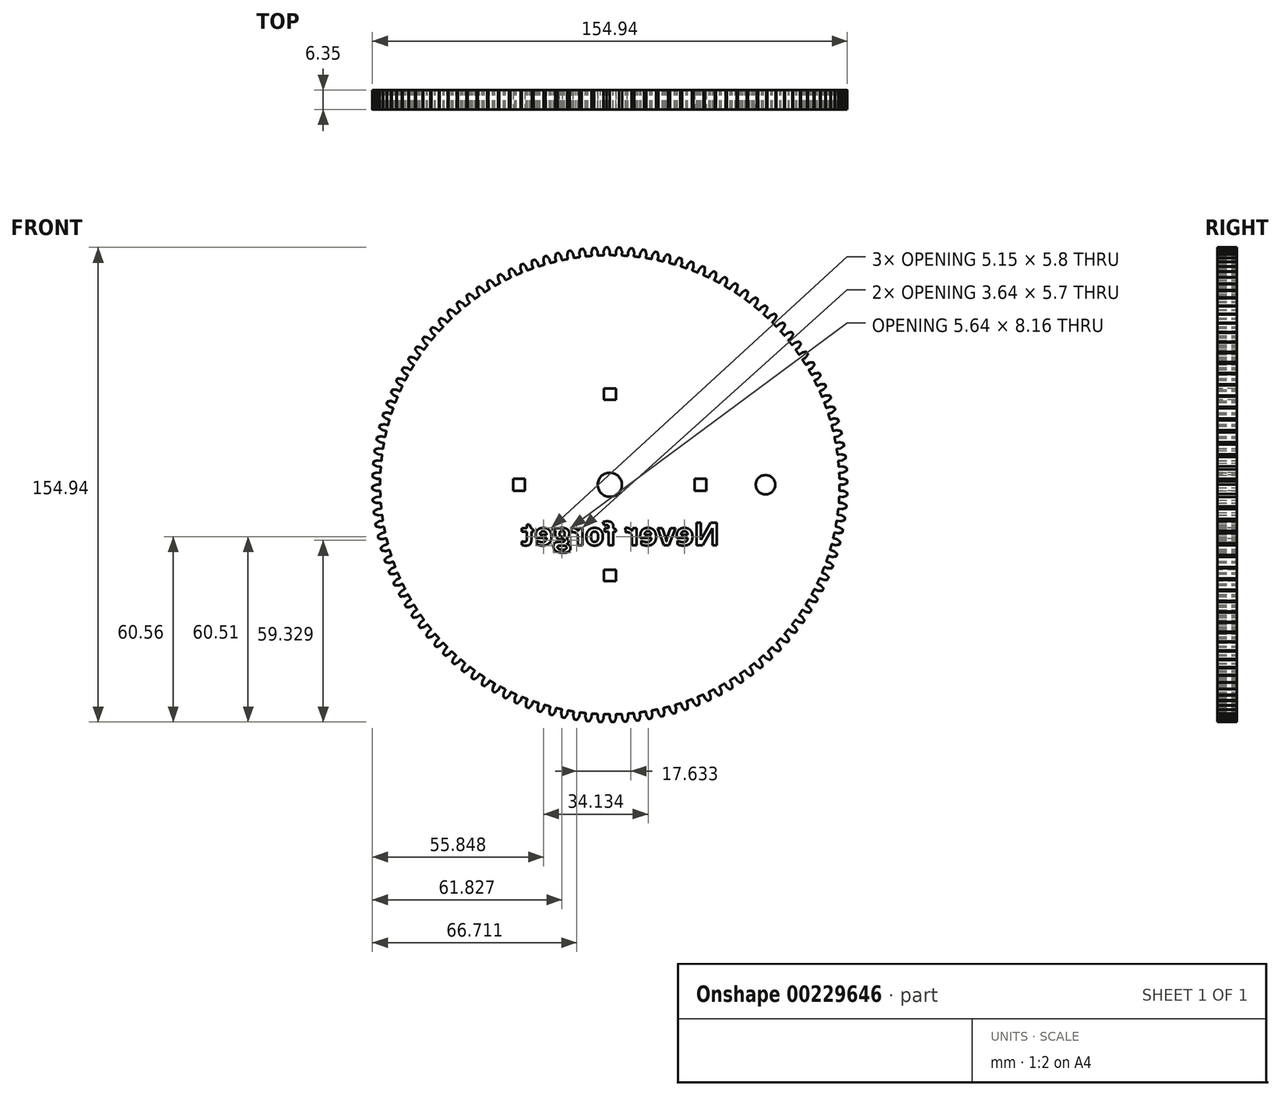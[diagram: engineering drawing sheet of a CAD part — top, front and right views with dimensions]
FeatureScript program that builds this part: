
annotation { "Feature Type Name" : "Feature", "Feature Type Description" : "" }
export const myFeature = defineFeature(function(context is Context, id is Id, definition is map)
    precondition{}
    {
        {
            var Q0;
            Q0=qCreatedBy(makeId("Front.planeOp"),FACE);
            var sketch = newSketch(context, id + "F0", { "sketchPlane" : qUnion([Q0])});
            skArc(sketch, "E0", {"start": v(-2.11, 74.9) * mm, "mid": v(-2.94, 74.87) * mm, "end": v(-3.77, 74.84) * mm});
            skArc(sketch, "E1.trimOffspring", {"start": v(-0.01, 76.23) * mm, "mid": v(-0.25, 76.8) * mm, "end": v(-0.5, 77.38) * mm});
            skLineSegment(sketch, "E2", {"start": v(-0.64, 77.47) * mm, "end": v(-1.01, 77.46) * mm});
            skLineSegment(sketch, "E3", {"start": v(0, 76.17) * mm, "end": v(0, 75.08) * mm});
            skLineSegment(sketch, "E4.MirrorCS", {"start": v(-1.39, 77.46) * mm, "end": v(-1.01, 77.46) * mm});
            skArc(sketch, "E5.MirrorCS", {"start": v(-1.99, 76.2) * mm, "mid": v(-1.77, 76.79) * mm, "end": v(-1.53, 77.37) * mm});
            skLineSegment(sketch, "E6.MirrorCS", {"start": v(-2, 76.15) * mm, "end": v(-1.97, 75.06) * mm});
            skPoint(sketch, "E7.visualSharp", {"position": v(-1.96, 74.9) * mm});
            skArc(sketch, "E8.filletArc", {"start": v(-2.11, 74.9) * mm, "mid": v(-2, 74.95) * mm, "end": v(-1.97, 75.06) * mm});
            skPoint(sketch, "E9.visualSharp", {"position": v(0, 74.93) * mm});
            skArc(sketch, "E9.filletArc", {"start": v(0, 75.08) * mm, "mid": v(0.04, 74.97) * mm, "end": v(0.15, 74.93) * mm});
            skPoint(sketch, "E10.visualSharp", {"position": v(0, 76.2) * mm});
            skArc(sketch, "E10.filletArc", {"start": v(0, 76.17) * mm, "mid": v(0, 76.2) * mm, "end": v(-0.01, 76.23) * mm});
            skPoint(sketch, "E11.visualSharp", {"position": v(-2, 76.17) * mm});
            skArc(sketch, "E11.filletArc", {"start": v(-1.99, 76.2) * mm, "mid": v(-2, 76.17) * mm, "end": v(-2, 76.15) * mm});
            skPoint(sketch, "E12.visualSharp", {"position": v(-1.49, 77.46) * mm});
            skArc(sketch, "E12.filletArc", {"start": v(-1.39, 77.46) * mm, "mid": v(-1.47, 77.43) * mm, "end": v(-1.53, 77.37) * mm});
            skPoint(sketch, "E13.visualSharp", {"position": v(-0.54, 77.47) * mm});
            skArc(sketch, "E13.filletArc", {"start": v(-0.5, 77.38) * mm, "mid": v(-0.56, 77.44) * mm, "end": v(-0.64, 77.47) * mm});
            skArc(sketch, "E14.1.0", {"start": v(-6.03, 74.69) * mm, "mid": v(-5.93, 74.74) * mm, "end": v(-5.9, 74.85) * mm});
            skLineSegment(sketch, "E14.1.1", {"start": v(-5.98, 75.94) * mm, "end": v(-5.9, 74.85) * mm});
            skArc(sketch, "E14.1.2", {"start": v(-5.97, 76) * mm, "mid": v(-5.78, 76.59) * mm, "end": v(-5.57, 77.18) * mm});
            skArc(sketch, "E14.1.3", {"start": v(-5.44, 77.28) * mm, "mid": v(-5.52, 77.25) * mm, "end": v(-5.57, 77.18) * mm});
            skLineSegment(sketch, "E14.1.4", {"start": v(-5.44, 77.28) * mm, "end": v(-5.07, 77.3) * mm});
            skLineSegment(sketch, "E14.1.5", {"start": v(-4.7, 77.33) * mm, "end": v(-5.07, 77.3) * mm});
            skArc(sketch, "E14.1.6", {"start": v(-4.55, 77.25) * mm, "mid": v(-4.6, 77.3) * mm, "end": v(-4.7, 77.33) * mm});
            skArc(sketch, "E14.1.7", {"start": v(-4, 76.12) * mm, "mid": v(-4.26, 76.69) * mm, "end": v(-4.55, 77.25) * mm});
            skLineSegment(sketch, "E14.1.8", {"start": v(-3.99, 76.07) * mm, "end": v(-3.93, 74.98) * mm});
            skArc(sketch, "E14.1.9", {"start": v(-3.93, 74.98) * mm, "mid": v(-3.88, 74.87) * mm, "end": v(-3.77, 74.84) * mm});
            skArc(sketch, "E14.2.0", {"start": v(-9.93, 74.27) * mm, "mid": v(-9.83, 74.33) * mm, "end": v(-9.8, 74.44) * mm});
            skLineSegment(sketch, "E14.2.1", {"start": v(-9.94, 75.52) * mm, "end": v(-9.8, 74.44) * mm});
            skArc(sketch, "E14.2.2", {"start": v(-9.94, 75.58) * mm, "mid": v(-9.78, 76.18) * mm, "end": v(-9.6, 76.78) * mm});
            skArc(sketch, "E14.2.3", {"start": v(-9.48, 76.89) * mm, "mid": v(-9.56, 76.85) * mm, "end": v(-9.6, 76.78) * mm});
            skLineSegment(sketch, "E14.2.4", {"start": v(-9.48, 76.89) * mm, "end": v(-9.1, 76.93) * mm});
            skLineSegment(sketch, "E14.2.5", {"start": v(-8.73, 76.98) * mm, "end": v(-9.1, 76.93) * mm});
            skArc(sketch, "E14.2.6", {"start": v(-8.59, 76.9) * mm, "mid": v(-8.65, 76.96) * mm, "end": v(-8.73, 76.98) * mm});
            skArc(sketch, "E14.2.7", {"start": v(-7.98, 75.8) * mm, "mid": v(-8.27, 76.36) * mm, "end": v(-8.59, 76.9) * mm});
            skLineSegment(sketch, "E14.2.8", {"start": v(-7.96, 75.75) * mm, "end": v(-7.85, 74.67) * mm});
            skArc(sketch, "E14.2.9", {"start": v(-7.85, 74.67) * mm, "mid": v(-7.8, 74.57) * mm, "end": v(-7.68, 74.54) * mm});
            skArc(sketch, "E14.3.0", {"start": v(-13.8, 73.65) * mm, "mid": v(-13.7, 73.71) * mm, "end": v(-13.68, 73.82) * mm});
            skLineSegment(sketch, "E14.3.1", {"start": v(-13.88, 74.9) * mm, "end": v(-13.68, 73.82) * mm});
            skArc(sketch, "E14.3.2", {"start": v(-13.88, 74.95) * mm, "mid": v(-13.76, 75.57) * mm, "end": v(-13.6, 76.17) * mm});
            skArc(sketch, "E14.3.3", {"start": v(-13.49, 76.29) * mm, "mid": v(-13.57, 76.25) * mm, "end": v(-13.6, 76.17) * mm});
            skLineSegment(sketch, "E14.3.4", {"start": v(-13.49, 76.29) * mm, "end": v(-13.12, 76.35) * mm});
            skLineSegment(sketch, "E14.3.5", {"start": v(-12.75, 76.41) * mm, "end": v(-13.12, 76.35) * mm});
            skArc(sketch, "E14.3.6", {"start": v(-12.6, 76.35) * mm, "mid": v(-12.66, 76.4) * mm, "end": v(-12.75, 76.41) * mm});
            skArc(sketch, "E14.3.7", {"start": v(-11.93, 75.29) * mm, "mid": v(-12.26, 75.82) * mm, "end": v(-12.6, 76.35) * mm});
            skLineSegment(sketch, "E14.3.8", {"start": v(-11.92, 75.23) * mm, "end": v(-11.75, 74.16) * mm});
            skArc(sketch, "E14.3.9", {"start": v(-11.75, 74.16) * mm, "mid": v(-11.68, 74.06) * mm, "end": v(-11.57, 74.03) * mm});
            skArc(sketch, "E14.4.0", {"start": v(-17.64, 72.82) * mm, "mid": v(-17.55, 72.9) * mm, "end": v(-17.53, 73) * mm});
            skLineSegment(sketch, "E14.4.1", {"start": v(-17.78, 74.07) * mm, "end": v(-17.53, 73) * mm});
            skArc(sketch, "E14.4.2", {"start": v(-17.78, 74.12) * mm, "mid": v(-17.7, 74.74) * mm, "end": v(-17.58, 75.36) * mm});
            skArc(sketch, "E14.4.3", {"start": v(-17.46, 75.48) * mm, "mid": v(-17.54, 75.43) * mm, "end": v(-17.58, 75.36) * mm});
            skLineSegment(sketch, "E14.4.4", {"start": v(-17.46, 75.48) * mm, "end": v(-17.1, 75.56) * mm});
            skLineSegment(sketch, "E14.4.5", {"start": v(-16.73, 75.64) * mm, "end": v(-17.1, 75.56) * mm});
            skArc(sketch, "E14.4.6", {"start": v(-16.58, 75.58) * mm, "mid": v(-16.65, 75.64) * mm, "end": v(-16.73, 75.64) * mm});
            skArc(sketch, "E14.4.7", {"start": v(-15.86, 74.56) * mm, "mid": v(-16.2, 75.08) * mm, "end": v(-16.58, 75.58) * mm});
            skLineSegment(sketch, "E14.4.8", {"start": v(-15.84, 74.5) * mm, "end": v(-15.61, 73.44) * mm});
            skArc(sketch, "E14.4.9", {"start": v(-15.61, 73.44) * mm, "mid": v(-15.54, 73.35) * mm, "end": v(-15.43, 73.32) * mm});
            skArc(sketch, "E14.5.0", {"start": v(-21.43, 71.8) * mm, "mid": v(-21.34, 71.87) * mm, "end": v(-21.32, 72) * mm});
            skLineSegment(sketch, "E14.5.1", {"start": v(-21.63, 73.03) * mm, "end": v(-21.32, 72) * mm});
            skArc(sketch, "E14.5.2", {"start": v(-21.64, 73.1) * mm, "mid": v(-21.58, 73.71) * mm, "end": v(-21.5, 74.33) * mm});
            skArc(sketch, "E14.5.3", {"start": v(-21.39, 74.46) * mm, "mid": v(-21.46, 74.41) * mm, "end": v(-21.5, 74.33) * mm});
            skLineSegment(sketch, "E14.5.4", {"start": v(-21.39, 74.46) * mm, "end": v(-21.03, 74.56) * mm});
            skLineSegment(sketch, "E14.5.5", {"start": v(-20.67, 74.66) * mm, "end": v(-21.03, 74.56) * mm});
            skArc(sketch, "E14.5.6", {"start": v(-20.5, 74.61) * mm, "mid": v(-20.58, 74.66) * mm, "end": v(-20.67, 74.66) * mm});
            skArc(sketch, "E14.5.7", {"start": v(-19.74, 73.63) * mm, "mid": v(-20.12, 74.13) * mm, "end": v(-20.5, 74.61) * mm});
            skLineSegment(sketch, "E14.5.8", {"start": v(-19.71, 73.58) * mm, "end": v(-19.43, 72.52) * mm});
            skArc(sketch, "E14.5.9", {"start": v(-19.43, 72.52) * mm, "mid": v(-19.36, 72.43) * mm, "end": v(-19.25, 72.42) * mm});
            skArc(sketch, "E14.6.0", {"start": v(-25.16, 70.58) * mm, "mid": v(-25.07, 70.66) * mm, "end": v(-25.06, 70.78) * mm});
            skLineSegment(sketch, "E14.6.1", {"start": v(-25.43, 71.8) * mm, "end": v(-25.06, 70.78) * mm});
            skArc(sketch, "E14.6.2", {"start": v(-25.44, 71.86) * mm, "mid": v(-25.4, 72.48) * mm, "end": v(-25.36, 73.1) * mm});
            skArc(sketch, "E14.6.3", {"start": v(-25.26, 73.24) * mm, "mid": v(-25.33, 73.19) * mm, "end": v(-25.36, 73.1) * mm});
            skLineSegment(sketch, "E14.6.4", {"start": v(-25.26, 73.24) * mm, "end": v(-24.9, 73.36) * mm});
            skLineSegment(sketch, "E14.6.5", {"start": v(-24.55, 73.48) * mm, "end": v(-24.9, 73.36) * mm});
            skArc(sketch, "E14.6.6", {"start": v(-24.39, 73.44) * mm, "mid": v(-24.46, 73.48) * mm, "end": v(-24.55, 73.48) * mm});
            skArc(sketch, "E14.6.7", {"start": v(-23.57, 72.5) * mm, "mid": v(-23.97, 72.97) * mm, "end": v(-24.39, 73.44) * mm});
            skLineSegment(sketch, "E14.6.8", {"start": v(-23.54, 72.44) * mm, "end": v(-23.2, 71.4) * mm});
            skArc(sketch, "E14.6.9", {"start": v(-23.2, 71.4) * mm, "mid": v(-23.13, 71.32) * mm, "end": v(-23, 71.3) * mm});
            skArc(sketch, "E14.7.0", {"start": v(-28.81, 69.17) * mm, "mid": v(-28.73, 69.25) * mm, "end": v(-28.73, 69.37) * mm});
            skLineSegment(sketch, "E14.7.1", {"start": v(-29.15, 70.37) * mm, "end": v(-28.73, 69.37) * mm});
            skArc(sketch, "E14.7.2", {"start": v(-29.16, 70.43) * mm, "mid": v(-29.17, 71.05) * mm, "end": v(-29.15, 71.68) * mm});
            skArc(sketch, "E14.7.3", {"start": v(-29.06, 71.82) * mm, "mid": v(-29.12, 71.76) * mm, "end": v(-29.15, 71.68) * mm});
            skLineSegment(sketch, "E14.7.4", {"start": v(-29.06, 71.82) * mm, "end": v(-28.7, 71.96) * mm});
            skLineSegment(sketch, "E14.7.5", {"start": v(-28.36, 72.1) * mm, "end": v(-28.7, 71.96) * mm});
            skArc(sketch, "E14.7.6", {"start": v(-28.2, 72.06) * mm, "mid": v(-28.27, 72.1) * mm, "end": v(-28.36, 72.1) * mm});
            skArc(sketch, "E14.7.7", {"start": v(-27.33, 71.16) * mm, "mid": v(-27.75, 71.62) * mm, "end": v(-28.2, 72.06) * mm});
            skLineSegment(sketch, "E14.7.8", {"start": v(-27.3, 71.11) * mm, "end": v(-26.9, 70.1) * mm});
            skArc(sketch, "E14.7.9", {"start": v(-26.9, 70.1) * mm, "mid": v(-26.83, 70.01) * mm, "end": v(-26.71, 70) * mm});
            skArc(sketch, "E14.8.0", {"start": v(-32.4, 67.57) * mm, "mid": v(-32.32, 67.65) * mm, "end": v(-32.32, 67.77) * mm});
            skLineSegment(sketch, "E14.8.1", {"start": v(-32.8, 68.75) * mm, "end": v(-32.32, 67.77) * mm});
            skArc(sketch, "E14.8.2", {"start": v(-32.8, 68.8) * mm, "mid": v(-32.84, 69.43) * mm, "end": v(-32.86, 70.06) * mm});
            skArc(sketch, "E14.8.3", {"start": v(-32.77, 70.2) * mm, "mid": v(-32.84, 70.14) * mm, "end": v(-32.86, 70.06) * mm});
            skLineSegment(sketch, "E14.8.4", {"start": v(-32.77, 70.2) * mm, "end": v(-32.43, 70.36) * mm});
            skLineSegment(sketch, "E14.8.5", {"start": v(-32.1, 70.51) * mm, "end": v(-32.43, 70.36) * mm});
            skArc(sketch, "E14.8.6", {"start": v(-31.93, 70.49) * mm, "mid": v(-32, 70.52) * mm, "end": v(-32.1, 70.51) * mm});
            skArc(sketch, "E14.8.7", {"start": v(-31.01, 69.63) * mm, "mid": v(-31.46, 70.07) * mm, "end": v(-31.93, 70.49) * mm});
            skLineSegment(sketch, "E14.8.8", {"start": v(-30.98, 69.59) * mm, "end": v(-30.54, 68.6) * mm});
            skArc(sketch, "E14.8.9", {"start": v(-30.54, 68.6) * mm, "mid": v(-30.45, 68.51) * mm, "end": v(-30.34, 68.51) * mm});
            skArc(sketch, "E14.9.0", {"start": v(-35.89, 65.78) * mm, "mid": v(-35.81, 65.87) * mm, "end": v(-35.83, 65.98) * mm});
            skLineSegment(sketch, "E14.9.1", {"start": v(-36.35, 66.94) * mm, "end": v(-35.83, 65.98) * mm});
            skArc(sketch, "E14.9.2", {"start": v(-36.36, 67) * mm, "mid": v(-36.43, 67.62) * mm, "end": v(-36.48, 68.24) * mm});
            skArc(sketch, "E14.9.3", {"start": v(-36.4, 68.38) * mm, "mid": v(-36.46, 68.32) * mm, "end": v(-36.48, 68.24) * mm});
            skLineSegment(sketch, "E14.9.4", {"start": v(-36.4, 68.38) * mm, "end": v(-36.07, 68.56) * mm});
            skLineSegment(sketch, "E14.9.5", {"start": v(-35.74, 68.73) * mm, "end": v(-36.07, 68.56) * mm});
            skArc(sketch, "E14.9.6", {"start": v(-35.57, 68.72) * mm, "mid": v(-35.65, 68.75) * mm, "end": v(-35.74, 68.73) * mm});
            skArc(sketch, "E14.9.7", {"start": v(-34.62, 67.91) * mm, "mid": v(-35.09, 68.32) * mm, "end": v(-35.57, 68.72) * mm});
            skLineSegment(sketch, "E14.9.8", {"start": v(-34.58, 67.87) * mm, "end": v(-34.09, 66.9) * mm});
            skArc(sketch, "E14.9.9", {"start": v(-34.09, 66.9) * mm, "mid": v(-34, 66.82) * mm, "end": v(-33.88, 66.83) * mm});
            skArc(sketch, "E14.10.0", {"start": v(-39.28, 63.8) * mm, "mid": v(-39.21, 63.9) * mm, "end": v(-39.23, 64.02) * mm});
            skLineSegment(sketch, "E14.10.1", {"start": v(-39.8, 64.95) * mm, "end": v(-39.23, 64.02) * mm});
            skArc(sketch, "E14.10.2", {"start": v(-39.82, 65) * mm, "mid": v(-39.92, 65.62) * mm, "end": v(-40, 66.24) * mm});
            skArc(sketch, "E14.10.3", {"start": v(-39.93, 66.39) * mm, "mid": v(-39.99, 66.32) * mm, "end": v(-40, 66.24) * mm});
            skLineSegment(sketch, "E14.10.4", {"start": v(-39.93, 66.39) * mm, "end": v(-39.61, 66.58) * mm});
            skLineSegment(sketch, "E14.10.5", {"start": v(-39.29, 66.77) * mm, "end": v(-39.61, 66.58) * mm});
            skArc(sketch, "E14.10.6", {"start": v(-39.12, 66.76) * mm, "mid": v(-39.2, 66.8) * mm, "end": v(-39.29, 66.77) * mm});
            skArc(sketch, "E14.10.7", {"start": v(-38.12, 66) * mm, "mid": v(-38.62, 66.4) * mm, "end": v(-39.12, 66.76) * mm});
            skLineSegment(sketch, "E14.10.8", {"start": v(-38.09, 65.97) * mm, "end": v(-37.54, 65.02) * mm});
            skArc(sketch, "E14.10.9", {"start": v(-37.54, 65.02) * mm, "mid": v(-37.45, 64.95) * mm, "end": v(-37.33, 64.97) * mm});
            skArc(sketch, "E14.11.0", {"start": v(-42.57, 61.67) * mm, "mid": v(-42.5, 61.76) * mm, "end": v(-42.53, 61.88) * mm});
            skLineSegment(sketch, "E14.11.1", {"start": v(-43.14, 62.78) * mm, "end": v(-42.53, 61.88) * mm});
            skArc(sketch, "E14.11.2", {"start": v(-43.17, 62.83) * mm, "mid": v(-43.3, 63.44) * mm, "end": v(-43.42, 64.05) * mm});
            skArc(sketch, "E14.11.3", {"start": v(-43.35, 64.2) * mm, "mid": v(-43.4, 64.14) * mm, "end": v(-43.42, 64.05) * mm});
            skLineSegment(sketch, "E14.11.4", {"start": v(-43.35, 64.2) * mm, "end": v(-43.04, 64.42) * mm});
            skLineSegment(sketch, "E14.11.5", {"start": v(-42.73, 64.62) * mm, "end": v(-43.04, 64.42) * mm});
            skArc(sketch, "E14.11.6", {"start": v(-42.56, 64.62) * mm, "mid": v(-42.65, 64.65) * mm, "end": v(-42.73, 64.62) * mm});
            skArc(sketch, "E14.11.7", {"start": v(-41.52, 63.92) * mm, "mid": v(-42.04, 64.28) * mm, "end": v(-42.56, 64.62) * mm});
            skLineSegment(sketch, "E14.11.8", {"start": v(-41.49, 63.88) * mm, "end": v(-40.9, 62.97) * mm});
            skArc(sketch, "E14.11.9", {"start": v(-40.9, 62.97) * mm, "mid": v(-40.8, 62.9) * mm, "end": v(-40.68, 62.92) * mm});
            skArc(sketch, "E14.12.0", {"start": v(-45.74, 59.35) * mm, "mid": v(-45.68, 59.45) * mm, "end": v(-45.7, 59.57) * mm});
            skLineSegment(sketch, "E14.12.1", {"start": v(-46.37, 60.43) * mm, "end": v(-45.7, 59.57) * mm});
            skArc(sketch, "E14.12.2", {"start": v(-46.4, 60.48) * mm, "mid": v(-46.56, 61.08) * mm, "end": v(-46.7, 61.7) * mm});
            skArc(sketch, "E14.12.3", {"start": v(-46.65, 61.85) * mm, "mid": v(-46.7, 61.78) * mm, "end": v(-46.7, 61.7) * mm});
            skLineSegment(sketch, "E14.12.4", {"start": v(-46.65, 61.85) * mm, "end": v(-46.35, 62.07) * mm});
            skLineSegment(sketch, "E14.12.5", {"start": v(-46.05, 62.3) * mm, "end": v(-46.35, 62.07) * mm});
            skArc(sketch, "E14.12.6", {"start": v(-45.89, 62.3) * mm, "mid": v(-45.97, 62.33) * mm, "end": v(-46.05, 62.3) * mm});
            skArc(sketch, "E14.12.7", {"start": v(-44.81, 61.66) * mm, "mid": v(-45.34, 62) * mm, "end": v(-45.89, 62.3) * mm});
            skLineSegment(sketch, "E14.12.8", {"start": v(-44.77, 61.62) * mm, "end": v(-44.13, 60.74) * mm});
            skArc(sketch, "E14.12.9", {"start": v(-44.13, 60.74) * mm, "mid": v(-44.03, 60.68) * mm, "end": v(-43.92, 60.7) * mm});
            skArc(sketch, "E14.13.0", {"start": v(-48.78, 56.88) * mm, "mid": v(-48.73, 56.98) * mm, "end": v(-48.76, 57.1) * mm});
            skLineSegment(sketch, "E14.13.1", {"start": v(-49.47, 57.92) * mm, "end": v(-48.76, 57.1) * mm});
            skArc(sketch, "E14.13.2", {"start": v(-49.5, 57.97) * mm, "mid": v(-49.7, 58.56) * mm, "end": v(-49.87, 59.16) * mm});
            skArc(sketch, "E14.13.3", {"start": v(-49.83, 59.32) * mm, "mid": v(-49.87, 59.25) * mm, "end": v(-49.87, 59.16) * mm});
            skLineSegment(sketch, "E14.13.4", {"start": v(-49.83, 59.32) * mm, "end": v(-49.54, 59.56) * mm});
            skLineSegment(sketch, "E14.13.5", {"start": v(-49.25, 59.8) * mm, "end": v(-49.54, 59.56) * mm});
            skArc(sketch, "E14.13.6", {"start": v(-49.08, 59.82) * mm, "mid": v(-49.17, 59.84) * mm, "end": v(-49.25, 59.8) * mm});
            skArc(sketch, "E14.13.7", {"start": v(-47.98, 59.23) * mm, "mid": v(-48.53, 59.54) * mm, "end": v(-49.08, 59.82) * mm});
            skLineSegment(sketch, "E14.13.8", {"start": v(-47.94, 59.2) * mm, "end": v(-47.25, 58.35) * mm});
            skArc(sketch, "E14.13.9", {"start": v(-47.25, 58.35) * mm, "mid": v(-47.15, 58.3) * mm, "end": v(-47.04, 58.33) * mm});
            skArc(sketch, "E14.14.0", {"start": v(-51.69, 54.25) * mm, "mid": v(-51.64, 54.35) * mm, "end": v(-51.68, 54.46) * mm});
            skLineSegment(sketch, "E14.14.1", {"start": v(-52.43, 55.25) * mm, "end": v(-51.68, 54.46) * mm});
            skArc(sketch, "E14.14.2", {"start": v(-52.46, 55.3) * mm, "mid": v(-52.7, 55.88) * mm, "end": v(-52.9, 56.47) * mm});
            skArc(sketch, "E14.14.3", {"start": v(-52.86, 56.63) * mm, "mid": v(-52.9, 56.56) * mm, "end": v(-52.9, 56.47) * mm});
            skLineSegment(sketch, "E14.14.4", {"start": v(-52.86, 56.63) * mm, "end": v(-52.59, 56.89) * mm});
            skLineSegment(sketch, "E14.14.5", {"start": v(-52.31, 57.14) * mm, "end": v(-52.59, 56.89) * mm});
            skArc(sketch, "E14.14.6", {"start": v(-52.15, 57.17) * mm, "mid": v(-52.23, 57.18) * mm, "end": v(-52.31, 57.14) * mm});
            skArc(sketch, "E14.14.7", {"start": v(-51.01, 56.64) * mm, "mid": v(-51.58, 56.91) * mm, "end": v(-52.15, 57.17) * mm});
            skLineSegment(sketch, "E14.14.8", {"start": v(-50.97, 56.6) * mm, "end": v(-50.24, 55.8) * mm});
            skArc(sketch, "E14.14.9", {"start": v(-50.24, 55.8) * mm, "mid": v(-50.13, 55.75) * mm, "end": v(-50.02, 55.79) * mm});
            skArc(sketch, "E14.15.0", {"start": v(-54.46, 51.47) * mm, "mid": v(-54.42, 51.58) * mm, "end": v(-54.46, 51.68) * mm});
            skLineSegment(sketch, "E14.15.1", {"start": v(-55.25, 52.43) * mm, "end": v(-54.46, 51.68) * mm});
            skArc(sketch, "E14.15.2", {"start": v(-55.29, 52.48) * mm, "mid": v(-55.54, 53.05) * mm, "end": v(-55.78, 53.63) * mm});
            skArc(sketch, "E14.15.3", {"start": v(-55.75, 53.79) * mm, "mid": v(-55.8, 53.71) * mm, "end": v(-55.78, 53.63) * mm});
            skLineSegment(sketch, "E14.15.4", {"start": v(-55.75, 53.79) * mm, "end": v(-55.5, 54.06) * mm});
            skLineSegment(sketch, "E14.15.5", {"start": v(-55.23, 54.33) * mm, "end": v(-55.5, 54.06) * mm});
            skArc(sketch, "E14.15.6", {"start": v(-55.07, 54.36) * mm, "mid": v(-55.15, 54.37) * mm, "end": v(-55.23, 54.33) * mm});
            skArc(sketch, "E14.15.7", {"start": v(-53.9, 53.9) * mm, "mid": v(-54.48, 54.14) * mm, "end": v(-55.07, 54.36) * mm});
            skLineSegment(sketch, "E14.15.8", {"start": v(-53.86, 53.86) * mm, "end": v(-53.1, 53.1) * mm});
            skArc(sketch, "E14.15.9", {"start": v(-53.1, 53.1) * mm, "mid": v(-52.98, 53.05) * mm, "end": v(-52.88, 53.1) * mm});
            skArc(sketch, "E14.16.0", {"start": v(-57.08, 48.55) * mm, "mid": v(-57.04, 48.66) * mm, "end": v(-57.1, 48.76) * mm});
            skLineSegment(sketch, "E14.16.1", {"start": v(-57.92, 49.47) * mm, "end": v(-57.1, 48.76) * mm});
            skArc(sketch, "E14.16.2", {"start": v(-57.96, 49.51) * mm, "mid": v(-58.25, 50.07) * mm, "end": v(-58.52, 50.63) * mm});
            skArc(sketch, "E14.16.3", {"start": v(-58.5, 50.8) * mm, "mid": v(-58.53, 50.72) * mm, "end": v(-58.52, 50.63) * mm});
            skLineSegment(sketch, "E14.16.4", {"start": v(-58.5, 50.8) * mm, "end": v(-58.25, 51.08) * mm});
            skLineSegment(sketch, "E14.16.5", {"start": v(-58, 51.36) * mm, "end": v(-58.25, 51.08) * mm});
            skArc(sketch, "E14.16.6", {"start": v(-57.84, 51.4) * mm, "mid": v(-57.92, 51.4) * mm, "end": v(-58, 51.36) * mm});
            skArc(sketch, "E14.16.7", {"start": v(-56.65, 51) * mm, "mid": v(-57.24, 51.21) * mm, "end": v(-57.84, 51.4) * mm});
            skLineSegment(sketch, "E14.16.8", {"start": v(-56.6, 50.97) * mm, "end": v(-55.8, 50.24) * mm});
            skArc(sketch, "E14.16.9", {"start": v(-55.8, 50.24) * mm, "mid": v(-55.69, 50.2) * mm, "end": v(-55.58, 50.25) * mm});
            skArc(sketch, "E14.17.0", {"start": v(-59.54, 45.5) * mm, "mid": v(-59.5, 45.6) * mm, "end": v(-59.57, 45.7) * mm});
            skLineSegment(sketch, "E14.17.1", {"start": v(-60.43, 46.37) * mm, "end": v(-59.57, 45.7) * mm});
            skArc(sketch, "E14.17.2", {"start": v(-60.47, 46.41) * mm, "mid": v(-60.79, 46.95) * mm, "end": v(-61.08, 47.5) * mm});
            skArc(sketch, "E14.17.3", {"start": v(-61.07, 47.67) * mm, "mid": v(-61.1, 47.59) * mm, "end": v(-61.08, 47.5) * mm});
            skLineSegment(sketch, "E14.17.4", {"start": v(-61.07, 47.67) * mm, "end": v(-60.84, 47.96) * mm});
            skLineSegment(sketch, "E14.17.5", {"start": v(-60.6, 48.26) * mm, "end": v(-60.84, 47.96) * mm});
            skArc(sketch, "E14.17.6", {"start": v(-60.45, 48.3) * mm, "mid": v(-60.54, 48.3) * mm, "end": v(-60.6, 48.26) * mm});
            skArc(sketch, "E14.17.7", {"start": v(-59.25, 47.96) * mm, "mid": v(-59.84, 48.15) * mm, "end": v(-60.45, 48.3) * mm});
            skLineSegment(sketch, "E14.17.8", {"start": v(-59.2, 47.94) * mm, "end": v(-58.35, 47.25) * mm});
            skArc(sketch, "E14.17.9", {"start": v(-58.35, 47.25) * mm, "mid": v(-58.24, 47.22) * mm, "end": v(-58.14, 47.27) * mm});
            skArc(sketch, "E14.18.0", {"start": v(-61.84, 42.32) * mm, "mid": v(-61.81, 42.43) * mm, "end": v(-61.88, 42.53) * mm});
            skLineSegment(sketch, "E14.18.1", {"start": v(-62.78, 43.14) * mm, "end": v(-61.88, 42.53) * mm});
            skArc(sketch, "E14.18.2", {"start": v(-62.81, 43.18) * mm, "mid": v(-63.16, 43.7) * mm, "end": v(-63.49, 44.24) * mm});
            skArc(sketch, "E14.18.3", {"start": v(-63.48, 44.4) * mm, "mid": v(-63.5, 44.32) * mm, "end": v(-63.49, 44.24) * mm});
            skLineSegment(sketch, "E14.18.4", {"start": v(-63.48, 44.4) * mm, "end": v(-63.27, 44.71) * mm});
            skLineSegment(sketch, "E14.18.5", {"start": v(-63.05, 45.02) * mm, "end": v(-63.27, 44.71) * mm});
            skArc(sketch, "E14.18.6", {"start": v(-62.9, 45.08) * mm, "mid": v(-62.98, 45.07) * mm, "end": v(-63.05, 45.02) * mm});
            skArc(sketch, "E14.18.7", {"start": v(-61.67, 44.8) * mm, "mid": v(-62.28, 44.95) * mm, "end": v(-62.9, 45.08) * mm});
            skLineSegment(sketch, "E14.18.8", {"start": v(-61.62, 44.77) * mm, "end": v(-60.74, 44.13) * mm});
            skArc(sketch, "E14.18.9", {"start": v(-60.74, 44.13) * mm, "mid": v(-60.63, 44.1) * mm, "end": v(-60.53, 44.17) * mm});
            skArc(sketch, "E14.19.0", {"start": v(-63.97, 39.02) * mm, "mid": v(-63.95, 39.14) * mm, "end": v(-64.02, 39.23) * mm});
            skLineSegment(sketch, "E14.19.1", {"start": v(-64.95, 39.8) * mm, "end": v(-64.02, 39.23) * mm});
            skArc(sketch, "E14.19.2", {"start": v(-64.99, 39.84) * mm, "mid": v(-65.36, 40.34) * mm, "end": v(-65.72, 40.86) * mm});
            skArc(sketch, "E14.19.3", {"start": v(-65.72, 41.02) * mm, "mid": v(-65.74, 40.94) * mm, "end": v(-65.72, 40.86) * mm});
            skLineSegment(sketch, "E14.19.4", {"start": v(-65.72, 41.02) * mm, "end": v(-65.52, 41.34) * mm});
            skLineSegment(sketch, "E14.19.5", {"start": v(-65.32, 41.66) * mm, "end": v(-65.52, 41.34) * mm});
            skArc(sketch, "E14.19.6", {"start": v(-65.17, 41.72) * mm, "mid": v(-65.25, 41.71) * mm, "end": v(-65.32, 41.66) * mm});
            skArc(sketch, "E14.19.7", {"start": v(-63.93, 41.5) * mm, "mid": v(-64.55, 41.63) * mm, "end": v(-65.17, 41.72) * mm});
            skLineSegment(sketch, "E14.19.8", {"start": v(-63.88, 41.49) * mm, "end": v(-62.97, 40.9) * mm});
            skArc(sketch, "E14.19.9", {"start": v(-62.97, 40.9) * mm, "mid": v(-62.85, 40.87) * mm, "end": v(-62.76, 40.94) * mm});
            skArc(sketch, "E14.20.0", {"start": v(-65.92, 35.62) * mm, "mid": v(-65.91, 35.74) * mm, "end": v(-65.98, 35.83) * mm});
            skLineSegment(sketch, "E14.20.1", {"start": v(-66.94, 36.35) * mm, "end": v(-65.98, 35.83) * mm});
            skArc(sketch, "E14.20.2", {"start": v(-66.98, 36.38) * mm, "mid": v(-67.38, 36.86) * mm, "end": v(-67.76, 37.36) * mm});
            skArc(sketch, "E14.20.3", {"start": v(-67.77, 37.53) * mm, "mid": v(-67.8, 37.44) * mm, "end": v(-67.76, 37.36) * mm});
            skLineSegment(sketch, "E14.20.4", {"start": v(-67.77, 37.53) * mm, "end": v(-67.6, 37.85) * mm});
            skLineSegment(sketch, "E14.20.5", {"start": v(-67.4, 38.18) * mm, "end": v(-67.6, 37.85) * mm});
            skArc(sketch, "E14.20.6", {"start": v(-67.26, 38.26) * mm, "mid": v(-67.35, 38.24) * mm, "end": v(-67.4, 38.18) * mm});
            skArc(sketch, "E14.20.7", {"start": v(-66.02, 38.1) * mm, "mid": v(-66.64, 38.2) * mm, "end": v(-67.26, 38.26) * mm});
            skLineSegment(sketch, "E14.20.8", {"start": v(-65.97, 38.09) * mm, "end": v(-65.02, 37.54) * mm});
            skArc(sketch, "E14.20.9", {"start": v(-65.02, 37.54) * mm, "mid": v(-64.9, 37.53) * mm, "end": v(-64.82, 37.6) * mm});
            skArc(sketch, "E14.21.0", {"start": v(-67.7, 32.12) * mm, "mid": v(-67.7, 32.24) * mm, "end": v(-67.77, 32.32) * mm});
            skLineSegment(sketch, "E14.21.1", {"start": v(-68.75, 32.8) * mm, "end": v(-67.77, 32.32) * mm});
            skArc(sketch, "E14.21.2", {"start": v(-68.8, 32.83) * mm, "mid": v(-69.22, 33.29) * mm, "end": v(-69.63, 33.76) * mm});
            skArc(sketch, "E14.21.3", {"start": v(-69.65, 33.93) * mm, "mid": v(-69.66, 33.84) * mm, "end": v(-69.63, 33.76) * mm});
            skLineSegment(sketch, "E14.21.4", {"start": v(-69.65, 33.93) * mm, "end": v(-69.48, 34.26) * mm});
            skLineSegment(sketch, "E14.21.5", {"start": v(-69.31, 34.6) * mm, "end": v(-69.48, 34.26) * mm});
            skArc(sketch, "E14.21.6", {"start": v(-69.17, 34.68) * mm, "mid": v(-69.26, 34.66) * mm, "end": v(-69.31, 34.6) * mm});
            skArc(sketch, "E14.21.7", {"start": v(-67.92, 34.6) * mm, "mid": v(-68.55, 34.65) * mm, "end": v(-69.17, 34.68) * mm});
            skLineSegment(sketch, "E14.21.8", {"start": v(-67.87, 34.58) * mm, "end": v(-66.9, 34.09) * mm});
            skArc(sketch, "E14.21.9", {"start": v(-66.9, 34.09) * mm, "mid": v(-66.78, 34.08) * mm, "end": v(-66.7, 34.15) * mm});
            skArc(sketch, "E14.22.0", {"start": v(-69.28, 28.53) * mm, "mid": v(-69.28, 28.65) * mm, "end": v(-69.37, 28.73) * mm});
            skLineSegment(sketch, "E14.22.1", {"start": v(-70.37, 29.15) * mm, "end": v(-69.37, 28.73) * mm});
            skArc(sketch, "E14.22.2", {"start": v(-70.42, 29.18) * mm, "mid": v(-70.87, 29.62) * mm, "end": v(-71.3, 30.07) * mm});
            skArc(sketch, "E14.22.3", {"start": v(-71.33, 30.24) * mm, "mid": v(-71.34, 30.15) * mm, "end": v(-71.3, 30.07) * mm});
            skLineSegment(sketch, "E14.22.4", {"start": v(-71.33, 30.24) * mm, "end": v(-71.18, 30.58) * mm});
            skLineSegment(sketch, "E14.22.5", {"start": v(-71.03, 30.93) * mm, "end": v(-71.18, 30.58) * mm});
            skArc(sketch, "E14.22.6", {"start": v(-70.9, 31.02) * mm, "mid": v(-70.97, 31) * mm, "end": v(-71.03, 30.93) * mm});
            skArc(sketch, "E14.22.7", {"start": v(-69.64, 31) * mm, "mid": v(-70.27, 31.02) * mm, "end": v(-70.9, 31.02) * mm});
            skLineSegment(sketch, "E14.22.8", {"start": v(-69.59, 30.98) * mm, "end": v(-68.6, 30.54) * mm});
            skArc(sketch, "E14.22.9", {"start": v(-68.6, 30.54) * mm, "mid": v(-68.47, 30.54) * mm, "end": v(-68.39, 30.62) * mm});
            skArc(sketch, "E14.23.0", {"start": v(-70.68, 24.87) * mm, "mid": v(-70.69, 24.99) * mm, "end": v(-70.78, 25.06) * mm});
            skLineSegment(sketch, "E14.23.1", {"start": v(-71.8, 25.43) * mm, "end": v(-70.78, 25.06) * mm});
            skArc(sketch, "E14.23.2", {"start": v(-71.85, 25.45) * mm, "mid": v(-72.32, 25.87) * mm, "end": v(-72.77, 26.3) * mm});
            skArc(sketch, "E14.23.3", {"start": v(-72.81, 26.46) * mm, "mid": v(-72.82, 26.38) * mm, "end": v(-72.77, 26.3) * mm});
            skLineSegment(sketch, "E14.23.4", {"start": v(-72.81, 26.46) * mm, "end": v(-72.68, 26.81) * mm});
            skLineSegment(sketch, "E14.23.5", {"start": v(-72.55, 27.17) * mm, "end": v(-72.68, 26.81) * mm});
            skArc(sketch, "E14.23.6", {"start": v(-72.42, 27.26) * mm, "mid": v(-72.5, 27.23) * mm, "end": v(-72.55, 27.17) * mm});
            skArc(sketch, "E14.23.7", {"start": v(-71.17, 27.3) * mm, "mid": v(-71.8, 27.3) * mm, "end": v(-72.42, 27.26) * mm});
            skLineSegment(sketch, "E14.23.8", {"start": v(-71.11, 27.3) * mm, "end": v(-70.1, 26.9) * mm});
            skArc(sketch, "E14.23.9", {"start": v(-70.1, 26.9) * mm, "mid": v(-69.98, 26.91) * mm, "end": v(-69.9, 27) * mm});
            skArc(sketch, "E14.24.0", {"start": v(-71.89, 21.14) * mm, "mid": v(-71.9, 21.25) * mm, "end": v(-72, 21.32) * mm});
            skLineSegment(sketch, "E14.24.1", {"start": v(-73.03, 21.63) * mm, "end": v(-72, 21.32) * mm});
            skArc(sketch, "E14.24.2", {"start": v(-73.08, 21.66) * mm, "mid": v(-73.57, 22.05) * mm, "end": v(-74.05, 22.46) * mm});
            skArc(sketch, "E14.24.3", {"start": v(-74.1, 22.61) * mm, "mid": v(-74.1, 22.53) * mm, "end": v(-74.05, 22.46) * mm});
            skLineSegment(sketch, "E14.24.4", {"start": v(-74.1, 22.61) * mm, "end": v(-73.99, 22.97) * mm});
            skLineSegment(sketch, "E14.24.5", {"start": v(-73.87, 23.33) * mm, "end": v(-73.99, 22.97) * mm});
            skArc(sketch, "E14.24.6", {"start": v(-73.75, 23.44) * mm, "mid": v(-73.83, 23.4) * mm, "end": v(-73.87, 23.33) * mm});
            skArc(sketch, "E14.24.7", {"start": v(-72.5, 23.55) * mm, "mid": v(-73.12, 23.5) * mm, "end": v(-73.75, 23.44) * mm});
            skLineSegment(sketch, "E14.24.8", {"start": v(-72.44, 23.54) * mm, "end": v(-71.4, 23.2) * mm});
            skArc(sketch, "E14.24.9", {"start": v(-71.4, 23.2) * mm, "mid": v(-71.3, 23.21) * mm, "end": v(-71.22, 23.3) * mm});
            skArc(sketch, "E14.25.0", {"start": v(-72.9, 17.34) * mm, "mid": v(-72.91, 17.46) * mm, "end": v(-73, 17.53) * mm});
            skLineSegment(sketch, "E14.25.1", {"start": v(-74.07, 17.78) * mm, "end": v(-73, 17.53) * mm});
            skArc(sketch, "E14.25.2", {"start": v(-74.12, 17.8) * mm, "mid": v(-74.63, 18.17) * mm, "end": v(-75.12, 18.55) * mm});
            skArc(sketch, "E14.25.3", {"start": v(-75.18, 18.7) * mm, "mid": v(-75.17, 18.62) * mm, "end": v(-75.12, 18.55) * mm});
            skLineSegment(sketch, "E14.25.4", {"start": v(-75.18, 18.7) * mm, "end": v(-75.09, 19.07) * mm});
            skLineSegment(sketch, "E14.25.5", {"start": v(-75, 19.43) * mm, "end": v(-75.09, 19.07) * mm});
            skArc(sketch, "E14.25.6", {"start": v(-74.87, 19.54) * mm, "mid": v(-74.95, 19.5) * mm, "end": v(-75, 19.43) * mm});
            skArc(sketch, "E14.25.7", {"start": v(-73.63, 19.72) * mm, "mid": v(-74.25, 19.64) * mm, "end": v(-74.87, 19.54) * mm});
            skLineSegment(sketch, "E14.25.8", {"start": v(-73.58, 19.71) * mm, "end": v(-72.52, 19.43) * mm});
            skArc(sketch, "E14.25.9", {"start": v(-72.52, 19.43) * mm, "mid": v(-72.4, 19.45) * mm, "end": v(-72.34, 19.54) * mm});
            skArc(sketch, "E14.26.0", {"start": v(-73.7, 13.5) * mm, "mid": v(-73.73, 13.62) * mm, "end": v(-73.82, 13.68) * mm});
            skLineSegment(sketch, "E14.26.1", {"start": v(-74.9, 13.88) * mm, "end": v(-73.82, 13.68) * mm});
            skArc(sketch, "E14.26.2", {"start": v(-74.95, 13.9) * mm, "mid": v(-75.48, 14.24) * mm, "end": v(-76, 14.6) * mm});
            skArc(sketch, "E14.26.3", {"start": v(-76.05, 14.75) * mm, "mid": v(-76.05, 14.66) * mm, "end": v(-76, 14.6) * mm});
            skLineSegment(sketch, "E14.26.4", {"start": v(-76.05, 14.75) * mm, "end": v(-75.98, 15.11) * mm});
            skLineSegment(sketch, "E14.26.5", {"start": v(-75.9, 15.48) * mm, "end": v(-75.98, 15.11) * mm});
            skArc(sketch, "E14.26.6", {"start": v(-75.8, 15.6) * mm, "mid": v(-75.87, 15.56) * mm, "end": v(-75.9, 15.48) * mm});
            skArc(sketch, "E14.26.7", {"start": v(-74.56, 15.84) * mm, "mid": v(-75.18, 15.73) * mm, "end": v(-75.8, 15.6) * mm});
            skLineSegment(sketch, "E14.26.8", {"start": v(-74.5, 15.84) * mm, "end": v(-73.44, 15.61) * mm});
            skArc(sketch, "E14.26.9", {"start": v(-73.44, 15.61) * mm, "mid": v(-73.33, 15.63) * mm, "end": v(-73.26, 15.73) * mm});
            skArc(sketch, "E14.27.0", {"start": v(-74.3, 9.63) * mm, "mid": v(-74.34, 9.74) * mm, "end": v(-74.44, 9.8) * mm});
            skLineSegment(sketch, "E14.27.1", {"start": v(-75.52, 9.94) * mm, "end": v(-74.44, 9.8) * mm});
            skArc(sketch, "E14.27.2", {"start": v(-75.57, 9.96) * mm, "mid": v(-76.12, 10.27) * mm, "end": v(-76.65, 10.6) * mm});
            skArc(sketch, "E14.27.3", {"start": v(-76.72, 10.74) * mm, "mid": v(-76.7, 10.66) * mm, "end": v(-76.65, 10.6) * mm});
            skLineSegment(sketch, "E14.27.4", {"start": v(-76.72, 10.74) * mm, "end": v(-76.67, 11.12) * mm});
            skLineSegment(sketch, "E14.27.5", {"start": v(-76.61, 11.49) * mm, "end": v(-76.67, 11.12) * mm});
            skArc(sketch, "E14.27.6", {"start": v(-76.5, 11.61) * mm, "mid": v(-76.58, 11.57) * mm, "end": v(-76.61, 11.49) * mm});
            skArc(sketch, "E14.27.7", {"start": v(-75.29, 11.91) * mm, "mid": v(-75.9, 11.77) * mm, "end": v(-76.5, 11.61) * mm});
            skLineSegment(sketch, "E14.27.8", {"start": v(-75.23, 11.92) * mm, "end": v(-74.16, 11.75) * mm});
            skArc(sketch, "E14.27.9", {"start": v(-74.16, 11.75) * mm, "mid": v(-74.04, 11.77) * mm, "end": v(-73.98, 11.87) * mm});
            skArc(sketch, "E14.28.0", {"start": v(-74.71, 5.73) * mm, "mid": v(-74.75, 5.84) * mm, "end": v(-74.85, 5.9) * mm});
            skLineSegment(sketch, "E14.28.1", {"start": v(-75.94, 5.98) * mm, "end": v(-74.85, 5.9) * mm});
            skArc(sketch, "E14.28.2", {"start": v(-76, 6) * mm, "mid": v(-76.55, 6.27) * mm, "end": v(-77.1, 6.57) * mm});
            skArc(sketch, "E14.28.3", {"start": v(-77.18, 6.71) * mm, "mid": v(-77.16, 6.63) * mm, "end": v(-77.1, 6.57) * mm});
            skLineSegment(sketch, "E14.28.4", {"start": v(-77.18, 6.71) * mm, "end": v(-77.15, 7.09) * mm});
            skLineSegment(sketch, "E14.28.5", {"start": v(-77.1, 7.46) * mm, "end": v(-77.15, 7.09) * mm});
            skArc(sketch, "E14.28.6", {"start": v(-77, 7.6) * mm, "mid": v(-77.08, 7.54) * mm, "end": v(-77.1, 7.46) * mm});
            skArc(sketch, "E14.28.7", {"start": v(-75.81, 7.96) * mm, "mid": v(-76.41, 7.78) * mm, "end": v(-77, 7.6) * mm});
            skLineSegment(sketch, "E14.28.8", {"start": v(-75.75, 7.96) * mm, "end": v(-74.67, 7.85) * mm});
            skArc(sketch, "E14.28.9", {"start": v(-74.67, 7.85) * mm, "mid": v(-74.56, 7.88) * mm, "end": v(-74.5, 7.98) * mm});
            skArc(sketch, "E14.29.0", {"start": v(-74.9, 1.8) * mm, "mid": v(-74.95, 1.92) * mm, "end": v(-75.06, 1.97) * mm});
            skLineSegment(sketch, "E14.29.1", {"start": v(-76.15, 2) * mm, "end": v(-75.06, 1.97) * mm});
            skArc(sketch, "E14.29.2", {"start": v(-76.2, 2) * mm, "mid": v(-76.77, 2.26) * mm, "end": v(-77.34, 2.52) * mm});
            skArc(sketch, "E14.29.3", {"start": v(-77.42, 2.67) * mm, "mid": v(-77.4, 2.58) * mm, "end": v(-77.34, 2.52) * mm});
            skLineSegment(sketch, "E14.29.4", {"start": v(-77.42, 2.67) * mm, "end": v(-77.41, 3.04) * mm});
            skLineSegment(sketch, "E14.29.5", {"start": v(-77.4, 3.42) * mm, "end": v(-77.41, 3.04) * mm});
            skArc(sketch, "E14.29.6", {"start": v(-77.3, 3.55) * mm, "mid": v(-77.37, 3.5) * mm, "end": v(-77.4, 3.42) * mm});
            skArc(sketch, "E14.29.7", {"start": v(-76.12, 3.98) * mm, "mid": v(-76.71, 3.77) * mm, "end": v(-77.3, 3.55) * mm});
            skLineSegment(sketch, "E14.29.8", {"start": v(-76.07, 3.99) * mm, "end": v(-74.98, 3.93) * mm});
            skArc(sketch, "E14.29.9", {"start": v(-74.98, 3.93) * mm, "mid": v(-74.87, 3.97) * mm, "end": v(-74.82, 4.07) * mm});
            skArc(sketch, "E14.30.0", {"start": v(-74.9, -2.11) * mm, "mid": v(-74.95, -2) * mm, "end": v(-75.06, -1.97) * mm});
            skLineSegment(sketch, "E14.30.1", {"start": v(-76.15, -2) * mm, "end": v(-75.06, -1.97) * mm});
            skArc(sketch, "E14.30.2", {"start": v(-76.2, -1.99) * mm, "mid": v(-76.79, -1.77) * mm, "end": v(-77.37, -1.53) * mm});
            skArc(sketch, "E14.30.3", {"start": v(-77.46, -1.39) * mm, "mid": v(-77.43, -1.47) * mm, "end": v(-77.37, -1.53) * mm});
            skLineSegment(sketch, "E14.30.4", {"start": v(-77.46, -1.39) * mm, "end": v(-77.46, -1.01) * mm});
            skLineSegment(sketch, "E14.30.5", {"start": v(-77.47, -0.64) * mm, "end": v(-77.46, -1.01) * mm});
            skArc(sketch, "E14.30.6", {"start": v(-77.38, -0.5) * mm, "mid": v(-77.44, -0.56) * mm, "end": v(-77.47, -0.64) * mm});
            skArc(sketch, "E14.30.7", {"start": v(-76.23, -0.01) * mm, "mid": v(-76.8, -0.25) * mm, "end": v(-77.38, -0.5) * mm});
            skLineSegment(sketch, "E14.30.8", {"start": v(-76.17, 0) * mm, "end": v(-75.08, 0) * mm});
            skArc(sketch, "E14.30.9", {"start": v(-75.08, 0) * mm, "mid": v(-74.97, 0.04) * mm, "end": v(-74.93, 0.15) * mm});
            skArc(sketch, "E14.31.0", {"start": v(-74.69, -6.03) * mm, "mid": v(-74.74, -5.93) * mm, "end": v(-74.85, -5.9) * mm});
            skLineSegment(sketch, "E14.31.1", {"start": v(-75.94, -5.98) * mm, "end": v(-74.85, -5.9) * mm});
            skArc(sketch, "E14.31.2", {"start": v(-76, -5.97) * mm, "mid": v(-76.59, -5.78) * mm, "end": v(-77.18, -5.57) * mm});
            skArc(sketch, "E14.31.3", {"start": v(-77.28, -5.44) * mm, "mid": v(-77.25, -5.52) * mm, "end": v(-77.18, -5.57) * mm});
            skLineSegment(sketch, "E14.31.4", {"start": v(-77.28, -5.44) * mm, "end": v(-77.3, -5.07) * mm});
            skLineSegment(sketch, "E14.31.5", {"start": v(-77.33, -4.7) * mm, "end": v(-77.3, -5.07) * mm});
            skArc(sketch, "E14.31.6", {"start": v(-77.25, -4.55) * mm, "mid": v(-77.3, -4.6) * mm, "end": v(-77.33, -4.7) * mm});
            skArc(sketch, "E14.31.7", {"start": v(-76.12, -4) * mm, "mid": v(-76.69, -4.26) * mm, "end": v(-77.25, -4.55) * mm});
            skLineSegment(sketch, "E14.31.8", {"start": v(-76.07, -3.99) * mm, "end": v(-74.98, -3.93) * mm});
            skArc(sketch, "E14.31.9", {"start": v(-74.98, -3.93) * mm, "mid": v(-74.87, -3.88) * mm, "end": v(-74.84, -3.77) * mm});
            skArc(sketch, "E14.32.0", {"start": v(-74.27, -9.93) * mm, "mid": v(-74.33, -9.83) * mm, "end": v(-74.44, -9.8) * mm});
            skLineSegment(sketch, "E14.32.1", {"start": v(-75.52, -9.94) * mm, "end": v(-74.44, -9.8) * mm});
            skArc(sketch, "E14.32.2", {"start": v(-75.58, -9.94) * mm, "mid": v(-76.18, -9.78) * mm, "end": v(-76.78, -9.6) * mm});
            skArc(sketch, "E14.32.3", {"start": v(-76.89, -9.48) * mm, "mid": v(-76.85, -9.56) * mm, "end": v(-76.78, -9.6) * mm});
            skLineSegment(sketch, "E14.32.4", {"start": v(-76.89, -9.48) * mm, "end": v(-76.93, -9.1) * mm});
            skLineSegment(sketch, "E14.32.5", {"start": v(-76.98, -8.73) * mm, "end": v(-76.93, -9.1) * mm});
            skArc(sketch, "E14.32.6", {"start": v(-76.9, -8.59) * mm, "mid": v(-76.96, -8.65) * mm, "end": v(-76.98, -8.73) * mm});
            skArc(sketch, "E14.32.7", {"start": v(-75.8, -7.98) * mm, "mid": v(-76.36, -8.27) * mm, "end": v(-76.9, -8.59) * mm});
            skLineSegment(sketch, "E14.32.8", {"start": v(-75.75, -7.96) * mm, "end": v(-74.67, -7.85) * mm});
            skArc(sketch, "E14.32.9", {"start": v(-74.67, -7.85) * mm, "mid": v(-74.57, -7.8) * mm, "end": v(-74.54, -7.68) * mm});
            skArc(sketch, "E14.33.0", {"start": v(-73.65, -13.8) * mm, "mid": v(-73.71, -13.7) * mm, "end": v(-73.82, -13.68) * mm});
            skLineSegment(sketch, "E14.33.1", {"start": v(-74.9, -13.88) * mm, "end": v(-73.82, -13.68) * mm});
            skArc(sketch, "E14.33.2", {"start": v(-74.95, -13.88) * mm, "mid": v(-75.57, -13.76) * mm, "end": v(-76.17, -13.6) * mm});
            skArc(sketch, "E14.33.3", {"start": v(-76.29, -13.49) * mm, "mid": v(-76.25, -13.57) * mm, "end": v(-76.17, -13.6) * mm});
            skLineSegment(sketch, "E14.33.4", {"start": v(-76.29, -13.49) * mm, "end": v(-76.35, -13.12) * mm});
            skLineSegment(sketch, "E14.33.5", {"start": v(-76.41, -12.75) * mm, "end": v(-76.35, -13.12) * mm});
            skArc(sketch, "E14.33.6", {"start": v(-76.35, -12.6) * mm, "mid": v(-76.4, -12.66) * mm, "end": v(-76.41, -12.75) * mm});
            skArc(sketch, "E14.33.7", {"start": v(-75.29, -11.93) * mm, "mid": v(-75.82, -12.26) * mm, "end": v(-76.35, -12.6) * mm});
            skLineSegment(sketch, "E14.33.8", {"start": v(-75.23, -11.92) * mm, "end": v(-74.16, -11.75) * mm});
            skArc(sketch, "E14.33.9", {"start": v(-74.16, -11.75) * mm, "mid": v(-74.06, -11.68) * mm, "end": v(-74.03, -11.57) * mm});
            skArc(sketch, "E14.34.0", {"start": v(-72.82, -17.64) * mm, "mid": v(-72.9, -17.55) * mm, "end": v(-73, -17.53) * mm});
            skLineSegment(sketch, "E14.34.1", {"start": v(-74.07, -17.78) * mm, "end": v(-73, -17.53) * mm});
            skArc(sketch, "E14.34.2", {"start": v(-74.12, -17.78) * mm, "mid": v(-74.74, -17.7) * mm, "end": v(-75.36, -17.58) * mm});
            skArc(sketch, "E14.34.3", {"start": v(-75.48, -17.46) * mm, "mid": v(-75.43, -17.54) * mm, "end": v(-75.36, -17.58) * mm});
            skLineSegment(sketch, "E14.34.4", {"start": v(-75.48, -17.46) * mm, "end": v(-75.56, -17.1) * mm});
            skLineSegment(sketch, "E14.34.5", {"start": v(-75.64, -16.73) * mm, "end": v(-75.56, -17.1) * mm});
            skArc(sketch, "E14.34.6", {"start": v(-75.58, -16.58) * mm, "mid": v(-75.64, -16.65) * mm, "end": v(-75.64, -16.73) * mm});
            skArc(sketch, "E14.34.7", {"start": v(-74.56, -15.86) * mm, "mid": v(-75.08, -16.2) * mm, "end": v(-75.58, -16.58) * mm});
            skLineSegment(sketch, "E14.34.8", {"start": v(-74.5, -15.84) * mm, "end": v(-73.44, -15.61) * mm});
            skArc(sketch, "E14.34.9", {"start": v(-73.44, -15.61) * mm, "mid": v(-73.35, -15.54) * mm, "end": v(-73.32, -15.43) * mm});
            skArc(sketch, "E14.35.0", {"start": v(-71.8, -21.43) * mm, "mid": v(-71.87, -21.34) * mm, "end": v(-72, -21.32) * mm});
            skLineSegment(sketch, "E14.35.1", {"start": v(-73.03, -21.63) * mm, "end": v(-72, -21.32) * mm});
            skArc(sketch, "E14.35.2", {"start": v(-73.1, -21.64) * mm, "mid": v(-73.71, -21.58) * mm, "end": v(-74.33, -21.5) * mm});
            skArc(sketch, "E14.35.3", {"start": v(-74.46, -21.39) * mm, "mid": v(-74.41, -21.46) * mm, "end": v(-74.33, -21.5) * mm});
            skLineSegment(sketch, "E14.35.4", {"start": v(-74.46, -21.39) * mm, "end": v(-74.56, -21.03) * mm});
            skLineSegment(sketch, "E14.35.5", {"start": v(-74.66, -20.67) * mm, "end": v(-74.56, -21.03) * mm});
            skArc(sketch, "E14.35.6", {"start": v(-74.61, -20.5) * mm, "mid": v(-74.66, -20.58) * mm, "end": v(-74.66, -20.67) * mm});
            skArc(sketch, "E14.35.7", {"start": v(-73.63, -19.74) * mm, "mid": v(-74.13, -20.12) * mm, "end": v(-74.61, -20.5) * mm});
            skLineSegment(sketch, "E14.35.8", {"start": v(-73.58, -19.71) * mm, "end": v(-72.52, -19.43) * mm});
            skArc(sketch, "E14.35.9", {"start": v(-72.52, -19.43) * mm, "mid": v(-72.43, -19.36) * mm, "end": v(-72.42, -19.25) * mm});
            skArc(sketch, "E14.36.0", {"start": v(-70.58, -25.16) * mm, "mid": v(-70.66, -25.07) * mm, "end": v(-70.78, -25.06) * mm});
            skLineSegment(sketch, "E14.36.1", {"start": v(-71.8, -25.43) * mm, "end": v(-70.78, -25.06) * mm});
            skArc(sketch, "E14.36.2", {"start": v(-71.86, -25.44) * mm, "mid": v(-72.48, -25.4) * mm, "end": v(-73.1, -25.36) * mm});
            skArc(sketch, "E14.36.3", {"start": v(-73.24, -25.26) * mm, "mid": v(-73.19, -25.33) * mm, "end": v(-73.1, -25.36) * mm});
            skLineSegment(sketch, "E14.36.4", {"start": v(-73.24, -25.26) * mm, "end": v(-73.36, -24.9) * mm});
            skLineSegment(sketch, "E14.36.5", {"start": v(-73.48, -24.55) * mm, "end": v(-73.36, -24.9) * mm});
            skArc(sketch, "E14.36.6", {"start": v(-73.44, -24.39) * mm, "mid": v(-73.48, -24.46) * mm, "end": v(-73.48, -24.55) * mm});
            skArc(sketch, "E14.36.7", {"start": v(-72.5, -23.57) * mm, "mid": v(-72.97, -23.97) * mm, "end": v(-73.44, -24.39) * mm});
            skLineSegment(sketch, "E14.36.8", {"start": v(-72.44, -23.54) * mm, "end": v(-71.4, -23.2) * mm});
            skArc(sketch, "E14.36.9", {"start": v(-71.4, -23.2) * mm, "mid": v(-71.32, -23.13) * mm, "end": v(-71.3, -23) * mm});
            skArc(sketch, "E14.37.0", {"start": v(-69.17, -28.81) * mm, "mid": v(-69.25, -28.73) * mm, "end": v(-69.37, -28.73) * mm});
            skLineSegment(sketch, "E14.37.1", {"start": v(-70.37, -29.15) * mm, "end": v(-69.37, -28.73) * mm});
            skArc(sketch, "E14.37.2", {"start": v(-70.43, -29.16) * mm, "mid": v(-71.05, -29.17) * mm, "end": v(-71.68, -29.15) * mm});
            skArc(sketch, "E14.37.3", {"start": v(-71.82, -29.06) * mm, "mid": v(-71.76, -29.12) * mm, "end": v(-71.68, -29.15) * mm});
            skLineSegment(sketch, "E14.37.4", {"start": v(-71.82, -29.06) * mm, "end": v(-71.96, -28.7) * mm});
            skLineSegment(sketch, "E14.37.5", {"start": v(-72.1, -28.36) * mm, "end": v(-71.96, -28.7) * mm});
            skArc(sketch, "E14.37.6", {"start": v(-72.06, -28.2) * mm, "mid": v(-72.1, -28.27) * mm, "end": v(-72.1, -28.36) * mm});
            skArc(sketch, "E14.37.7", {"start": v(-71.16, -27.33) * mm, "mid": v(-71.62, -27.75) * mm, "end": v(-72.06, -28.2) * mm});
            skLineSegment(sketch, "E14.37.8", {"start": v(-71.11, -27.3) * mm, "end": v(-70.1, -26.9) * mm});
            skArc(sketch, "E14.37.9", {"start": v(-70.1, -26.9) * mm, "mid": v(-70.01, -26.83) * mm, "end": v(-70, -26.71) * mm});
            skArc(sketch, "E14.38.0", {"start": v(-67.57, -32.4) * mm, "mid": v(-67.65, -32.32) * mm, "end": v(-67.77, -32.32) * mm});
            skLineSegment(sketch, "E14.38.1", {"start": v(-68.75, -32.8) * mm, "end": v(-67.77, -32.32) * mm});
            skArc(sketch, "E14.38.2", {"start": v(-68.8, -32.8) * mm, "mid": v(-69.43, -32.84) * mm, "end": v(-70.06, -32.86) * mm});
            skArc(sketch, "E14.38.3", {"start": v(-70.2, -32.77) * mm, "mid": v(-70.14, -32.84) * mm, "end": v(-70.06, -32.86) * mm});
            skLineSegment(sketch, "E14.38.4", {"start": v(-70.2, -32.77) * mm, "end": v(-70.36, -32.43) * mm});
            skLineSegment(sketch, "E14.38.5", {"start": v(-70.51, -32.1) * mm, "end": v(-70.36, -32.43) * mm});
            skArc(sketch, "E14.38.6", {"start": v(-70.49, -31.93) * mm, "mid": v(-70.52, -32) * mm, "end": v(-70.51, -32.1) * mm});
            skArc(sketch, "E14.38.7", {"start": v(-69.63, -31.01) * mm, "mid": v(-70.07, -31.46) * mm, "end": v(-70.49, -31.93) * mm});
            skLineSegment(sketch, "E14.38.8", {"start": v(-69.59, -30.98) * mm, "end": v(-68.6, -30.54) * mm});
            skArc(sketch, "E14.38.9", {"start": v(-68.6, -30.54) * mm, "mid": v(-68.51, -30.45) * mm, "end": v(-68.51, -30.34) * mm});
            skArc(sketch, "E14.39.0", {"start": v(-65.78, -35.89) * mm, "mid": v(-65.87, -35.81) * mm, "end": v(-65.98, -35.83) * mm});
            skLineSegment(sketch, "E14.39.1", {"start": v(-66.94, -36.35) * mm, "end": v(-65.98, -35.83) * mm});
            skArc(sketch, "E14.39.2", {"start": v(-67, -36.36) * mm, "mid": v(-67.62, -36.43) * mm, "end": v(-68.24, -36.48) * mm});
            skArc(sketch, "E14.39.3", {"start": v(-68.38, -36.4) * mm, "mid": v(-68.32, -36.46) * mm, "end": v(-68.24, -36.48) * mm});
            skLineSegment(sketch, "E14.39.4", {"start": v(-68.38, -36.4) * mm, "end": v(-68.56, -36.07) * mm});
            skLineSegment(sketch, "E14.39.5", {"start": v(-68.73, -35.74) * mm, "end": v(-68.56, -36.07) * mm});
            skArc(sketch, "E14.39.6", {"start": v(-68.72, -35.57) * mm, "mid": v(-68.75, -35.65) * mm, "end": v(-68.73, -35.74) * mm});
            skArc(sketch, "E14.39.7", {"start": v(-67.91, -34.62) * mm, "mid": v(-68.32, -35.09) * mm, "end": v(-68.72, -35.57) * mm});
            skLineSegment(sketch, "E14.39.8", {"start": v(-67.87, -34.58) * mm, "end": v(-66.9, -34.09) * mm});
            skArc(sketch, "E14.39.9", {"start": v(-66.9, -34.09) * mm, "mid": v(-66.82, -34) * mm, "end": v(-66.83, -33.88) * mm});
            skArc(sketch, "E14.40.0", {"start": v(-63.8, -39.28) * mm, "mid": v(-63.9, -39.21) * mm, "end": v(-64.02, -39.23) * mm});
            skLineSegment(sketch, "E14.40.1", {"start": v(-64.95, -39.8) * mm, "end": v(-64.02, -39.23) * mm});
            skArc(sketch, "E14.40.2", {"start": v(-65, -39.82) * mm, "mid": v(-65.62, -39.92) * mm, "end": v(-66.24, -40) * mm});
            skArc(sketch, "E14.40.3", {"start": v(-66.39, -39.93) * mm, "mid": v(-66.32, -39.99) * mm, "end": v(-66.24, -40) * mm});
            skLineSegment(sketch, "E14.40.4", {"start": v(-66.39, -39.93) * mm, "end": v(-66.58, -39.61) * mm});
            skLineSegment(sketch, "E14.40.5", {"start": v(-66.77, -39.29) * mm, "end": v(-66.58, -39.61) * mm});
            skArc(sketch, "E14.40.6", {"start": v(-66.76, -39.12) * mm, "mid": v(-66.8, -39.2) * mm, "end": v(-66.77, -39.29) * mm});
            skArc(sketch, "E14.40.7", {"start": v(-66, -38.12) * mm, "mid": v(-66.4, -38.62) * mm, "end": v(-66.76, -39.12) * mm});
            skLineSegment(sketch, "E14.40.8", {"start": v(-65.97, -38.09) * mm, "end": v(-65.02, -37.54) * mm});
            skArc(sketch, "E14.40.9", {"start": v(-65.02, -37.54) * mm, "mid": v(-64.95, -37.45) * mm, "end": v(-64.97, -37.33) * mm});
            skArc(sketch, "E14.41.0", {"start": v(-61.67, -42.57) * mm, "mid": v(-61.76, -42.5) * mm, "end": v(-61.88, -42.53) * mm});
            skLineSegment(sketch, "E14.41.1", {"start": v(-62.78, -43.14) * mm, "end": v(-61.88, -42.53) * mm});
            skArc(sketch, "E14.41.2", {"start": v(-62.83, -43.17) * mm, "mid": v(-63.44, -43.3) * mm, "end": v(-64.05, -43.42) * mm});
            skArc(sketch, "E14.41.3", {"start": v(-64.2, -43.35) * mm, "mid": v(-64.14, -43.4) * mm, "end": v(-64.05, -43.42) * mm});
            skLineSegment(sketch, "E14.41.4", {"start": v(-64.2, -43.35) * mm, "end": v(-64.42, -43.04) * mm});
            skLineSegment(sketch, "E14.41.5", {"start": v(-64.62, -42.73) * mm, "end": v(-64.42, -43.04) * mm});
            skArc(sketch, "E14.41.6", {"start": v(-64.62, -42.56) * mm, "mid": v(-64.65, -42.65) * mm, "end": v(-64.62, -42.73) * mm});
            skArc(sketch, "E14.41.7", {"start": v(-63.92, -41.52) * mm, "mid": v(-64.28, -42.04) * mm, "end": v(-64.62, -42.56) * mm});
            skLineSegment(sketch, "E14.41.8", {"start": v(-63.88, -41.49) * mm, "end": v(-62.97, -40.9) * mm});
            skArc(sketch, "E14.41.9", {"start": v(-62.97, -40.9) * mm, "mid": v(-62.9, -40.8) * mm, "end": v(-62.92, -40.68) * mm});
            skArc(sketch, "E14.42.0", {"start": v(-59.35, -45.74) * mm, "mid": v(-59.45, -45.68) * mm, "end": v(-59.57, -45.7) * mm});
            skLineSegment(sketch, "E14.42.1", {"start": v(-60.43, -46.37) * mm, "end": v(-59.57, -45.7) * mm});
            skArc(sketch, "E14.42.2", {"start": v(-60.48, -46.4) * mm, "mid": v(-61.08, -46.56) * mm, "end": v(-61.7, -46.7) * mm});
            skArc(sketch, "E14.42.3", {"start": v(-61.85, -46.65) * mm, "mid": v(-61.78, -46.7) * mm, "end": v(-61.7, -46.7) * mm});
            skLineSegment(sketch, "E14.42.4", {"start": v(-61.85, -46.65) * mm, "end": v(-62.07, -46.35) * mm});
            skLineSegment(sketch, "E14.42.5", {"start": v(-62.3, -46.05) * mm, "end": v(-62.07, -46.35) * mm});
            skArc(sketch, "E14.42.6", {"start": v(-62.3, -45.89) * mm, "mid": v(-62.33, -45.97) * mm, "end": v(-62.3, -46.05) * mm});
            skArc(sketch, "E14.42.7", {"start": v(-61.66, -44.81) * mm, "mid": v(-62, -45.34) * mm, "end": v(-62.3, -45.89) * mm});
            skLineSegment(sketch, "E14.42.8", {"start": v(-61.62, -44.77) * mm, "end": v(-60.74, -44.13) * mm});
            skArc(sketch, "E14.42.9", {"start": v(-60.74, -44.13) * mm, "mid": v(-60.68, -44.03) * mm, "end": v(-60.7, -43.92) * mm});
            skArc(sketch, "E14.43.0", {"start": v(-56.88, -48.78) * mm, "mid": v(-56.98, -48.73) * mm, "end": v(-57.1, -48.76) * mm});
            skLineSegment(sketch, "E14.43.1", {"start": v(-57.92, -49.47) * mm, "end": v(-57.1, -48.76) * mm});
            skArc(sketch, "E14.43.2", {"start": v(-57.97, -49.5) * mm, "mid": v(-58.56, -49.7) * mm, "end": v(-59.16, -49.87) * mm});
            skArc(sketch, "E14.43.3", {"start": v(-59.32, -49.83) * mm, "mid": v(-59.25, -49.87) * mm, "end": v(-59.16, -49.87) * mm});
            skLineSegment(sketch, "E14.43.4", {"start": v(-59.32, -49.83) * mm, "end": v(-59.56, -49.54) * mm});
            skLineSegment(sketch, "E14.43.5", {"start": v(-59.8, -49.25) * mm, "end": v(-59.56, -49.54) * mm});
            skArc(sketch, "E14.43.6", {"start": v(-59.82, -49.08) * mm, "mid": v(-59.84, -49.17) * mm, "end": v(-59.8, -49.25) * mm});
            skArc(sketch, "E14.43.7", {"start": v(-59.23, -47.98) * mm, "mid": v(-59.54, -48.53) * mm, "end": v(-59.82, -49.08) * mm});
            skLineSegment(sketch, "E14.43.8", {"start": v(-59.2, -47.94) * mm, "end": v(-58.35, -47.25) * mm});
            skArc(sketch, "E14.43.9", {"start": v(-58.35, -47.25) * mm, "mid": v(-58.3, -47.15) * mm, "end": v(-58.33, -47.04) * mm});
            skArc(sketch, "E14.44.0", {"start": v(-54.25, -51.69) * mm, "mid": v(-54.35, -51.64) * mm, "end": v(-54.46, -51.68) * mm});
            skLineSegment(sketch, "E14.44.1", {"start": v(-55.25, -52.43) * mm, "end": v(-54.46, -51.68) * mm});
            skArc(sketch, "E14.44.2", {"start": v(-55.3, -52.46) * mm, "mid": v(-55.88, -52.7) * mm, "end": v(-56.47, -52.9) * mm});
            skArc(sketch, "E14.44.3", {"start": v(-56.63, -52.86) * mm, "mid": v(-56.56, -52.9) * mm, "end": v(-56.47, -52.9) * mm});
            skLineSegment(sketch, "E14.44.4", {"start": v(-56.63, -52.86) * mm, "end": v(-56.89, -52.59) * mm});
            skLineSegment(sketch, "E14.44.5", {"start": v(-57.14, -52.31) * mm, "end": v(-56.89, -52.59) * mm});
            skArc(sketch, "E14.44.6", {"start": v(-57.17, -52.15) * mm, "mid": v(-57.18, -52.23) * mm, "end": v(-57.14, -52.31) * mm});
            skArc(sketch, "E14.44.7", {"start": v(-56.64, -51.01) * mm, "mid": v(-56.91, -51.58) * mm, "end": v(-57.17, -52.15) * mm});
            skLineSegment(sketch, "E14.44.8", {"start": v(-56.6, -50.97) * mm, "end": v(-55.8, -50.24) * mm});
            skArc(sketch, "E14.44.9", {"start": v(-55.8, -50.24) * mm, "mid": v(-55.75, -50.13) * mm, "end": v(-55.79, -50.02) * mm});
            skArc(sketch, "E14.45.0", {"start": v(-51.47, -54.46) * mm, "mid": v(-51.58, -54.42) * mm, "end": v(-51.68, -54.46) * mm});
            skLineSegment(sketch, "E14.45.1", {"start": v(-52.43, -55.25) * mm, "end": v(-51.68, -54.46) * mm});
            skArc(sketch, "E14.45.2", {"start": v(-52.48, -55.29) * mm, "mid": v(-53.05, -55.54) * mm, "end": v(-53.63, -55.78) * mm});
            skArc(sketch, "E14.45.3", {"start": v(-53.79, -55.75) * mm, "mid": v(-53.71, -55.8) * mm, "end": v(-53.63, -55.78) * mm});
            skLineSegment(sketch, "E14.45.4", {"start": v(-53.79, -55.75) * mm, "end": v(-54.06, -55.5) * mm});
            skLineSegment(sketch, "E14.45.5", {"start": v(-54.33, -55.23) * mm, "end": v(-54.06, -55.5) * mm});
            skArc(sketch, "E14.45.6", {"start": v(-54.36, -55.07) * mm, "mid": v(-54.37, -55.15) * mm, "end": v(-54.33, -55.23) * mm});
            skArc(sketch, "E14.45.7", {"start": v(-53.9, -53.9) * mm, "mid": v(-54.14, -54.48) * mm, "end": v(-54.36, -55.07) * mm});
            skLineSegment(sketch, "E14.45.8", {"start": v(-53.86, -53.86) * mm, "end": v(-53.1, -53.1) * mm});
            skArc(sketch, "E14.45.9", {"start": v(-53.1, -53.1) * mm, "mid": v(-53.05, -52.98) * mm, "end": v(-53.1, -52.88) * mm});
            skArc(sketch, "E14.46.0", {"start": v(-48.55, -57.08) * mm, "mid": v(-48.66, -57.04) * mm, "end": v(-48.76, -57.1) * mm});
            skLineSegment(sketch, "E14.46.1", {"start": v(-49.47, -57.92) * mm, "end": v(-48.76, -57.1) * mm});
            skArc(sketch, "E14.46.2", {"start": v(-49.51, -57.96) * mm, "mid": v(-50.07, -58.25) * mm, "end": v(-50.63, -58.52) * mm});
            skArc(sketch, "E14.46.3", {"start": v(-50.8, -58.5) * mm, "mid": v(-50.72, -58.53) * mm, "end": v(-50.63, -58.52) * mm});
            skLineSegment(sketch, "E14.46.4", {"start": v(-50.8, -58.5) * mm, "end": v(-51.08, -58.25) * mm});
            skLineSegment(sketch, "E14.46.5", {"start": v(-51.36, -58) * mm, "end": v(-51.08, -58.25) * mm});
            skArc(sketch, "E14.46.6", {"start": v(-51.4, -57.84) * mm, "mid": v(-51.4, -57.92) * mm, "end": v(-51.36, -58) * mm});
            skArc(sketch, "E14.46.7", {"start": v(-51, -56.65) * mm, "mid": v(-51.21, -57.24) * mm, "end": v(-51.4, -57.84) * mm});
            skLineSegment(sketch, "E14.46.8", {"start": v(-50.97, -56.6) * mm, "end": v(-50.24, -55.8) * mm});
            skArc(sketch, "E14.46.9", {"start": v(-50.24, -55.8) * mm, "mid": v(-50.2, -55.69) * mm, "end": v(-50.25, -55.58) * mm});
            skArc(sketch, "E14.47.0", {"start": v(-45.5, -59.54) * mm, "mid": v(-45.6, -59.5) * mm, "end": v(-45.7, -59.57) * mm});
            skLineSegment(sketch, "E14.47.1", {"start": v(-46.37, -60.43) * mm, "end": v(-45.7, -59.57) * mm});
            skArc(sketch, "E14.47.2", {"start": v(-46.41, -60.47) * mm, "mid": v(-46.95, -60.79) * mm, "end": v(-47.5, -61.08) * mm});
            skArc(sketch, "E14.47.3", {"start": v(-47.67, -61.07) * mm, "mid": v(-47.59, -61.1) * mm, "end": v(-47.5, -61.08) * mm});
            skLineSegment(sketch, "E14.47.4", {"start": v(-47.67, -61.07) * mm, "end": v(-47.96, -60.84) * mm});
            skLineSegment(sketch, "E14.47.5", {"start": v(-48.26, -60.6) * mm, "end": v(-47.96, -60.84) * mm});
            skArc(sketch, "E14.47.6", {"start": v(-48.3, -60.45) * mm, "mid": v(-48.3, -60.54) * mm, "end": v(-48.26, -60.6) * mm});
            skArc(sketch, "E14.47.7", {"start": v(-47.96, -59.25) * mm, "mid": v(-48.15, -59.84) * mm, "end": v(-48.3, -60.45) * mm});
            skLineSegment(sketch, "E14.47.8", {"start": v(-47.94, -59.2) * mm, "end": v(-47.25, -58.35) * mm});
            skArc(sketch, "E14.47.9", {"start": v(-47.25, -58.35) * mm, "mid": v(-47.22, -58.24) * mm, "end": v(-47.27, -58.14) * mm});
            skArc(sketch, "E14.48.0", {"start": v(-42.32, -61.84) * mm, "mid": v(-42.43, -61.81) * mm, "end": v(-42.53, -61.88) * mm});
            skLineSegment(sketch, "E14.48.1", {"start": v(-43.14, -62.78) * mm, "end": v(-42.53, -61.88) * mm});
            skArc(sketch, "E14.48.2", {"start": v(-43.18, -62.81) * mm, "mid": v(-43.7, -63.16) * mm, "end": v(-44.24, -63.49) * mm});
            skArc(sketch, "E14.48.3", {"start": v(-44.4, -63.48) * mm, "mid": v(-44.32, -63.5) * mm, "end": v(-44.24, -63.49) * mm});
            skLineSegment(sketch, "E14.48.4", {"start": v(-44.4, -63.48) * mm, "end": v(-44.71, -63.27) * mm});
            skLineSegment(sketch, "E14.48.5", {"start": v(-45.02, -63.05) * mm, "end": v(-44.71, -63.27) * mm});
            skArc(sketch, "E14.48.6", {"start": v(-45.08, -62.9) * mm, "mid": v(-45.07, -62.98) * mm, "end": v(-45.02, -63.05) * mm});
            skArc(sketch, "E14.48.7", {"start": v(-44.8, -61.67) * mm, "mid": v(-44.95, -62.28) * mm, "end": v(-45.08, -62.9) * mm});
            skLineSegment(sketch, "E14.48.8", {"start": v(-44.77, -61.62) * mm, "end": v(-44.13, -60.74) * mm});
            skArc(sketch, "E14.48.9", {"start": v(-44.13, -60.74) * mm, "mid": v(-44.1, -60.63) * mm, "end": v(-44.17, -60.53) * mm});
            skArc(sketch, "E14.49.0", {"start": v(-39.02, -63.97) * mm, "mid": v(-39.14, -63.95) * mm, "end": v(-39.23, -64.02) * mm});
            skLineSegment(sketch, "E14.49.1", {"start": v(-39.8, -64.95) * mm, "end": v(-39.23, -64.02) * mm});
            skArc(sketch, "E14.49.2", {"start": v(-39.84, -64.99) * mm, "mid": v(-40.34, -65.36) * mm, "end": v(-40.86, -65.72) * mm});
            skArc(sketch, "E14.49.3", {"start": v(-41.02, -65.72) * mm, "mid": v(-40.94, -65.74) * mm, "end": v(-40.86, -65.72) * mm});
            skLineSegment(sketch, "E14.49.4", {"start": v(-41.02, -65.72) * mm, "end": v(-41.34, -65.52) * mm});
            skLineSegment(sketch, "E14.49.5", {"start": v(-41.66, -65.32) * mm, "end": v(-41.34, -65.52) * mm});
            skArc(sketch, "E14.49.6", {"start": v(-41.72, -65.17) * mm, "mid": v(-41.71, -65.25) * mm, "end": v(-41.66, -65.32) * mm});
            skArc(sketch, "E14.49.7", {"start": v(-41.5, -63.93) * mm, "mid": v(-41.63, -64.55) * mm, "end": v(-41.72, -65.17) * mm});
            skLineSegment(sketch, "E14.49.8", {"start": v(-41.49, -63.88) * mm, "end": v(-40.9, -62.97) * mm});
            skArc(sketch, "E14.49.9", {"start": v(-40.9, -62.97) * mm, "mid": v(-40.87, -62.85) * mm, "end": v(-40.94, -62.76) * mm});
            skArc(sketch, "E14.50.0", {"start": v(-35.62, -65.92) * mm, "mid": v(-35.74, -65.91) * mm, "end": v(-35.83, -65.98) * mm});
            skLineSegment(sketch, "E14.50.1", {"start": v(-36.35, -66.94) * mm, "end": v(-35.83, -65.98) * mm});
            skArc(sketch, "E14.50.2", {"start": v(-36.38, -66.98) * mm, "mid": v(-36.86, -67.38) * mm, "end": v(-37.36, -67.76) * mm});
            skArc(sketch, "E14.50.3", {"start": v(-37.53, -67.77) * mm, "mid": v(-37.44, -67.8) * mm, "end": v(-37.36, -67.76) * mm});
            skLineSegment(sketch, "E14.50.4", {"start": v(-37.53, -67.77) * mm, "end": v(-37.85, -67.6) * mm});
            skLineSegment(sketch, "E14.50.5", {"start": v(-38.18, -67.4) * mm, "end": v(-37.85, -67.6) * mm});
            skArc(sketch, "E14.50.6", {"start": v(-38.26, -67.26) * mm, "mid": v(-38.24, -67.35) * mm, "end": v(-38.18, -67.4) * mm});
            skArc(sketch, "E14.50.7", {"start": v(-38.1, -66.02) * mm, "mid": v(-38.2, -66.64) * mm, "end": v(-38.26, -67.26) * mm});
            skLineSegment(sketch, "E14.50.8", {"start": v(-38.09, -65.97) * mm, "end": v(-37.54, -65.02) * mm});
            skArc(sketch, "E14.50.9", {"start": v(-37.54, -65.02) * mm, "mid": v(-37.53, -64.9) * mm, "end": v(-37.6, -64.82) * mm});
            skArc(sketch, "E14.51.0", {"start": v(-32.12, -67.7) * mm, "mid": v(-32.24, -67.7) * mm, "end": v(-32.32, -67.77) * mm});
            skLineSegment(sketch, "E14.51.1", {"start": v(-32.8, -68.75) * mm, "end": v(-32.32, -67.77) * mm});
            skArc(sketch, "E14.51.2", {"start": v(-32.83, -68.8) * mm, "mid": v(-33.29, -69.22) * mm, "end": v(-33.76, -69.63) * mm});
            skArc(sketch, "E14.51.3", {"start": v(-33.93, -69.65) * mm, "mid": v(-33.84, -69.66) * mm, "end": v(-33.76, -69.63) * mm});
            skLineSegment(sketch, "E14.51.4", {"start": v(-33.93, -69.65) * mm, "end": v(-34.26, -69.48) * mm});
            skLineSegment(sketch, "E14.51.5", {"start": v(-34.6, -69.31) * mm, "end": v(-34.26, -69.48) * mm});
            skArc(sketch, "E14.51.6", {"start": v(-34.68, -69.17) * mm, "mid": v(-34.66, -69.26) * mm, "end": v(-34.6, -69.31) * mm});
            skArc(sketch, "E14.51.7", {"start": v(-34.6, -67.92) * mm, "mid": v(-34.65, -68.55) * mm, "end": v(-34.68, -69.17) * mm});
            skLineSegment(sketch, "E14.51.8", {"start": v(-34.58, -67.87) * mm, "end": v(-34.09, -66.9) * mm});
            skArc(sketch, "E14.51.9", {"start": v(-34.09, -66.9) * mm, "mid": v(-34.08, -66.78) * mm, "end": v(-34.15, -66.7) * mm});
            skArc(sketch, "E14.52.0", {"start": v(-28.53, -69.28) * mm, "mid": v(-28.65, -69.28) * mm, "end": v(-28.73, -69.37) * mm});
            skLineSegment(sketch, "E14.52.1", {"start": v(-29.15, -70.37) * mm, "end": v(-28.73, -69.37) * mm});
            skArc(sketch, "E14.52.2", {"start": v(-29.18, -70.42) * mm, "mid": v(-29.62, -70.87) * mm, "end": v(-30.07, -71.3) * mm});
            skArc(sketch, "E14.52.3", {"start": v(-30.24, -71.33) * mm, "mid": v(-30.15, -71.34) * mm, "end": v(-30.07, -71.3) * mm});
            skLineSegment(sketch, "E14.52.4", {"start": v(-30.24, -71.33) * mm, "end": v(-30.58, -71.18) * mm});
            skLineSegment(sketch, "E14.52.5", {"start": v(-30.93, -71.03) * mm, "end": v(-30.58, -71.18) * mm});
            skArc(sketch, "E14.52.6", {"start": v(-31.02, -70.9) * mm, "mid": v(-31, -70.97) * mm, "end": v(-30.93, -71.03) * mm});
            skArc(sketch, "E14.52.7", {"start": v(-31, -69.64) * mm, "mid": v(-31.02, -70.27) * mm, "end": v(-31.02, -70.9) * mm});
            skLineSegment(sketch, "E14.52.8", {"start": v(-30.98, -69.59) * mm, "end": v(-30.54, -68.6) * mm});
            skArc(sketch, "E14.52.9", {"start": v(-30.54, -68.6) * mm, "mid": v(-30.54, -68.47) * mm, "end": v(-30.62, -68.39) * mm});
            skArc(sketch, "E14.53.0", {"start": v(-24.87, -70.68) * mm, "mid": v(-24.99, -70.69) * mm, "end": v(-25.06, -70.78) * mm});
            skLineSegment(sketch, "E14.53.1", {"start": v(-25.43, -71.8) * mm, "end": v(-25.06, -70.78) * mm});
            skArc(sketch, "E14.53.2", {"start": v(-25.45, -71.85) * mm, "mid": v(-25.87, -72.32) * mm, "end": v(-26.3, -72.77) * mm});
            skArc(sketch, "E14.53.3", {"start": v(-26.46, -72.81) * mm, "mid": v(-26.38, -72.82) * mm, "end": v(-26.3, -72.77) * mm});
            skLineSegment(sketch, "E14.53.4", {"start": v(-26.46, -72.81) * mm, "end": v(-26.81, -72.68) * mm});
            skLineSegment(sketch, "E14.53.5", {"start": v(-27.17, -72.55) * mm, "end": v(-26.81, -72.68) * mm});
            skArc(sketch, "E14.53.6", {"start": v(-27.26, -72.42) * mm, "mid": v(-27.23, -72.5) * mm, "end": v(-27.17, -72.55) * mm});
            skArc(sketch, "E14.53.7", {"start": v(-27.3, -71.17) * mm, "mid": v(-27.3, -71.8) * mm, "end": v(-27.26, -72.42) * mm});
            skLineSegment(sketch, "E14.53.8", {"start": v(-27.3, -71.11) * mm, "end": v(-26.9, -70.1) * mm});
            skArc(sketch, "E14.53.9", {"start": v(-26.9, -70.1) * mm, "mid": v(-26.91, -69.98) * mm, "end": v(-27, -69.9) * mm});
            skArc(sketch, "E14.54.0", {"start": v(-21.14, -71.89) * mm, "mid": v(-21.25, -71.9) * mm, "end": v(-21.32, -72) * mm});
            skLineSegment(sketch, "E14.54.1", {"start": v(-21.63, -73.03) * mm, "end": v(-21.32, -72) * mm});
            skArc(sketch, "E14.54.2", {"start": v(-21.66, -73.08) * mm, "mid": v(-22.05, -73.57) * mm, "end": v(-22.46, -74.05) * mm});
            skArc(sketch, "E14.54.3", {"start": v(-22.61, -74.1) * mm, "mid": v(-22.53, -74.1) * mm, "end": v(-22.46, -74.05) * mm});
            skLineSegment(sketch, "E14.54.4", {"start": v(-22.61, -74.1) * mm, "end": v(-22.97, -73.99) * mm});
            skLineSegment(sketch, "E14.54.5", {"start": v(-23.33, -73.87) * mm, "end": v(-22.97, -73.99) * mm});
            skArc(sketch, "E14.54.6", {"start": v(-23.44, -73.75) * mm, "mid": v(-23.4, -73.83) * mm, "end": v(-23.33, -73.87) * mm});
            skArc(sketch, "E14.54.7", {"start": v(-23.55, -72.5) * mm, "mid": v(-23.5, -73.12) * mm, "end": v(-23.44, -73.75) * mm});
            skLineSegment(sketch, "E14.54.8", {"start": v(-23.54, -72.44) * mm, "end": v(-23.2, -71.4) * mm});
            skArc(sketch, "E14.54.9", {"start": v(-23.2, -71.4) * mm, "mid": v(-23.21, -71.3) * mm, "end": v(-23.3, -71.22) * mm});
            skArc(sketch, "E14.55.0", {"start": v(-17.34, -72.9) * mm, "mid": v(-17.46, -72.91) * mm, "end": v(-17.53, -73) * mm});
            skLineSegment(sketch, "E14.55.1", {"start": v(-17.78, -74.07) * mm, "end": v(-17.53, -73) * mm});
            skArc(sketch, "E14.55.2", {"start": v(-17.8, -74.12) * mm, "mid": v(-18.17, -74.63) * mm, "end": v(-18.55, -75.12) * mm});
            skArc(sketch, "E14.55.3", {"start": v(-18.7, -75.18) * mm, "mid": v(-18.62, -75.17) * mm, "end": v(-18.55, -75.12) * mm});
            skLineSegment(sketch, "E14.55.4", {"start": v(-18.7, -75.18) * mm, "end": v(-19.07, -75.09) * mm});
            skLineSegment(sketch, "E14.55.5", {"start": v(-19.43, -75) * mm, "end": v(-19.07, -75.09) * mm});
            skArc(sketch, "E14.55.6", {"start": v(-19.54, -74.87) * mm, "mid": v(-19.5, -74.95) * mm, "end": v(-19.43, -75) * mm});
            skArc(sketch, "E14.55.7", {"start": v(-19.72, -73.63) * mm, "mid": v(-19.64, -74.25) * mm, "end": v(-19.54, -74.87) * mm});
            skLineSegment(sketch, "E14.55.8", {"start": v(-19.71, -73.58) * mm, "end": v(-19.43, -72.52) * mm});
            skArc(sketch, "E14.55.9", {"start": v(-19.43, -72.52) * mm, "mid": v(-19.45, -72.4) * mm, "end": v(-19.54, -72.34) * mm});
            skArc(sketch, "E14.56.0", {"start": v(-13.5, -73.7) * mm, "mid": v(-13.62, -73.73) * mm, "end": v(-13.68, -73.82) * mm});
            skLineSegment(sketch, "E14.56.1", {"start": v(-13.88, -74.9) * mm, "end": v(-13.68, -73.82) * mm});
            skArc(sketch, "E14.56.2", {"start": v(-13.9, -74.95) * mm, "mid": v(-14.24, -75.48) * mm, "end": v(-14.6, -76) * mm});
            skArc(sketch, "E14.56.3", {"start": v(-14.75, -76.05) * mm, "mid": v(-14.66, -76.05) * mm, "end": v(-14.6, -76) * mm});
            skLineSegment(sketch, "E14.56.4", {"start": v(-14.75, -76.05) * mm, "end": v(-15.11, -75.98) * mm});
            skLineSegment(sketch, "E14.56.5", {"start": v(-15.48, -75.9) * mm, "end": v(-15.11, -75.98) * mm});
            skArc(sketch, "E14.56.6", {"start": v(-15.6, -75.8) * mm, "mid": v(-15.56, -75.87) * mm, "end": v(-15.48, -75.9) * mm});
            skArc(sketch, "E14.56.7", {"start": v(-15.84, -74.56) * mm, "mid": v(-15.73, -75.18) * mm, "end": v(-15.6, -75.8) * mm});
            skLineSegment(sketch, "E14.56.8", {"start": v(-15.84, -74.5) * mm, "end": v(-15.61, -73.44) * mm});
            skArc(sketch, "E14.56.9", {"start": v(-15.61, -73.44) * mm, "mid": v(-15.63, -73.33) * mm, "end": v(-15.73, -73.26) * mm});
            skArc(sketch, "E14.57.0", {"start": v(-9.63, -74.3) * mm, "mid": v(-9.74, -74.34) * mm, "end": v(-9.8, -74.44) * mm});
            skLineSegment(sketch, "E14.57.1", {"start": v(-9.94, -75.52) * mm, "end": v(-9.8, -74.44) * mm});
            skArc(sketch, "E14.57.2", {"start": v(-9.96, -75.57) * mm, "mid": v(-10.27, -76.12) * mm, "end": v(-10.6, -76.65) * mm});
            skArc(sketch, "E14.57.3", {"start": v(-10.74, -76.72) * mm, "mid": v(-10.66, -76.7) * mm, "end": v(-10.6, -76.65) * mm});
            skLineSegment(sketch, "E14.57.4", {"start": v(-10.74, -76.72) * mm, "end": v(-11.12, -76.67) * mm});
            skLineSegment(sketch, "E14.57.5", {"start": v(-11.49, -76.61) * mm, "end": v(-11.12, -76.67) * mm});
            skArc(sketch, "E14.57.6", {"start": v(-11.61, -76.5) * mm, "mid": v(-11.57, -76.58) * mm, "end": v(-11.49, -76.61) * mm});
            skArc(sketch, "E14.57.7", {"start": v(-11.91, -75.29) * mm, "mid": v(-11.77, -75.9) * mm, "end": v(-11.61, -76.5) * mm});
            skLineSegment(sketch, "E14.57.8", {"start": v(-11.92, -75.23) * mm, "end": v(-11.75, -74.16) * mm});
            skArc(sketch, "E14.57.9", {"start": v(-11.75, -74.16) * mm, "mid": v(-11.77, -74.04) * mm, "end": v(-11.87, -73.98) * mm});
            skArc(sketch, "E14.58.0", {"start": v(-5.73, -74.71) * mm, "mid": v(-5.84, -74.75) * mm, "end": v(-5.9, -74.85) * mm});
            skLineSegment(sketch, "E14.58.1", {"start": v(-5.98, -75.94) * mm, "end": v(-5.9, -74.85) * mm});
            skArc(sketch, "E14.58.2", {"start": v(-6, -76) * mm, "mid": v(-6.27, -76.55) * mm, "end": v(-6.57, -77.1) * mm});
            skArc(sketch, "E14.58.3", {"start": v(-6.71, -77.18) * mm, "mid": v(-6.63, -77.16) * mm, "end": v(-6.57, -77.1) * mm});
            skLineSegment(sketch, "E14.58.4", {"start": v(-6.71, -77.18) * mm, "end": v(-7.09, -77.15) * mm});
            skLineSegment(sketch, "E14.58.5", {"start": v(-7.46, -77.1) * mm, "end": v(-7.09, -77.15) * mm});
            skArc(sketch, "E14.58.6", {"start": v(-7.6, -77) * mm, "mid": v(-7.54, -77.08) * mm, "end": v(-7.46, -77.1) * mm});
            skArc(sketch, "E14.58.7", {"start": v(-7.96, -75.81) * mm, "mid": v(-7.78, -76.41) * mm, "end": v(-7.6, -77) * mm});
            skLineSegment(sketch, "E14.58.8", {"start": v(-7.96, -75.75) * mm, "end": v(-7.85, -74.67) * mm});
            skArc(sketch, "E14.58.9", {"start": v(-7.85, -74.67) * mm, "mid": v(-7.88, -74.56) * mm, "end": v(-7.98, -74.5) * mm});
            skArc(sketch, "E14.59.0", {"start": v(-1.8, -74.9) * mm, "mid": v(-1.92, -74.95) * mm, "end": v(-1.97, -75.06) * mm});
            skLineSegment(sketch, "E14.59.1", {"start": v(-2, -76.15) * mm, "end": v(-1.97, -75.06) * mm});
            skArc(sketch, "E14.59.2", {"start": v(-2, -76.2) * mm, "mid": v(-2.26, -76.77) * mm, "end": v(-2.52, -77.34) * mm});
            skArc(sketch, "E14.59.3", {"start": v(-2.67, -77.42) * mm, "mid": v(-2.58, -77.4) * mm, "end": v(-2.52, -77.34) * mm});
            skLineSegment(sketch, "E14.59.4", {"start": v(-2.67, -77.42) * mm, "end": v(-3.04, -77.41) * mm});
            skLineSegment(sketch, "E14.59.5", {"start": v(-3.42, -77.4) * mm, "end": v(-3.04, -77.41) * mm});
            skArc(sketch, "E14.59.6", {"start": v(-3.55, -77.3) * mm, "mid": v(-3.5, -77.37) * mm, "end": v(-3.42, -77.4) * mm});
            skArc(sketch, "E14.59.7", {"start": v(-3.98, -76.12) * mm, "mid": v(-3.77, -76.71) * mm, "end": v(-3.55, -77.3) * mm});
            skLineSegment(sketch, "E14.59.8", {"start": v(-3.99, -76.07) * mm, "end": v(-3.93, -74.98) * mm});
            skArc(sketch, "E14.59.9", {"start": v(-3.93, -74.98) * mm, "mid": v(-3.97, -74.87) * mm, "end": v(-4.07, -74.82) * mm});
            skArc(sketch, "E14.60.0", {"start": v(2.11, -74.9) * mm, "mid": v(2, -74.95) * mm, "end": v(1.97, -75.06) * mm});
            skLineSegment(sketch, "E14.60.1", {"start": v(2, -76.15) * mm, "end": v(1.97, -75.06) * mm});
            skArc(sketch, "E14.60.2", {"start": v(1.99, -76.2) * mm, "mid": v(1.77, -76.79) * mm, "end": v(1.53, -77.37) * mm});
            skArc(sketch, "E14.60.3", {"start": v(1.39, -77.46) * mm, "mid": v(1.47, -77.43) * mm, "end": v(1.53, -77.37) * mm});
            skLineSegment(sketch, "E14.60.4", {"start": v(1.39, -77.46) * mm, "end": v(1.01, -77.46) * mm});
            skLineSegment(sketch, "E14.60.5", {"start": v(0.64, -77.47) * mm, "end": v(1.01, -77.46) * mm});
            skArc(sketch, "E14.60.6", {"start": v(0.5, -77.38) * mm, "mid": v(0.56, -77.44) * mm, "end": v(0.64, -77.47) * mm});
            skArc(sketch, "E14.60.7", {"start": v(0.01, -76.23) * mm, "mid": v(0.25, -76.8) * mm, "end": v(0.5, -77.38) * mm});
            skLineSegment(sketch, "E14.60.8", {"start": v(0, -76.17) * mm, "end": v(0, -75.08) * mm});
            skArc(sketch, "E14.60.9", {"start": v(0, -75.08) * mm, "mid": v(-0.04, -74.97) * mm, "end": v(-0.15, -74.93) * mm});
            skArc(sketch, "E14.61.0", {"start": v(6.03, -74.69) * mm, "mid": v(5.93, -74.74) * mm, "end": v(5.9, -74.85) * mm});
            skLineSegment(sketch, "E14.61.1", {"start": v(5.98, -75.94) * mm, "end": v(5.9, -74.85) * mm});
            skArc(sketch, "E14.61.2", {"start": v(5.97, -76) * mm, "mid": v(5.78, -76.59) * mm, "end": v(5.57, -77.18) * mm});
            skArc(sketch, "E14.61.3", {"start": v(5.44, -77.28) * mm, "mid": v(5.52, -77.25) * mm, "end": v(5.57, -77.18) * mm});
            skLineSegment(sketch, "E14.61.4", {"start": v(5.44, -77.28) * mm, "end": v(5.07, -77.3) * mm});
            skLineSegment(sketch, "E14.61.5", {"start": v(4.7, -77.33) * mm, "end": v(5.07, -77.3) * mm});
            skArc(sketch, "E14.61.6", {"start": v(4.55, -77.25) * mm, "mid": v(4.6, -77.3) * mm, "end": v(4.7, -77.33) * mm});
            skArc(sketch, "E14.61.7", {"start": v(4, -76.12) * mm, "mid": v(4.26, -76.69) * mm, "end": v(4.55, -77.25) * mm});
            skLineSegment(sketch, "E14.61.8", {"start": v(3.99, -76.07) * mm, "end": v(3.93, -74.98) * mm});
            skArc(sketch, "E14.61.9", {"start": v(3.93, -74.98) * mm, "mid": v(3.88, -74.87) * mm, "end": v(3.77, -74.84) * mm});
            skArc(sketch, "E14.62.0", {"start": v(9.93, -74.27) * mm, "mid": v(9.83, -74.33) * mm, "end": v(9.8, -74.44) * mm});
            skLineSegment(sketch, "E14.62.1", {"start": v(9.94, -75.52) * mm, "end": v(9.8, -74.44) * mm});
            skArc(sketch, "E14.62.2", {"start": v(9.94, -75.58) * mm, "mid": v(9.78, -76.18) * mm, "end": v(9.6, -76.78) * mm});
            skArc(sketch, "E14.62.3", {"start": v(9.48, -76.89) * mm, "mid": v(9.56, -76.85) * mm, "end": v(9.6, -76.78) * mm});
            skLineSegment(sketch, "E14.62.4", {"start": v(9.48, -76.89) * mm, "end": v(9.1, -76.93) * mm});
            skLineSegment(sketch, "E14.62.5", {"start": v(8.73, -76.98) * mm, "end": v(9.1, -76.93) * mm});
            skArc(sketch, "E14.62.6", {"start": v(8.59, -76.9) * mm, "mid": v(8.65, -76.96) * mm, "end": v(8.73, -76.98) * mm});
            skArc(sketch, "E14.62.7", {"start": v(7.98, -75.8) * mm, "mid": v(8.27, -76.36) * mm, "end": v(8.59, -76.9) * mm});
            skLineSegment(sketch, "E14.62.8", {"start": v(7.96, -75.75) * mm, "end": v(7.85, -74.67) * mm});
            skArc(sketch, "E14.62.9", {"start": v(7.85, -74.67) * mm, "mid": v(7.8, -74.57) * mm, "end": v(7.68, -74.54) * mm});
            skArc(sketch, "E14.63.0", {"start": v(13.8, -73.65) * mm, "mid": v(13.7, -73.71) * mm, "end": v(13.68, -73.82) * mm});
            skLineSegment(sketch, "E14.63.1", {"start": v(13.88, -74.9) * mm, "end": v(13.68, -73.82) * mm});
            skArc(sketch, "E14.63.2", {"start": v(13.88, -74.95) * mm, "mid": v(13.76, -75.57) * mm, "end": v(13.6, -76.17) * mm});
            skArc(sketch, "E14.63.3", {"start": v(13.49, -76.29) * mm, "mid": v(13.57, -76.25) * mm, "end": v(13.6, -76.17) * mm});
            skLineSegment(sketch, "E14.63.4", {"start": v(13.49, -76.29) * mm, "end": v(13.12, -76.35) * mm});
            skLineSegment(sketch, "E14.63.5", {"start": v(12.75, -76.41) * mm, "end": v(13.12, -76.35) * mm});
            skArc(sketch, "E14.63.6", {"start": v(12.6, -76.35) * mm, "mid": v(12.66, -76.4) * mm, "end": v(12.75, -76.41) * mm});
            skArc(sketch, "E14.63.7", {"start": v(11.93, -75.29) * mm, "mid": v(12.26, -75.82) * mm, "end": v(12.6, -76.35) * mm});
            skLineSegment(sketch, "E14.63.8", {"start": v(11.92, -75.23) * mm, "end": v(11.75, -74.16) * mm});
            skArc(sketch, "E14.63.9", {"start": v(11.75, -74.16) * mm, "mid": v(11.68, -74.06) * mm, "end": v(11.57, -74.03) * mm});
            skArc(sketch, "E14.64.0", {"start": v(17.64, -72.82) * mm, "mid": v(17.55, -72.9) * mm, "end": v(17.53, -73) * mm});
            skLineSegment(sketch, "E14.64.1", {"start": v(17.78, -74.07) * mm, "end": v(17.53, -73) * mm});
            skArc(sketch, "E14.64.2", {"start": v(17.78, -74.12) * mm, "mid": v(17.7, -74.74) * mm, "end": v(17.58, -75.36) * mm});
            skArc(sketch, "E14.64.3", {"start": v(17.46, -75.48) * mm, "mid": v(17.54, -75.43) * mm, "end": v(17.58, -75.36) * mm});
            skLineSegment(sketch, "E14.64.4", {"start": v(17.46, -75.48) * mm, "end": v(17.1, -75.56) * mm});
            skLineSegment(sketch, "E14.64.5", {"start": v(16.73, -75.64) * mm, "end": v(17.1, -75.56) * mm});
            skArc(sketch, "E14.64.6", {"start": v(16.58, -75.58) * mm, "mid": v(16.65, -75.64) * mm, "end": v(16.73, -75.64) * mm});
            skArc(sketch, "E14.64.7", {"start": v(15.86, -74.56) * mm, "mid": v(16.2, -75.08) * mm, "end": v(16.58, -75.58) * mm});
            skLineSegment(sketch, "E14.64.8", {"start": v(15.84, -74.5) * mm, "end": v(15.61, -73.44) * mm});
            skArc(sketch, "E14.64.9", {"start": v(15.61, -73.44) * mm, "mid": v(15.54, -73.35) * mm, "end": v(15.43, -73.32) * mm});
            skArc(sketch, "E14.65.0", {"start": v(21.43, -71.8) * mm, "mid": v(21.34, -71.87) * mm, "end": v(21.32, -72) * mm});
            skLineSegment(sketch, "E14.65.1", {"start": v(21.63, -73.03) * mm, "end": v(21.32, -72) * mm});
            skArc(sketch, "E14.65.2", {"start": v(21.64, -73.1) * mm, "mid": v(21.58, -73.71) * mm, "end": v(21.5, -74.33) * mm});
            skArc(sketch, "E14.65.3", {"start": v(21.39, -74.46) * mm, "mid": v(21.46, -74.41) * mm, "end": v(21.5, -74.33) * mm});
            skLineSegment(sketch, "E14.65.4", {"start": v(21.39, -74.46) * mm, "end": v(21.03, -74.56) * mm});
            skLineSegment(sketch, "E14.65.5", {"start": v(20.67, -74.66) * mm, "end": v(21.03, -74.56) * mm});
            skArc(sketch, "E14.65.6", {"start": v(20.5, -74.61) * mm, "mid": v(20.58, -74.66) * mm, "end": v(20.67, -74.66) * mm});
            skArc(sketch, "E14.65.7", {"start": v(19.74, -73.63) * mm, "mid": v(20.12, -74.13) * mm, "end": v(20.5, -74.61) * mm});
            skLineSegment(sketch, "E14.65.8", {"start": v(19.71, -73.58) * mm, "end": v(19.43, -72.52) * mm});
            skArc(sketch, "E14.65.9", {"start": v(19.43, -72.52) * mm, "mid": v(19.36, -72.43) * mm, "end": v(19.25, -72.42) * mm});
            skArc(sketch, "E14.66.0", {"start": v(25.16, -70.58) * mm, "mid": v(25.07, -70.66) * mm, "end": v(25.06, -70.78) * mm});
            skLineSegment(sketch, "E14.66.1", {"start": v(25.43, -71.8) * mm, "end": v(25.06, -70.78) * mm});
            skArc(sketch, "E14.66.2", {"start": v(25.44, -71.86) * mm, "mid": v(25.4, -72.48) * mm, "end": v(25.36, -73.1) * mm});
            skArc(sketch, "E14.66.3", {"start": v(25.26, -73.24) * mm, "mid": v(25.33, -73.19) * mm, "end": v(25.36, -73.1) * mm});
            skLineSegment(sketch, "E14.66.4", {"start": v(25.26, -73.24) * mm, "end": v(24.9, -73.36) * mm});
            skLineSegment(sketch, "E14.66.5", {"start": v(24.55, -73.48) * mm, "end": v(24.9, -73.36) * mm});
            skArc(sketch, "E14.66.6", {"start": v(24.39, -73.44) * mm, "mid": v(24.46, -73.48) * mm, "end": v(24.55, -73.48) * mm});
            skArc(sketch, "E14.66.7", {"start": v(23.57, -72.5) * mm, "mid": v(23.97, -72.97) * mm, "end": v(24.39, -73.44) * mm});
            skLineSegment(sketch, "E14.66.8", {"start": v(23.54, -72.44) * mm, "end": v(23.2, -71.4) * mm});
            skArc(sketch, "E14.66.9", {"start": v(23.2, -71.4) * mm, "mid": v(23.13, -71.32) * mm, "end": v(23, -71.3) * mm});
            skArc(sketch, "E14.67.0", {"start": v(28.81, -69.17) * mm, "mid": v(28.73, -69.25) * mm, "end": v(28.73, -69.37) * mm});
            skLineSegment(sketch, "E14.67.1", {"start": v(29.15, -70.37) * mm, "end": v(28.73, -69.37) * mm});
            skArc(sketch, "E14.67.2", {"start": v(29.16, -70.43) * mm, "mid": v(29.17, -71.05) * mm, "end": v(29.15, -71.68) * mm});
            skArc(sketch, "E14.67.3", {"start": v(29.06, -71.82) * mm, "mid": v(29.12, -71.76) * mm, "end": v(29.15, -71.68) * mm});
            skLineSegment(sketch, "E14.67.4", {"start": v(29.06, -71.82) * mm, "end": v(28.7, -71.96) * mm});
            skLineSegment(sketch, "E14.67.5", {"start": v(28.36, -72.1) * mm, "end": v(28.7, -71.96) * mm});
            skArc(sketch, "E14.67.6", {"start": v(28.2, -72.06) * mm, "mid": v(28.27, -72.1) * mm, "end": v(28.36, -72.1) * mm});
            skArc(sketch, "E14.67.7", {"start": v(27.33, -71.16) * mm, "mid": v(27.75, -71.62) * mm, "end": v(28.2, -72.06) * mm});
            skLineSegment(sketch, "E14.67.8", {"start": v(27.3, -71.11) * mm, "end": v(26.9, -70.1) * mm});
            skArc(sketch, "E14.67.9", {"start": v(26.9, -70.1) * mm, "mid": v(26.83, -70.01) * mm, "end": v(26.71, -70) * mm});
            skArc(sketch, "E14.68.0", {"start": v(32.4, -67.57) * mm, "mid": v(32.32, -67.65) * mm, "end": v(32.32, -67.77) * mm});
            skLineSegment(sketch, "E14.68.1", {"start": v(32.8, -68.75) * mm, "end": v(32.32, -67.77) * mm});
            skArc(sketch, "E14.68.2", {"start": v(32.8, -68.8) * mm, "mid": v(32.84, -69.43) * mm, "end": v(32.86, -70.06) * mm});
            skArc(sketch, "E14.68.3", {"start": v(32.77, -70.2) * mm, "mid": v(32.84, -70.14) * mm, "end": v(32.86, -70.06) * mm});
            skLineSegment(sketch, "E14.68.4", {"start": v(32.77, -70.2) * mm, "end": v(32.43, -70.36) * mm});
            skLineSegment(sketch, "E14.68.5", {"start": v(32.1, -70.51) * mm, "end": v(32.43, -70.36) * mm});
            skArc(sketch, "E14.68.6", {"start": v(31.93, -70.49) * mm, "mid": v(32, -70.52) * mm, "end": v(32.1, -70.51) * mm});
            skArc(sketch, "E14.68.7", {"start": v(31.01, -69.63) * mm, "mid": v(31.46, -70.07) * mm, "end": v(31.93, -70.49) * mm});
            skLineSegment(sketch, "E14.68.8", {"start": v(30.98, -69.59) * mm, "end": v(30.54, -68.6) * mm});
            skArc(sketch, "E14.68.9", {"start": v(30.54, -68.6) * mm, "mid": v(30.45, -68.51) * mm, "end": v(30.34, -68.51) * mm});
            skArc(sketch, "E14.69.0", {"start": v(35.89, -65.78) * mm, "mid": v(35.81, -65.87) * mm, "end": v(35.83, -65.98) * mm});
            skLineSegment(sketch, "E14.69.1", {"start": v(36.35, -66.94) * mm, "end": v(35.83, -65.98) * mm});
            skArc(sketch, "E14.69.2", {"start": v(36.36, -67) * mm, "mid": v(36.43, -67.62) * mm, "end": v(36.48, -68.24) * mm});
            skArc(sketch, "E14.69.3", {"start": v(36.4, -68.38) * mm, "mid": v(36.46, -68.32) * mm, "end": v(36.48, -68.24) * mm});
            skLineSegment(sketch, "E14.69.4", {"start": v(36.4, -68.38) * mm, "end": v(36.07, -68.56) * mm});
            skLineSegment(sketch, "E14.69.5", {"start": v(35.74, -68.73) * mm, "end": v(36.07, -68.56) * mm});
            skArc(sketch, "E14.69.6", {"start": v(35.57, -68.72) * mm, "mid": v(35.65, -68.75) * mm, "end": v(35.74, -68.73) * mm});
            skArc(sketch, "E14.69.7", {"start": v(34.62, -67.91) * mm, "mid": v(35.09, -68.32) * mm, "end": v(35.57, -68.72) * mm});
            skLineSegment(sketch, "E14.69.8", {"start": v(34.58, -67.87) * mm, "end": v(34.09, -66.9) * mm});
            skArc(sketch, "E14.69.9", {"start": v(34.09, -66.9) * mm, "mid": v(34, -66.82) * mm, "end": v(33.88, -66.83) * mm});
            skArc(sketch, "E14.70.0", {"start": v(39.28, -63.8) * mm, "mid": v(39.21, -63.9) * mm, "end": v(39.23, -64.02) * mm});
            skLineSegment(sketch, "E14.70.1", {"start": v(39.8, -64.95) * mm, "end": v(39.23, -64.02) * mm});
            skArc(sketch, "E14.70.2", {"start": v(39.82, -65) * mm, "mid": v(39.92, -65.62) * mm, "end": v(40, -66.24) * mm});
            skArc(sketch, "E14.70.3", {"start": v(39.93, -66.39) * mm, "mid": v(39.99, -66.32) * mm, "end": v(40, -66.24) * mm});
            skLineSegment(sketch, "E14.70.4", {"start": v(39.93, -66.39) * mm, "end": v(39.61, -66.58) * mm});
            skLineSegment(sketch, "E14.70.5", {"start": v(39.29, -66.77) * mm, "end": v(39.61, -66.58) * mm});
            skArc(sketch, "E14.70.6", {"start": v(39.12, -66.76) * mm, "mid": v(39.2, -66.8) * mm, "end": v(39.29, -66.77) * mm});
            skArc(sketch, "E14.70.7", {"start": v(38.12, -66) * mm, "mid": v(38.62, -66.4) * mm, "end": v(39.12, -66.76) * mm});
            skLineSegment(sketch, "E14.70.8", {"start": v(38.09, -65.97) * mm, "end": v(37.54, -65.02) * mm});
            skArc(sketch, "E14.70.9", {"start": v(37.54, -65.02) * mm, "mid": v(37.45, -64.95) * mm, "end": v(37.33, -64.97) * mm});
            skArc(sketch, "E14.71.0", {"start": v(42.57, -61.67) * mm, "mid": v(42.5, -61.76) * mm, "end": v(42.53, -61.88) * mm});
            skLineSegment(sketch, "E14.71.1", {"start": v(43.14, -62.78) * mm, "end": v(42.53, -61.88) * mm});
            skArc(sketch, "E14.71.2", {"start": v(43.17, -62.83) * mm, "mid": v(43.3, -63.44) * mm, "end": v(43.42, -64.05) * mm});
            skArc(sketch, "E14.71.3", {"start": v(43.35, -64.2) * mm, "mid": v(43.4, -64.14) * mm, "end": v(43.42, -64.05) * mm});
            skLineSegment(sketch, "E14.71.4", {"start": v(43.35, -64.2) * mm, "end": v(43.04, -64.42) * mm});
            skLineSegment(sketch, "E14.71.5", {"start": v(42.73, -64.62) * mm, "end": v(43.04, -64.42) * mm});
            skArc(sketch, "E14.71.6", {"start": v(42.56, -64.62) * mm, "mid": v(42.65, -64.65) * mm, "end": v(42.73, -64.62) * mm});
            skArc(sketch, "E14.71.7", {"start": v(41.52, -63.92) * mm, "mid": v(42.04, -64.28) * mm, "end": v(42.56, -64.62) * mm});
            skLineSegment(sketch, "E14.71.8", {"start": v(41.49, -63.88) * mm, "end": v(40.9, -62.97) * mm});
            skArc(sketch, "E14.71.9", {"start": v(40.9, -62.97) * mm, "mid": v(40.8, -62.9) * mm, "end": v(40.68, -62.92) * mm});
            skArc(sketch, "E14.72.0", {"start": v(45.74, -59.35) * mm, "mid": v(45.68, -59.45) * mm, "end": v(45.7, -59.57) * mm});
            skLineSegment(sketch, "E14.72.1", {"start": v(46.37, -60.43) * mm, "end": v(45.7, -59.57) * mm});
            skArc(sketch, "E14.72.2", {"start": v(46.4, -60.48) * mm, "mid": v(46.56, -61.08) * mm, "end": v(46.7, -61.7) * mm});
            skArc(sketch, "E14.72.3", {"start": v(46.65, -61.85) * mm, "mid": v(46.7, -61.78) * mm, "end": v(46.7, -61.7) * mm});
            skLineSegment(sketch, "E14.72.4", {"start": v(46.65, -61.85) * mm, "end": v(46.35, -62.07) * mm});
            skLineSegment(sketch, "E14.72.5", {"start": v(46.05, -62.3) * mm, "end": v(46.35, -62.07) * mm});
            skArc(sketch, "E14.72.6", {"start": v(45.89, -62.3) * mm, "mid": v(45.97, -62.33) * mm, "end": v(46.05, -62.3) * mm});
            skArc(sketch, "E14.72.7", {"start": v(44.81, -61.66) * mm, "mid": v(45.34, -62) * mm, "end": v(45.89, -62.3) * mm});
            skLineSegment(sketch, "E14.72.8", {"start": v(44.77, -61.62) * mm, "end": v(44.13, -60.74) * mm});
            skArc(sketch, "E14.72.9", {"start": v(44.13, -60.74) * mm, "mid": v(44.03, -60.68) * mm, "end": v(43.92, -60.7) * mm});
            skArc(sketch, "E14.73.0", {"start": v(48.78, -56.88) * mm, "mid": v(48.73, -56.98) * mm, "end": v(48.76, -57.1) * mm});
            skLineSegment(sketch, "E14.73.1", {"start": v(49.47, -57.92) * mm, "end": v(48.76, -57.1) * mm});
            skArc(sketch, "E14.73.2", {"start": v(49.5, -57.97) * mm, "mid": v(49.7, -58.56) * mm, "end": v(49.87, -59.16) * mm});
            skArc(sketch, "E14.73.3", {"start": v(49.83, -59.32) * mm, "mid": v(49.87, -59.25) * mm, "end": v(49.87, -59.16) * mm});
            skLineSegment(sketch, "E14.73.4", {"start": v(49.83, -59.32) * mm, "end": v(49.54, -59.56) * mm});
            skLineSegment(sketch, "E14.73.5", {"start": v(49.25, -59.8) * mm, "end": v(49.54, -59.56) * mm});
            skArc(sketch, "E14.73.6", {"start": v(49.08, -59.82) * mm, "mid": v(49.17, -59.84) * mm, "end": v(49.25, -59.8) * mm});
            skArc(sketch, "E14.73.7", {"start": v(47.98, -59.23) * mm, "mid": v(48.53, -59.54) * mm, "end": v(49.08, -59.82) * mm});
            skLineSegment(sketch, "E14.73.8", {"start": v(47.94, -59.2) * mm, "end": v(47.25, -58.35) * mm});
            skArc(sketch, "E14.73.9", {"start": v(47.25, -58.35) * mm, "mid": v(47.15, -58.3) * mm, "end": v(47.04, -58.33) * mm});
            skArc(sketch, "E14.74.0", {"start": v(51.69, -54.25) * mm, "mid": v(51.64, -54.35) * mm, "end": v(51.68, -54.46) * mm});
            skLineSegment(sketch, "E14.74.1", {"start": v(52.43, -55.25) * mm, "end": v(51.68, -54.46) * mm});
            skArc(sketch, "E14.74.2", {"start": v(52.46, -55.3) * mm, "mid": v(52.7, -55.88) * mm, "end": v(52.9, -56.47) * mm});
            skArc(sketch, "E14.74.3", {"start": v(52.86, -56.63) * mm, "mid": v(52.9, -56.56) * mm, "end": v(52.9, -56.47) * mm});
            skLineSegment(sketch, "E14.74.4", {"start": v(52.86, -56.63) * mm, "end": v(52.59, -56.89) * mm});
            skLineSegment(sketch, "E14.74.5", {"start": v(52.31, -57.14) * mm, "end": v(52.59, -56.89) * mm});
            skArc(sketch, "E14.74.6", {"start": v(52.15, -57.17) * mm, "mid": v(52.23, -57.18) * mm, "end": v(52.31, -57.14) * mm});
            skArc(sketch, "E14.74.7", {"start": v(51.01, -56.64) * mm, "mid": v(51.58, -56.91) * mm, "end": v(52.15, -57.17) * mm});
            skLineSegment(sketch, "E14.74.8", {"start": v(50.97, -56.6) * mm, "end": v(50.24, -55.8) * mm});
            skArc(sketch, "E14.74.9", {"start": v(50.24, -55.8) * mm, "mid": v(50.13, -55.75) * mm, "end": v(50.02, -55.79) * mm});
            skArc(sketch, "E14.75.0", {"start": v(54.46, -51.47) * mm, "mid": v(54.42, -51.58) * mm, "end": v(54.46, -51.68) * mm});
            skLineSegment(sketch, "E14.75.1", {"start": v(55.25, -52.43) * mm, "end": v(54.46, -51.68) * mm});
            skArc(sketch, "E14.75.2", {"start": v(55.29, -52.48) * mm, "mid": v(55.54, -53.05) * mm, "end": v(55.78, -53.63) * mm});
            skArc(sketch, "E14.75.3", {"start": v(55.75, -53.79) * mm, "mid": v(55.8, -53.71) * mm, "end": v(55.78, -53.63) * mm});
            skLineSegment(sketch, "E14.75.4", {"start": v(55.75, -53.79) * mm, "end": v(55.5, -54.06) * mm});
            skLineSegment(sketch, "E14.75.5", {"start": v(55.23, -54.33) * mm, "end": v(55.5, -54.06) * mm});
            skArc(sketch, "E14.75.6", {"start": v(55.07, -54.36) * mm, "mid": v(55.15, -54.37) * mm, "end": v(55.23, -54.33) * mm});
            skArc(sketch, "E14.75.7", {"start": v(53.9, -53.9) * mm, "mid": v(54.48, -54.14) * mm, "end": v(55.07, -54.36) * mm});
            skLineSegment(sketch, "E14.75.8", {"start": v(53.86, -53.86) * mm, "end": v(53.1, -53.1) * mm});
            skArc(sketch, "E14.75.9", {"start": v(53.1, -53.1) * mm, "mid": v(52.98, -53.05) * mm, "end": v(52.88, -53.1) * mm});
            skArc(sketch, "E14.76.0", {"start": v(57.08, -48.55) * mm, "mid": v(57.04, -48.66) * mm, "end": v(57.1, -48.76) * mm});
            skLineSegment(sketch, "E14.76.1", {"start": v(57.92, -49.47) * mm, "end": v(57.1, -48.76) * mm});
            skArc(sketch, "E14.76.2", {"start": v(57.96, -49.51) * mm, "mid": v(58.25, -50.07) * mm, "end": v(58.52, -50.63) * mm});
            skArc(sketch, "E14.76.3", {"start": v(58.5, -50.8) * mm, "mid": v(58.53, -50.72) * mm, "end": v(58.52, -50.63) * mm});
            skLineSegment(sketch, "E14.76.4", {"start": v(58.5, -50.8) * mm, "end": v(58.25, -51.08) * mm});
            skLineSegment(sketch, "E14.76.5", {"start": v(58, -51.36) * mm, "end": v(58.25, -51.08) * mm});
            skArc(sketch, "E14.76.6", {"start": v(57.84, -51.4) * mm, "mid": v(57.92, -51.4) * mm, "end": v(58, -51.36) * mm});
            skArc(sketch, "E14.76.7", {"start": v(56.65, -51) * mm, "mid": v(57.24, -51.21) * mm, "end": v(57.84, -51.4) * mm});
            skLineSegment(sketch, "E14.76.8", {"start": v(56.6, -50.97) * mm, "end": v(55.8, -50.24) * mm});
            skArc(sketch, "E14.76.9", {"start": v(55.8, -50.24) * mm, "mid": v(55.69, -50.2) * mm, "end": v(55.58, -50.25) * mm});
            skArc(sketch, "E14.77.0", {"start": v(59.54, -45.5) * mm, "mid": v(59.5, -45.6) * mm, "end": v(59.57, -45.7) * mm});
            skLineSegment(sketch, "E14.77.1", {"start": v(60.43, -46.37) * mm, "end": v(59.57, -45.7) * mm});
            skArc(sketch, "E14.77.2", {"start": v(60.47, -46.41) * mm, "mid": v(60.79, -46.95) * mm, "end": v(61.08, -47.5) * mm});
            skArc(sketch, "E14.77.3", {"start": v(61.07, -47.67) * mm, "mid": v(61.1, -47.59) * mm, "end": v(61.08, -47.5) * mm});
            skLineSegment(sketch, "E14.77.4", {"start": v(61.07, -47.67) * mm, "end": v(60.84, -47.96) * mm});
            skLineSegment(sketch, "E14.77.5", {"start": v(60.6, -48.26) * mm, "end": v(60.84, -47.96) * mm});
            skArc(sketch, "E14.77.6", {"start": v(60.45, -48.3) * mm, "mid": v(60.54, -48.3) * mm, "end": v(60.6, -48.26) * mm});
            skArc(sketch, "E14.77.7", {"start": v(59.25, -47.96) * mm, "mid": v(59.84, -48.15) * mm, "end": v(60.45, -48.3) * mm});
            skLineSegment(sketch, "E14.77.8", {"start": v(59.2, -47.94) * mm, "end": v(58.35, -47.25) * mm});
            skArc(sketch, "E14.77.9", {"start": v(58.35, -47.25) * mm, "mid": v(58.24, -47.22) * mm, "end": v(58.14, -47.27) * mm});
            skArc(sketch, "E14.78.0", {"start": v(61.84, -42.32) * mm, "mid": v(61.81, -42.43) * mm, "end": v(61.88, -42.53) * mm});
            skLineSegment(sketch, "E14.78.1", {"start": v(62.78, -43.14) * mm, "end": v(61.88, -42.53) * mm});
            skArc(sketch, "E14.78.2", {"start": v(62.81, -43.18) * mm, "mid": v(63.16, -43.7) * mm, "end": v(63.49, -44.24) * mm});
            skArc(sketch, "E14.78.3", {"start": v(63.48, -44.4) * mm, "mid": v(63.5, -44.32) * mm, "end": v(63.49, -44.24) * mm});
            skLineSegment(sketch, "E14.78.4", {"start": v(63.48, -44.4) * mm, "end": v(63.27, -44.71) * mm});
            skLineSegment(sketch, "E14.78.5", {"start": v(63.05, -45.02) * mm, "end": v(63.27, -44.71) * mm});
            skArc(sketch, "E14.78.6", {"start": v(62.9, -45.08) * mm, "mid": v(62.98, -45.07) * mm, "end": v(63.05, -45.02) * mm});
            skArc(sketch, "E14.78.7", {"start": v(61.67, -44.8) * mm, "mid": v(62.28, -44.95) * mm, "end": v(62.9, -45.08) * mm});
            skLineSegment(sketch, "E14.78.8", {"start": v(61.62, -44.77) * mm, "end": v(60.74, -44.13) * mm});
            skArc(sketch, "E14.78.9", {"start": v(60.74, -44.13) * mm, "mid": v(60.63, -44.1) * mm, "end": v(60.53, -44.17) * mm});
            skArc(sketch, "E14.79.0", {"start": v(63.97, -39.02) * mm, "mid": v(63.95, -39.14) * mm, "end": v(64.02, -39.23) * mm});
            skLineSegment(sketch, "E14.79.1", {"start": v(64.95, -39.8) * mm, "end": v(64.02, -39.23) * mm});
            skArc(sketch, "E14.79.2", {"start": v(64.99, -39.84) * mm, "mid": v(65.36, -40.34) * mm, "end": v(65.72, -40.86) * mm});
            skArc(sketch, "E14.79.3", {"start": v(65.72, -41.02) * mm, "mid": v(65.74, -40.94) * mm, "end": v(65.72, -40.86) * mm});
            skLineSegment(sketch, "E14.79.4", {"start": v(65.72, -41.02) * mm, "end": v(65.52, -41.34) * mm});
            skLineSegment(sketch, "E14.79.5", {"start": v(65.32, -41.66) * mm, "end": v(65.52, -41.34) * mm});
            skArc(sketch, "E14.79.6", {"start": v(65.17, -41.72) * mm, "mid": v(65.25, -41.71) * mm, "end": v(65.32, -41.66) * mm});
            skArc(sketch, "E14.79.7", {"start": v(63.93, -41.5) * mm, "mid": v(64.55, -41.63) * mm, "end": v(65.17, -41.72) * mm});
            skLineSegment(sketch, "E14.79.8", {"start": v(63.88, -41.49) * mm, "end": v(62.97, -40.9) * mm});
            skArc(sketch, "E14.79.9", {"start": v(62.97, -40.9) * mm, "mid": v(62.85, -40.87) * mm, "end": v(62.76, -40.94) * mm});
            skArc(sketch, "E14.80.0", {"start": v(65.92, -35.62) * mm, "mid": v(65.91, -35.74) * mm, "end": v(65.98, -35.83) * mm});
            skLineSegment(sketch, "E14.80.1", {"start": v(66.94, -36.35) * mm, "end": v(65.98, -35.83) * mm});
            skArc(sketch, "E14.80.2", {"start": v(66.98, -36.38) * mm, "mid": v(67.38, -36.86) * mm, "end": v(67.76, -37.36) * mm});
            skArc(sketch, "E14.80.3", {"start": v(67.77, -37.53) * mm, "mid": v(67.8, -37.44) * mm, "end": v(67.76, -37.36) * mm});
            skLineSegment(sketch, "E14.80.4", {"start": v(67.77, -37.53) * mm, "end": v(67.6, -37.85) * mm});
            skLineSegment(sketch, "E14.80.5", {"start": v(67.4, -38.18) * mm, "end": v(67.6, -37.85) * mm});
            skArc(sketch, "E14.80.6", {"start": v(67.26, -38.26) * mm, "mid": v(67.35, -38.24) * mm, "end": v(67.4, -38.18) * mm});
            skArc(sketch, "E14.80.7", {"start": v(66.02, -38.1) * mm, "mid": v(66.64, -38.2) * mm, "end": v(67.26, -38.26) * mm});
            skLineSegment(sketch, "E14.80.8", {"start": v(65.97, -38.09) * mm, "end": v(65.02, -37.54) * mm});
            skArc(sketch, "E14.80.9", {"start": v(65.02, -37.54) * mm, "mid": v(64.9, -37.53) * mm, "end": v(64.82, -37.6) * mm});
            skArc(sketch, "E14.81.0", {"start": v(67.7, -32.12) * mm, "mid": v(67.7, -32.24) * mm, "end": v(67.77, -32.32) * mm});
            skLineSegment(sketch, "E14.81.1", {"start": v(68.75, -32.8) * mm, "end": v(67.77, -32.32) * mm});
            skArc(sketch, "E14.81.2", {"start": v(68.8, -32.83) * mm, "mid": v(69.22, -33.29) * mm, "end": v(69.63, -33.76) * mm});
            skArc(sketch, "E14.81.3", {"start": v(69.65, -33.93) * mm, "mid": v(69.66, -33.84) * mm, "end": v(69.63, -33.76) * mm});
            skLineSegment(sketch, "E14.81.4", {"start": v(69.65, -33.93) * mm, "end": v(69.48, -34.26) * mm});
            skLineSegment(sketch, "E14.81.5", {"start": v(69.31, -34.6) * mm, "end": v(69.48, -34.26) * mm});
            skArc(sketch, "E14.81.6", {"start": v(69.17, -34.68) * mm, "mid": v(69.26, -34.66) * mm, "end": v(69.31, -34.6) * mm});
            skArc(sketch, "E14.81.7", {"start": v(67.92, -34.6) * mm, "mid": v(68.55, -34.65) * mm, "end": v(69.17, -34.68) * mm});
            skLineSegment(sketch, "E14.81.8", {"start": v(67.87, -34.58) * mm, "end": v(66.9, -34.09) * mm});
            skArc(sketch, "E14.81.9", {"start": v(66.9, -34.09) * mm, "mid": v(66.78, -34.08) * mm, "end": v(66.7, -34.15) * mm});
            skArc(sketch, "E14.82.0", {"start": v(69.28, -28.53) * mm, "mid": v(69.28, -28.65) * mm, "end": v(69.37, -28.73) * mm});
            skLineSegment(sketch, "E14.82.1", {"start": v(70.37, -29.15) * mm, "end": v(69.37, -28.73) * mm});
            skArc(sketch, "E14.82.2", {"start": v(70.42, -29.18) * mm, "mid": v(70.87, -29.62) * mm, "end": v(71.3, -30.07) * mm});
            skArc(sketch, "E14.82.3", {"start": v(71.33, -30.24) * mm, "mid": v(71.34, -30.15) * mm, "end": v(71.3, -30.07) * mm});
            skLineSegment(sketch, "E14.82.4", {"start": v(71.33, -30.24) * mm, "end": v(71.18, -30.58) * mm});
            skLineSegment(sketch, "E14.82.5", {"start": v(71.03, -30.93) * mm, "end": v(71.18, -30.58) * mm});
            skArc(sketch, "E14.82.6", {"start": v(70.9, -31.02) * mm, "mid": v(70.97, -31) * mm, "end": v(71.03, -30.93) * mm});
            skArc(sketch, "E14.82.7", {"start": v(69.64, -31) * mm, "mid": v(70.27, -31.02) * mm, "end": v(70.9, -31.02) * mm});
            skLineSegment(sketch, "E14.82.8", {"start": v(69.59, -30.98) * mm, "end": v(68.6, -30.54) * mm});
            skArc(sketch, "E14.82.9", {"start": v(68.6, -30.54) * mm, "mid": v(68.47, -30.54) * mm, "end": v(68.39, -30.62) * mm});
            skArc(sketch, "E14.83.0", {"start": v(70.68, -24.87) * mm, "mid": v(70.69, -24.99) * mm, "end": v(70.78, -25.06) * mm});
            skLineSegment(sketch, "E14.83.1", {"start": v(71.8, -25.43) * mm, "end": v(70.78, -25.06) * mm});
            skArc(sketch, "E14.83.2", {"start": v(71.85, -25.45) * mm, "mid": v(72.32, -25.87) * mm, "end": v(72.77, -26.3) * mm});
            skArc(sketch, "E14.83.3", {"start": v(72.81, -26.46) * mm, "mid": v(72.82, -26.38) * mm, "end": v(72.77, -26.3) * mm});
            skLineSegment(sketch, "E14.83.4", {"start": v(72.81, -26.46) * mm, "end": v(72.68, -26.81) * mm});
            skLineSegment(sketch, "E14.83.5", {"start": v(72.55, -27.17) * mm, "end": v(72.68, -26.81) * mm});
            skArc(sketch, "E14.83.6", {"start": v(72.42, -27.26) * mm, "mid": v(72.5, -27.23) * mm, "end": v(72.55, -27.17) * mm});
            skArc(sketch, "E14.83.7", {"start": v(71.17, -27.3) * mm, "mid": v(71.8, -27.3) * mm, "end": v(72.42, -27.26) * mm});
            skLineSegment(sketch, "E14.83.8", {"start": v(71.11, -27.3) * mm, "end": v(70.1, -26.9) * mm});
            skArc(sketch, "E14.83.9", {"start": v(70.1, -26.9) * mm, "mid": v(69.98, -26.91) * mm, "end": v(69.9, -27) * mm});
            skArc(sketch, "E14.84.0", {"start": v(71.89, -21.14) * mm, "mid": v(71.9, -21.25) * mm, "end": v(72, -21.32) * mm});
            skLineSegment(sketch, "E14.84.1", {"start": v(73.03, -21.63) * mm, "end": v(72, -21.32) * mm});
            skArc(sketch, "E14.84.2", {"start": v(73.08, -21.66) * mm, "mid": v(73.57, -22.05) * mm, "end": v(74.05, -22.46) * mm});
            skArc(sketch, "E14.84.3", {"start": v(74.1, -22.61) * mm, "mid": v(74.1, -22.53) * mm, "end": v(74.05, -22.46) * mm});
            skLineSegment(sketch, "E14.84.4", {"start": v(74.1, -22.61) * mm, "end": v(73.99, -22.97) * mm});
            skLineSegment(sketch, "E14.84.5", {"start": v(73.87, -23.33) * mm, "end": v(73.99, -22.97) * mm});
            skArc(sketch, "E14.84.6", {"start": v(73.75, -23.44) * mm, "mid": v(73.83, -23.4) * mm, "end": v(73.87, -23.33) * mm});
            skArc(sketch, "E14.84.7", {"start": v(72.5, -23.55) * mm, "mid": v(73.12, -23.5) * mm, "end": v(73.75, -23.44) * mm});
            skLineSegment(sketch, "E14.84.8", {"start": v(72.44, -23.54) * mm, "end": v(71.4, -23.2) * mm});
            skArc(sketch, "E14.84.9", {"start": v(71.4, -23.2) * mm, "mid": v(71.3, -23.21) * mm, "end": v(71.22, -23.3) * mm});
            skArc(sketch, "E14.85.0", {"start": v(72.9, -17.34) * mm, "mid": v(72.91, -17.46) * mm, "end": v(73, -17.53) * mm});
            skLineSegment(sketch, "E14.85.1", {"start": v(74.07, -17.78) * mm, "end": v(73, -17.53) * mm});
            skArc(sketch, "E14.85.2", {"start": v(74.12, -17.8) * mm, "mid": v(74.63, -18.17) * mm, "end": v(75.12, -18.55) * mm});
            skArc(sketch, "E14.85.3", {"start": v(75.18, -18.7) * mm, "mid": v(75.17, -18.62) * mm, "end": v(75.12, -18.55) * mm});
            skLineSegment(sketch, "E14.85.4", {"start": v(75.18, -18.7) * mm, "end": v(75.09, -19.07) * mm});
            skLineSegment(sketch, "E14.85.5", {"start": v(75, -19.43) * mm, "end": v(75.09, -19.07) * mm});
            skArc(sketch, "E14.85.6", {"start": v(74.87, -19.54) * mm, "mid": v(74.95, -19.5) * mm, "end": v(75, -19.43) * mm});
            skArc(sketch, "E14.85.7", {"start": v(73.63, -19.72) * mm, "mid": v(74.25, -19.64) * mm, "end": v(74.87, -19.54) * mm});
            skLineSegment(sketch, "E14.85.8", {"start": v(73.58, -19.71) * mm, "end": v(72.52, -19.43) * mm});
            skArc(sketch, "E14.85.9", {"start": v(72.52, -19.43) * mm, "mid": v(72.4, -19.45) * mm, "end": v(72.34, -19.54) * mm});
            skArc(sketch, "E14.86.0", {"start": v(73.7, -13.5) * mm, "mid": v(73.73, -13.62) * mm, "end": v(73.82, -13.68) * mm});
            skLineSegment(sketch, "E14.86.1", {"start": v(74.9, -13.88) * mm, "end": v(73.82, -13.68) * mm});
            skArc(sketch, "E14.86.2", {"start": v(74.95, -13.9) * mm, "mid": v(75.48, -14.24) * mm, "end": v(76, -14.6) * mm});
            skArc(sketch, "E14.86.3", {"start": v(76.05, -14.75) * mm, "mid": v(76.05, -14.66) * mm, "end": v(76, -14.6) * mm});
            skLineSegment(sketch, "E14.86.4", {"start": v(76.05, -14.75) * mm, "end": v(75.98, -15.11) * mm});
            skLineSegment(sketch, "E14.86.5", {"start": v(75.9, -15.48) * mm, "end": v(75.98, -15.11) * mm});
            skArc(sketch, "E14.86.6", {"start": v(75.8, -15.6) * mm, "mid": v(75.87, -15.56) * mm, "end": v(75.9, -15.48) * mm});
            skArc(sketch, "E14.86.7", {"start": v(74.56, -15.84) * mm, "mid": v(75.18, -15.73) * mm, "end": v(75.8, -15.6) * mm});
            skLineSegment(sketch, "E14.86.8", {"start": v(74.5, -15.84) * mm, "end": v(73.44, -15.61) * mm});
            skArc(sketch, "E14.86.9", {"start": v(73.44, -15.61) * mm, "mid": v(73.33, -15.63) * mm, "end": v(73.26, -15.73) * mm});
            skArc(sketch, "E14.87.0", {"start": v(74.3, -9.63) * mm, "mid": v(74.34, -9.74) * mm, "end": v(74.44, -9.8) * mm});
            skLineSegment(sketch, "E14.87.1", {"start": v(75.52, -9.94) * mm, "end": v(74.44, -9.8) * mm});
            skArc(sketch, "E14.87.2", {"start": v(75.57, -9.96) * mm, "mid": v(76.12, -10.27) * mm, "end": v(76.65, -10.6) * mm});
            skArc(sketch, "E14.87.3", {"start": v(76.72, -10.74) * mm, "mid": v(76.7, -10.66) * mm, "end": v(76.65, -10.6) * mm});
            skLineSegment(sketch, "E14.87.4", {"start": v(76.72, -10.74) * mm, "end": v(76.67, -11.12) * mm});
            skLineSegment(sketch, "E14.87.5", {"start": v(76.61, -11.49) * mm, "end": v(76.67, -11.12) * mm});
            skArc(sketch, "E14.87.6", {"start": v(76.5, -11.61) * mm, "mid": v(76.58, -11.57) * mm, "end": v(76.61, -11.49) * mm});
            skArc(sketch, "E14.87.7", {"start": v(75.29, -11.91) * mm, "mid": v(75.9, -11.77) * mm, "end": v(76.5, -11.61) * mm});
            skLineSegment(sketch, "E14.87.8", {"start": v(75.23, -11.92) * mm, "end": v(74.16, -11.75) * mm});
            skArc(sketch, "E14.87.9", {"start": v(74.16, -11.75) * mm, "mid": v(74.04, -11.77) * mm, "end": v(73.98, -11.87) * mm});
            skArc(sketch, "E14.88.0", {"start": v(74.71, -5.73) * mm, "mid": v(74.75, -5.84) * mm, "end": v(74.85, -5.9) * mm});
            skLineSegment(sketch, "E14.88.1", {"start": v(75.94, -5.98) * mm, "end": v(74.85, -5.9) * mm});
            skArc(sketch, "E14.88.2", {"start": v(76, -6) * mm, "mid": v(76.55, -6.27) * mm, "end": v(77.1, -6.57) * mm});
            skArc(sketch, "E14.88.3", {"start": v(77.18, -6.71) * mm, "mid": v(77.16, -6.63) * mm, "end": v(77.1, -6.57) * mm});
            skLineSegment(sketch, "E14.88.4", {"start": v(77.18, -6.71) * mm, "end": v(77.15, -7.09) * mm});
            skLineSegment(sketch, "E14.88.5", {"start": v(77.1, -7.46) * mm, "end": v(77.15, -7.09) * mm});
            skArc(sketch, "E14.88.6", {"start": v(77, -7.6) * mm, "mid": v(77.08, -7.54) * mm, "end": v(77.1, -7.46) * mm});
            skArc(sketch, "E14.88.7", {"start": v(75.81, -7.96) * mm, "mid": v(76.41, -7.78) * mm, "end": v(77, -7.6) * mm});
            skLineSegment(sketch, "E14.88.8", {"start": v(75.75, -7.96) * mm, "end": v(74.67, -7.85) * mm});
            skArc(sketch, "E14.88.9", {"start": v(74.67, -7.85) * mm, "mid": v(74.56, -7.88) * mm, "end": v(74.5, -7.98) * mm});
            skArc(sketch, "E14.89.0", {"start": v(74.9, -1.8) * mm, "mid": v(74.95, -1.92) * mm, "end": v(75.06, -1.97) * mm});
            skLineSegment(sketch, "E14.89.1", {"start": v(76.15, -2) * mm, "end": v(75.06, -1.97) * mm});
            skArc(sketch, "E14.89.2", {"start": v(76.2, -2) * mm, "mid": v(76.77, -2.26) * mm, "end": v(77.34, -2.52) * mm});
            skArc(sketch, "E14.89.3", {"start": v(77.42, -2.67) * mm, "mid": v(77.4, -2.58) * mm, "end": v(77.34, -2.52) * mm});
            skLineSegment(sketch, "E14.89.4", {"start": v(77.42, -2.67) * mm, "end": v(77.41, -3.04) * mm});
            skLineSegment(sketch, "E14.89.5", {"start": v(77.4, -3.42) * mm, "end": v(77.41, -3.04) * mm});
            skArc(sketch, "E14.89.6", {"start": v(77.3, -3.55) * mm, "mid": v(77.37, -3.5) * mm, "end": v(77.4, -3.42) * mm});
            skArc(sketch, "E14.89.7", {"start": v(76.12, -3.98) * mm, "mid": v(76.71, -3.77) * mm, "end": v(77.3, -3.55) * mm});
            skLineSegment(sketch, "E14.89.8", {"start": v(76.07, -3.99) * mm, "end": v(74.98, -3.93) * mm});
            skArc(sketch, "E14.89.9", {"start": v(74.98, -3.93) * mm, "mid": v(74.87, -3.97) * mm, "end": v(74.82, -4.07) * mm});
            skArc(sketch, "E14.90.0", {"start": v(74.9, 2.11) * mm, "mid": v(74.95, 2) * mm, "end": v(75.06, 1.97) * mm});
            skLineSegment(sketch, "E14.90.1", {"start": v(76.15, 2) * mm, "end": v(75.06, 1.97) * mm});
            skArc(sketch, "E14.90.2", {"start": v(76.2, 1.99) * mm, "mid": v(76.79, 1.77) * mm, "end": v(77.37, 1.53) * mm});
            skArc(sketch, "E14.90.3", {"start": v(77.46, 1.39) * mm, "mid": v(77.43, 1.47) * mm, "end": v(77.37, 1.53) * mm});
            skLineSegment(sketch, "E14.90.4", {"start": v(77.46, 1.39) * mm, "end": v(77.46, 1.01) * mm});
            skLineSegment(sketch, "E14.90.5", {"start": v(77.47, 0.64) * mm, "end": v(77.46, 1.01) * mm});
            skArc(sketch, "E14.90.6", {"start": v(77.38, 0.5) * mm, "mid": v(77.44, 0.56) * mm, "end": v(77.47, 0.64) * mm});
            skArc(sketch, "E14.90.7", {"start": v(76.23, 0.01) * mm, "mid": v(76.8, 0.25) * mm, "end": v(77.38, 0.5) * mm});
            skLineSegment(sketch, "E14.90.8", {"start": v(76.17, 0) * mm, "end": v(75.08, 0) * mm});
            skArc(sketch, "E14.90.9", {"start": v(75.08, 0) * mm, "mid": v(74.97, -0.04) * mm, "end": v(74.93, -0.15) * mm});
            skArc(sketch, "E14.91.0", {"start": v(74.69, 6.03) * mm, "mid": v(74.74, 5.93) * mm, "end": v(74.85, 5.9) * mm});
            skLineSegment(sketch, "E14.91.1", {"start": v(75.94, 5.98) * mm, "end": v(74.85, 5.9) * mm});
            skArc(sketch, "E14.91.2", {"start": v(76, 5.97) * mm, "mid": v(76.59, 5.78) * mm, "end": v(77.18, 5.57) * mm});
            skArc(sketch, "E14.91.3", {"start": v(77.28, 5.44) * mm, "mid": v(77.25, 5.52) * mm, "end": v(77.18, 5.57) * mm});
            skLineSegment(sketch, "E14.91.4", {"start": v(77.28, 5.44) * mm, "end": v(77.3, 5.07) * mm});
            skLineSegment(sketch, "E14.91.5", {"start": v(77.33, 4.7) * mm, "end": v(77.3, 5.07) * mm});
            skArc(sketch, "E14.91.6", {"start": v(77.25, 4.55) * mm, "mid": v(77.3, 4.6) * mm, "end": v(77.33, 4.7) * mm});
            skArc(sketch, "E14.91.7", {"start": v(76.12, 4) * mm, "mid": v(76.69, 4.26) * mm, "end": v(77.25, 4.55) * mm});
            skLineSegment(sketch, "E14.91.8", {"start": v(76.07, 3.99) * mm, "end": v(74.98, 3.93) * mm});
            skArc(sketch, "E14.91.9", {"start": v(74.98, 3.93) * mm, "mid": v(74.87, 3.88) * mm, "end": v(74.84, 3.77) * mm});
            skArc(sketch, "E14.92.0", {"start": v(74.27, 9.93) * mm, "mid": v(74.33, 9.83) * mm, "end": v(74.44, 9.8) * mm});
            skLineSegment(sketch, "E14.92.1", {"start": v(75.52, 9.94) * mm, "end": v(74.44, 9.8) * mm});
            skArc(sketch, "E14.92.2", {"start": v(75.58, 9.94) * mm, "mid": v(76.18, 9.78) * mm, "end": v(76.78, 9.6) * mm});
            skArc(sketch, "E14.92.3", {"start": v(76.89, 9.48) * mm, "mid": v(76.85, 9.56) * mm, "end": v(76.78, 9.6) * mm});
            skLineSegment(sketch, "E14.92.4", {"start": v(76.89, 9.48) * mm, "end": v(76.93, 9.1) * mm});
            skLineSegment(sketch, "E14.92.5", {"start": v(76.98, 8.73) * mm, "end": v(76.93, 9.1) * mm});
            skArc(sketch, "E14.92.6", {"start": v(76.9, 8.59) * mm, "mid": v(76.96, 8.65) * mm, "end": v(76.98, 8.73) * mm});
            skArc(sketch, "E14.92.7", {"start": v(75.8, 7.98) * mm, "mid": v(76.36, 8.27) * mm, "end": v(76.9, 8.59) * mm});
            skLineSegment(sketch, "E14.92.8", {"start": v(75.75, 7.96) * mm, "end": v(74.67, 7.85) * mm});
            skArc(sketch, "E14.92.9", {"start": v(74.67, 7.85) * mm, "mid": v(74.57, 7.8) * mm, "end": v(74.54, 7.68) * mm});
            skArc(sketch, "E14.93.0", {"start": v(73.65, 13.8) * mm, "mid": v(73.71, 13.7) * mm, "end": v(73.82, 13.68) * mm});
            skLineSegment(sketch, "E14.93.1", {"start": v(74.9, 13.88) * mm, "end": v(73.82, 13.68) * mm});
            skArc(sketch, "E14.93.2", {"start": v(74.95, 13.88) * mm, "mid": v(75.57, 13.76) * mm, "end": v(76.17, 13.6) * mm});
            skArc(sketch, "E14.93.3", {"start": v(76.29, 13.49) * mm, "mid": v(76.25, 13.57) * mm, "end": v(76.17, 13.6) * mm});
            skLineSegment(sketch, "E14.93.4", {"start": v(76.29, 13.49) * mm, "end": v(76.35, 13.12) * mm});
            skLineSegment(sketch, "E14.93.5", {"start": v(76.41, 12.75) * mm, "end": v(76.35, 13.12) * mm});
            skArc(sketch, "E14.93.6", {"start": v(76.35, 12.6) * mm, "mid": v(76.4, 12.66) * mm, "end": v(76.41, 12.75) * mm});
            skArc(sketch, "E14.93.7", {"start": v(75.29, 11.93) * mm, "mid": v(75.82, 12.26) * mm, "end": v(76.35, 12.6) * mm});
            skLineSegment(sketch, "E14.93.8", {"start": v(75.23, 11.92) * mm, "end": v(74.16, 11.75) * mm});
            skArc(sketch, "E14.93.9", {"start": v(74.16, 11.75) * mm, "mid": v(74.06, 11.68) * mm, "end": v(74.03, 11.57) * mm});
            skArc(sketch, "E14.94.0", {"start": v(72.82, 17.64) * mm, "mid": v(72.9, 17.55) * mm, "end": v(73, 17.53) * mm});
            skLineSegment(sketch, "E14.94.1", {"start": v(74.07, 17.78) * mm, "end": v(73, 17.53) * mm});
            skArc(sketch, "E14.94.2", {"start": v(74.12, 17.78) * mm, "mid": v(74.74, 17.7) * mm, "end": v(75.36, 17.58) * mm});
            skArc(sketch, "E14.94.3", {"start": v(75.48, 17.46) * mm, "mid": v(75.43, 17.54) * mm, "end": v(75.36, 17.58) * mm});
            skLineSegment(sketch, "E14.94.4", {"start": v(75.48, 17.46) * mm, "end": v(75.56, 17.1) * mm});
            skLineSegment(sketch, "E14.94.5", {"start": v(75.64, 16.73) * mm, "end": v(75.56, 17.1) * mm});
            skArc(sketch, "E14.94.6", {"start": v(75.58, 16.58) * mm, "mid": v(75.64, 16.65) * mm, "end": v(75.64, 16.73) * mm});
            skArc(sketch, "E14.94.7", {"start": v(74.56, 15.86) * mm, "mid": v(75.08, 16.2) * mm, "end": v(75.58, 16.58) * mm});
            skLineSegment(sketch, "E14.94.8", {"start": v(74.5, 15.84) * mm, "end": v(73.44, 15.61) * mm});
            skArc(sketch, "E14.94.9", {"start": v(73.44, 15.61) * mm, "mid": v(73.35, 15.54) * mm, "end": v(73.32, 15.43) * mm});
            skArc(sketch, "E14.95.0", {"start": v(71.8, 21.43) * mm, "mid": v(71.87, 21.34) * mm, "end": v(72, 21.32) * mm});
            skLineSegment(sketch, "E14.95.1", {"start": v(73.03, 21.63) * mm, "end": v(72, 21.32) * mm});
            skArc(sketch, "E14.95.2", {"start": v(73.1, 21.64) * mm, "mid": v(73.71, 21.58) * mm, "end": v(74.33, 21.5) * mm});
            skArc(sketch, "E14.95.3", {"start": v(74.46, 21.39) * mm, "mid": v(74.41, 21.46) * mm, "end": v(74.33, 21.5) * mm});
            skLineSegment(sketch, "E14.95.4", {"start": v(74.46, 21.39) * mm, "end": v(74.56, 21.03) * mm});
            skLineSegment(sketch, "E14.95.5", {"start": v(74.66, 20.67) * mm, "end": v(74.56, 21.03) * mm});
            skArc(sketch, "E14.95.6", {"start": v(74.61, 20.5) * mm, "mid": v(74.66, 20.58) * mm, "end": v(74.66, 20.67) * mm});
            skArc(sketch, "E14.95.7", {"start": v(73.63, 19.74) * mm, "mid": v(74.13, 20.12) * mm, "end": v(74.61, 20.5) * mm});
            skLineSegment(sketch, "E14.95.8", {"start": v(73.58, 19.71) * mm, "end": v(72.52, 19.43) * mm});
            skArc(sketch, "E14.95.9", {"start": v(72.52, 19.43) * mm, "mid": v(72.43, 19.36) * mm, "end": v(72.42, 19.25) * mm});
            skArc(sketch, "E14.96.0", {"start": v(70.58, 25.16) * mm, "mid": v(70.66, 25.07) * mm, "end": v(70.78, 25.06) * mm});
            skLineSegment(sketch, "E14.96.1", {"start": v(71.8, 25.43) * mm, "end": v(70.78, 25.06) * mm});
            skArc(sketch, "E14.96.2", {"start": v(71.86, 25.44) * mm, "mid": v(72.48, 25.4) * mm, "end": v(73.1, 25.36) * mm});
            skArc(sketch, "E14.96.3", {"start": v(73.24, 25.26) * mm, "mid": v(73.19, 25.33) * mm, "end": v(73.1, 25.36) * mm});
            skLineSegment(sketch, "E14.96.4", {"start": v(73.24, 25.26) * mm, "end": v(73.36, 24.9) * mm});
            skLineSegment(sketch, "E14.96.5", {"start": v(73.48, 24.55) * mm, "end": v(73.36, 24.9) * mm});
            skArc(sketch, "E14.96.6", {"start": v(73.44, 24.39) * mm, "mid": v(73.48, 24.46) * mm, "end": v(73.48, 24.55) * mm});
            skArc(sketch, "E14.96.7", {"start": v(72.5, 23.57) * mm, "mid": v(72.97, 23.97) * mm, "end": v(73.44, 24.39) * mm});
            skLineSegment(sketch, "E14.96.8", {"start": v(72.44, 23.54) * mm, "end": v(71.4, 23.2) * mm});
            skArc(sketch, "E14.96.9", {"start": v(71.4, 23.2) * mm, "mid": v(71.32, 23.13) * mm, "end": v(71.3, 23) * mm});
            skArc(sketch, "E14.97.0", {"start": v(69.17, 28.81) * mm, "mid": v(69.25, 28.73) * mm, "end": v(69.37, 28.73) * mm});
            skLineSegment(sketch, "E14.97.1", {"start": v(70.37, 29.15) * mm, "end": v(69.37, 28.73) * mm});
            skArc(sketch, "E14.97.2", {"start": v(70.43, 29.16) * mm, "mid": v(71.05, 29.17) * mm, "end": v(71.68, 29.15) * mm});
            skArc(sketch, "E14.97.3", {"start": v(71.82, 29.06) * mm, "mid": v(71.76, 29.12) * mm, "end": v(71.68, 29.15) * mm});
            skLineSegment(sketch, "E14.97.4", {"start": v(71.82, 29.06) * mm, "end": v(71.96, 28.7) * mm});
            skLineSegment(sketch, "E14.97.5", {"start": v(72.1, 28.36) * mm, "end": v(71.96, 28.7) * mm});
            skArc(sketch, "E14.97.6", {"start": v(72.06, 28.2) * mm, "mid": v(72.1, 28.27) * mm, "end": v(72.1, 28.36) * mm});
            skArc(sketch, "E14.97.7", {"start": v(71.16, 27.33) * mm, "mid": v(71.62, 27.75) * mm, "end": v(72.06, 28.2) * mm});
            skLineSegment(sketch, "E14.97.8", {"start": v(71.11, 27.3) * mm, "end": v(70.1, 26.9) * mm});
            skArc(sketch, "E14.97.9", {"start": v(70.1, 26.9) * mm, "mid": v(70.01, 26.83) * mm, "end": v(70, 26.71) * mm});
            skArc(sketch, "E14.98.0", {"start": v(67.57, 32.4) * mm, "mid": v(67.65, 32.32) * mm, "end": v(67.77, 32.32) * mm});
            skLineSegment(sketch, "E14.98.1", {"start": v(68.75, 32.8) * mm, "end": v(67.77, 32.32) * mm});
            skArc(sketch, "E14.98.2", {"start": v(68.8, 32.8) * mm, "mid": v(69.43, 32.84) * mm, "end": v(70.06, 32.86) * mm});
            skArc(sketch, "E14.98.3", {"start": v(70.2, 32.77) * mm, "mid": v(70.14, 32.84) * mm, "end": v(70.06, 32.86) * mm});
            skLineSegment(sketch, "E14.98.4", {"start": v(70.2, 32.77) * mm, "end": v(70.36, 32.43) * mm});
            skLineSegment(sketch, "E14.98.5", {"start": v(70.51, 32.1) * mm, "end": v(70.36, 32.43) * mm});
            skArc(sketch, "E14.98.6", {"start": v(70.49, 31.93) * mm, "mid": v(70.52, 32) * mm, "end": v(70.51, 32.1) * mm});
            skArc(sketch, "E14.98.7", {"start": v(69.63, 31.01) * mm, "mid": v(70.07, 31.46) * mm, "end": v(70.49, 31.93) * mm});
            skLineSegment(sketch, "E14.98.8", {"start": v(69.59, 30.98) * mm, "end": v(68.6, 30.54) * mm});
            skArc(sketch, "E14.98.9", {"start": v(68.6, 30.54) * mm, "mid": v(68.51, 30.45) * mm, "end": v(68.51, 30.34) * mm});
            skArc(sketch, "E14.99.0", {"start": v(65.78, 35.89) * mm, "mid": v(65.87, 35.81) * mm, "end": v(65.98, 35.83) * mm});
            skLineSegment(sketch, "E14.99.1", {"start": v(66.94, 36.35) * mm, "end": v(65.98, 35.83) * mm});
            skArc(sketch, "E14.99.2", {"start": v(67, 36.36) * mm, "mid": v(67.62, 36.43) * mm, "end": v(68.24, 36.48) * mm});
            skArc(sketch, "E14.99.3", {"start": v(68.38, 36.4) * mm, "mid": v(68.32, 36.46) * mm, "end": v(68.24, 36.48) * mm});
            skLineSegment(sketch, "E14.99.4", {"start": v(68.38, 36.4) * mm, "end": v(68.56, 36.07) * mm});
            skLineSegment(sketch, "E14.99.5", {"start": v(68.73, 35.74) * mm, "end": v(68.56, 36.07) * mm});
            skArc(sketch, "E14.99.6", {"start": v(68.72, 35.57) * mm, "mid": v(68.75, 35.65) * mm, "end": v(68.73, 35.74) * mm});
            skArc(sketch, "E14.99.7", {"start": v(67.91, 34.62) * mm, "mid": v(68.32, 35.09) * mm, "end": v(68.72, 35.57) * mm});
            skLineSegment(sketch, "E14.99.8", {"start": v(67.87, 34.58) * mm, "end": v(66.9, 34.09) * mm});
            skArc(sketch, "E14.99.9", {"start": v(66.9, 34.09) * mm, "mid": v(66.82, 34) * mm, "end": v(66.83, 33.88) * mm});
            skArc(sketch, "E14.100.0", {"start": v(63.8, 39.28) * mm, "mid": v(63.9, 39.21) * mm, "end": v(64.02, 39.23) * mm});
            skLineSegment(sketch, "E14.100.1", {"start": v(64.95, 39.8) * mm, "end": v(64.02, 39.23) * mm});
            skArc(sketch, "E14.100.2", {"start": v(65, 39.82) * mm, "mid": v(65.62, 39.92) * mm, "end": v(66.24, 40) * mm});
            skArc(sketch, "E14.100.3", {"start": v(66.39, 39.93) * mm, "mid": v(66.32, 39.99) * mm, "end": v(66.24, 40) * mm});
            skLineSegment(sketch, "E14.100.4", {"start": v(66.39, 39.93) * mm, "end": v(66.58, 39.61) * mm});
            skLineSegment(sketch, "E14.100.5", {"start": v(66.77, 39.29) * mm, "end": v(66.58, 39.61) * mm});
            skArc(sketch, "E14.100.6", {"start": v(66.76, 39.12) * mm, "mid": v(66.8, 39.2) * mm, "end": v(66.77, 39.29) * mm});
            skArc(sketch, "E14.100.7", {"start": v(66, 38.12) * mm, "mid": v(66.4, 38.62) * mm, "end": v(66.76, 39.12) * mm});
            skLineSegment(sketch, "E14.100.8", {"start": v(65.97, 38.09) * mm, "end": v(65.02, 37.54) * mm});
            skArc(sketch, "E14.100.9", {"start": v(65.02, 37.54) * mm, "mid": v(64.95, 37.45) * mm, "end": v(64.97, 37.33) * mm});
            skArc(sketch, "E14.101.0", {"start": v(61.67, 42.57) * mm, "mid": v(61.76, 42.5) * mm, "end": v(61.88, 42.53) * mm});
            skLineSegment(sketch, "E14.101.1", {"start": v(62.78, 43.14) * mm, "end": v(61.88, 42.53) * mm});
            skArc(sketch, "E14.101.2", {"start": v(62.83, 43.17) * mm, "mid": v(63.44, 43.3) * mm, "end": v(64.05, 43.42) * mm});
            skArc(sketch, "E14.101.3", {"start": v(64.2, 43.35) * mm, "mid": v(64.14, 43.4) * mm, "end": v(64.05, 43.42) * mm});
            skLineSegment(sketch, "E14.101.4", {"start": v(64.2, 43.35) * mm, "end": v(64.42, 43.04) * mm});
            skLineSegment(sketch, "E14.101.5", {"start": v(64.62, 42.73) * mm, "end": v(64.42, 43.04) * mm});
            skArc(sketch, "E14.101.6", {"start": v(64.62, 42.56) * mm, "mid": v(64.65, 42.65) * mm, "end": v(64.62, 42.73) * mm});
            skArc(sketch, "E14.101.7", {"start": v(63.92, 41.52) * mm, "mid": v(64.28, 42.04) * mm, "end": v(64.62, 42.56) * mm});
            skLineSegment(sketch, "E14.101.8", {"start": v(63.88, 41.49) * mm, "end": v(62.97, 40.9) * mm});
            skArc(sketch, "E14.101.9", {"start": v(62.97, 40.9) * mm, "mid": v(62.9, 40.8) * mm, "end": v(62.92, 40.68) * mm});
            skArc(sketch, "E14.102.0", {"start": v(59.35, 45.74) * mm, "mid": v(59.45, 45.68) * mm, "end": v(59.57, 45.7) * mm});
            skLineSegment(sketch, "E14.102.1", {"start": v(60.43, 46.37) * mm, "end": v(59.57, 45.7) * mm});
            skArc(sketch, "E14.102.2", {"start": v(60.48, 46.4) * mm, "mid": v(61.08, 46.56) * mm, "end": v(61.7, 46.7) * mm});
            skArc(sketch, "E14.102.3", {"start": v(61.85, 46.65) * mm, "mid": v(61.78, 46.7) * mm, "end": v(61.7, 46.7) * mm});
            skLineSegment(sketch, "E14.102.4", {"start": v(61.85, 46.65) * mm, "end": v(62.07, 46.35) * mm});
            skLineSegment(sketch, "E14.102.5", {"start": v(62.3, 46.05) * mm, "end": v(62.07, 46.35) * mm});
            skArc(sketch, "E14.102.6", {"start": v(62.3, 45.89) * mm, "mid": v(62.33, 45.97) * mm, "end": v(62.3, 46.05) * mm});
            skArc(sketch, "E14.102.7", {"start": v(61.66, 44.81) * mm, "mid": v(62, 45.34) * mm, "end": v(62.3, 45.89) * mm});
            skLineSegment(sketch, "E14.102.8", {"start": v(61.62, 44.77) * mm, "end": v(60.74, 44.13) * mm});
            skArc(sketch, "E14.102.9", {"start": v(60.74, 44.13) * mm, "mid": v(60.68, 44.03) * mm, "end": v(60.7, 43.92) * mm});
            skArc(sketch, "E14.103.0", {"start": v(56.88, 48.78) * mm, "mid": v(56.98, 48.73) * mm, "end": v(57.1, 48.76) * mm});
            skLineSegment(sketch, "E14.103.1", {"start": v(57.92, 49.47) * mm, "end": v(57.1, 48.76) * mm});
            skArc(sketch, "E14.103.2", {"start": v(57.97, 49.5) * mm, "mid": v(58.56, 49.7) * mm, "end": v(59.16, 49.87) * mm});
            skArc(sketch, "E14.103.3", {"start": v(59.32, 49.83) * mm, "mid": v(59.25, 49.87) * mm, "end": v(59.16, 49.87) * mm});
            skLineSegment(sketch, "E14.103.4", {"start": v(59.32, 49.83) * mm, "end": v(59.56, 49.54) * mm});
            skLineSegment(sketch, "E14.103.5", {"start": v(59.8, 49.25) * mm, "end": v(59.56, 49.54) * mm});
            skArc(sketch, "E14.103.6", {"start": v(59.82, 49.08) * mm, "mid": v(59.84, 49.17) * mm, "end": v(59.8, 49.25) * mm});
            skArc(sketch, "E14.103.7", {"start": v(59.23, 47.98) * mm, "mid": v(59.54, 48.53) * mm, "end": v(59.82, 49.08) * mm});
            skLineSegment(sketch, "E14.103.8", {"start": v(59.2, 47.94) * mm, "end": v(58.35, 47.25) * mm});
            skArc(sketch, "E14.103.9", {"start": v(58.35, 47.25) * mm, "mid": v(58.3, 47.15) * mm, "end": v(58.33, 47.04) * mm});
            skArc(sketch, "E14.104.0", {"start": v(54.25, 51.69) * mm, "mid": v(54.35, 51.64) * mm, "end": v(54.46, 51.68) * mm});
            skLineSegment(sketch, "E14.104.1", {"start": v(55.25, 52.43) * mm, "end": v(54.46, 51.68) * mm});
            skArc(sketch, "E14.104.2", {"start": v(55.3, 52.46) * mm, "mid": v(55.88, 52.7) * mm, "end": v(56.47, 52.9) * mm});
            skArc(sketch, "E14.104.3", {"start": v(56.63, 52.86) * mm, "mid": v(56.56, 52.9) * mm, "end": v(56.47, 52.9) * mm});
            skLineSegment(sketch, "E14.104.4", {"start": v(56.63, 52.86) * mm, "end": v(56.89, 52.59) * mm});
            skLineSegment(sketch, "E14.104.5", {"start": v(57.14, 52.31) * mm, "end": v(56.89, 52.59) * mm});
            skArc(sketch, "E14.104.6", {"start": v(57.17, 52.15) * mm, "mid": v(57.18, 52.23) * mm, "end": v(57.14, 52.31) * mm});
            skArc(sketch, "E14.104.7", {"start": v(56.64, 51.01) * mm, "mid": v(56.91, 51.58) * mm, "end": v(57.17, 52.15) * mm});
            skLineSegment(sketch, "E14.104.8", {"start": v(56.6, 50.97) * mm, "end": v(55.8, 50.24) * mm});
            skArc(sketch, "E14.104.9", {"start": v(55.8, 50.24) * mm, "mid": v(55.75, 50.13) * mm, "end": v(55.79, 50.02) * mm});
            skArc(sketch, "E14.105.0", {"start": v(51.47, 54.46) * mm, "mid": v(51.58, 54.42) * mm, "end": v(51.68, 54.46) * mm});
            skLineSegment(sketch, "E14.105.1", {"start": v(52.43, 55.25) * mm, "end": v(51.68, 54.46) * mm});
            skArc(sketch, "E14.105.2", {"start": v(52.48, 55.29) * mm, "mid": v(53.05, 55.54) * mm, "end": v(53.63, 55.78) * mm});
            skArc(sketch, "E14.105.3", {"start": v(53.79, 55.75) * mm, "mid": v(53.71, 55.8) * mm, "end": v(53.63, 55.78) * mm});
            skLineSegment(sketch, "E14.105.4", {"start": v(53.79, 55.75) * mm, "end": v(54.06, 55.5) * mm});
            skLineSegment(sketch, "E14.105.5", {"start": v(54.33, 55.23) * mm, "end": v(54.06, 55.5) * mm});
            skArc(sketch, "E14.105.6", {"start": v(54.36, 55.07) * mm, "mid": v(54.37, 55.15) * mm, "end": v(54.33, 55.23) * mm});
            skArc(sketch, "E14.105.7", {"start": v(53.9, 53.9) * mm, "mid": v(54.14, 54.48) * mm, "end": v(54.36, 55.07) * mm});
            skLineSegment(sketch, "E14.105.8", {"start": v(53.86, 53.86) * mm, "end": v(53.1, 53.1) * mm});
            skArc(sketch, "E14.105.9", {"start": v(53.1, 53.1) * mm, "mid": v(53.05, 52.98) * mm, "end": v(53.1, 52.88) * mm});
            skArc(sketch, "E14.106.0", {"start": v(48.55, 57.08) * mm, "mid": v(48.66, 57.04) * mm, "end": v(48.76, 57.1) * mm});
            skLineSegment(sketch, "E14.106.1", {"start": v(49.47, 57.92) * mm, "end": v(48.76, 57.1) * mm});
            skArc(sketch, "E14.106.2", {"start": v(49.51, 57.96) * mm, "mid": v(50.07, 58.25) * mm, "end": v(50.63, 58.52) * mm});
            skArc(sketch, "E14.106.3", {"start": v(50.8, 58.5) * mm, "mid": v(50.72, 58.53) * mm, "end": v(50.63, 58.52) * mm});
            skLineSegment(sketch, "E14.106.4", {"start": v(50.8, 58.5) * mm, "end": v(51.08, 58.25) * mm});
            skLineSegment(sketch, "E14.106.5", {"start": v(51.36, 58) * mm, "end": v(51.08, 58.25) * mm});
            skArc(sketch, "E14.106.6", {"start": v(51.4, 57.84) * mm, "mid": v(51.4, 57.92) * mm, "end": v(51.36, 58) * mm});
            skArc(sketch, "E14.106.7", {"start": v(51, 56.65) * mm, "mid": v(51.21, 57.24) * mm, "end": v(51.4, 57.84) * mm});
            skLineSegment(sketch, "E14.106.8", {"start": v(50.97, 56.6) * mm, "end": v(50.24, 55.8) * mm});
            skArc(sketch, "E14.106.9", {"start": v(50.24, 55.8) * mm, "mid": v(50.2, 55.69) * mm, "end": v(50.25, 55.58) * mm});
            skArc(sketch, "E14.107.0", {"start": v(45.5, 59.54) * mm, "mid": v(45.6, 59.5) * mm, "end": v(45.7, 59.57) * mm});
            skLineSegment(sketch, "E14.107.1", {"start": v(46.37, 60.43) * mm, "end": v(45.7, 59.57) * mm});
            skArc(sketch, "E14.107.2", {"start": v(46.41, 60.47) * mm, "mid": v(46.95, 60.79) * mm, "end": v(47.5, 61.08) * mm});
            skArc(sketch, "E14.107.3", {"start": v(47.67, 61.07) * mm, "mid": v(47.59, 61.1) * mm, "end": v(47.5, 61.08) * mm});
            skLineSegment(sketch, "E14.107.4", {"start": v(47.67, 61.07) * mm, "end": v(47.96, 60.84) * mm});
            skLineSegment(sketch, "E14.107.5", {"start": v(48.26, 60.6) * mm, "end": v(47.96, 60.84) * mm});
            skArc(sketch, "E14.107.6", {"start": v(48.3, 60.45) * mm, "mid": v(48.3, 60.54) * mm, "end": v(48.26, 60.6) * mm});
            skArc(sketch, "E14.107.7", {"start": v(47.96, 59.25) * mm, "mid": v(48.15, 59.84) * mm, "end": v(48.3, 60.45) * mm});
            skLineSegment(sketch, "E14.107.8", {"start": v(47.94, 59.2) * mm, "end": v(47.25, 58.35) * mm});
            skArc(sketch, "E14.107.9", {"start": v(47.25, 58.35) * mm, "mid": v(47.22, 58.24) * mm, "end": v(47.27, 58.14) * mm});
            skArc(sketch, "E14.108.0", {"start": v(42.32, 61.84) * mm, "mid": v(42.43, 61.81) * mm, "end": v(42.53, 61.88) * mm});
            skLineSegment(sketch, "E14.108.1", {"start": v(43.14, 62.78) * mm, "end": v(42.53, 61.88) * mm});
            skArc(sketch, "E14.108.2", {"start": v(43.18, 62.81) * mm, "mid": v(43.7, 63.16) * mm, "end": v(44.24, 63.49) * mm});
            skArc(sketch, "E14.108.3", {"start": v(44.4, 63.48) * mm, "mid": v(44.32, 63.5) * mm, "end": v(44.24, 63.49) * mm});
            skLineSegment(sketch, "E14.108.4", {"start": v(44.4, 63.48) * mm, "end": v(44.71, 63.27) * mm});
            skLineSegment(sketch, "E14.108.5", {"start": v(45.02, 63.05) * mm, "end": v(44.71, 63.27) * mm});
            skArc(sketch, "E14.108.6", {"start": v(45.08, 62.9) * mm, "mid": v(45.07, 62.98) * mm, "end": v(45.02, 63.05) * mm});
            skArc(sketch, "E14.108.7", {"start": v(44.8, 61.67) * mm, "mid": v(44.95, 62.28) * mm, "end": v(45.08, 62.9) * mm});
            skLineSegment(sketch, "E14.108.8", {"start": v(44.77, 61.62) * mm, "end": v(44.13, 60.74) * mm});
            skArc(sketch, "E14.108.9", {"start": v(44.13, 60.74) * mm, "mid": v(44.1, 60.63) * mm, "end": v(44.17, 60.53) * mm});
            skArc(sketch, "E14.109.0", {"start": v(39.02, 63.97) * mm, "mid": v(39.14, 63.95) * mm, "end": v(39.23, 64.02) * mm});
            skLineSegment(sketch, "E14.109.1", {"start": v(39.8, 64.95) * mm, "end": v(39.23, 64.02) * mm});
            skArc(sketch, "E14.109.2", {"start": v(39.84, 64.99) * mm, "mid": v(40.34, 65.36) * mm, "end": v(40.86, 65.72) * mm});
            skArc(sketch, "E14.109.3", {"start": v(41.02, 65.72) * mm, "mid": v(40.94, 65.74) * mm, "end": v(40.86, 65.72) * mm});
            skLineSegment(sketch, "E14.109.4", {"start": v(41.02, 65.72) * mm, "end": v(41.34, 65.52) * mm});
            skLineSegment(sketch, "E14.109.5", {"start": v(41.66, 65.32) * mm, "end": v(41.34, 65.52) * mm});
            skArc(sketch, "E14.109.6", {"start": v(41.72, 65.17) * mm, "mid": v(41.71, 65.25) * mm, "end": v(41.66, 65.32) * mm});
            skArc(sketch, "E14.109.7", {"start": v(41.5, 63.93) * mm, "mid": v(41.63, 64.55) * mm, "end": v(41.72, 65.17) * mm});
            skLineSegment(sketch, "E14.109.8", {"start": v(41.49, 63.88) * mm, "end": v(40.9, 62.97) * mm});
            skArc(sketch, "E14.109.9", {"start": v(40.9, 62.97) * mm, "mid": v(40.87, 62.85) * mm, "end": v(40.94, 62.76) * mm});
            skArc(sketch, "E14.110.0", {"start": v(35.62, 65.92) * mm, "mid": v(35.74, 65.91) * mm, "end": v(35.83, 65.98) * mm});
            skLineSegment(sketch, "E14.110.1", {"start": v(36.35, 66.94) * mm, "end": v(35.83, 65.98) * mm});
            skArc(sketch, "E14.110.2", {"start": v(36.38, 66.98) * mm, "mid": v(36.86, 67.38) * mm, "end": v(37.36, 67.76) * mm});
            skArc(sketch, "E14.110.3", {"start": v(37.53, 67.77) * mm, "mid": v(37.44, 67.8) * mm, "end": v(37.36, 67.76) * mm});
            skLineSegment(sketch, "E14.110.4", {"start": v(37.53, 67.77) * mm, "end": v(37.85, 67.6) * mm});
            skLineSegment(sketch, "E14.110.5", {"start": v(38.18, 67.4) * mm, "end": v(37.85, 67.6) * mm});
            skArc(sketch, "E14.110.6", {"start": v(38.26, 67.26) * mm, "mid": v(38.24, 67.35) * mm, "end": v(38.18, 67.4) * mm});
            skArc(sketch, "E14.110.7", {"start": v(38.1, 66.02) * mm, "mid": v(38.2, 66.64) * mm, "end": v(38.26, 67.26) * mm});
            skLineSegment(sketch, "E14.110.8", {"start": v(38.09, 65.97) * mm, "end": v(37.54, 65.02) * mm});
            skArc(sketch, "E14.110.9", {"start": v(37.54, 65.02) * mm, "mid": v(37.53, 64.9) * mm, "end": v(37.6, 64.82) * mm});
            skArc(sketch, "E14.111.0", {"start": v(32.12, 67.7) * mm, "mid": v(32.24, 67.7) * mm, "end": v(32.32, 67.77) * mm});
            skLineSegment(sketch, "E14.111.1", {"start": v(32.8, 68.75) * mm, "end": v(32.32, 67.77) * mm});
            skArc(sketch, "E14.111.2", {"start": v(32.83, 68.8) * mm, "mid": v(33.29, 69.22) * mm, "end": v(33.76, 69.63) * mm});
            skArc(sketch, "E14.111.3", {"start": v(33.93, 69.65) * mm, "mid": v(33.84, 69.66) * mm, "end": v(33.76, 69.63) * mm});
            skLineSegment(sketch, "E14.111.4", {"start": v(33.93, 69.65) * mm, "end": v(34.26, 69.48) * mm});
            skLineSegment(sketch, "E14.111.5", {"start": v(34.6, 69.31) * mm, "end": v(34.26, 69.48) * mm});
            skArc(sketch, "E14.111.6", {"start": v(34.68, 69.17) * mm, "mid": v(34.66, 69.26) * mm, "end": v(34.6, 69.31) * mm});
            skArc(sketch, "E14.111.7", {"start": v(34.6, 67.92) * mm, "mid": v(34.65, 68.55) * mm, "end": v(34.68, 69.17) * mm});
            skLineSegment(sketch, "E14.111.8", {"start": v(34.58, 67.87) * mm, "end": v(34.09, 66.9) * mm});
            skArc(sketch, "E14.111.9", {"start": v(34.09, 66.9) * mm, "mid": v(34.08, 66.78) * mm, "end": v(34.15, 66.7) * mm});
            skArc(sketch, "E14.112.0", {"start": v(28.53, 69.28) * mm, "mid": v(28.65, 69.28) * mm, "end": v(28.73, 69.37) * mm});
            skLineSegment(sketch, "E14.112.1", {"start": v(29.15, 70.37) * mm, "end": v(28.73, 69.37) * mm});
            skArc(sketch, "E14.112.2", {"start": v(29.18, 70.42) * mm, "mid": v(29.62, 70.87) * mm, "end": v(30.07, 71.3) * mm});
            skArc(sketch, "E14.112.3", {"start": v(30.24, 71.33) * mm, "mid": v(30.15, 71.34) * mm, "end": v(30.07, 71.3) * mm});
            skLineSegment(sketch, "E14.112.4", {"start": v(30.24, 71.33) * mm, "end": v(30.58, 71.18) * mm});
            skLineSegment(sketch, "E14.112.5", {"start": v(30.93, 71.03) * mm, "end": v(30.58, 71.18) * mm});
            skArc(sketch, "E14.112.6", {"start": v(31.02, 70.9) * mm, "mid": v(31, 70.97) * mm, "end": v(30.93, 71.03) * mm});
            skArc(sketch, "E14.112.7", {"start": v(31, 69.64) * mm, "mid": v(31.02, 70.27) * mm, "end": v(31.02, 70.9) * mm});
            skLineSegment(sketch, "E14.112.8", {"start": v(30.98, 69.59) * mm, "end": v(30.54, 68.6) * mm});
            skArc(sketch, "E14.112.9", {"start": v(30.54, 68.6) * mm, "mid": v(30.54, 68.47) * mm, "end": v(30.62, 68.39) * mm});
            skArc(sketch, "E14.113.0", {"start": v(24.87, 70.68) * mm, "mid": v(24.99, 70.69) * mm, "end": v(25.06, 70.78) * mm});
            skLineSegment(sketch, "E14.113.1", {"start": v(25.43, 71.8) * mm, "end": v(25.06, 70.78) * mm});
            skArc(sketch, "E14.113.2", {"start": v(25.45, 71.85) * mm, "mid": v(25.87, 72.32) * mm, "end": v(26.3, 72.77) * mm});
            skArc(sketch, "E14.113.3", {"start": v(26.46, 72.81) * mm, "mid": v(26.38, 72.82) * mm, "end": v(26.3, 72.77) * mm});
            skLineSegment(sketch, "E14.113.4", {"start": v(26.46, 72.81) * mm, "end": v(26.81, 72.68) * mm});
            skLineSegment(sketch, "E14.113.5", {"start": v(27.17, 72.55) * mm, "end": v(26.81, 72.68) * mm});
            skArc(sketch, "E14.113.6", {"start": v(27.26, 72.42) * mm, "mid": v(27.23, 72.5) * mm, "end": v(27.17, 72.55) * mm});
            skArc(sketch, "E14.113.7", {"start": v(27.3, 71.17) * mm, "mid": v(27.3, 71.8) * mm, "end": v(27.26, 72.42) * mm});
            skLineSegment(sketch, "E14.113.8", {"start": v(27.3, 71.11) * mm, "end": v(26.9, 70.1) * mm});
            skArc(sketch, "E14.113.9", {"start": v(26.9, 70.1) * mm, "mid": v(26.91, 69.98) * mm, "end": v(27, 69.9) * mm});
            skArc(sketch, "E14.114.0", {"start": v(21.14, 71.89) * mm, "mid": v(21.25, 71.9) * mm, "end": v(21.32, 72) * mm});
            skLineSegment(sketch, "E14.114.1", {"start": v(21.63, 73.03) * mm, "end": v(21.32, 72) * mm});
            skArc(sketch, "E14.114.2", {"start": v(21.66, 73.08) * mm, "mid": v(22.05, 73.57) * mm, "end": v(22.46, 74.05) * mm});
            skArc(sketch, "E14.114.3", {"start": v(22.61, 74.1) * mm, "mid": v(22.53, 74.1) * mm, "end": v(22.46, 74.05) * mm});
            skLineSegment(sketch, "E14.114.4", {"start": v(22.61, 74.1) * mm, "end": v(22.97, 73.99) * mm});
            skLineSegment(sketch, "E14.114.5", {"start": v(23.33, 73.87) * mm, "end": v(22.97, 73.99) * mm});
            skArc(sketch, "E14.114.6", {"start": v(23.44, 73.75) * mm, "mid": v(23.4, 73.83) * mm, "end": v(23.33, 73.87) * mm});
            skArc(sketch, "E14.114.7", {"start": v(23.55, 72.5) * mm, "mid": v(23.5, 73.12) * mm, "end": v(23.44, 73.75) * mm});
            skLineSegment(sketch, "E14.114.8", {"start": v(23.54, 72.44) * mm, "end": v(23.2, 71.4) * mm});
            skArc(sketch, "E14.114.9", {"start": v(23.2, 71.4) * mm, "mid": v(23.21, 71.3) * mm, "end": v(23.3, 71.22) * mm});
            skArc(sketch, "E14.115.0", {"start": v(17.34, 72.9) * mm, "mid": v(17.46, 72.91) * mm, "end": v(17.53, 73) * mm});
            skLineSegment(sketch, "E14.115.1", {"start": v(17.78, 74.07) * mm, "end": v(17.53, 73) * mm});
            skArc(sketch, "E14.115.2", {"start": v(17.8, 74.12) * mm, "mid": v(18.17, 74.63) * mm, "end": v(18.55, 75.12) * mm});
            skArc(sketch, "E14.115.3", {"start": v(18.7, 75.18) * mm, "mid": v(18.62, 75.17) * mm, "end": v(18.55, 75.12) * mm});
            skLineSegment(sketch, "E14.115.4", {"start": v(18.7, 75.18) * mm, "end": v(19.07, 75.09) * mm});
            skLineSegment(sketch, "E14.115.5", {"start": v(19.43, 75) * mm, "end": v(19.07, 75.09) * mm});
            skArc(sketch, "E14.115.6", {"start": v(19.54, 74.87) * mm, "mid": v(19.5, 74.95) * mm, "end": v(19.43, 75) * mm});
            skArc(sketch, "E14.115.7", {"start": v(19.72, 73.63) * mm, "mid": v(19.64, 74.25) * mm, "end": v(19.54, 74.87) * mm});
            skLineSegment(sketch, "E14.115.8", {"start": v(19.71, 73.58) * mm, "end": v(19.43, 72.52) * mm});
            skArc(sketch, "E14.115.9", {"start": v(19.43, 72.52) * mm, "mid": v(19.45, 72.4) * mm, "end": v(19.54, 72.34) * mm});
            skArc(sketch, "E14.116.0", {"start": v(13.5, 73.7) * mm, "mid": v(13.62, 73.73) * mm, "end": v(13.68, 73.82) * mm});
            skLineSegment(sketch, "E14.116.1", {"start": v(13.88, 74.9) * mm, "end": v(13.68, 73.82) * mm});
            skArc(sketch, "E14.116.2", {"start": v(13.9, 74.95) * mm, "mid": v(14.24, 75.48) * mm, "end": v(14.6, 76) * mm});
            skArc(sketch, "E14.116.3", {"start": v(14.75, 76.05) * mm, "mid": v(14.66, 76.05) * mm, "end": v(14.6, 76) * mm});
            skLineSegment(sketch, "E14.116.4", {"start": v(14.75, 76.05) * mm, "end": v(15.11, 75.98) * mm});
            skLineSegment(sketch, "E14.116.5", {"start": v(15.48, 75.9) * mm, "end": v(15.11, 75.98) * mm});
            skArc(sketch, "E14.116.6", {"start": v(15.6, 75.8) * mm, "mid": v(15.56, 75.87) * mm, "end": v(15.48, 75.9) * mm});
            skArc(sketch, "E14.116.7", {"start": v(15.84, 74.56) * mm, "mid": v(15.73, 75.18) * mm, "end": v(15.6, 75.8) * mm});
            skLineSegment(sketch, "E14.116.8", {"start": v(15.84, 74.5) * mm, "end": v(15.61, 73.44) * mm});
            skArc(sketch, "E14.116.9", {"start": v(15.61, 73.44) * mm, "mid": v(15.63, 73.33) * mm, "end": v(15.73, 73.26) * mm});
            skArc(sketch, "E14.117.0", {"start": v(9.63, 74.3) * mm, "mid": v(9.74, 74.34) * mm, "end": v(9.8, 74.44) * mm});
            skLineSegment(sketch, "E14.117.1", {"start": v(9.94, 75.52) * mm, "end": v(9.8, 74.44) * mm});
            skArc(sketch, "E14.117.2", {"start": v(9.96, 75.57) * mm, "mid": v(10.27, 76.12) * mm, "end": v(10.6, 76.65) * mm});
            skArc(sketch, "E14.117.3", {"start": v(10.74, 76.72) * mm, "mid": v(10.66, 76.7) * mm, "end": v(10.6, 76.65) * mm});
            skLineSegment(sketch, "E14.117.4", {"start": v(10.74, 76.72) * mm, "end": v(11.12, 76.67) * mm});
            skLineSegment(sketch, "E14.117.5", {"start": v(11.49, 76.61) * mm, "end": v(11.12, 76.67) * mm});
            skArc(sketch, "E14.117.6", {"start": v(11.61, 76.5) * mm, "mid": v(11.57, 76.58) * mm, "end": v(11.49, 76.61) * mm});
            skArc(sketch, "E14.117.7", {"start": v(11.91, 75.29) * mm, "mid": v(11.77, 75.9) * mm, "end": v(11.61, 76.5) * mm});
            skLineSegment(sketch, "E14.117.8", {"start": v(11.92, 75.23) * mm, "end": v(11.75, 74.16) * mm});
            skArc(sketch, "E14.117.9", {"start": v(11.75, 74.16) * mm, "mid": v(11.77, 74.04) * mm, "end": v(11.87, 73.98) * mm});
            skArc(sketch, "E14.118.0", {"start": v(5.73, 74.71) * mm, "mid": v(5.84, 74.75) * mm, "end": v(5.9, 74.85) * mm});
            skLineSegment(sketch, "E14.118.1", {"start": v(5.98, 75.94) * mm, "end": v(5.9, 74.85) * mm});
            skArc(sketch, "E14.118.2", {"start": v(6, 76) * mm, "mid": v(6.27, 76.55) * mm, "end": v(6.57, 77.1) * mm});
            skArc(sketch, "E14.118.3", {"start": v(6.71, 77.18) * mm, "mid": v(6.63, 77.16) * mm, "end": v(6.57, 77.1) * mm});
            skLineSegment(sketch, "E14.118.4", {"start": v(6.71, 77.18) * mm, "end": v(7.09, 77.15) * mm});
            skLineSegment(sketch, "E14.118.5", {"start": v(7.46, 77.1) * mm, "end": v(7.09, 77.15) * mm});
            skArc(sketch, "E14.118.6", {"start": v(7.6, 77) * mm, "mid": v(7.54, 77.08) * mm, "end": v(7.46, 77.1) * mm});
            skArc(sketch, "E14.118.7", {"start": v(7.96, 75.81) * mm, "mid": v(7.78, 76.41) * mm, "end": v(7.6, 77) * mm});
            skLineSegment(sketch, "E14.118.8", {"start": v(7.96, 75.75) * mm, "end": v(7.85, 74.67) * mm});
            skArc(sketch, "E14.118.9", {"start": v(7.85, 74.67) * mm, "mid": v(7.88, 74.56) * mm, "end": v(7.98, 74.5) * mm});
            skArc(sketch, "E14.119.0", {"start": v(1.8, 74.9) * mm, "mid": v(1.92, 74.95) * mm, "end": v(1.97, 75.06) * mm});
            skLineSegment(sketch, "E14.119.1", {"start": v(2, 76.15) * mm, "end": v(1.97, 75.06) * mm});
            skArc(sketch, "E14.119.2", {"start": v(2, 76.2) * mm, "mid": v(2.26, 76.77) * mm, "end": v(2.52, 77.34) * mm});
            skArc(sketch, "E14.119.3", {"start": v(2.67, 77.42) * mm, "mid": v(2.58, 77.4) * mm, "end": v(2.52, 77.34) * mm});
            skLineSegment(sketch, "E14.119.4", {"start": v(2.67, 77.42) * mm, "end": v(3.04, 77.41) * mm});
            skLineSegment(sketch, "E14.119.5", {"start": v(3.42, 77.4) * mm, "end": v(3.04, 77.41) * mm});
            skArc(sketch, "E14.119.6", {"start": v(3.55, 77.3) * mm, "mid": v(3.5, 77.37) * mm, "end": v(3.42, 77.4) * mm});
            skArc(sketch, "E14.119.7", {"start": v(3.98, 76.12) * mm, "mid": v(3.77, 76.71) * mm, "end": v(3.55, 77.3) * mm});
            skLineSegment(sketch, "E14.119.8", {"start": v(3.99, 76.07) * mm, "end": v(3.93, 74.98) * mm});
            skArc(sketch, "E14.119.9", {"start": v(3.93, 74.98) * mm, "mid": v(3.97, 74.87) * mm, "end": v(4.07, 74.82) * mm});
            skArc(sketch, "E15.trimOffspring", {"start": v(-6.03, 74.69) * mm, "mid": v(-6.86, 74.62) * mm, "end": v(-7.68, 74.54) * mm});
            skArc(sketch, "E16.trimOffspring", {"start": v(-9.93, 74.27) * mm, "mid": v(-10.75, 74.15) * mm, "end": v(-11.57, 74.03) * mm});
            skArc(sketch, "E17.trimOffspring", {"start": v(-13.8, 73.65) * mm, "mid": v(-14.62, 73.5) * mm, "end": v(-15.43, 73.32) * mm});
            skArc(sketch, "E18.trimOffspring", {"start": v(-17.64, 72.82) * mm, "mid": v(-18.44, 72.62) * mm, "end": v(-19.25, 72.42) * mm});
            skArc(sketch, "E19.trimOffspring", {"start": v(-21.43, 71.8) * mm, "mid": v(-22.22, 71.56) * mm, "end": v(-23, 71.3) * mm});
            skArc(sketch, "E20.trimOffspring", {"start": v(-25.16, 70.58) * mm, "mid": v(-25.93, 70.3) * mm, "end": v(-26.71, 70) * mm});
            skArc(sketch, "E21.trimOffspring", {"start": v(-28.81, 69.17) * mm, "mid": v(-29.58, 68.85) * mm, "end": v(-30.34, 68.51) * mm});
            skArc(sketch, "E22.trimOffspring", {"start": v(-32.4, 67.57) * mm, "mid": v(-33.14, 67.2) * mm, "end": v(-33.88, 66.83) * mm});
            skArc(sketch, "E23.trimOffspring", {"start": v(-35.89, 65.78) * mm, "mid": v(-36.61, 65.38) * mm, "end": v(-37.33, 64.97) * mm});
            skArc(sketch, "E24.trimOffspring", {"start": v(-39.28, 63.8) * mm, "mid": v(-39.98, 63.37) * mm, "end": v(-40.68, 62.92) * mm});
            skArc(sketch, "E25.trimOffspring", {"start": v(-42.57, 61.67) * mm, "mid": v(-43.25, 61.2) * mm, "end": v(-43.92, 60.7) * mm});
            skArc(sketch, "E26.trimOffspring", {"start": v(-45.74, 59.35) * mm, "mid": v(-46.39, 58.84) * mm, "end": v(-47.04, 58.33) * mm});
            skArc(sketch, "E27.trimOffspring", {"start": v(-48.78, 56.88) * mm, "mid": v(-49.4, 56.34) * mm, "end": v(-50.02, 55.79) * mm});
            skArc(sketch, "E28.trimOffspring", {"start": v(-51.69, 54.25) * mm, "mid": v(-52.29, 53.67) * mm, "end": v(-52.88, 53.1) * mm});
            skArc(sketch, "E29.trimOffspring", {"start": v(-54.46, 51.47) * mm, "mid": v(-55.02, 50.86) * mm, "end": v(-55.58, 50.25) * mm});
            skArc(sketch, "E30.trimOffspring", {"start": v(-57.08, 48.55) * mm, "mid": v(-57.6, 47.91) * mm, "end": v(-58.14, 47.27) * mm});
            skArc(sketch, "E31.trimOffspring", {"start": v(-59.54, 45.5) * mm, "mid": v(-60.04, 44.83) * mm, "end": v(-60.53, 44.17) * mm});
            skArc(sketch, "E32.trimOffspring", {"start": v(-61.84, 42.32) * mm, "mid": v(-62.3, 41.63) * mm, "end": v(-62.76, 40.94) * mm});
            skArc(sketch, "E33.trimOffspring", {"start": v(-63.97, 39.02) * mm, "mid": v(-64.4, 38.31) * mm, "end": v(-64.82, 37.6) * mm});
            skArc(sketch, "E34.trimOffspring", {"start": v(-65.92, 35.62) * mm, "mid": v(-66.31, 34.89) * mm, "end": v(-66.7, 34.15) * mm});
            skArc(sketch, "E35.trimOffspring", {"start": v(-67.7, 32.12) * mm, "mid": v(-68.05, 31.37) * mm, "end": v(-68.39, 30.62) * mm});
            skArc(sketch, "E36.trimOffspring", {"start": v(-69.28, 28.53) * mm, "mid": v(-69.6, 27.77) * mm, "end": v(-69.9, 27) * mm});
            skArc(sketch, "E37.trimOffspring", {"start": v(-70.68, 24.87) * mm, "mid": v(-70.95, 24.09) * mm, "end": v(-71.22, 23.3) * mm});
            skArc(sketch, "E38.trimOffspring", {"start": v(-71.89, 21.14) * mm, "mid": v(-72.12, 20.34) * mm, "end": v(-72.34, 19.54) * mm});
            skArc(sketch, "E39.trimOffspring", {"start": v(-72.9, 17.34) * mm, "mid": v(-73.08, 16.54) * mm, "end": v(-73.26, 15.73) * mm});
            skArc(sketch, "E40.trimOffspring", {"start": v(-73.7, 13.5) * mm, "mid": v(-73.85, 12.69) * mm, "end": v(-73.98, 11.87) * mm});
            skArc(sketch, "E41.trimOffspring", {"start": v(-74.3, 9.63) * mm, "mid": v(-74.41, 8.8) * mm, "end": v(-74.5, 7.98) * mm});
            skArc(sketch, "E42.trimOffspring", {"start": v(-74.71, 5.73) * mm, "mid": v(-74.77, 4.9) * mm, "end": v(-74.82, 4.07) * mm});
            skArc(sketch, "E43.trimOffspring", {"start": v(-74.9, 1.8) * mm, "mid": v(-74.92, 0.98) * mm, "end": v(-74.93, 0.15) * mm});
            skArc(sketch, "E44.trimOffspring", {"start": v(-74.9, -2.11) * mm, "mid": v(-74.87, -2.94) * mm, "end": v(-74.84, -3.77) * mm});
            skArc(sketch, "E45.trimOffspring", {"start": v(-74.69, -6.03) * mm, "mid": v(-74.62, -6.86) * mm, "end": v(-74.54, -7.68) * mm});
            skArc(sketch, "E46.trimOffspring", {"start": v(-74.27, -9.93) * mm, "mid": v(-74.15, -10.75) * mm, "end": v(-74.03, -11.57) * mm});
            skArc(sketch, "E47.trimOffspring", {"start": v(-73.65, -13.8) * mm, "mid": v(-73.5, -14.62) * mm, "end": v(-73.32, -15.43) * mm});
            skArc(sketch, "E48.trimOffspring", {"start": v(-72.82, -17.64) * mm, "mid": v(-72.62, -18.44) * mm, "end": v(-72.42, -19.25) * mm});
            skArc(sketch, "E49.trimOffspring", {"start": v(-61.67, -42.57) * mm, "mid": v(-61.2, -43.25) * mm, "end": v(-60.7, -43.92) * mm});
            skLineSegment(sketch, "E50", {"start": v(-5.98, 75.94) * mm, "end": v(-5.97, 76) * mm});
            skLineSegment(sketch, "E51", {"start": v(-3.99, 76.07) * mm, "end": v(-4, 76.12) * mm});
            skLineSegment(sketch, "E52", {"start": v(-7.96, 75.75) * mm, "end": v(-7.98, 75.8) * mm});
            skLineSegment(sketch, "E53", {"start": v(-9.94, 75.52) * mm, "end": v(-9.94, 75.58) * mm});
            skLineSegment(sketch, "E54", {"start": v(-11.92, 75.23) * mm, "end": v(-11.93, 75.29) * mm});
            skLineSegment(sketch, "E55", {"start": v(-13.88, 74.9) * mm, "end": v(-13.88, 74.95) * mm});
            skLineSegment(sketch, "E56", {"start": v(-15.84, 74.5) * mm, "end": v(-15.86, 74.56) * mm});
            skLineSegment(sketch, "E57", {"start": v(-17.78, 74.07) * mm, "end": v(-17.78, 74.12) * mm});
            skLineSegment(sketch, "E58", {"start": v(-19.74, 73.63) * mm, "end": v(-19.71, 73.58) * mm});
            skLineSegment(sketch, "E59", {"start": v(-21.63, 73.03) * mm, "end": v(-21.64, 73.1) * mm});
            skLineSegment(sketch, "E60", {"start": v(-23.57, 72.5) * mm, "end": v(-23.54, 72.44) * mm});
            skLineSegment(sketch, "E61", {"start": v(-25.44, 71.86) * mm, "end": v(-25.43, 71.8) * mm});
            skLineSegment(sketch, "E62", {"start": v(-27.33, 71.16) * mm, "end": v(-27.3, 71.11) * mm});
            skLineSegment(sketch, "E63", {"start": v(-29.16, 70.43) * mm, "end": v(-29.15, 70.37) * mm});
            skLineSegment(sketch, "E64", {"start": v(-31.01, 69.63) * mm, "end": v(-30.98, 69.59) * mm});
            skLineSegment(sketch, "E65", {"start": v(-32.8, 68.75) * mm, "end": v(-32.8, 68.8) * mm});
            skLineSegment(sketch, "E66", {"start": v(-34.62, 67.91) * mm, "end": v(-34.58, 67.87) * mm});
            skLineSegment(sketch, "E67", {"start": v(-36.36, 67) * mm, "end": v(-36.35, 66.94) * mm});
            skLineSegment(sketch, "E68", {"start": v(-39.8, 64.95) * mm, "end": v(-39.82, 65) * mm});
            skLineSegment(sketch, "E69", {"start": v(-38.12, 66) * mm, "end": v(-38.09, 65.97) * mm});
            skLineSegment(sketch, "E70", {"start": v(-41.52, 63.92) * mm, "end": v(-41.49, 63.88) * mm});
            skLineSegment(sketch, "E71", {"start": v(-43.17, 62.83) * mm, "end": v(-43.14, 62.78) * mm});
            skLineSegment(sketch, "E72", {"start": v(-44.81, 61.66) * mm, "end": v(-44.77, 61.62) * mm});
            skArc(sketch, "E73.1.0", {"start": v(-5.97, 76) * mm, "mid": v(-5.98, 75.96) * mm, "end": v(-5.98, 75.94) * mm});
            skArc(sketch, "E73.1.1", {"start": v(-3.99, 76.07) * mm, "mid": v(-4, 76.1) * mm, "end": v(-4, 76.12) * mm});
            skArc(sketch, "E73.2.0", {"start": v(-9.94, 75.58) * mm, "mid": v(-9.94, 75.55) * mm, "end": v(-9.94, 75.52) * mm});
            skArc(sketch, "E73.2.1", {"start": v(-7.96, 75.75) * mm, "mid": v(-7.97, 75.78) * mm, "end": v(-7.98, 75.8) * mm});
            skArc(sketch, "E74.3.3.0", {"start": v(-13.88, 74.95) * mm, "mid": v(-13.88, 74.92) * mm, "end": v(-13.88, 74.9) * mm});
            skArc(sketch, "E74.4.3.0", {"start": v(-11.92, 75.23) * mm, "mid": v(-11.92, 75.26) * mm, "end": v(-11.93, 75.29) * mm});
            skArc(sketch, "E74.3.4.0", {"start": v(-17.78, 74.12) * mm, "mid": v(-17.79, 74.1) * mm, "end": v(-17.78, 74.07) * mm});
            skArc(sketch, "E74.4.4.0", {"start": v(-15.84, 74.5) * mm, "mid": v(-15.85, 74.53) * mm, "end": v(-15.86, 74.56) * mm});
            skArc(sketch, "E74.3.5.0", {"start": v(-21.64, 73.1) * mm, "mid": v(-21.64, 73.06) * mm, "end": v(-21.63, 73.03) * mm});
            skArc(sketch, "E74.4.5.0", {"start": v(-19.71, 73.58) * mm, "mid": v(-19.72, 73.6) * mm, "end": v(-19.74, 73.63) * mm});
            skArc(sketch, "E74.3.6.0", {"start": v(-25.44, 71.86) * mm, "mid": v(-25.43, 71.83) * mm, "end": v(-25.43, 71.8) * mm});
            skArc(sketch, "E74.4.6.0", {"start": v(-23.54, 72.44) * mm, "mid": v(-23.55, 72.47) * mm, "end": v(-23.57, 72.5) * mm});
            skArc(sketch, "E74.3.7.0", {"start": v(-29.16, 70.43) * mm, "mid": v(-29.16, 70.4) * mm, "end": v(-29.15, 70.37) * mm});
            skArc(sketch, "E74.4.7.0", {"start": v(-27.3, 71.11) * mm, "mid": v(-27.3, 71.14) * mm, "end": v(-27.33, 71.16) * mm});
            skArc(sketch, "E74.3.8.0", {"start": v(-32.8, 68.8) * mm, "mid": v(-32.8, 68.78) * mm, "end": v(-32.8, 68.75) * mm});
            skArc(sketch, "E74.4.8.0", {"start": v(-30.98, 69.59) * mm, "mid": v(-31, 69.61) * mm, "end": v(-31.01, 69.63) * mm});
            skArc(sketch, "E74.3.9.0", {"start": v(-36.36, 67) * mm, "mid": v(-36.36, 66.97) * mm, "end": v(-36.35, 66.94) * mm});
            skArc(sketch, "E74.4.9.0", {"start": v(-34.58, 67.87) * mm, "mid": v(-34.6, 67.9) * mm, "end": v(-34.62, 67.91) * mm});
            skArc(sketch, "E74.3.10.0", {"start": v(-39.82, 65) * mm, "mid": v(-39.81, 64.97) * mm, "end": v(-39.8, 64.95) * mm});
            skArc(sketch, "E74.4.10.0", {"start": v(-38.09, 65.97) * mm, "mid": v(-38.1, 65.99) * mm, "end": v(-38.12, 66) * mm});
            skArc(sketch, "E74.3.11.0", {"start": v(-43.17, 62.83) * mm, "mid": v(-43.16, 62.8) * mm, "end": v(-43.14, 62.78) * mm});
            skArc(sketch, "E74.4.11.0", {"start": v(-41.49, 63.88) * mm, "mid": v(-41.5, 63.9) * mm, "end": v(-41.52, 63.92) * mm});
            skArc(sketch, "E74.3.12.0", {"start": v(-46.4, 60.48) * mm, "mid": v(-46.39, 60.45) * mm, "end": v(-46.37, 60.43) * mm});
            skArc(sketch, "E74.4.12.0", {"start": v(-44.77, 61.62) * mm, "mid": v(-44.8, 61.65) * mm, "end": v(-44.81, 61.66) * mm});
            skArc(sketch, "E74.3.13.0", {"start": v(-49.5, 57.97) * mm, "mid": v(-49.49, 57.94) * mm, "end": v(-49.47, 57.92) * mm});
            skArc(sketch, "E74.4.13.0", {"start": v(-47.94, 59.2) * mm, "mid": v(-47.96, 59.22) * mm, "end": v(-47.98, 59.23) * mm});
            skArc(sketch, "E74.3.14.0", {"start": v(-52.46, 55.3) * mm, "mid": v(-52.45, 55.27) * mm, "end": v(-52.43, 55.25) * mm});
            skArc(sketch, "E74.4.14.0", {"start": v(-50.97, 56.6) * mm, "mid": v(-50.99, 56.63) * mm, "end": v(-51.01, 56.64) * mm});
            skArc(sketch, "E74.3.15.0", {"start": v(-55.29, 52.48) * mm, "mid": v(-55.27, 52.45) * mm, "end": v(-55.25, 52.43) * mm});
            skArc(sketch, "E74.4.15.0", {"start": v(-53.86, 53.86) * mm, "mid": v(-53.88, 53.88) * mm, "end": v(-53.9, 53.9) * mm});
            skArc(sketch, "E74.3.16.0", {"start": v(-57.96, 49.51) * mm, "mid": v(-57.94, 49.49) * mm, "end": v(-57.92, 49.47) * mm});
            skArc(sketch, "E74.4.16.0", {"start": v(-56.6, 50.97) * mm, "mid": v(-56.63, 50.99) * mm, "end": v(-56.65, 51) * mm});
            skArc(sketch, "E74.3.17.0", {"start": v(-60.47, 46.41) * mm, "mid": v(-60.45, 46.39) * mm, "end": v(-60.43, 46.37) * mm});
            skArc(sketch, "E74.4.17.0", {"start": v(-59.2, 47.94) * mm, "mid": v(-59.22, 47.95) * mm, "end": v(-59.25, 47.96) * mm});
            skArc(sketch, "E74.3.18.0", {"start": v(-62.81, 43.18) * mm, "mid": v(-62.8, 43.16) * mm, "end": v(-62.78, 43.14) * mm});
            skArc(sketch, "E74.4.18.0", {"start": v(-61.62, 44.77) * mm, "mid": v(-61.65, 44.79) * mm, "end": v(-61.67, 44.8) * mm});
            skArc(sketch, "E74.3.19.0", {"start": v(-64.99, 39.84) * mm, "mid": v(-64.97, 39.82) * mm, "end": v(-64.95, 39.8) * mm});
            skArc(sketch, "E74.4.19.0", {"start": v(-63.88, 41.49) * mm, "mid": v(-63.9, 41.5) * mm, "end": v(-63.93, 41.5) * mm});
            skArc(sketch, "E74.3.20.0", {"start": v(-66.98, 36.38) * mm, "mid": v(-66.96, 36.36) * mm, "end": v(-66.94, 36.35) * mm});
            skArc(sketch, "E74.4.20.0", {"start": v(-65.97, 38.09) * mm, "mid": v(-66, 38.1) * mm, "end": v(-66.02, 38.1) * mm});
            skArc(sketch, "E74.3.21.0", {"start": v(-68.8, 32.83) * mm, "mid": v(-68.78, 32.8) * mm, "end": v(-68.75, 32.8) * mm});
            skArc(sketch, "E74.4.21.0", {"start": v(-67.87, 34.58) * mm, "mid": v(-67.9, 34.6) * mm, "end": v(-67.92, 34.6) * mm});
            skArc(sketch, "E74.3.22.0", {"start": v(-70.42, 29.18) * mm, "mid": v(-70.4, 29.16) * mm, "end": v(-70.37, 29.15) * mm});
            skArc(sketch, "E74.4.22.0", {"start": v(-69.59, 30.98) * mm, "mid": v(-69.61, 31) * mm, "end": v(-69.64, 31) * mm});
            skArc(sketch, "E74.3.23.0", {"start": v(-71.85, 25.45) * mm, "mid": v(-71.83, 25.44) * mm, "end": v(-71.8, 25.43) * mm});
            skArc(sketch, "E74.4.23.0", {"start": v(-71.11, 27.3) * mm, "mid": v(-71.14, 27.3) * mm, "end": v(-71.17, 27.3) * mm});
            skArc(sketch, "E74.3.24.0", {"start": v(-73.08, 21.66) * mm, "mid": v(-73.06, 21.64) * mm, "end": v(-73.03, 21.63) * mm});
            skArc(sketch, "E74.4.24.0", {"start": v(-72.44, 23.54) * mm, "mid": v(-72.47, 23.54) * mm, "end": v(-72.5, 23.55) * mm});
            skArc(sketch, "E74.3.25.0", {"start": v(-74.12, 17.8) * mm, "mid": v(-74.1, 17.8) * mm, "end": v(-74.07, 17.78) * mm});
            skArc(sketch, "E74.4.25.0", {"start": v(-73.58, 19.71) * mm, "mid": v(-73.6, 19.72) * mm, "end": v(-73.63, 19.72) * mm});
            skArc(sketch, "E74.3.26.0", {"start": v(-74.95, 13.9) * mm, "mid": v(-74.92, 13.89) * mm, "end": v(-74.9, 13.88) * mm});
            skArc(sketch, "E74.4.26.0", {"start": v(-74.5, 15.84) * mm, "mid": v(-74.53, 15.84) * mm, "end": v(-74.56, 15.84) * mm});
            skArc(sketch, "E74.3.27.0", {"start": v(-75.57, 9.96) * mm, "mid": v(-75.55, 9.95) * mm, "end": v(-75.52, 9.94) * mm});
            skArc(sketch, "E74.4.27.0", {"start": v(-75.23, 11.92) * mm, "mid": v(-75.26, 11.92) * mm, "end": v(-75.29, 11.91) * mm});
            skArc(sketch, "E74.3.28.0", {"start": v(-76, 6) * mm, "mid": v(-75.96, 5.98) * mm, "end": v(-75.94, 5.98) * mm});
            skArc(sketch, "E74.4.28.0", {"start": v(-75.75, 7.96) * mm, "mid": v(-75.78, 7.96) * mm, "end": v(-75.81, 7.96) * mm});
            skArc(sketch, "E74.3.29.0", {"start": v(-76.2, 2) * mm, "mid": v(-76.17, 2) * mm, "end": v(-76.15, 2) * mm});
            skArc(sketch, "E74.4.29.0", {"start": v(-76.07, 3.99) * mm, "mid": v(-76.1, 3.99) * mm, "end": v(-76.12, 3.98) * mm});
            skArc(sketch, "E74.3.30.0", {"start": v(-76.2, -1.99) * mm, "mid": v(-76.17, -2) * mm, "end": v(-76.15, -2) * mm});
            skArc(sketch, "E74.4.30.0", {"start": v(-76.17, 0) * mm, "mid": v(-76.2, 0) * mm, "end": v(-76.23, -0.01) * mm});
            skArc(sketch, "E74.3.31.0", {"start": v(-76, -5.97) * mm, "mid": v(-75.96, -5.98) * mm, "end": v(-75.94, -5.98) * mm});
            skArc(sketch, "E74.4.31.0", {"start": v(-76.07, -3.99) * mm, "mid": v(-76.1, -4) * mm, "end": v(-76.12, -4) * mm});
            skArc(sketch, "E74.3.32.0", {"start": v(-75.58, -9.94) * mm, "mid": v(-75.55, -9.94) * mm, "end": v(-75.52, -9.94) * mm});
            skArc(sketch, "E74.4.32.0", {"start": v(-75.75, -7.96) * mm, "mid": v(-75.78, -7.97) * mm, "end": v(-75.8, -7.98) * mm});
            skArc(sketch, "E74.3.33.0", {"start": v(-74.95, -13.88) * mm, "mid": v(-74.92, -13.88) * mm, "end": v(-74.9, -13.88) * mm});
            skArc(sketch, "E74.4.33.0", {"start": v(-75.23, -11.92) * mm, "mid": v(-75.26, -11.92) * mm, "end": v(-75.29, -11.93) * mm});
            skArc(sketch, "E74.3.34.0", {"start": v(-74.12, -17.78) * mm, "mid": v(-74.1, -17.79) * mm, "end": v(-74.07, -17.78) * mm});
            skArc(sketch, "E74.4.34.0", {"start": v(-74.5, -15.84) * mm, "mid": v(-74.53, -15.85) * mm, "end": v(-74.56, -15.86) * mm});
            skArc(sketch, "E74.3.35.0", {"start": v(-73.1, -21.64) * mm, "mid": v(-73.06, -21.64) * mm, "end": v(-73.03, -21.63) * mm});
            skArc(sketch, "E74.4.35.0", {"start": v(-73.58, -19.71) * mm, "mid": v(-73.6, -19.72) * mm, "end": v(-73.63, -19.74) * mm});
            skArc(sketch, "E74.3.36.0", {"start": v(-71.86, -25.44) * mm, "mid": v(-71.83, -25.43) * mm, "end": v(-71.8, -25.43) * mm});
            skArc(sketch, "E74.4.36.0", {"start": v(-72.44, -23.54) * mm, "mid": v(-72.47, -23.55) * mm, "end": v(-72.5, -23.57) * mm});
            skArc(sketch, "E74.3.37.0", {"start": v(-70.43, -29.16) * mm, "mid": v(-70.4, -29.16) * mm, "end": v(-70.37, -29.15) * mm});
            skArc(sketch, "E74.4.37.0", {"start": v(-71.11, -27.3) * mm, "mid": v(-71.14, -27.3) * mm, "end": v(-71.16, -27.33) * mm});
            skArc(sketch, "E74.3.38.0", {"start": v(-68.8, -32.8) * mm, "mid": v(-68.78, -32.8) * mm, "end": v(-68.75, -32.8) * mm});
            skArc(sketch, "E74.4.38.0", {"start": v(-69.59, -30.98) * mm, "mid": v(-69.61, -31) * mm, "end": v(-69.63, -31.01) * mm});
            skArc(sketch, "E74.3.39.0", {"start": v(-67, -36.36) * mm, "mid": v(-66.97, -36.36) * mm, "end": v(-66.94, -36.35) * mm});
            skArc(sketch, "E74.4.39.0", {"start": v(-67.87, -34.58) * mm, "mid": v(-67.9, -34.6) * mm, "end": v(-67.91, -34.62) * mm});
            skArc(sketch, "E74.3.40.0", {"start": v(-65, -39.82) * mm, "mid": v(-64.97, -39.81) * mm, "end": v(-64.95, -39.8) * mm});
            skArc(sketch, "E74.4.40.0", {"start": v(-65.97, -38.09) * mm, "mid": v(-65.99, -38.1) * mm, "end": v(-66, -38.12) * mm});
            skArc(sketch, "E74.3.41.0", {"start": v(-62.83, -43.17) * mm, "mid": v(-62.8, -43.16) * mm, "end": v(-62.78, -43.14) * mm});
            skArc(sketch, "E74.4.41.0", {"start": v(-63.88, -41.49) * mm, "mid": v(-63.9, -41.5) * mm, "end": v(-63.92, -41.52) * mm});
            skArc(sketch, "E74.3.42.0", {"start": v(-60.48, -46.4) * mm, "mid": v(-60.45, -46.39) * mm, "end": v(-60.43, -46.37) * mm});
            skArc(sketch, "E74.4.42.0", {"start": v(-61.62, -44.77) * mm, "mid": v(-61.65, -44.8) * mm, "end": v(-61.66, -44.81) * mm});
            skArc(sketch, "E74.3.43.0", {"start": v(-57.97, -49.5) * mm, "mid": v(-57.94, -49.49) * mm, "end": v(-57.92, -49.47) * mm});
            skArc(sketch, "E74.4.43.0", {"start": v(-59.2, -47.94) * mm, "mid": v(-59.22, -47.96) * mm, "end": v(-59.23, -47.98) * mm});
            skArc(sketch, "E74.3.44.0", {"start": v(-55.3, -52.46) * mm, "mid": v(-55.27, -52.45) * mm, "end": v(-55.25, -52.43) * mm});
            skArc(sketch, "E74.4.44.0", {"start": v(-56.6, -50.97) * mm, "mid": v(-56.63, -50.99) * mm, "end": v(-56.64, -51.01) * mm});
            skArc(sketch, "E74.3.45.0", {"start": v(-52.48, -55.29) * mm, "mid": v(-52.45, -55.27) * mm, "end": v(-52.43, -55.25) * mm});
            skArc(sketch, "E74.4.45.0", {"start": v(-53.86, -53.86) * mm, "mid": v(-53.88, -53.88) * mm, "end": v(-53.9, -53.9) * mm});
            skArc(sketch, "E74.3.46.0", {"start": v(-49.51, -57.96) * mm, "mid": v(-49.49, -57.94) * mm, "end": v(-49.47, -57.92) * mm});
            skArc(sketch, "E74.4.46.0", {"start": v(-50.97, -56.6) * mm, "mid": v(-50.99, -56.63) * mm, "end": v(-51, -56.65) * mm});
            skArc(sketch, "E74.3.47.0", {"start": v(-46.41, -60.47) * mm, "mid": v(-46.39, -60.45) * mm, "end": v(-46.37, -60.43) * mm});
            skArc(sketch, "E74.4.47.0", {"start": v(-47.94, -59.2) * mm, "mid": v(-47.95, -59.22) * mm, "end": v(-47.96, -59.25) * mm});
            skArc(sketch, "E74.3.48.0", {"start": v(-43.18, -62.81) * mm, "mid": v(-43.16, -62.8) * mm, "end": v(-43.14, -62.78) * mm});
            skArc(sketch, "E74.4.48.0", {"start": v(-44.77, -61.62) * mm, "mid": v(-44.79, -61.65) * mm, "end": v(-44.8, -61.67) * mm});
            skArc(sketch, "E74.3.49.0", {"start": v(-39.84, -64.99) * mm, "mid": v(-39.82, -64.97) * mm, "end": v(-39.8, -64.95) * mm});
            skArc(sketch, "E74.4.49.0", {"start": v(-41.49, -63.88) * mm, "mid": v(-41.5, -63.9) * mm, "end": v(-41.5, -63.93) * mm});
            skArc(sketch, "E74.3.50.0", {"start": v(-36.38, -66.98) * mm, "mid": v(-36.36, -66.96) * mm, "end": v(-36.35, -66.94) * mm});
            skArc(sketch, "E74.4.50.0", {"start": v(-38.09, -65.97) * mm, "mid": v(-38.1, -66) * mm, "end": v(-38.1, -66.02) * mm});
            skArc(sketch, "E74.3.51.0", {"start": v(-32.83, -68.8) * mm, "mid": v(-32.8, -68.78) * mm, "end": v(-32.8, -68.75) * mm});
            skArc(sketch, "E74.4.51.0", {"start": v(-34.58, -67.87) * mm, "mid": v(-34.6, -67.9) * mm, "end": v(-34.6, -67.92) * mm});
            skArc(sketch, "E74.3.52.0", {"start": v(-29.18, -70.42) * mm, "mid": v(-29.16, -70.4) * mm, "end": v(-29.15, -70.37) * mm});
            skArc(sketch, "E74.4.52.0", {"start": v(-30.98, -69.59) * mm, "mid": v(-31, -69.61) * mm, "end": v(-31, -69.64) * mm});
            skArc(sketch, "E74.3.53.0", {"start": v(-25.45, -71.85) * mm, "mid": v(-25.44, -71.83) * mm, "end": v(-25.43, -71.8) * mm});
            skArc(sketch, "E74.4.53.0", {"start": v(-27.3, -71.11) * mm, "mid": v(-27.3, -71.14) * mm, "end": v(-27.3, -71.17) * mm});
            skArc(sketch, "E74.3.54.0", {"start": v(-21.66, -73.08) * mm, "mid": v(-21.64, -73.06) * mm, "end": v(-21.63, -73.03) * mm});
            skArc(sketch, "E74.4.54.0", {"start": v(-23.54, -72.44) * mm, "mid": v(-23.54, -72.47) * mm, "end": v(-23.55, -72.5) * mm});
            skArc(sketch, "E74.3.55.0", {"start": v(-17.8, -74.12) * mm, "mid": v(-17.8, -74.1) * mm, "end": v(-17.78, -74.07) * mm});
            skArc(sketch, "E74.4.55.0", {"start": v(-19.71, -73.58) * mm, "mid": v(-19.72, -73.6) * mm, "end": v(-19.72, -73.63) * mm});
            skArc(sketch, "E74.3.56.0", {"start": v(-13.9, -74.95) * mm, "mid": v(-13.89, -74.92) * mm, "end": v(-13.88, -74.9) * mm});
            skArc(sketch, "E74.4.56.0", {"start": v(-15.84, -74.5) * mm, "mid": v(-15.84, -74.53) * mm, "end": v(-15.84, -74.56) * mm});
            skArc(sketch, "E74.3.57.0", {"start": v(-9.96, -75.57) * mm, "mid": v(-9.95, -75.55) * mm, "end": v(-9.94, -75.52) * mm});
            skArc(sketch, "E74.4.57.0", {"start": v(-11.92, -75.23) * mm, "mid": v(-11.92, -75.26) * mm, "end": v(-11.91, -75.29) * mm});
            skArc(sketch, "E74.3.58.0", {"start": v(-6, -76) * mm, "mid": v(-5.98, -75.96) * mm, "end": v(-5.98, -75.94) * mm});
            skArc(sketch, "E74.4.58.0", {"start": v(-7.96, -75.75) * mm, "mid": v(-7.96, -75.78) * mm, "end": v(-7.96, -75.81) * mm});
            skArc(sketch, "E74.3.59.0", {"start": v(-2, -76.2) * mm, "mid": v(-2, -76.17) * mm, "end": v(-2, -76.15) * mm});
            skArc(sketch, "E74.4.59.0", {"start": v(-3.99, -76.07) * mm, "mid": v(-3.99, -76.1) * mm, "end": v(-3.98, -76.12) * mm});
            skArc(sketch, "E74.3.60.0", {"start": v(1.99, -76.2) * mm, "mid": v(2, -76.17) * mm, "end": v(2, -76.15) * mm});
            skArc(sketch, "E74.4.60.0", {"start": v(0, -76.17) * mm, "mid": v(0, -76.2) * mm, "end": v(0.01, -76.23) * mm});
            skArc(sketch, "E74.3.61.0", {"start": v(5.97, -76) * mm, "mid": v(5.98, -75.96) * mm, "end": v(5.98, -75.94) * mm});
            skArc(sketch, "E74.4.61.0", {"start": v(3.99, -76.07) * mm, "mid": v(4, -76.1) * mm, "end": v(4, -76.12) * mm});
            skArc(sketch, "E74.3.62.0", {"start": v(9.94, -75.58) * mm, "mid": v(9.94, -75.55) * mm, "end": v(9.94, -75.52) * mm});
            skArc(sketch, "E74.4.62.0", {"start": v(7.96, -75.75) * mm, "mid": v(7.97, -75.78) * mm, "end": v(7.98, -75.8) * mm});
            skArc(sketch, "E74.3.63.0", {"start": v(13.88, -74.95) * mm, "mid": v(13.88, -74.92) * mm, "end": v(13.88, -74.9) * mm});
            skArc(sketch, "E74.4.63.0", {"start": v(11.92, -75.23) * mm, "mid": v(11.92, -75.26) * mm, "end": v(11.93, -75.29) * mm});
            skArc(sketch, "E74.3.64.0", {"start": v(17.78, -74.12) * mm, "mid": v(17.79, -74.1) * mm, "end": v(17.78, -74.07) * mm});
            skArc(sketch, "E74.4.64.0", {"start": v(15.84, -74.5) * mm, "mid": v(15.85, -74.53) * mm, "end": v(15.86, -74.56) * mm});
            skArc(sketch, "E74.3.65.0", {"start": v(21.64, -73.1) * mm, "mid": v(21.64, -73.06) * mm, "end": v(21.63, -73.03) * mm});
            skArc(sketch, "E74.4.65.0", {"start": v(19.71, -73.58) * mm, "mid": v(19.72, -73.6) * mm, "end": v(19.74, -73.63) * mm});
            skArc(sketch, "E74.3.66.0", {"start": v(25.44, -71.86) * mm, "mid": v(25.43, -71.83) * mm, "end": v(25.43, -71.8) * mm});
            skArc(sketch, "E74.4.66.0", {"start": v(23.54, -72.44) * mm, "mid": v(23.55, -72.47) * mm, "end": v(23.57, -72.5) * mm});
            skArc(sketch, "E74.3.67.0", {"start": v(29.16, -70.43) * mm, "mid": v(29.16, -70.4) * mm, "end": v(29.15, -70.37) * mm});
            skArc(sketch, "E74.4.67.0", {"start": v(27.3, -71.11) * mm, "mid": v(27.3, -71.14) * mm, "end": v(27.33, -71.16) * mm});
            skArc(sketch, "E74.3.68.0", {"start": v(32.8, -68.8) * mm, "mid": v(32.8, -68.78) * mm, "end": v(32.8, -68.75) * mm});
            skArc(sketch, "E74.4.68.0", {"start": v(30.98, -69.59) * mm, "mid": v(31, -69.61) * mm, "end": v(31.01, -69.63) * mm});
            skArc(sketch, "E74.3.69.0", {"start": v(36.36, -67) * mm, "mid": v(36.36, -66.97) * mm, "end": v(36.35, -66.94) * mm});
            skArc(sketch, "E74.4.69.0", {"start": v(34.58, -67.87) * mm, "mid": v(34.6, -67.9) * mm, "end": v(34.62, -67.91) * mm});
            skArc(sketch, "E74.3.70.0", {"start": v(39.82, -65) * mm, "mid": v(39.81, -64.97) * mm, "end": v(39.8, -64.95) * mm});
            skArc(sketch, "E74.4.70.0", {"start": v(38.09, -65.97) * mm, "mid": v(38.1, -65.99) * mm, "end": v(38.12, -66) * mm});
            skArc(sketch, "E74.3.71.0", {"start": v(43.17, -62.83) * mm, "mid": v(43.16, -62.8) * mm, "end": v(43.14, -62.78) * mm});
            skArc(sketch, "E74.4.71.0", {"start": v(41.49, -63.88) * mm, "mid": v(41.5, -63.9) * mm, "end": v(41.52, -63.92) * mm});
            skArc(sketch, "E74.3.72.0", {"start": v(46.4, -60.48) * mm, "mid": v(46.39, -60.45) * mm, "end": v(46.37, -60.43) * mm});
            skArc(sketch, "E74.4.72.0", {"start": v(44.77, -61.62) * mm, "mid": v(44.8, -61.65) * mm, "end": v(44.81, -61.66) * mm});
            skArc(sketch, "E74.3.73.0", {"start": v(49.5, -57.97) * mm, "mid": v(49.49, -57.94) * mm, "end": v(49.47, -57.92) * mm});
            skArc(sketch, "E74.4.73.0", {"start": v(47.94, -59.2) * mm, "mid": v(47.96, -59.22) * mm, "end": v(47.98, -59.23) * mm});
            skArc(sketch, "E74.3.74.0", {"start": v(52.46, -55.3) * mm, "mid": v(52.45, -55.27) * mm, "end": v(52.43, -55.25) * mm});
            skArc(sketch, "E74.4.74.0", {"start": v(50.97, -56.6) * mm, "mid": v(50.99, -56.63) * mm, "end": v(51.01, -56.64) * mm});
            skArc(sketch, "E74.3.75.0", {"start": v(55.29, -52.48) * mm, "mid": v(55.27, -52.45) * mm, "end": v(55.25, -52.43) * mm});
            skArc(sketch, "E74.4.75.0", {"start": v(53.86, -53.86) * mm, "mid": v(53.88, -53.88) * mm, "end": v(53.9, -53.9) * mm});
            skArc(sketch, "E74.3.76.0", {"start": v(57.96, -49.51) * mm, "mid": v(57.94, -49.49) * mm, "end": v(57.92, -49.47) * mm});
            skArc(sketch, "E74.4.76.0", {"start": v(56.6, -50.97) * mm, "mid": v(56.63, -50.99) * mm, "end": v(56.65, -51) * mm});
            skArc(sketch, "E74.3.77.0", {"start": v(60.47, -46.41) * mm, "mid": v(60.45, -46.39) * mm, "end": v(60.43, -46.37) * mm});
            skArc(sketch, "E74.4.77.0", {"start": v(59.2, -47.94) * mm, "mid": v(59.22, -47.95) * mm, "end": v(59.25, -47.96) * mm});
            skArc(sketch, "E74.3.78.0", {"start": v(62.81, -43.18) * mm, "mid": v(62.8, -43.16) * mm, "end": v(62.78, -43.14) * mm});
            skArc(sketch, "E74.4.78.0", {"start": v(61.62, -44.77) * mm, "mid": v(61.65, -44.79) * mm, "end": v(61.67, -44.8) * mm});
            skArc(sketch, "E74.3.79.0", {"start": v(64.99, -39.84) * mm, "mid": v(64.97, -39.82) * mm, "end": v(64.95, -39.8) * mm});
            skArc(sketch, "E74.4.79.0", {"start": v(63.88, -41.49) * mm, "mid": v(63.9, -41.5) * mm, "end": v(63.93, -41.5) * mm});
            skArc(sketch, "E74.3.80.0", {"start": v(66.98, -36.38) * mm, "mid": v(66.96, -36.36) * mm, "end": v(66.94, -36.35) * mm});
            skArc(sketch, "E74.4.80.0", {"start": v(65.97, -38.09) * mm, "mid": v(66, -38.1) * mm, "end": v(66.02, -38.1) * mm});
            skArc(sketch, "E74.3.81.0", {"start": v(68.8, -32.83) * mm, "mid": v(68.78, -32.8) * mm, "end": v(68.75, -32.8) * mm});
            skArc(sketch, "E74.4.81.0", {"start": v(67.87, -34.58) * mm, "mid": v(67.9, -34.6) * mm, "end": v(67.92, -34.6) * mm});
            skArc(sketch, "E74.3.82.0", {"start": v(70.42, -29.18) * mm, "mid": v(70.4, -29.16) * mm, "end": v(70.37, -29.15) * mm});
            skArc(sketch, "E74.4.82.0", {"start": v(69.59, -30.98) * mm, "mid": v(69.61, -31) * mm, "end": v(69.64, -31) * mm});
            skArc(sketch, "E74.3.83.0", {"start": v(71.85, -25.45) * mm, "mid": v(71.83, -25.44) * mm, "end": v(71.8, -25.43) * mm});
            skArc(sketch, "E74.4.83.0", {"start": v(71.11, -27.3) * mm, "mid": v(71.14, -27.3) * mm, "end": v(71.17, -27.3) * mm});
            skArc(sketch, "E74.3.84.0", {"start": v(73.08, -21.66) * mm, "mid": v(73.06, -21.64) * mm, "end": v(73.03, -21.63) * mm});
            skArc(sketch, "E74.4.84.0", {"start": v(72.44, -23.54) * mm, "mid": v(72.47, -23.54) * mm, "end": v(72.5, -23.55) * mm});
            skArc(sketch, "E74.3.85.0", {"start": v(74.12, -17.8) * mm, "mid": v(74.1, -17.8) * mm, "end": v(74.07, -17.78) * mm});
            skArc(sketch, "E74.4.85.0", {"start": v(73.58, -19.71) * mm, "mid": v(73.6, -19.72) * mm, "end": v(73.63, -19.72) * mm});
            skArc(sketch, "E74.3.86.0", {"start": v(74.95, -13.9) * mm, "mid": v(74.92, -13.89) * mm, "end": v(74.9, -13.88) * mm});
            skArc(sketch, "E74.4.86.0", {"start": v(74.5, -15.84) * mm, "mid": v(74.53, -15.84) * mm, "end": v(74.56, -15.84) * mm});
            skArc(sketch, "E74.3.87.0", {"start": v(75.57, -9.96) * mm, "mid": v(75.55, -9.95) * mm, "end": v(75.52, -9.94) * mm});
            skArc(sketch, "E74.4.87.0", {"start": v(75.23, -11.92) * mm, "mid": v(75.26, -11.92) * mm, "end": v(75.29, -11.91) * mm});
            skArc(sketch, "E74.3.88.0", {"start": v(76, -6) * mm, "mid": v(75.96, -5.98) * mm, "end": v(75.94, -5.98) * mm});
            skArc(sketch, "E74.4.88.0", {"start": v(75.75, -7.96) * mm, "mid": v(75.78, -7.96) * mm, "end": v(75.81, -7.96) * mm});
            skArc(sketch, "E74.3.89.0", {"start": v(76.2, -2) * mm, "mid": v(76.17, -2) * mm, "end": v(76.15, -2) * mm});
            skArc(sketch, "E74.4.89.0", {"start": v(76.07, -3.99) * mm, "mid": v(76.1, -3.99) * mm, "end": v(76.12, -3.98) * mm});
            skArc(sketch, "E74.3.90.0", {"start": v(76.2, 1.99) * mm, "mid": v(76.17, 2) * mm, "end": v(76.15, 2) * mm});
            skArc(sketch, "E74.4.90.0", {"start": v(76.17, 0) * mm, "mid": v(76.2, 0) * mm, "end": v(76.23, 0.01) * mm});
            skArc(sketch, "E74.3.91.0", {"start": v(76, 5.97) * mm, "mid": v(75.96, 5.98) * mm, "end": v(75.94, 5.98) * mm});
            skArc(sketch, "E74.4.91.0", {"start": v(76.07, 3.99) * mm, "mid": v(76.1, 4) * mm, "end": v(76.12, 4) * mm});
            skArc(sketch, "E74.3.92.0", {"start": v(75.58, 9.94) * mm, "mid": v(75.55, 9.94) * mm, "end": v(75.52, 9.94) * mm});
            skArc(sketch, "E74.4.92.0", {"start": v(75.75, 7.96) * mm, "mid": v(75.78, 7.97) * mm, "end": v(75.8, 7.98) * mm});
            skArc(sketch, "E74.3.93.0", {"start": v(74.95, 13.88) * mm, "mid": v(74.92, 13.88) * mm, "end": v(74.9, 13.88) * mm});
            skArc(sketch, "E74.4.93.0", {"start": v(75.23, 11.92) * mm, "mid": v(75.26, 11.92) * mm, "end": v(75.29, 11.93) * mm});
            skArc(sketch, "E74.3.94.0", {"start": v(74.12, 17.78) * mm, "mid": v(74.1, 17.79) * mm, "end": v(74.07, 17.78) * mm});
            skArc(sketch, "E74.4.94.0", {"start": v(74.5, 15.84) * mm, "mid": v(74.53, 15.85) * mm, "end": v(74.56, 15.86) * mm});
            skArc(sketch, "E74.3.95.0", {"start": v(73.1, 21.64) * mm, "mid": v(73.06, 21.64) * mm, "end": v(73.03, 21.63) * mm});
            skArc(sketch, "E74.4.95.0", {"start": v(73.58, 19.71) * mm, "mid": v(73.6, 19.72) * mm, "end": v(73.63, 19.74) * mm});
            skArc(sketch, "E74.3.96.0", {"start": v(71.86, 25.44) * mm, "mid": v(71.83, 25.43) * mm, "end": v(71.8, 25.43) * mm});
            skArc(sketch, "E74.4.96.0", {"start": v(72.44, 23.54) * mm, "mid": v(72.47, 23.55) * mm, "end": v(72.5, 23.57) * mm});
            skArc(sketch, "E74.3.97.0", {"start": v(70.43, 29.16) * mm, "mid": v(70.4, 29.16) * mm, "end": v(70.37, 29.15) * mm});
            skArc(sketch, "E74.4.97.0", {"start": v(71.11, 27.3) * mm, "mid": v(71.14, 27.3) * mm, "end": v(71.16, 27.33) * mm});
            skArc(sketch, "E74.3.98.0", {"start": v(68.8, 32.8) * mm, "mid": v(68.78, 32.8) * mm, "end": v(68.75, 32.8) * mm});
            skArc(sketch, "E74.4.98.0", {"start": v(69.59, 30.98) * mm, "mid": v(69.61, 31) * mm, "end": v(69.63, 31.01) * mm});
            skArc(sketch, "E74.3.99.0", {"start": v(67, 36.36) * mm, "mid": v(66.97, 36.36) * mm, "end": v(66.94, 36.35) * mm});
            skArc(sketch, "E74.4.99.0", {"start": v(67.87, 34.58) * mm, "mid": v(67.9, 34.6) * mm, "end": v(67.91, 34.62) * mm});
            skArc(sketch, "E74.3.100.0", {"start": v(65, 39.82) * mm, "mid": v(64.97, 39.81) * mm, "end": v(64.95, 39.8) * mm});
            skArc(sketch, "E74.4.100.0", {"start": v(65.97, 38.09) * mm, "mid": v(65.99, 38.1) * mm, "end": v(66, 38.12) * mm});
            skArc(sketch, "E74.3.101.0", {"start": v(62.83, 43.17) * mm, "mid": v(62.8, 43.16) * mm, "end": v(62.78, 43.14) * mm});
            skArc(sketch, "E74.4.101.0", {"start": v(63.88, 41.49) * mm, "mid": v(63.9, 41.5) * mm, "end": v(63.92, 41.52) * mm});
            skArc(sketch, "E74.3.102.0", {"start": v(60.48, 46.4) * mm, "mid": v(60.45, 46.39) * mm, "end": v(60.43, 46.37) * mm});
            skArc(sketch, "E74.4.102.0", {"start": v(61.62, 44.77) * mm, "mid": v(61.65, 44.8) * mm, "end": v(61.66, 44.81) * mm});
            skArc(sketch, "E74.3.103.0", {"start": v(57.97, 49.5) * mm, "mid": v(57.94, 49.49) * mm, "end": v(57.92, 49.47) * mm});
            skArc(sketch, "E74.4.103.0", {"start": v(59.2, 47.94) * mm, "mid": v(59.22, 47.96) * mm, "end": v(59.23, 47.98) * mm});
            skArc(sketch, "E74.3.104.0", {"start": v(55.3, 52.46) * mm, "mid": v(55.27, 52.45) * mm, "end": v(55.25, 52.43) * mm});
            skArc(sketch, "E74.4.104.0", {"start": v(56.6, 50.97) * mm, "mid": v(56.63, 50.99) * mm, "end": v(56.64, 51.01) * mm});
            skArc(sketch, "E74.3.105.0", {"start": v(52.48, 55.29) * mm, "mid": v(52.45, 55.27) * mm, "end": v(52.43, 55.25) * mm});
            skArc(sketch, "E74.4.105.0", {"start": v(53.86, 53.86) * mm, "mid": v(53.88, 53.88) * mm, "end": v(53.9, 53.9) * mm});
            skArc(sketch, "E74.3.106.0", {"start": v(49.51, 57.96) * mm, "mid": v(49.49, 57.94) * mm, "end": v(49.47, 57.92) * mm});
            skArc(sketch, "E74.4.106.0", {"start": v(50.97, 56.6) * mm, "mid": v(50.99, 56.63) * mm, "end": v(51, 56.65) * mm});
            skArc(sketch, "E74.3.107.0", {"start": v(46.41, 60.47) * mm, "mid": v(46.39, 60.45) * mm, "end": v(46.37, 60.43) * mm});
            skArc(sketch, "E74.4.107.0", {"start": v(47.94, 59.2) * mm, "mid": v(47.95, 59.22) * mm, "end": v(47.96, 59.25) * mm});
            skArc(sketch, "E74.3.108.0", {"start": v(43.18, 62.81) * mm, "mid": v(43.16, 62.8) * mm, "end": v(43.14, 62.78) * mm});
            skArc(sketch, "E74.4.108.0", {"start": v(44.77, 61.62) * mm, "mid": v(44.79, 61.65) * mm, "end": v(44.8, 61.67) * mm});
            skArc(sketch, "E74.3.109.0", {"start": v(39.84, 64.99) * mm, "mid": v(39.82, 64.97) * mm, "end": v(39.8, 64.95) * mm});
            skArc(sketch, "E74.4.109.0", {"start": v(41.49, 63.88) * mm, "mid": v(41.5, 63.9) * mm, "end": v(41.5, 63.93) * mm});
            skArc(sketch, "E74.3.110.0", {"start": v(36.38, 66.98) * mm, "mid": v(36.36, 66.96) * mm, "end": v(36.35, 66.94) * mm});
            skArc(sketch, "E74.4.110.0", {"start": v(38.09, 65.97) * mm, "mid": v(38.1, 66) * mm, "end": v(38.1, 66.02) * mm});
            skArc(sketch, "E74.3.111.0", {"start": v(32.83, 68.8) * mm, "mid": v(32.8, 68.78) * mm, "end": v(32.8, 68.75) * mm});
            skArc(sketch, "E74.4.111.0", {"start": v(34.58, 67.87) * mm, "mid": v(34.6, 67.9) * mm, "end": v(34.6, 67.92) * mm});
            skArc(sketch, "E74.3.112.0", {"start": v(29.18, 70.42) * mm, "mid": v(29.16, 70.4) * mm, "end": v(29.15, 70.37) * mm});
            skArc(sketch, "E74.4.112.0", {"start": v(30.98, 69.59) * mm, "mid": v(31, 69.61) * mm, "end": v(31, 69.64) * mm});
            skArc(sketch, "E74.3.113.0", {"start": v(25.45, 71.85) * mm, "mid": v(25.44, 71.83) * mm, "end": v(25.43, 71.8) * mm});
            skArc(sketch, "E74.4.113.0", {"start": v(27.3, 71.11) * mm, "mid": v(27.3, 71.14) * mm, "end": v(27.3, 71.17) * mm});
            skArc(sketch, "E74.3.114.0", {"start": v(21.66, 73.08) * mm, "mid": v(21.64, 73.06) * mm, "end": v(21.63, 73.03) * mm});
            skArc(sketch, "E74.4.114.0", {"start": v(23.54, 72.44) * mm, "mid": v(23.54, 72.47) * mm, "end": v(23.55, 72.5) * mm});
            skArc(sketch, "E74.3.115.0", {"start": v(17.8, 74.12) * mm, "mid": v(17.8, 74.1) * mm, "end": v(17.78, 74.07) * mm});
            skArc(sketch, "E74.4.115.0", {"start": v(19.71, 73.58) * mm, "mid": v(19.72, 73.6) * mm, "end": v(19.72, 73.63) * mm});
            skArc(sketch, "E74.3.116.0", {"start": v(13.9, 74.95) * mm, "mid": v(13.89, 74.92) * mm, "end": v(13.88, 74.9) * mm});
            skArc(sketch, "E74.4.116.0", {"start": v(15.84, 74.5) * mm, "mid": v(15.84, 74.53) * mm, "end": v(15.84, 74.56) * mm});
            skArc(sketch, "E74.3.117.0", {"start": v(9.96, 75.57) * mm, "mid": v(9.95, 75.55) * mm, "end": v(9.94, 75.52) * mm});
            skArc(sketch, "E74.4.117.0", {"start": v(11.92, 75.23) * mm, "mid": v(11.92, 75.26) * mm, "end": v(11.91, 75.29) * mm});
            skArc(sketch, "E74.3.118.0", {"start": v(6, 76) * mm, "mid": v(5.98, 75.96) * mm, "end": v(5.98, 75.94) * mm});
            skArc(sketch, "E74.4.118.0", {"start": v(7.96, 75.75) * mm, "mid": v(7.96, 75.78) * mm, "end": v(7.96, 75.81) * mm});
            skArc(sketch, "E74.3.119.0", {"start": v(2, 76.2) * mm, "mid": v(2, 76.17) * mm, "end": v(2, 76.15) * mm});
            skArc(sketch, "E74.4.119.0", {"start": v(3.99, 76.07) * mm, "mid": v(3.99, 76.1) * mm, "end": v(3.98, 76.12) * mm});
            skArc(sketch, "E75.trimOffspring", {"start": v(-65.78, -35.89) * mm, "mid": v(-65.38, -36.61) * mm, "end": v(-64.97, -37.33) * mm});
            skArc(sketch, "E76.trimOffspring", {"start": v(-67.57, -32.4) * mm, "mid": v(-67.2, -33.14) * mm, "end": v(-66.83, -33.88) * mm});
            skArc(sketch, "E77.trimOffspring", {"start": v(-69.17, -28.81) * mm, "mid": v(-68.85, -29.58) * mm, "end": v(-68.51, -30.34) * mm});
            skArc(sketch, "E78.trimOffspring", {"start": v(-63.8, -39.28) * mm, "mid": v(-63.37, -39.98) * mm, "end": v(-62.92, -40.68) * mm});
            skArc(sketch, "E79.trimOffspring", {"start": v(-59.35, -45.74) * mm, "mid": v(-58.84, -46.39) * mm, "end": v(-58.33, -47.04) * mm});
            skArc(sketch, "E80.trimOffspring", {"start": v(-56.88, -48.78) * mm, "mid": v(-56.34, -49.4) * mm, "end": v(-55.79, -50.02) * mm});
            skArc(sketch, "E81.trimOffspring", {"start": v(-54.25, -51.69) * mm, "mid": v(-53.67, -52.29) * mm, "end": v(-53.1, -52.88) * mm});
            skArc(sketch, "E82.trimOffspring", {"start": v(-71.8, -21.43) * mm, "mid": v(-70.95, -24.09) * mm, "end": v(-70, -26.71) * mm});
            skArc(sketch, "E83.trimOffspring", {"start": v(-51.47, -54.46) * mm, "mid": v(-50.86, -55.02) * mm, "end": v(-50.25, -55.58) * mm});
            skArc(sketch, "E84.trimOffspring", {"start": v(-48.55, -57.08) * mm, "mid": v(-47.91, -57.6) * mm, "end": v(-47.27, -58.14) * mm});
            skArc(sketch, "E85.trimOffspring", {"start": v(-45.5, -59.54) * mm, "mid": v(-44.83, -60.04) * mm, "end": v(-44.17, -60.53) * mm});
            skArc(sketch, "E86.trimOffspring", {"start": v(-42.32, -61.84) * mm, "mid": v(-41.63, -62.3) * mm, "end": v(-40.94, -62.76) * mm});
            skArc(sketch, "E87.trimOffspring", {"start": v(-39.02, -63.97) * mm, "mid": v(-38.31, -64.4) * mm, "end": v(-37.6, -64.82) * mm});
            skArc(sketch, "E88.trimOffspring", {"start": v(-35.62, -65.92) * mm, "mid": v(-34.89, -66.31) * mm, "end": v(-34.15, -66.7) * mm});
            skArc(sketch, "E89.trimOffspring", {"start": v(-32.12, -67.7) * mm, "mid": v(-31.37, -68.05) * mm, "end": v(-30.62, -68.39) * mm});
            skArc(sketch, "E90.trimOffspring", {"start": v(-28.53, -69.28) * mm, "mid": v(-27.77, -69.6) * mm, "end": v(-27, -69.9) * mm});
            skArc(sketch, "E91.trimOffspring", {"start": v(-24.87, -70.68) * mm, "mid": v(-24.09, -70.95) * mm, "end": v(-23.3, -71.22) * mm});
            skArc(sketch, "E92.trimOffspring", {"start": v(-21.14, -71.89) * mm, "mid": v(-20.34, -72.12) * mm, "end": v(-19.54, -72.34) * mm});
            skArc(sketch, "E93.trimOffspring", {"start": v(-17.34, -72.9) * mm, "mid": v(-16.54, -73.08) * mm, "end": v(-15.73, -73.26) * mm});
            skArc(sketch, "E94.trimOffspring", {"start": v(-13.5, -73.7) * mm, "mid": v(-12.69, -73.85) * mm, "end": v(-11.87, -73.98) * mm});
            skArc(sketch, "E95.trimOffspring", {"start": v(-9.63, -74.3) * mm, "mid": v(-8.8, -74.41) * mm, "end": v(-7.98, -74.5) * mm});
            skArc(sketch, "E96.trimOffspring", {"start": v(-5.73, -74.71) * mm, "mid": v(-4.9, -74.77) * mm, "end": v(-4.07, -74.82) * mm});
            skArc(sketch, "E97.trimOffspring", {"start": v(-1.8, -74.9) * mm, "mid": v(-0.98, -74.92) * mm, "end": v(-0.15, -74.93) * mm});
            skArc(sketch, "E98.trimOffspring", {"start": v(2.11, -74.9) * mm, "mid": v(2.94, -74.87) * mm, "end": v(3.77, -74.84) * mm});
            skArc(sketch, "E99.trimOffspring", {"start": v(6.03, -74.69) * mm, "mid": v(6.86, -74.62) * mm, "end": v(7.68, -74.54) * mm});
            skArc(sketch, "E100.trimOffspring", {"start": v(9.93, -74.27) * mm, "mid": v(10.75, -74.15) * mm, "end": v(11.57, -74.03) * mm});
            skArc(sketch, "E101.trimOffspring", {"start": v(13.8, -73.65) * mm, "mid": v(14.62, -73.5) * mm, "end": v(15.43, -73.32) * mm});
            skArc(sketch, "E102.trimOffspring", {"start": v(17.64, -72.82) * mm, "mid": v(18.44, -72.62) * mm, "end": v(19.25, -72.42) * mm});
            skArc(sketch, "E103.trimOffspring", {"start": v(21.43, -71.8) * mm, "mid": v(22.22, -71.56) * mm, "end": v(23, -71.3) * mm});
            skArc(sketch, "E104.trimOffspring", {"start": v(25.16, -70.58) * mm, "mid": v(25.93, -70.3) * mm, "end": v(26.71, -70) * mm});
            skArc(sketch, "E105.trimOffspring", {"start": v(28.81, -69.17) * mm, "mid": v(29.58, -68.85) * mm, "end": v(30.34, -68.51) * mm});
            skArc(sketch, "E106.trimOffspring", {"start": v(32.4, -67.57) * mm, "mid": v(33.14, -67.2) * mm, "end": v(33.88, -66.83) * mm});
            skArc(sketch, "E107.trimOffspring", {"start": v(35.89, -65.78) * mm, "mid": v(36.61, -65.38) * mm, "end": v(37.33, -64.97) * mm});
            skArc(sketch, "E108.trimOffspring", {"start": v(39.28, -63.8) * mm, "mid": v(39.98, -63.37) * mm, "end": v(40.68, -62.92) * mm});
            skArc(sketch, "E109.trimOffspring", {"start": v(42.57, -61.67) * mm, "mid": v(43.25, -61.2) * mm, "end": v(43.92, -60.7) * mm});
            skArc(sketch, "E110.trimOffspring", {"start": v(45.74, -59.35) * mm, "mid": v(46.39, -58.84) * mm, "end": v(47.04, -58.33) * mm});
            skArc(sketch, "E111.trimOffspring", {"start": v(48.78, -56.88) * mm, "mid": v(49.4, -56.34) * mm, "end": v(50.02, -55.79) * mm});
            skArc(sketch, "E112.trimOffspring", {"start": v(51.69, -54.25) * mm, "mid": v(52.29, -53.67) * mm, "end": v(52.88, -53.1) * mm});
            skArc(sketch, "E113.trimOffspring", {"start": v(54.46, -51.47) * mm, "mid": v(55.02, -50.86) * mm, "end": v(55.58, -50.25) * mm});
            skArc(sketch, "E114.trimOffspring", {"start": v(57.08, -48.55) * mm, "mid": v(57.6, -47.91) * mm, "end": v(58.14, -47.27) * mm});
            skArc(sketch, "E115.trimOffspring", {"start": v(59.54, -45.5) * mm, "mid": v(60.04, -44.83) * mm, "end": v(60.53, -44.17) * mm});
            skArc(sketch, "E116.trimOffspring", {"start": v(61.84, -42.32) * mm, "mid": v(62.3, -41.63) * mm, "end": v(62.76, -40.94) * mm});
            skArc(sketch, "E117.trimOffspring", {"start": v(63.97, -39.02) * mm, "mid": v(64.4, -38.31) * mm, "end": v(64.82, -37.6) * mm});
            skArc(sketch, "E118.trimOffspring", {"start": v(65.92, -35.62) * mm, "mid": v(66.31, -34.89) * mm, "end": v(66.7, -34.15) * mm});
            skArc(sketch, "E119.trimOffspring", {"start": v(67.7, -32.12) * mm, "mid": v(68.05, -31.37) * mm, "end": v(68.39, -30.62) * mm});
            skArc(sketch, "E120.trimOffspring", {"start": v(69.28, -28.53) * mm, "mid": v(69.6, -27.77) * mm, "end": v(69.9, -27) * mm});
            skArc(sketch, "E121.trimOffspring", {"start": v(70.68, -24.87) * mm, "mid": v(70.95, -24.09) * mm, "end": v(71.22, -23.3) * mm});
            skArc(sketch, "E122.trimOffspring", {"start": v(71.89, -21.14) * mm, "mid": v(72.12, -20.34) * mm, "end": v(72.34, -19.54) * mm});
            skArc(sketch, "E123.trimOffspring", {"start": v(72.9, -17.34) * mm, "mid": v(73.08, -16.54) * mm, "end": v(73.26, -15.73) * mm});
            skArc(sketch, "E124.trimOffspring", {"start": v(73.7, -13.5) * mm, "mid": v(73.85, -12.69) * mm, "end": v(73.98, -11.87) * mm});
            skArc(sketch, "E125.trimOffspring", {"start": v(74.3, -9.63) * mm, "mid": v(74.41, -8.8) * mm, "end": v(74.5, -7.98) * mm});
            skArc(sketch, "E126.trimOffspring", {"start": v(74.71, -5.73) * mm, "mid": v(74.77, -4.9) * mm, "end": v(74.82, -4.07) * mm});
            skArc(sketch, "E127.trimOffspring", {"start": v(74.9, -1.8) * mm, "mid": v(74.92, -0.98) * mm, "end": v(74.93, -0.15) * mm});
            skArc(sketch, "E128.trimOffspring", {"start": v(74.9, 2.11) * mm, "mid": v(74.87, 2.94) * mm, "end": v(74.84, 3.77) * mm});
            skArc(sketch, "E129.trimOffspring", {"start": v(74.69, 6.03) * mm, "mid": v(74.62, 6.86) * mm, "end": v(74.54, 7.68) * mm});
            skArc(sketch, "E130.trimOffspring", {"start": v(74.27, 9.93) * mm, "mid": v(74.15, 10.75) * mm, "end": v(74.03, 11.57) * mm});
            skArc(sketch, "E131.trimOffspring", {"start": v(73.65, 13.8) * mm, "mid": v(73.5, 14.62) * mm, "end": v(73.32, 15.43) * mm});
            skArc(sketch, "E132.trimOffspring", {"start": v(72.82, 17.64) * mm, "mid": v(72.62, 18.44) * mm, "end": v(72.42, 19.25) * mm});
            skArc(sketch, "E133.trimOffspring", {"start": v(71.8, 21.43) * mm, "mid": v(71.56, 22.22) * mm, "end": v(71.3, 23) * mm});
            skArc(sketch, "E134.trimOffspring", {"start": v(70.58, 25.16) * mm, "mid": v(70.3, 25.93) * mm, "end": v(70, 26.71) * mm});
            skArc(sketch, "E135.trimOffspring", {"start": v(69.17, 28.81) * mm, "mid": v(68.85, 29.58) * mm, "end": v(68.51, 30.34) * mm});
            skArc(sketch, "E136.trimOffspring", {"start": v(67.57, 32.4) * mm, "mid": v(67.2, 33.14) * mm, "end": v(66.83, 33.88) * mm});
            skArc(sketch, "E137.trimOffspring", {"start": v(65.78, 35.89) * mm, "mid": v(65.38, 36.61) * mm, "end": v(64.97, 37.33) * mm});
            skArc(sketch, "E138.trimOffspring", {"start": v(63.8, 39.28) * mm, "mid": v(63.37, 39.98) * mm, "end": v(62.92, 40.68) * mm});
            skArc(sketch, "E139.trimOffspring", {"start": v(61.67, 42.57) * mm, "mid": v(61.2, 43.25) * mm, "end": v(60.7, 43.92) * mm});
            skArc(sketch, "E140.trimOffspring", {"start": v(59.35, 45.74) * mm, "mid": v(58.84, 46.39) * mm, "end": v(58.33, 47.04) * mm});
            skArc(sketch, "E141.trimOffspring", {"start": v(56.88, 48.78) * mm, "mid": v(56.34, 49.4) * mm, "end": v(55.79, 50.02) * mm});
            skArc(sketch, "E142.trimOffspring", {"start": v(54.25, 51.69) * mm, "mid": v(53.67, 52.29) * mm, "end": v(53.1, 52.88) * mm});
            skArc(sketch, "E143.trimOffspring", {"start": v(51.47, 54.46) * mm, "mid": v(50.86, 55.02) * mm, "end": v(50.25, 55.58) * mm});
            skArc(sketch, "E144.trimOffspring", {"start": v(48.55, 57.08) * mm, "mid": v(47.91, 57.6) * mm, "end": v(47.27, 58.14) * mm});
            skArc(sketch, "E145.trimOffspring", {"start": v(45.5, 59.54) * mm, "mid": v(44.83, 60.04) * mm, "end": v(44.17, 60.53) * mm});
            skArc(sketch, "E146.trimOffspring", {"start": v(42.32, 61.84) * mm, "mid": v(41.63, 62.3) * mm, "end": v(40.94, 62.76) * mm});
            skArc(sketch, "E147.trimOffspring", {"start": v(39.02, 63.97) * mm, "mid": v(38.31, 64.4) * mm, "end": v(37.6, 64.82) * mm});
            skArc(sketch, "E148.trimOffspring", {"start": v(35.62, 65.92) * mm, "mid": v(34.89, 66.31) * mm, "end": v(34.15, 66.7) * mm});
            skArc(sketch, "E149.trimOffspring", {"start": v(32.12, 67.7) * mm, "mid": v(31.37, 68.05) * mm, "end": v(30.62, 68.39) * mm});
            skArc(sketch, "E150.trimOffspring", {"start": v(28.53, 69.28) * mm, "mid": v(27.77, 69.6) * mm, "end": v(27, 69.9) * mm});
            skArc(sketch, "E151.trimOffspring", {"start": v(24.87, 70.68) * mm, "mid": v(24.09, 70.95) * mm, "end": v(23.3, 71.22) * mm});
            skArc(sketch, "E152.trimOffspring", {"start": v(21.14, 71.89) * mm, "mid": v(20.34, 72.12) * mm, "end": v(19.54, 72.34) * mm});
            skArc(sketch, "E153.trimOffspring", {"start": v(17.34, 72.9) * mm, "mid": v(16.54, 73.08) * mm, "end": v(15.73, 73.26) * mm});
            skArc(sketch, "E154.trimOffspring", {"start": v(13.5, 73.7) * mm, "mid": v(12.69, 73.85) * mm, "end": v(11.87, 73.98) * mm});
            skArc(sketch, "E155.trimOffspring", {"start": v(9.63, 74.3) * mm, "mid": v(8.8, 74.41) * mm, "end": v(7.98, 74.5) * mm});
            skArc(sketch, "E156.trimOffspring", {"start": v(1.8, 74.9) * mm, "mid": v(0.98, 74.92) * mm, "end": v(0.15, 74.93) * mm});
            skArc(sketch, "E157.trimOffspring", {"start": v(5.73, 74.71) * mm, "mid": v(4.9, 74.77) * mm, "end": v(4.07, 74.82) * mm});
            skSolve(sketch);
        }
        {
            var Q0;
            Q0 = qSketchRegion(id + "F0", true);
            extrude(context, id + "F1", {"entities" : qUnion([Q0]), "depth" : 6.35 * mm});
        }
        {
            var Q0;
            Q0=makeQuery(id+"F1.opExtrude","CAP_FACE",FACE,{"disambiguationData":[OSD([sQuery(id+"F0.wireOp",EDGE,"E0"),sQuery(id+"F0.wireOp",EDGE,"E1.trimOffspring"),sQuery(id+"F0.wireOp",EDGE,"E2"),sQuery(id+"F0.wireOp",EDGE,"E3"),sQuery(id+"F0.wireOp",EDGE,"E4.MirrorCS"),sQuery(id+"F0.wireOp",EDGE,"E5.MirrorCS"),sQuery(id+"F0.wireOp",EDGE,"E6.MirrorCS"),sQuery(id+"F0.wireOp",EDGE,"E8.filletArc"),sQuery(id+"F0.wireOp",EDGE,"E9.filletArc"),sQuery(id+"F0.wireOp",EDGE,"E10.filletArc"),sQuery(id+"F0.wireOp",EDGE,"E11.filletArc"),sQuery(id+"F0.wireOp",EDGE,"E12.filletArc"),sQuery(id+"F0.wireOp",EDGE,"E13.filletArc"),sQuery(id+"F0.wireOp",EDGE,"E14.1.0"),sQuery(id+"F0.wireOp",EDGE,"E14.1.1"),sQuery(id+"F0.wireOp",EDGE,"E14.1.2"),sQuery(id+"F0.wireOp",EDGE,"E14.1.3"),sQuery(id+"F0.wireOp",EDGE,"E14.1.4"),sQuery(id+"F0.wireOp",EDGE,"E14.1.5"),sQuery(id+"F0.wireOp",EDGE,"E14.1.6"),sQuery(id+"F0.wireOp",EDGE,"E14.1.7"),sQuery(id+"F0.wireOp",EDGE,"E14.1.8"),sQuery(id+"F0.wireOp",EDGE,"E14.1.9"),sQuery(id+"F0.wireOp",EDGE,"E14.2.0"),sQuery(id+"F0.wireOp",EDGE,"E14.2.1"),sQuery(id+"F0.wireOp",EDGE,"E14.2.2"),sQuery(id+"F0.wireOp",EDGE,"E14.2.3"),sQuery(id+"F0.wireOp",EDGE,"E14.2.4"),sQuery(id+"F0.wireOp",EDGE,"E14.2.5"),sQuery(id+"F0.wireOp",EDGE,"E14.2.6"),sQuery(id+"F0.wireOp",EDGE,"E14.2.7"),sQuery(id+"F0.wireOp",EDGE,"E14.2.8"),sQuery(id+"F0.wireOp",EDGE,"E14.2.9"),sQuery(id+"F0.wireOp",EDGE,"E14.3.0"),sQuery(id+"F0.wireOp",EDGE,"E14.3.1"),sQuery(id+"F0.wireOp",EDGE,"E14.3.2"),sQuery(id+"F0.wireOp",EDGE,"E14.3.3"),sQuery(id+"F0.wireOp",EDGE,"E14.3.4"),sQuery(id+"F0.wireOp",EDGE,"E14.3.5"),sQuery(id+"F0.wireOp",EDGE,"E14.3.6"),sQuery(id+"F0.wireOp",EDGE,"E14.3.7"),sQuery(id+"F0.wireOp",EDGE,"E14.3.8"),sQuery(id+"F0.wireOp",EDGE,"E14.3.9"),sQuery(id+"F0.wireOp",EDGE,"E14.4.0"),sQuery(id+"F0.wireOp",EDGE,"E14.4.1"),sQuery(id+"F0.wireOp",EDGE,"E14.4.2"),sQuery(id+"F0.wireOp",EDGE,"E14.4.3"),sQuery(id+"F0.wireOp",EDGE,"E14.4.4"),sQuery(id+"F0.wireOp",EDGE,"E14.4.5"),sQuery(id+"F0.wireOp",EDGE,"E14.4.6"),sQuery(id+"F0.wireOp",EDGE,"E14.4.7"),sQuery(id+"F0.wireOp",EDGE,"E14.4.8"),sQuery(id+"F0.wireOp",EDGE,"E14.4.9"),sQuery(id+"F0.wireOp",EDGE,"E14.5.0"),sQuery(id+"F0.wireOp",EDGE,"E14.5.1"),sQuery(id+"F0.wireOp",EDGE,"E14.5.2"),sQuery(id+"F0.wireOp",EDGE,"E14.5.3"),sQuery(id+"F0.wireOp",EDGE,"E14.5.4"),sQuery(id+"F0.wireOp",EDGE,"E14.5.5"),sQuery(id+"F0.wireOp",EDGE,"E14.5.6"),sQuery(id+"F0.wireOp",EDGE,"E14.5.7"),sQuery(id+"F0.wireOp",EDGE,"E14.5.8"),sQuery(id+"F0.wireOp",EDGE,"E14.5.9"),sQuery(id+"F0.wireOp",EDGE,"E14.6.0"),sQuery(id+"F0.wireOp",EDGE,"E14.6.1"),sQuery(id+"F0.wireOp",EDGE,"E14.6.2"),sQuery(id+"F0.wireOp",EDGE,"E14.6.3"),sQuery(id+"F0.wireOp",EDGE,"E14.6.4"),sQuery(id+"F0.wireOp",EDGE,"E14.6.5"),sQuery(id+"F0.wireOp",EDGE,"E14.6.6"),sQuery(id+"F0.wireOp",EDGE,"E14.6.7"),sQuery(id+"F0.wireOp",EDGE,"E14.6.8"),sQuery(id+"F0.wireOp",EDGE,"E14.6.9"),sQuery(id+"F0.wireOp",EDGE,"E14.7.0"),sQuery(id+"F0.wireOp",EDGE,"E14.7.1"),sQuery(id+"F0.wireOp",EDGE,"E14.7.2"),sQuery(id+"F0.wireOp",EDGE,"E14.7.3"),sQuery(id+"F0.wireOp",EDGE,"E14.7.4"),sQuery(id+"F0.wireOp",EDGE,"E14.7.5"),sQuery(id+"F0.wireOp",EDGE,"E14.7.6"),sQuery(id+"F0.wireOp",EDGE,"E14.7.7"),sQuery(id+"F0.wireOp",EDGE,"E14.7.8"),sQuery(id+"F0.wireOp",EDGE,"E14.7.9"),sQuery(id+"F0.wireOp",EDGE,"E14.8.0"),sQuery(id+"F0.wireOp",EDGE,"E14.8.1"),sQuery(id+"F0.wireOp",EDGE,"E14.8.2"),sQuery(id+"F0.wireOp",EDGE,"E14.8.3"),sQuery(id+"F0.wireOp",EDGE,"E14.8.4"),sQuery(id+"F0.wireOp",EDGE,"E14.8.5"),sQuery(id+"F0.wireOp",EDGE,"E14.8.6"),sQuery(id+"F0.wireOp",EDGE,"E14.8.7"),sQuery(id+"F0.wireOp",EDGE,"E14.8.8"),sQuery(id+"F0.wireOp",EDGE,"E14.8.9"),sQuery(id+"F0.wireOp",EDGE,"E14.9.0"),sQuery(id+"F0.wireOp",EDGE,"E14.9.1"),sQuery(id+"F0.wireOp",EDGE,"E14.9.2"),sQuery(id+"F0.wireOp",EDGE,"E14.9.3"),sQuery(id+"F0.wireOp",EDGE,"E14.9.4"),sQuery(id+"F0.wireOp",EDGE,"E14.9.5"),sQuery(id+"F0.wireOp",EDGE,"E14.9.6"),sQuery(id+"F0.wireOp",EDGE,"E14.9.7"),sQuery(id+"F0.wireOp",EDGE,"E14.9.8"),sQuery(id+"F0.wireOp",EDGE,"E14.9.9"),sQuery(id+"F0.wireOp",EDGE,"E14.10.0"),sQuery(id+"F0.wireOp",EDGE,"E14.10.1"),sQuery(id+"F0.wireOp",EDGE,"E14.10.2"),sQuery(id+"F0.wireOp",EDGE,"E14.10.3"),sQuery(id+"F0.wireOp",EDGE,"E14.10.4"),sQuery(id+"F0.wireOp",EDGE,"E14.10.5"),sQuery(id+"F0.wireOp",EDGE,"E14.10.6"),sQuery(id+"F0.wireOp",EDGE,"E14.10.7"),sQuery(id+"F0.wireOp",EDGE,"E14.10.8"),sQuery(id+"F0.wireOp",EDGE,"E14.10.9"),sQuery(id+"F0.wireOp",EDGE,"E14.11.0"),sQuery(id+"F0.wireOp",EDGE,"E14.11.1"),sQuery(id+"F0.wireOp",EDGE,"E14.11.2"),sQuery(id+"F0.wireOp",EDGE,"E14.11.3"),sQuery(id+"F0.wireOp",EDGE,"E14.11.4"),sQuery(id+"F0.wireOp",EDGE,"E14.11.5"),sQuery(id+"F0.wireOp",EDGE,"E14.11.6"),sQuery(id+"F0.wireOp",EDGE,"E14.11.7"),sQuery(id+"F0.wireOp",EDGE,"E14.11.8"),sQuery(id+"F0.wireOp",EDGE,"E14.11.9"),sQuery(id+"F0.wireOp",EDGE,"E14.12.0"),sQuery(id+"F0.wireOp",EDGE,"E14.12.1"),sQuery(id+"F0.wireOp",EDGE,"E14.12.2"),sQuery(id+"F0.wireOp",EDGE,"E14.12.3"),sQuery(id+"F0.wireOp",EDGE,"E14.12.4"),sQuery(id+"F0.wireOp",EDGE,"E14.12.5"),sQuery(id+"F0.wireOp",EDGE,"E14.12.6"),sQuery(id+"F0.wireOp",EDGE,"E14.12.7"),sQuery(id+"F0.wireOp",EDGE,"E14.12.8"),sQuery(id+"F0.wireOp",EDGE,"E14.12.9"),sQuery(id+"F0.wireOp",EDGE,"E14.13.0"),sQuery(id+"F0.wireOp",EDGE,"E14.13.1"),sQuery(id+"F0.wireOp",EDGE,"E14.13.2"),sQuery(id+"F0.wireOp",EDGE,"E14.13.3"),sQuery(id+"F0.wireOp",EDGE,"E14.13.4"),sQuery(id+"F0.wireOp",EDGE,"E14.13.5"),sQuery(id+"F0.wireOp",EDGE,"E14.13.6"),sQuery(id+"F0.wireOp",EDGE,"E14.13.7"),sQuery(id+"F0.wireOp",EDGE,"E14.13.8"),sQuery(id+"F0.wireOp",EDGE,"E14.13.9"),sQuery(id+"F0.wireOp",EDGE,"E14.14.0"),sQuery(id+"F0.wireOp",EDGE,"E14.14.1"),sQuery(id+"F0.wireOp",EDGE,"E14.14.2"),sQuery(id+"F0.wireOp",EDGE,"E14.14.3"),sQuery(id+"F0.wireOp",EDGE,"E14.14.4"),sQuery(id+"F0.wireOp",EDGE,"E14.14.5"),sQuery(id+"F0.wireOp",EDGE,"E14.14.6"),sQuery(id+"F0.wireOp",EDGE,"E14.14.7"),sQuery(id+"F0.wireOp",EDGE,"E14.14.8"),sQuery(id+"F0.wireOp",EDGE,"E14.14.9"),sQuery(id+"F0.wireOp",EDGE,"E14.15.0"),sQuery(id+"F0.wireOp",EDGE,"E14.15.1"),sQuery(id+"F0.wireOp",EDGE,"E14.15.2"),sQuery(id+"F0.wireOp",EDGE,"E14.15.3"),sQuery(id+"F0.wireOp",EDGE,"E14.15.4"),sQuery(id+"F0.wireOp",EDGE,"E14.15.5"),sQuery(id+"F0.wireOp",EDGE,"E14.15.6"),sQuery(id+"F0.wireOp",EDGE,"E14.15.7"),sQuery(id+"F0.wireOp",EDGE,"E14.15.8"),sQuery(id+"F0.wireOp",EDGE,"E14.15.9"),sQuery(id+"F0.wireOp",EDGE,"E14.16.0"),sQuery(id+"F0.wireOp",EDGE,"E14.16.1"),sQuery(id+"F0.wireOp",EDGE,"E14.16.2"),sQuery(id+"F0.wireOp",EDGE,"E14.16.3"),sQuery(id+"F0.wireOp",EDGE,"E14.16.4"),sQuery(id+"F0.wireOp",EDGE,"E14.16.5"),sQuery(id+"F0.wireOp",EDGE,"E14.16.6"),sQuery(id+"F0.wireOp",EDGE,"E14.16.7"),sQuery(id+"F0.wireOp",EDGE,"E14.16.8"),sQuery(id+"F0.wireOp",EDGE,"E14.16.9"),sQuery(id+"F0.wireOp",EDGE,"E14.17.0"),sQuery(id+"F0.wireOp",EDGE,"E14.17.1"),sQuery(id+"F0.wireOp",EDGE,"E14.17.2"),sQuery(id+"F0.wireOp",EDGE,"E14.17.3"),sQuery(id+"F0.wireOp",EDGE,"E14.17.4"),sQuery(id+"F0.wireOp",EDGE,"E14.17.5"),sQuery(id+"F0.wireOp",EDGE,"E14.17.6"),sQuery(id+"F0.wireOp",EDGE,"E14.17.7"),sQuery(id+"F0.wireOp",EDGE,"E14.17.8"),sQuery(id+"F0.wireOp",EDGE,"E14.17.9"),sQuery(id+"F0.wireOp",EDGE,"E14.18.0"),sQuery(id+"F0.wireOp",EDGE,"E14.18.1"),sQuery(id+"F0.wireOp",EDGE,"E14.18.2"),sQuery(id+"F0.wireOp",EDGE,"E14.18.3"),sQuery(id+"F0.wireOp",EDGE,"E14.18.4"),sQuery(id+"F0.wireOp",EDGE,"E14.18.5"),sQuery(id+"F0.wireOp",EDGE,"E14.18.6"),sQuery(id+"F0.wireOp",EDGE,"E14.18.7"),sQuery(id+"F0.wireOp",EDGE,"E14.18.8"),sQuery(id+"F0.wireOp",EDGE,"E14.18.9"),sQuery(id+"F0.wireOp",EDGE,"E14.19.0"),sQuery(id+"F0.wireOp",EDGE,"E14.19.1"),sQuery(id+"F0.wireOp",EDGE,"E14.19.2"),sQuery(id+"F0.wireOp",EDGE,"E14.19.3"),sQuery(id+"F0.wireOp",EDGE,"E14.19.4"),sQuery(id+"F0.wireOp",EDGE,"E14.19.5"),sQuery(id+"F0.wireOp",EDGE,"E14.19.6"),sQuery(id+"F0.wireOp",EDGE,"E14.19.7"),sQuery(id+"F0.wireOp",EDGE,"E14.19.8"),sQuery(id+"F0.wireOp",EDGE,"E14.19.9"),sQuery(id+"F0.wireOp",EDGE,"E14.20.0"),sQuery(id+"F0.wireOp",EDGE,"E14.20.1"),sQuery(id+"F0.wireOp",EDGE,"E14.20.2"),sQuery(id+"F0.wireOp",EDGE,"E14.20.3"),sQuery(id+"F0.wireOp",EDGE,"E14.20.4"),sQuery(id+"F0.wireOp",EDGE,"E14.20.5"),sQuery(id+"F0.wireOp",EDGE,"E14.20.6"),sQuery(id+"F0.wireOp",EDGE,"E14.20.7"),sQuery(id+"F0.wireOp",EDGE,"E14.20.8"),sQuery(id+"F0.wireOp",EDGE,"E14.20.9"),sQuery(id+"F0.wireOp",EDGE,"E14.21.0"),sQuery(id+"F0.wireOp",EDGE,"E14.21.1"),sQuery(id+"F0.wireOp",EDGE,"E14.21.2"),sQuery(id+"F0.wireOp",EDGE,"E14.21.3"),sQuery(id+"F0.wireOp",EDGE,"E14.21.4"),sQuery(id+"F0.wireOp",EDGE,"E14.21.5"),sQuery(id+"F0.wireOp",EDGE,"E14.21.6"),sQuery(id+"F0.wireOp",EDGE,"E14.21.7"),sQuery(id+"F0.wireOp",EDGE,"E14.21.8"),sQuery(id+"F0.wireOp",EDGE,"E14.21.9"),sQuery(id+"F0.wireOp",EDGE,"E14.22.0"),sQuery(id+"F0.wireOp",EDGE,"E14.22.1"),sQuery(id+"F0.wireOp",EDGE,"E14.22.2"),sQuery(id+"F0.wireOp",EDGE,"E14.22.3"),sQuery(id+"F0.wireOp",EDGE,"E14.22.4"),sQuery(id+"F0.wireOp",EDGE,"E14.22.5"),sQuery(id+"F0.wireOp",EDGE,"E14.22.6"),sQuery(id+"F0.wireOp",EDGE,"E14.22.7"),sQuery(id+"F0.wireOp",EDGE,"E14.22.8"),sQuery(id+"F0.wireOp",EDGE,"E14.22.9"),sQuery(id+"F0.wireOp",EDGE,"E14.23.0"),sQuery(id+"F0.wireOp",EDGE,"E14.23.1"),sQuery(id+"F0.wireOp",EDGE,"E14.23.2"),sQuery(id+"F0.wireOp",EDGE,"E14.23.3"),sQuery(id+"F0.wireOp",EDGE,"E14.23.4"),sQuery(id+"F0.wireOp",EDGE,"E14.23.5"),sQuery(id+"F0.wireOp",EDGE,"E14.23.6"),sQuery(id+"F0.wireOp",EDGE,"E14.23.7"),sQuery(id+"F0.wireOp",EDGE,"E14.23.8"),sQuery(id+"F0.wireOp",EDGE,"E14.23.9"),sQuery(id+"F0.wireOp",EDGE,"E14.24.0"),sQuery(id+"F0.wireOp",EDGE,"E14.24.1"),sQuery(id+"F0.wireOp",EDGE,"E14.24.2"),sQuery(id+"F0.wireOp",EDGE,"E14.24.3"),sQuery(id+"F0.wireOp",EDGE,"E14.24.4"),sQuery(id+"F0.wireOp",EDGE,"E14.24.5"),sQuery(id+"F0.wireOp",EDGE,"E14.24.6"),sQuery(id+"F0.wireOp",EDGE,"E14.24.7"),sQuery(id+"F0.wireOp",EDGE,"E14.24.8"),sQuery(id+"F0.wireOp",EDGE,"E14.24.9"),sQuery(id+"F0.wireOp",EDGE,"E14.25.0"),sQuery(id+"F0.wireOp",EDGE,"E14.25.1"),sQuery(id+"F0.wireOp",EDGE,"E14.25.2"),sQuery(id+"F0.wireOp",EDGE,"E14.25.3"),sQuery(id+"F0.wireOp",EDGE,"E14.25.4"),sQuery(id+"F0.wireOp",EDGE,"E14.25.5"),sQuery(id+"F0.wireOp",EDGE,"E14.25.6"),sQuery(id+"F0.wireOp",EDGE,"E14.25.7"),sQuery(id+"F0.wireOp",EDGE,"E14.25.8"),sQuery(id+"F0.wireOp",EDGE,"E14.25.9"),sQuery(id+"F0.wireOp",EDGE,"E14.26.0"),sQuery(id+"F0.wireOp",EDGE,"E14.26.1"),sQuery(id+"F0.wireOp",EDGE,"E14.26.2"),sQuery(id+"F0.wireOp",EDGE,"E14.26.3"),sQuery(id+"F0.wireOp",EDGE,"E14.26.4"),sQuery(id+"F0.wireOp",EDGE,"E14.26.5"),sQuery(id+"F0.wireOp",EDGE,"E14.26.6"),sQuery(id+"F0.wireOp",EDGE,"E14.26.7"),sQuery(id+"F0.wireOp",EDGE,"E14.26.8"),sQuery(id+"F0.wireOp",EDGE,"E14.26.9"),sQuery(id+"F0.wireOp",EDGE,"E14.27.0"),sQuery(id+"F0.wireOp",EDGE,"E14.27.1"),sQuery(id+"F0.wireOp",EDGE,"E14.27.2"),sQuery(id+"F0.wireOp",EDGE,"E14.27.3"),sQuery(id+"F0.wireOp",EDGE,"E14.27.4"),sQuery(id+"F0.wireOp",EDGE,"E14.27.5"),sQuery(id+"F0.wireOp",EDGE,"E14.27.6"),sQuery(id+"F0.wireOp",EDGE,"E14.27.7"),sQuery(id+"F0.wireOp",EDGE,"E14.27.8"),sQuery(id+"F0.wireOp",EDGE,"E14.27.9"),sQuery(id+"F0.wireOp",EDGE,"E14.28.0"),sQuery(id+"F0.wireOp",EDGE,"E14.28.1"),sQuery(id+"F0.wireOp",EDGE,"E14.28.2"),sQuery(id+"F0.wireOp",EDGE,"E14.28.3"),sQuery(id+"F0.wireOp",EDGE,"E14.28.4"),sQuery(id+"F0.wireOp",EDGE,"E14.28.5"),sQuery(id+"F0.wireOp",EDGE,"E14.28.6"),sQuery(id+"F0.wireOp",EDGE,"E14.28.7"),sQuery(id+"F0.wireOp",EDGE,"E14.28.8"),sQuery(id+"F0.wireOp",EDGE,"E14.28.9"),sQuery(id+"F0.wireOp",EDGE,"E14.29.0"),sQuery(id+"F0.wireOp",EDGE,"E14.29.1"),sQuery(id+"F0.wireOp",EDGE,"E14.29.2"),sQuery(id+"F0.wireOp",EDGE,"E14.29.3"),sQuery(id+"F0.wireOp",EDGE,"E14.29.4"),sQuery(id+"F0.wireOp",EDGE,"E14.29.5"),sQuery(id+"F0.wireOp",EDGE,"E14.29.6"),sQuery(id+"F0.wireOp",EDGE,"E14.29.7"),sQuery(id+"F0.wireOp",EDGE,"E14.29.8"),sQuery(id+"F0.wireOp",EDGE,"E14.29.9"),sQuery(id+"F0.wireOp",EDGE,"E14.30.0"),sQuery(id+"F0.wireOp",EDGE,"E14.30.1"),sQuery(id+"F0.wireOp",EDGE,"E14.30.2"),sQuery(id+"F0.wireOp",EDGE,"E14.30.3"),sQuery(id+"F0.wireOp",EDGE,"E14.30.4"),sQuery(id+"F0.wireOp",EDGE,"E14.30.5"),sQuery(id+"F0.wireOp",EDGE,"E14.30.6"),sQuery(id+"F0.wireOp",EDGE,"E14.30.7"),sQuery(id+"F0.wireOp",EDGE,"E14.30.8"),sQuery(id+"F0.wireOp",EDGE,"E14.30.9"),sQuery(id+"F0.wireOp",EDGE,"E14.31.0"),sQuery(id+"F0.wireOp",EDGE,"E14.31.1"),sQuery(id+"F0.wireOp",EDGE,"E14.31.2"),sQuery(id+"F0.wireOp",EDGE,"E14.31.3"),sQuery(id+"F0.wireOp",EDGE,"E14.31.4"),sQuery(id+"F0.wireOp",EDGE,"E14.31.5"),sQuery(id+"F0.wireOp",EDGE,"E14.31.6"),sQuery(id+"F0.wireOp",EDGE,"E14.31.7"),sQuery(id+"F0.wireOp",EDGE,"E14.31.8"),sQuery(id+"F0.wireOp",EDGE,"E14.31.9"),sQuery(id+"F0.wireOp",EDGE,"E14.32.0"),sQuery(id+"F0.wireOp",EDGE,"E14.32.1"),sQuery(id+"F0.wireOp",EDGE,"E14.32.2"),sQuery(id+"F0.wireOp",EDGE,"E14.32.3"),sQuery(id+"F0.wireOp",EDGE,"E14.32.4"),sQuery(id+"F0.wireOp",EDGE,"E14.32.5"),sQuery(id+"F0.wireOp",EDGE,"E14.32.6"),sQuery(id+"F0.wireOp",EDGE,"E14.32.7"),sQuery(id+"F0.wireOp",EDGE,"E14.32.8"),sQuery(id+"F0.wireOp",EDGE,"E14.32.9"),sQuery(id+"F0.wireOp",EDGE,"E14.33.0"),sQuery(id+"F0.wireOp",EDGE,"E14.33.1"),sQuery(id+"F0.wireOp",EDGE,"E14.33.2"),sQuery(id+"F0.wireOp",EDGE,"E14.33.3"),sQuery(id+"F0.wireOp",EDGE,"E14.33.4"),sQuery(id+"F0.wireOp",EDGE,"E14.33.5"),sQuery(id+"F0.wireOp",EDGE,"E14.33.6"),sQuery(id+"F0.wireOp",EDGE,"E14.33.7"),sQuery(id+"F0.wireOp",EDGE,"E14.33.8"),sQuery(id+"F0.wireOp",EDGE,"E14.33.9"),sQuery(id+"F0.wireOp",EDGE,"E14.34.0"),sQuery(id+"F0.wireOp",EDGE,"E14.34.1"),sQuery(id+"F0.wireOp",EDGE,"E14.34.2"),sQuery(id+"F0.wireOp",EDGE,"E14.34.3"),sQuery(id+"F0.wireOp",EDGE,"E14.34.4"),sQuery(id+"F0.wireOp",EDGE,"E14.34.5"),sQuery(id+"F0.wireOp",EDGE,"E14.34.6"),sQuery(id+"F0.wireOp",EDGE,"E14.34.7"),sQuery(id+"F0.wireOp",EDGE,"E14.34.8"),sQuery(id+"F0.wireOp",EDGE,"E14.34.9"),sQuery(id+"F0.wireOp",EDGE,"E14.35.0"),sQuery(id+"F0.wireOp",EDGE,"E14.35.1"),sQuery(id+"F0.wireOp",EDGE,"E14.35.2"),sQuery(id+"F0.wireOp",EDGE,"E14.35.3"),sQuery(id+"F0.wireOp",EDGE,"E14.35.4"),sQuery(id+"F0.wireOp",EDGE,"E14.35.5"),sQuery(id+"F0.wireOp",EDGE,"E14.35.6"),sQuery(id+"F0.wireOp",EDGE,"E14.35.7"),sQuery(id+"F0.wireOp",EDGE,"E14.35.8"),sQuery(id+"F0.wireOp",EDGE,"E14.35.9"),sQuery(id+"F0.wireOp",EDGE,"E14.36.0"),sQuery(id+"F0.wireOp",EDGE,"E14.36.1"),sQuery(id+"F0.wireOp",EDGE,"E14.36.2"),sQuery(id+"F0.wireOp",EDGE,"E14.36.3"),sQuery(id+"F0.wireOp",EDGE,"E14.36.4"),sQuery(id+"F0.wireOp",EDGE,"E14.36.5"),sQuery(id+"F0.wireOp",EDGE,"E14.36.6"),sQuery(id+"F0.wireOp",EDGE,"E14.36.7"),sQuery(id+"F0.wireOp",EDGE,"E14.36.8"),sQuery(id+"F0.wireOp",EDGE,"E14.36.9"),sQuery(id+"F0.wireOp",EDGE,"E14.37.0"),sQuery(id+"F0.wireOp",EDGE,"E14.37.1"),sQuery(id+"F0.wireOp",EDGE,"E14.37.2"),sQuery(id+"F0.wireOp",EDGE,"E14.37.3"),sQuery(id+"F0.wireOp",EDGE,"E14.37.4"),sQuery(id+"F0.wireOp",EDGE,"E14.37.5"),sQuery(id+"F0.wireOp",EDGE,"E14.37.6"),sQuery(id+"F0.wireOp",EDGE,"E14.37.7"),sQuery(id+"F0.wireOp",EDGE,"E14.37.8"),sQuery(id+"F0.wireOp",EDGE,"E14.37.9"),sQuery(id+"F0.wireOp",EDGE,"E14.38.0"),sQuery(id+"F0.wireOp",EDGE,"E14.38.1"),sQuery(id+"F0.wireOp",EDGE,"E14.38.2"),sQuery(id+"F0.wireOp",EDGE,"E14.38.3"),sQuery(id+"F0.wireOp",EDGE,"E14.38.4"),sQuery(id+"F0.wireOp",EDGE,"E14.38.5"),sQuery(id+"F0.wireOp",EDGE,"E14.38.6"),sQuery(id+"F0.wireOp",EDGE,"E14.38.7"),sQuery(id+"F0.wireOp",EDGE,"E14.38.8"),sQuery(id+"F0.wireOp",EDGE,"E14.38.9"),sQuery(id+"F0.wireOp",EDGE,"E14.39.0"),sQuery(id+"F0.wireOp",EDGE,"E14.39.1"),sQuery(id+"F0.wireOp",EDGE,"E14.39.2"),sQuery(id+"F0.wireOp",EDGE,"E14.39.3"),sQuery(id+"F0.wireOp",EDGE,"E14.39.4"),sQuery(id+"F0.wireOp",EDGE,"E14.39.5"),sQuery(id+"F0.wireOp",EDGE,"E14.39.6"),sQuery(id+"F0.wireOp",EDGE,"E14.39.7"),sQuery(id+"F0.wireOp",EDGE,"E14.39.8"),sQuery(id+"F0.wireOp",EDGE,"E14.39.9"),sQuery(id+"F0.wireOp",EDGE,"E14.40.0"),sQuery(id+"F0.wireOp",EDGE,"E14.40.1"),sQuery(id+"F0.wireOp",EDGE,"E14.40.2"),sQuery(id+"F0.wireOp",EDGE,"E14.40.3"),sQuery(id+"F0.wireOp",EDGE,"E14.40.4"),sQuery(id+"F0.wireOp",EDGE,"E14.40.5"),sQuery(id+"F0.wireOp",EDGE,"E14.40.6"),sQuery(id+"F0.wireOp",EDGE,"E14.40.7"),sQuery(id+"F0.wireOp",EDGE,"E14.40.8"),sQuery(id+"F0.wireOp",EDGE,"E14.40.9"),sQuery(id+"F0.wireOp",EDGE,"E14.41.0"),sQuery(id+"F0.wireOp",EDGE,"E14.41.1"),sQuery(id+"F0.wireOp",EDGE,"E14.41.2"),sQuery(id+"F0.wireOp",EDGE,"E14.41.3"),sQuery(id+"F0.wireOp",EDGE,"E14.41.4"),sQuery(id+"F0.wireOp",EDGE,"E14.41.5"),sQuery(id+"F0.wireOp",EDGE,"E14.41.6"),sQuery(id+"F0.wireOp",EDGE,"E14.41.7"),sQuery(id+"F0.wireOp",EDGE,"E14.41.8"),sQuery(id+"F0.wireOp",EDGE,"E14.41.9"),sQuery(id+"F0.wireOp",EDGE,"E14.42.0"),sQuery(id+"F0.wireOp",EDGE,"E14.42.1"),sQuery(id+"F0.wireOp",EDGE,"E14.42.2"),sQuery(id+"F0.wireOp",EDGE,"E14.42.3"),sQuery(id+"F0.wireOp",EDGE,"E14.42.4"),sQuery(id+"F0.wireOp",EDGE,"E14.42.5"),sQuery(id+"F0.wireOp",EDGE,"E14.42.6"),sQuery(id+"F0.wireOp",EDGE,"E14.42.7"),sQuery(id+"F0.wireOp",EDGE,"E14.42.8"),sQuery(id+"F0.wireOp",EDGE,"E14.42.9"),sQuery(id+"F0.wireOp",EDGE,"E14.43.0"),sQuery(id+"F0.wireOp",EDGE,"E14.43.1"),sQuery(id+"F0.wireOp",EDGE,"E14.43.2"),sQuery(id+"F0.wireOp",EDGE,"E14.43.3"),sQuery(id+"F0.wireOp",EDGE,"E14.43.4"),sQuery(id+"F0.wireOp",EDGE,"E14.43.5"),sQuery(id+"F0.wireOp",EDGE,"E14.43.6"),sQuery(id+"F0.wireOp",EDGE,"E14.43.7"),sQuery(id+"F0.wireOp",EDGE,"E14.43.8"),sQuery(id+"F0.wireOp",EDGE,"E14.43.9"),sQuery(id+"F0.wireOp",EDGE,"E14.44.0"),sQuery(id+"F0.wireOp",EDGE,"E14.44.1"),sQuery(id+"F0.wireOp",EDGE,"E14.44.2"),sQuery(id+"F0.wireOp",EDGE,"E14.44.3"),sQuery(id+"F0.wireOp",EDGE,"E14.44.4"),sQuery(id+"F0.wireOp",EDGE,"E14.44.5"),sQuery(id+"F0.wireOp",EDGE,"E14.44.6"),sQuery(id+"F0.wireOp",EDGE,"E14.44.7"),sQuery(id+"F0.wireOp",EDGE,"E14.44.8"),sQuery(id+"F0.wireOp",EDGE,"E14.44.9"),sQuery(id+"F0.wireOp",EDGE,"E14.45.0"),sQuery(id+"F0.wireOp",EDGE,"E14.45.1"),sQuery(id+"F0.wireOp",EDGE,"E14.45.2"),sQuery(id+"F0.wireOp",EDGE,"E14.45.3"),sQuery(id+"F0.wireOp",EDGE,"E14.45.4"),sQuery(id+"F0.wireOp",EDGE,"E14.45.5"),sQuery(id+"F0.wireOp",EDGE,"E14.45.6"),sQuery(id+"F0.wireOp",EDGE,"E14.45.7"),sQuery(id+"F0.wireOp",EDGE,"E14.45.8"),sQuery(id+"F0.wireOp",EDGE,"E14.45.9"),sQuery(id+"F0.wireOp",EDGE,"E14.46.0"),sQuery(id+"F0.wireOp",EDGE,"E14.46.1"),sQuery(id+"F0.wireOp",EDGE,"E14.46.2"),sQuery(id+"F0.wireOp",EDGE,"E14.46.3"),sQuery(id+"F0.wireOp",EDGE,"E14.46.4"),sQuery(id+"F0.wireOp",EDGE,"E14.46.5"),sQuery(id+"F0.wireOp",EDGE,"E14.46.6"),sQuery(id+"F0.wireOp",EDGE,"E14.46.7"),sQuery(id+"F0.wireOp",EDGE,"E14.46.8"),sQuery(id+"F0.wireOp",EDGE,"E14.46.9"),sQuery(id+"F0.wireOp",EDGE,"E14.47.0"),sQuery(id+"F0.wireOp",EDGE,"E14.47.1"),sQuery(id+"F0.wireOp",EDGE,"E14.47.2"),sQuery(id+"F0.wireOp",EDGE,"E14.47.3"),sQuery(id+"F0.wireOp",EDGE,"E14.47.4"),sQuery(id+"F0.wireOp",EDGE,"E14.47.5"),sQuery(id+"F0.wireOp",EDGE,"E14.47.6"),sQuery(id+"F0.wireOp",EDGE,"E14.47.7"),sQuery(id+"F0.wireOp",EDGE,"E14.47.8"),sQuery(id+"F0.wireOp",EDGE,"E14.47.9"),sQuery(id+"F0.wireOp",EDGE,"E14.48.0"),sQuery(id+"F0.wireOp",EDGE,"E14.48.1"),sQuery(id+"F0.wireOp",EDGE,"E14.48.2"),sQuery(id+"F0.wireOp",EDGE,"E14.48.3"),sQuery(id+"F0.wireOp",EDGE,"E14.48.4"),sQuery(id+"F0.wireOp",EDGE,"E14.48.5"),sQuery(id+"F0.wireOp",EDGE,"E14.48.6"),sQuery(id+"F0.wireOp",EDGE,"E14.48.7"),sQuery(id+"F0.wireOp",EDGE,"E14.48.8"),sQuery(id+"F0.wireOp",EDGE,"E14.48.9"),sQuery(id+"F0.wireOp",EDGE,"E14.49.0"),sQuery(id+"F0.wireOp",EDGE,"E14.49.1"),sQuery(id+"F0.wireOp",EDGE,"E14.49.2"),sQuery(id+"F0.wireOp",EDGE,"E14.49.3"),sQuery(id+"F0.wireOp",EDGE,"E14.49.4"),sQuery(id+"F0.wireOp",EDGE,"E14.49.5"),sQuery(id+"F0.wireOp",EDGE,"E14.49.6"),sQuery(id+"F0.wireOp",EDGE,"E14.49.7"),sQuery(id+"F0.wireOp",EDGE,"E14.49.8"),sQuery(id+"F0.wireOp",EDGE,"E14.49.9"),sQuery(id+"F0.wireOp",EDGE,"E14.50.0"),sQuery(id+"F0.wireOp",EDGE,"E14.50.1"),sQuery(id+"F0.wireOp",EDGE,"E14.50.2"),sQuery(id+"F0.wireOp",EDGE,"E14.50.3"),sQuery(id+"F0.wireOp",EDGE,"E14.50.4"),sQuery(id+"F0.wireOp",EDGE,"E14.50.5"),sQuery(id+"F0.wireOp",EDGE,"E14.50.6"),sQuery(id+"F0.wireOp",EDGE,"E14.50.7"),sQuery(id+"F0.wireOp",EDGE,"E14.50.8"),sQuery(id+"F0.wireOp",EDGE,"E14.50.9"),sQuery(id+"F0.wireOp",EDGE,"E14.51.0"),sQuery(id+"F0.wireOp",EDGE,"E14.51.1"),sQuery(id+"F0.wireOp",EDGE,"E14.51.2"),sQuery(id+"F0.wireOp",EDGE,"E14.51.3"),sQuery(id+"F0.wireOp",EDGE,"E14.51.4"),sQuery(id+"F0.wireOp",EDGE,"E14.51.5"),sQuery(id+"F0.wireOp",EDGE,"E14.51.6"),sQuery(id+"F0.wireOp",EDGE,"E14.51.7"),sQuery(id+"F0.wireOp",EDGE,"E14.51.8"),sQuery(id+"F0.wireOp",EDGE,"E14.51.9"),sQuery(id+"F0.wireOp",EDGE,"E14.52.0"),sQuery(id+"F0.wireOp",EDGE,"E14.52.1"),sQuery(id+"F0.wireOp",EDGE,"E14.52.2"),sQuery(id+"F0.wireOp",EDGE,"E14.52.3"),sQuery(id+"F0.wireOp",EDGE,"E14.52.4"),sQuery(id+"F0.wireOp",EDGE,"E14.52.5"),sQuery(id+"F0.wireOp",EDGE,"E14.52.6"),sQuery(id+"F0.wireOp",EDGE,"E14.52.7"),sQuery(id+"F0.wireOp",EDGE,"E14.52.8"),sQuery(id+"F0.wireOp",EDGE,"E14.52.9"),sQuery(id+"F0.wireOp",EDGE,"E14.53.0"),sQuery(id+"F0.wireOp",EDGE,"E14.53.1"),sQuery(id+"F0.wireOp",EDGE,"E14.53.2"),sQuery(id+"F0.wireOp",EDGE,"E14.53.3"),sQuery(id+"F0.wireOp",EDGE,"E14.53.4"),sQuery(id+"F0.wireOp",EDGE,"E14.53.5"),sQuery(id+"F0.wireOp",EDGE,"E14.53.6"),sQuery(id+"F0.wireOp",EDGE,"E14.53.7"),sQuery(id+"F0.wireOp",EDGE,"E14.53.8"),sQuery(id+"F0.wireOp",EDGE,"E14.53.9"),sQuery(id+"F0.wireOp",EDGE,"E14.54.0"),sQuery(id+"F0.wireOp",EDGE,"E14.54.1"),sQuery(id+"F0.wireOp",EDGE,"E14.54.2"),sQuery(id+"F0.wireOp",EDGE,"E14.54.3"),sQuery(id+"F0.wireOp",EDGE,"E14.54.4"),sQuery(id+"F0.wireOp",EDGE,"E14.54.5"),sQuery(id+"F0.wireOp",EDGE,"E14.54.6"),sQuery(id+"F0.wireOp",EDGE,"E14.54.7"),sQuery(id+"F0.wireOp",EDGE,"E14.54.8"),sQuery(id+"F0.wireOp",EDGE,"E14.54.9"),sQuery(id+"F0.wireOp",EDGE,"E14.55.0"),sQuery(id+"F0.wireOp",EDGE,"E14.55.1"),sQuery(id+"F0.wireOp",EDGE,"E14.55.2"),sQuery(id+"F0.wireOp",EDGE,"E14.55.3"),sQuery(id+"F0.wireOp",EDGE,"E14.55.4"),sQuery(id+"F0.wireOp",EDGE,"E14.55.5"),sQuery(id+"F0.wireOp",EDGE,"E14.55.6"),sQuery(id+"F0.wireOp",EDGE,"E14.55.7"),sQuery(id+"F0.wireOp",EDGE,"E14.55.8"),sQuery(id+"F0.wireOp",EDGE,"E14.55.9"),sQuery(id+"F0.wireOp",EDGE,"E14.56.0"),sQuery(id+"F0.wireOp",EDGE,"E14.56.1"),sQuery(id+"F0.wireOp",EDGE,"E14.56.2"),sQuery(id+"F0.wireOp",EDGE,"E14.56.3"),sQuery(id+"F0.wireOp",EDGE,"E14.56.4"),sQuery(id+"F0.wireOp",EDGE,"E14.56.5"),sQuery(id+"F0.wireOp",EDGE,"E14.56.6"),sQuery(id+"F0.wireOp",EDGE,"E14.56.7"),sQuery(id+"F0.wireOp",EDGE,"E14.56.8"),sQuery(id+"F0.wireOp",EDGE,"E14.56.9"),sQuery(id+"F0.wireOp",EDGE,"E14.57.0"),sQuery(id+"F0.wireOp",EDGE,"E14.57.1"),sQuery(id+"F0.wireOp",EDGE,"E14.57.2"),sQuery(id+"F0.wireOp",EDGE,"E14.57.3"),sQuery(id+"F0.wireOp",EDGE,"E14.57.4"),sQuery(id+"F0.wireOp",EDGE,"E14.57.5"),sQuery(id+"F0.wireOp",EDGE,"E14.57.6"),sQuery(id+"F0.wireOp",EDGE,"E14.57.7"),sQuery(id+"F0.wireOp",EDGE,"E14.57.8"),sQuery(id+"F0.wireOp",EDGE,"E14.57.9"),sQuery(id+"F0.wireOp",EDGE,"E14.58.0"),sQuery(id+"F0.wireOp",EDGE,"E14.58.1"),sQuery(id+"F0.wireOp",EDGE,"E14.58.2"),sQuery(id+"F0.wireOp",EDGE,"E14.58.3"),sQuery(id+"F0.wireOp",EDGE,"E14.58.4"),sQuery(id+"F0.wireOp",EDGE,"E14.58.5"),sQuery(id+"F0.wireOp",EDGE,"E14.58.6"),sQuery(id+"F0.wireOp",EDGE,"E14.58.7"),sQuery(id+"F0.wireOp",EDGE,"E14.58.8"),sQuery(id+"F0.wireOp",EDGE,"E14.58.9"),sQuery(id+"F0.wireOp",EDGE,"E14.59.0"),sQuery(id+"F0.wireOp",EDGE,"E14.59.1"),sQuery(id+"F0.wireOp",EDGE,"E14.59.2"),sQuery(id+"F0.wireOp",EDGE,"E14.59.3"),sQuery(id+"F0.wireOp",EDGE,"E14.59.4"),sQuery(id+"F0.wireOp",EDGE,"E14.59.5"),sQuery(id+"F0.wireOp",EDGE,"E14.59.6"),sQuery(id+"F0.wireOp",EDGE,"E14.59.7"),sQuery(id+"F0.wireOp",EDGE,"E14.59.8"),sQuery(id+"F0.wireOp",EDGE,"E14.59.9"),sQuery(id+"F0.wireOp",EDGE,"E14.60.0"),sQuery(id+"F0.wireOp",EDGE,"E14.60.1"),sQuery(id+"F0.wireOp",EDGE,"E14.60.2"),sQuery(id+"F0.wireOp",EDGE,"E14.60.3"),sQuery(id+"F0.wireOp",EDGE,"E14.60.4"),sQuery(id+"F0.wireOp",EDGE,"E14.60.5"),sQuery(id+"F0.wireOp",EDGE,"E14.60.6"),sQuery(id+"F0.wireOp",EDGE,"E14.60.7"),sQuery(id+"F0.wireOp",EDGE,"E14.60.8"),sQuery(id+"F0.wireOp",EDGE,"E14.60.9"),sQuery(id+"F0.wireOp",EDGE,"E14.61.0"),sQuery(id+"F0.wireOp",EDGE,"E14.61.1"),sQuery(id+"F0.wireOp",EDGE,"E14.61.2"),sQuery(id+"F0.wireOp",EDGE,"E14.61.3"),sQuery(id+"F0.wireOp",EDGE,"E14.61.4"),sQuery(id+"F0.wireOp",EDGE,"E14.61.5"),sQuery(id+"F0.wireOp",EDGE,"E14.61.6"),sQuery(id+"F0.wireOp",EDGE,"E14.61.7"),sQuery(id+"F0.wireOp",EDGE,"E14.61.8"),sQuery(id+"F0.wireOp",EDGE,"E14.61.9"),sQuery(id+"F0.wireOp",EDGE,"E14.62.0"),sQuery(id+"F0.wireOp",EDGE,"E14.62.1"),sQuery(id+"F0.wireOp",EDGE,"E14.62.2"),sQuery(id+"F0.wireOp",EDGE,"E14.62.3"),sQuery(id+"F0.wireOp",EDGE,"E14.62.4"),sQuery(id+"F0.wireOp",EDGE,"E14.62.5"),sQuery(id+"F0.wireOp",EDGE,"E14.62.6"),sQuery(id+"F0.wireOp",EDGE,"E14.62.7"),sQuery(id+"F0.wireOp",EDGE,"E14.62.8"),sQuery(id+"F0.wireOp",EDGE,"E14.62.9"),sQuery(id+"F0.wireOp",EDGE,"E14.63.0"),sQuery(id+"F0.wireOp",EDGE,"E14.63.1"),sQuery(id+"F0.wireOp",EDGE,"E14.63.2"),sQuery(id+"F0.wireOp",EDGE,"E14.63.3"),sQuery(id+"F0.wireOp",EDGE,"E14.63.4"),sQuery(id+"F0.wireOp",EDGE,"E14.63.5"),sQuery(id+"F0.wireOp",EDGE,"E14.63.6"),sQuery(id+"F0.wireOp",EDGE,"E14.63.7"),sQuery(id+"F0.wireOp",EDGE,"E14.63.8"),sQuery(id+"F0.wireOp",EDGE,"E14.63.9"),sQuery(id+"F0.wireOp",EDGE,"E14.64.0"),sQuery(id+"F0.wireOp",EDGE,"E14.64.1"),sQuery(id+"F0.wireOp",EDGE,"E14.64.2"),sQuery(id+"F0.wireOp",EDGE,"E14.64.3"),sQuery(id+"F0.wireOp",EDGE,"E14.64.4"),sQuery(id+"F0.wireOp",EDGE,"E14.64.5"),sQuery(id+"F0.wireOp",EDGE,"E14.64.6"),sQuery(id+"F0.wireOp",EDGE,"E14.64.7"),sQuery(id+"F0.wireOp",EDGE,"E14.64.8"),sQuery(id+"F0.wireOp",EDGE,"E14.64.9"),sQuery(id+"F0.wireOp",EDGE,"E14.65.0"),sQuery(id+"F0.wireOp",EDGE,"E14.65.1"),sQuery(id+"F0.wireOp",EDGE,"E14.65.2"),sQuery(id+"F0.wireOp",EDGE,"E14.65.3"),sQuery(id+"F0.wireOp",EDGE,"E14.65.4"),sQuery(id+"F0.wireOp",EDGE,"E14.65.5"),sQuery(id+"F0.wireOp",EDGE,"E14.65.6"),sQuery(id+"F0.wireOp",EDGE,"E14.65.7"),sQuery(id+"F0.wireOp",EDGE,"E14.65.8"),sQuery(id+"F0.wireOp",EDGE,"E14.65.9"),sQuery(id+"F0.wireOp",EDGE,"E14.66.0"),sQuery(id+"F0.wireOp",EDGE,"E14.66.1"),sQuery(id+"F0.wireOp",EDGE,"E14.66.2"),sQuery(id+"F0.wireOp",EDGE,"E14.66.3"),sQuery(id+"F0.wireOp",EDGE,"E14.66.4"),sQuery(id+"F0.wireOp",EDGE,"E14.66.5"),sQuery(id+"F0.wireOp",EDGE,"E14.66.6"),sQuery(id+"F0.wireOp",EDGE,"E14.66.7"),sQuery(id+"F0.wireOp",EDGE,"E14.66.8"),sQuery(id+"F0.wireOp",EDGE,"E14.66.9"),sQuery(id+"F0.wireOp",EDGE,"E14.67.0"),sQuery(id+"F0.wireOp",EDGE,"E14.67.1"),sQuery(id+"F0.wireOp",EDGE,"E14.67.2"),sQuery(id+"F0.wireOp",EDGE,"E14.67.3"),sQuery(id+"F0.wireOp",EDGE,"E14.67.4"),sQuery(id+"F0.wireOp",EDGE,"E14.67.5"),sQuery(id+"F0.wireOp",EDGE,"E14.67.6"),sQuery(id+"F0.wireOp",EDGE,"E14.67.7"),sQuery(id+"F0.wireOp",EDGE,"E14.67.8"),sQuery(id+"F0.wireOp",EDGE,"E14.67.9"),sQuery(id+"F0.wireOp",EDGE,"E14.68.0"),sQuery(id+"F0.wireOp",EDGE,"E14.68.1"),sQuery(id+"F0.wireOp",EDGE,"E14.68.2"),sQuery(id+"F0.wireOp",EDGE,"E14.68.3"),sQuery(id+"F0.wireOp",EDGE,"E14.68.4"),sQuery(id+"F0.wireOp",EDGE,"E14.68.5"),sQuery(id+"F0.wireOp",EDGE,"E14.68.6"),sQuery(id+"F0.wireOp",EDGE,"E14.68.7"),sQuery(id+"F0.wireOp",EDGE,"E14.68.8"),sQuery(id+"F0.wireOp",EDGE,"E14.68.9"),sQuery(id+"F0.wireOp",EDGE,"E14.69.0"),sQuery(id+"F0.wireOp",EDGE,"E14.69.1"),sQuery(id+"F0.wireOp",EDGE,"E14.69.2"),sQuery(id+"F0.wireOp",EDGE,"E14.69.3"),sQuery(id+"F0.wireOp",EDGE,"E14.69.4"),sQuery(id+"F0.wireOp",EDGE,"E14.69.5"),sQuery(id+"F0.wireOp",EDGE,"E14.69.6"),sQuery(id+"F0.wireOp",EDGE,"E14.69.7"),sQuery(id+"F0.wireOp",EDGE,"E14.69.8"),sQuery(id+"F0.wireOp",EDGE,"E14.69.9"),sQuery(id+"F0.wireOp",EDGE,"E14.70.0"),sQuery(id+"F0.wireOp",EDGE,"E14.70.1"),sQuery(id+"F0.wireOp",EDGE,"E14.70.2"),sQuery(id+"F0.wireOp",EDGE,"E14.70.3"),sQuery(id+"F0.wireOp",EDGE,"E14.70.4"),sQuery(id+"F0.wireOp",EDGE,"E14.70.5"),sQuery(id+"F0.wireOp",EDGE,"E14.70.6"),sQuery(id+"F0.wireOp",EDGE,"E14.70.7"),sQuery(id+"F0.wireOp",EDGE,"E14.70.8"),sQuery(id+"F0.wireOp",EDGE,"E14.70.9"),sQuery(id+"F0.wireOp",EDGE,"E14.71.0"),sQuery(id+"F0.wireOp",EDGE,"E14.71.1"),sQuery(id+"F0.wireOp",EDGE,"E14.71.2"),sQuery(id+"F0.wireOp",EDGE,"E14.71.3"),sQuery(id+"F0.wireOp",EDGE,"E14.71.4"),sQuery(id+"F0.wireOp",EDGE,"E14.71.5"),sQuery(id+"F0.wireOp",EDGE,"E14.71.6"),sQuery(id+"F0.wireOp",EDGE,"E14.71.7"),sQuery(id+"F0.wireOp",EDGE,"E14.71.8"),sQuery(id+"F0.wireOp",EDGE,"E14.71.9"),sQuery(id+"F0.wireOp",EDGE,"E14.72.0"),sQuery(id+"F0.wireOp",EDGE,"E14.72.1"),sQuery(id+"F0.wireOp",EDGE,"E14.72.2"),sQuery(id+"F0.wireOp",EDGE,"E14.72.3"),sQuery(id+"F0.wireOp",EDGE,"E14.72.4"),sQuery(id+"F0.wireOp",EDGE,"E14.72.5"),sQuery(id+"F0.wireOp",EDGE,"E14.72.6"),sQuery(id+"F0.wireOp",EDGE,"E14.72.7"),sQuery(id+"F0.wireOp",EDGE,"E14.72.8"),sQuery(id+"F0.wireOp",EDGE,"E14.72.9"),sQuery(id+"F0.wireOp",EDGE,"E14.73.0"),sQuery(id+"F0.wireOp",EDGE,"E14.73.1"),sQuery(id+"F0.wireOp",EDGE,"E14.73.2"),sQuery(id+"F0.wireOp",EDGE,"E14.73.3"),sQuery(id+"F0.wireOp",EDGE,"E14.73.4"),sQuery(id+"F0.wireOp",EDGE,"E14.73.5"),sQuery(id+"F0.wireOp",EDGE,"E14.73.6"),sQuery(id+"F0.wireOp",EDGE,"E14.73.7"),sQuery(id+"F0.wireOp",EDGE,"E14.73.8"),sQuery(id+"F0.wireOp",EDGE,"E14.73.9"),sQuery(id+"F0.wireOp",EDGE,"E14.74.0"),sQuery(id+"F0.wireOp",EDGE,"E14.74.1"),sQuery(id+"F0.wireOp",EDGE,"E14.74.2"),sQuery(id+"F0.wireOp",EDGE,"E14.74.3"),sQuery(id+"F0.wireOp",EDGE,"E14.74.4"),sQuery(id+"F0.wireOp",EDGE,"E14.74.5"),sQuery(id+"F0.wireOp",EDGE,"E14.74.6"),sQuery(id+"F0.wireOp",EDGE,"E14.74.7"),sQuery(id+"F0.wireOp",EDGE,"E14.74.8"),sQuery(id+"F0.wireOp",EDGE,"E14.74.9"),sQuery(id+"F0.wireOp",EDGE,"E14.75.0"),sQuery(id+"F0.wireOp",EDGE,"E14.75.1"),sQuery(id+"F0.wireOp",EDGE,"E14.75.2"),sQuery(id+"F0.wireOp",EDGE,"E14.75.3"),sQuery(id+"F0.wireOp",EDGE,"E14.75.4"),sQuery(id+"F0.wireOp",EDGE,"E14.75.5"),sQuery(id+"F0.wireOp",EDGE,"E14.75.6"),sQuery(id+"F0.wireOp",EDGE,"E14.75.7"),sQuery(id+"F0.wireOp",EDGE,"E14.75.8"),sQuery(id+"F0.wireOp",EDGE,"E14.75.9"),sQuery(id+"F0.wireOp",EDGE,"E14.76.0"),sQuery(id+"F0.wireOp",EDGE,"E14.76.1"),sQuery(id+"F0.wireOp",EDGE,"E14.76.2"),sQuery(id+"F0.wireOp",EDGE,"E14.76.3"),sQuery(id+"F0.wireOp",EDGE,"E14.76.4"),sQuery(id+"F0.wireOp",EDGE,"E14.76.5"),sQuery(id+"F0.wireOp",EDGE,"E14.76.6"),sQuery(id+"F0.wireOp",EDGE,"E14.76.7"),sQuery(id+"F0.wireOp",EDGE,"E14.76.8"),sQuery(id+"F0.wireOp",EDGE,"E14.76.9"),sQuery(id+"F0.wireOp",EDGE,"E14.77.0"),sQuery(id+"F0.wireOp",EDGE,"E14.77.1"),sQuery(id+"F0.wireOp",EDGE,"E14.77.2"),sQuery(id+"F0.wireOp",EDGE,"E14.77.3"),sQuery(id+"F0.wireOp",EDGE,"E14.77.4"),sQuery(id+"F0.wireOp",EDGE,"E14.77.5"),sQuery(id+"F0.wireOp",EDGE,"E14.77.6"),sQuery(id+"F0.wireOp",EDGE,"E14.77.7"),sQuery(id+"F0.wireOp",EDGE,"E14.77.8"),sQuery(id+"F0.wireOp",EDGE,"E14.77.9"),sQuery(id+"F0.wireOp",EDGE,"E14.78.0"),sQuery(id+"F0.wireOp",EDGE,"E14.78.1"),sQuery(id+"F0.wireOp",EDGE,"E14.78.2"),sQuery(id+"F0.wireOp",EDGE,"E14.78.3"),sQuery(id+"F0.wireOp",EDGE,"E14.78.4"),sQuery(id+"F0.wireOp",EDGE,"E14.78.5"),sQuery(id+"F0.wireOp",EDGE,"E14.78.6"),sQuery(id+"F0.wireOp",EDGE,"E14.78.7"),sQuery(id+"F0.wireOp",EDGE,"E14.78.8"),sQuery(id+"F0.wireOp",EDGE,"E14.78.9"),sQuery(id+"F0.wireOp",EDGE,"E14.79.0"),sQuery(id+"F0.wireOp",EDGE,"E14.79.1"),sQuery(id+"F0.wireOp",EDGE,"E14.79.2"),sQuery(id+"F0.wireOp",EDGE,"E14.79.3"),sQuery(id+"F0.wireOp",EDGE,"E14.79.4"),sQuery(id+"F0.wireOp",EDGE,"E14.79.5"),sQuery(id+"F0.wireOp",EDGE,"E14.79.6"),sQuery(id+"F0.wireOp",EDGE,"E14.79.7"),sQuery(id+"F0.wireOp",EDGE,"E14.79.8"),sQuery(id+"F0.wireOp",EDGE,"E14.79.9"),sQuery(id+"F0.wireOp",EDGE,"E14.80.0"),sQuery(id+"F0.wireOp",EDGE,"E14.80.1"),sQuery(id+"F0.wireOp",EDGE,"E14.80.2"),sQuery(id+"F0.wireOp",EDGE,"E14.80.3"),sQuery(id+"F0.wireOp",EDGE,"E14.80.4"),sQuery(id+"F0.wireOp",EDGE,"E14.80.5"),sQuery(id+"F0.wireOp",EDGE,"E14.80.6"),sQuery(id+"F0.wireOp",EDGE,"E14.80.7"),sQuery(id+"F0.wireOp",EDGE,"E14.80.8"),sQuery(id+"F0.wireOp",EDGE,"E14.80.9"),sQuery(id+"F0.wireOp",EDGE,"E14.81.0"),sQuery(id+"F0.wireOp",EDGE,"E14.81.1"),sQuery(id+"F0.wireOp",EDGE,"E14.81.2"),sQuery(id+"F0.wireOp",EDGE,"E14.81.3"),sQuery(id+"F0.wireOp",EDGE,"E14.81.4"),sQuery(id+"F0.wireOp",EDGE,"E14.81.5"),sQuery(id+"F0.wireOp",EDGE,"E14.81.6"),sQuery(id+"F0.wireOp",EDGE,"E14.81.7"),sQuery(id+"F0.wireOp",EDGE,"E14.81.8"),sQuery(id+"F0.wireOp",EDGE,"E14.81.9"),sQuery(id+"F0.wireOp",EDGE,"E14.82.0"),sQuery(id+"F0.wireOp",EDGE,"E14.82.1"),sQuery(id+"F0.wireOp",EDGE,"E14.82.2"),sQuery(id+"F0.wireOp",EDGE,"E14.82.3"),sQuery(id+"F0.wireOp",EDGE,"E14.82.4"),sQuery(id+"F0.wireOp",EDGE,"E14.82.5"),sQuery(id+"F0.wireOp",EDGE,"E14.82.6"),sQuery(id+"F0.wireOp",EDGE,"E14.82.7"),sQuery(id+"F0.wireOp",EDGE,"E14.82.8"),sQuery(id+"F0.wireOp",EDGE,"E14.82.9"),sQuery(id+"F0.wireOp",EDGE,"E14.83.0"),sQuery(id+"F0.wireOp",EDGE,"E14.83.1"),sQuery(id+"F0.wireOp",EDGE,"E14.83.2"),sQuery(id+"F0.wireOp",EDGE,"E14.83.3"),sQuery(id+"F0.wireOp",EDGE,"E14.83.4"),sQuery(id+"F0.wireOp",EDGE,"E14.83.5"),sQuery(id+"F0.wireOp",EDGE,"E14.83.6"),sQuery(id+"F0.wireOp",EDGE,"E14.83.7"),sQuery(id+"F0.wireOp",EDGE,"E14.83.8"),sQuery(id+"F0.wireOp",EDGE,"E14.83.9"),sQuery(id+"F0.wireOp",EDGE,"E14.84.0"),sQuery(id+"F0.wireOp",EDGE,"E14.84.1"),sQuery(id+"F0.wireOp",EDGE,"E14.84.2"),sQuery(id+"F0.wireOp",EDGE,"E14.84.3"),sQuery(id+"F0.wireOp",EDGE,"E14.84.4"),sQuery(id+"F0.wireOp",EDGE,"E14.84.5"),sQuery(id+"F0.wireOp",EDGE,"E14.84.6"),sQuery(id+"F0.wireOp",EDGE,"E14.84.7"),sQuery(id+"F0.wireOp",EDGE,"E14.84.8"),sQuery(id+"F0.wireOp",EDGE,"E14.84.9"),sQuery(id+"F0.wireOp",EDGE,"E14.85.0"),sQuery(id+"F0.wireOp",EDGE,"E14.85.1"),sQuery(id+"F0.wireOp",EDGE,"E14.85.2"),sQuery(id+"F0.wireOp",EDGE,"E14.85.3"),sQuery(id+"F0.wireOp",EDGE,"E14.85.4"),sQuery(id+"F0.wireOp",EDGE,"E14.85.5"),sQuery(id+"F0.wireOp",EDGE,"E14.85.6"),sQuery(id+"F0.wireOp",EDGE,"E14.85.7"),sQuery(id+"F0.wireOp",EDGE,"E14.85.8"),sQuery(id+"F0.wireOp",EDGE,"E14.85.9"),sQuery(id+"F0.wireOp",EDGE,"E14.86.0"),sQuery(id+"F0.wireOp",EDGE,"E14.86.1"),sQuery(id+"F0.wireOp",EDGE,"E14.86.2"),sQuery(id+"F0.wireOp",EDGE,"E14.86.3"),sQuery(id+"F0.wireOp",EDGE,"E14.86.4"),sQuery(id+"F0.wireOp",EDGE,"E14.86.5"),sQuery(id+"F0.wireOp",EDGE,"E14.86.6"),sQuery(id+"F0.wireOp",EDGE,"E14.86.7"),sQuery(id+"F0.wireOp",EDGE,"E14.86.8"),sQuery(id+"F0.wireOp",EDGE,"E14.86.9"),sQuery(id+"F0.wireOp",EDGE,"E14.87.0"),sQuery(id+"F0.wireOp",EDGE,"E14.87.1"),sQuery(id+"F0.wireOp",EDGE,"E14.87.2"),sQuery(id+"F0.wireOp",EDGE,"E14.87.3"),sQuery(id+"F0.wireOp",EDGE,"E14.87.4"),sQuery(id+"F0.wireOp",EDGE,"E14.87.5"),sQuery(id+"F0.wireOp",EDGE,"E14.87.6"),sQuery(id+"F0.wireOp",EDGE,"E14.87.7"),sQuery(id+"F0.wireOp",EDGE,"E14.87.8"),sQuery(id+"F0.wireOp",EDGE,"E14.87.9"),sQuery(id+"F0.wireOp",EDGE,"E14.88.0"),sQuery(id+"F0.wireOp",EDGE,"E14.88.1"),sQuery(id+"F0.wireOp",EDGE,"E14.88.2"),sQuery(id+"F0.wireOp",EDGE,"E14.88.3"),sQuery(id+"F0.wireOp",EDGE,"E14.88.4"),sQuery(id+"F0.wireOp",EDGE,"E14.88.5"),sQuery(id+"F0.wireOp",EDGE,"E14.88.6"),sQuery(id+"F0.wireOp",EDGE,"E14.88.7"),sQuery(id+"F0.wireOp",EDGE,"E14.88.8"),sQuery(id+"F0.wireOp",EDGE,"E14.88.9"),sQuery(id+"F0.wireOp",EDGE,"E14.89.0"),sQuery(id+"F0.wireOp",EDGE,"E14.89.1"),sQuery(id+"F0.wireOp",EDGE,"E14.89.2"),sQuery(id+"F0.wireOp",EDGE,"E14.89.3"),sQuery(id+"F0.wireOp",EDGE,"E14.89.4"),sQuery(id+"F0.wireOp",EDGE,"E14.89.5"),sQuery(id+"F0.wireOp",EDGE,"E14.89.6"),sQuery(id+"F0.wireOp",EDGE,"E14.89.7"),sQuery(id+"F0.wireOp",EDGE,"E14.89.8"),sQuery(id+"F0.wireOp",EDGE,"E14.89.9"),sQuery(id+"F0.wireOp",EDGE,"E14.90.0"),sQuery(id+"F0.wireOp",EDGE,"E14.90.1"),sQuery(id+"F0.wireOp",EDGE,"E14.90.2"),sQuery(id+"F0.wireOp",EDGE,"E14.90.3"),sQuery(id+"F0.wireOp",EDGE,"E14.90.4"),sQuery(id+"F0.wireOp",EDGE,"E14.90.5"),sQuery(id+"F0.wireOp",EDGE,"E14.90.6"),sQuery(id+"F0.wireOp",EDGE,"E14.90.7"),sQuery(id+"F0.wireOp",EDGE,"E14.90.8"),sQuery(id+"F0.wireOp",EDGE,"E14.90.9"),sQuery(id+"F0.wireOp",EDGE,"E14.91.0"),sQuery(id+"F0.wireOp",EDGE,"E14.91.1"),sQuery(id+"F0.wireOp",EDGE,"E14.91.2"),sQuery(id+"F0.wireOp",EDGE,"E14.91.3"),sQuery(id+"F0.wireOp",EDGE,"E14.91.4"),sQuery(id+"F0.wireOp",EDGE,"E14.91.5"),sQuery(id+"F0.wireOp",EDGE,"E14.91.6"),sQuery(id+"F0.wireOp",EDGE,"E14.91.7"),sQuery(id+"F0.wireOp",EDGE,"E14.91.8"),sQuery(id+"F0.wireOp",EDGE,"E14.91.9"),sQuery(id+"F0.wireOp",EDGE,"E14.92.0"),sQuery(id+"F0.wireOp",EDGE,"E14.92.1"),sQuery(id+"F0.wireOp",EDGE,"E14.92.2"),sQuery(id+"F0.wireOp",EDGE,"E14.92.3"),sQuery(id+"F0.wireOp",EDGE,"E14.92.4"),sQuery(id+"F0.wireOp",EDGE,"E14.92.5"),sQuery(id+"F0.wireOp",EDGE,"E14.92.6"),sQuery(id+"F0.wireOp",EDGE,"E14.92.7"),sQuery(id+"F0.wireOp",EDGE,"E14.92.8"),sQuery(id+"F0.wireOp",EDGE,"E14.92.9"),sQuery(id+"F0.wireOp",EDGE,"E14.93.0"),sQuery(id+"F0.wireOp",EDGE,"E14.93.1"),sQuery(id+"F0.wireOp",EDGE,"E14.93.2"),sQuery(id+"F0.wireOp",EDGE,"E14.93.3"),sQuery(id+"F0.wireOp",EDGE,"E14.93.4"),sQuery(id+"F0.wireOp",EDGE,"E14.93.5"),sQuery(id+"F0.wireOp",EDGE,"E14.93.6"),sQuery(id+"F0.wireOp",EDGE,"E14.93.7"),sQuery(id+"F0.wireOp",EDGE,"E14.93.8"),sQuery(id+"F0.wireOp",EDGE,"E14.93.9"),sQuery(id+"F0.wireOp",EDGE,"E14.94.0"),sQuery(id+"F0.wireOp",EDGE,"E14.94.1"),sQuery(id+"F0.wireOp",EDGE,"E14.94.2"),sQuery(id+"F0.wireOp",EDGE,"E14.94.3"),sQuery(id+"F0.wireOp",EDGE,"E14.94.4"),sQuery(id+"F0.wireOp",EDGE,"E14.94.5"),sQuery(id+"F0.wireOp",EDGE,"E14.94.6"),sQuery(id+"F0.wireOp",EDGE,"E14.94.7"),sQuery(id+"F0.wireOp",EDGE,"E14.94.8"),sQuery(id+"F0.wireOp",EDGE,"E14.94.9"),sQuery(id+"F0.wireOp",EDGE,"E14.95.0"),sQuery(id+"F0.wireOp",EDGE,"E14.95.1"),sQuery(id+"F0.wireOp",EDGE,"E14.95.2"),sQuery(id+"F0.wireOp",EDGE,"E14.95.3"),sQuery(id+"F0.wireOp",EDGE,"E14.95.4"),sQuery(id+"F0.wireOp",EDGE,"E14.95.5"),sQuery(id+"F0.wireOp",EDGE,"E14.95.6"),sQuery(id+"F0.wireOp",EDGE,"E14.95.7"),sQuery(id+"F0.wireOp",EDGE,"E14.95.8"),sQuery(id+"F0.wireOp",EDGE,"E14.95.9"),sQuery(id+"F0.wireOp",EDGE,"E14.96.0"),sQuery(id+"F0.wireOp",EDGE,"E14.96.1"),sQuery(id+"F0.wireOp",EDGE,"E14.96.2"),sQuery(id+"F0.wireOp",EDGE,"E14.96.3"),sQuery(id+"F0.wireOp",EDGE,"E14.96.4"),sQuery(id+"F0.wireOp",EDGE,"E14.96.5"),sQuery(id+"F0.wireOp",EDGE,"E14.96.6"),sQuery(id+"F0.wireOp",EDGE,"E14.96.7"),sQuery(id+"F0.wireOp",EDGE,"E14.96.8"),sQuery(id+"F0.wireOp",EDGE,"E14.96.9"),sQuery(id+"F0.wireOp",EDGE,"E14.97.0"),sQuery(id+"F0.wireOp",EDGE,"E14.97.1"),sQuery(id+"F0.wireOp",EDGE,"E14.97.2"),sQuery(id+"F0.wireOp",EDGE,"E14.97.3"),sQuery(id+"F0.wireOp",EDGE,"E14.97.4"),sQuery(id+"F0.wireOp",EDGE,"E14.97.5"),sQuery(id+"F0.wireOp",EDGE,"E14.97.6"),sQuery(id+"F0.wireOp",EDGE,"E14.97.7"),sQuery(id+"F0.wireOp",EDGE,"E14.97.8"),sQuery(id+"F0.wireOp",EDGE,"E14.97.9"),sQuery(id+"F0.wireOp",EDGE,"E14.98.0"),sQuery(id+"F0.wireOp",EDGE,"E14.98.1"),sQuery(id+"F0.wireOp",EDGE,"E14.98.2"),sQuery(id+"F0.wireOp",EDGE,"E14.98.3"),sQuery(id+"F0.wireOp",EDGE,"E14.98.4"),sQuery(id+"F0.wireOp",EDGE,"E14.98.5"),sQuery(id+"F0.wireOp",EDGE,"E14.98.6"),sQuery(id+"F0.wireOp",EDGE,"E14.98.7"),sQuery(id+"F0.wireOp",EDGE,"E14.98.8"),sQuery(id+"F0.wireOp",EDGE,"E14.98.9"),sQuery(id+"F0.wireOp",EDGE,"E14.99.0"),sQuery(id+"F0.wireOp",EDGE,"E14.99.1"),sQuery(id+"F0.wireOp",EDGE,"E14.99.2"),sQuery(id+"F0.wireOp",EDGE,"E14.99.3"),sQuery(id+"F0.wireOp",EDGE,"E14.99.4"),sQuery(id+"F0.wireOp",EDGE,"E14.99.5"),sQuery(id+"F0.wireOp",EDGE,"E14.99.6"),sQuery(id+"F0.wireOp",EDGE,"E14.99.7"),sQuery(id+"F0.wireOp",EDGE,"E14.99.8"),sQuery(id+"F0.wireOp",EDGE,"E14.99.9"),sQuery(id+"F0.wireOp",EDGE,"E14.100.0"),sQuery(id+"F0.wireOp",EDGE,"E14.100.1"),sQuery(id+"F0.wireOp",EDGE,"E14.100.2"),sQuery(id+"F0.wireOp",EDGE,"E14.100.3"),sQuery(id+"F0.wireOp",EDGE,"E14.100.4"),sQuery(id+"F0.wireOp",EDGE,"E14.100.5"),sQuery(id+"F0.wireOp",EDGE,"E14.100.6"),sQuery(id+"F0.wireOp",EDGE,"E14.100.7"),sQuery(id+"F0.wireOp",EDGE,"E14.100.8"),sQuery(id+"F0.wireOp",EDGE,"E14.100.9"),sQuery(id+"F0.wireOp",EDGE,"E14.101.0"),sQuery(id+"F0.wireOp",EDGE,"E14.101.1"),sQuery(id+"F0.wireOp",EDGE,"E14.101.2"),sQuery(id+"F0.wireOp",EDGE,"E14.101.3"),sQuery(id+"F0.wireOp",EDGE,"E14.101.4"),sQuery(id+"F0.wireOp",EDGE,"E14.101.5"),sQuery(id+"F0.wireOp",EDGE,"E14.101.6"),sQuery(id+"F0.wireOp",EDGE,"E14.101.7"),sQuery(id+"F0.wireOp",EDGE,"E14.101.8"),sQuery(id+"F0.wireOp",EDGE,"E14.101.9"),sQuery(id+"F0.wireOp",EDGE,"E14.102.0"),sQuery(id+"F0.wireOp",EDGE,"E14.102.1"),sQuery(id+"F0.wireOp",EDGE,"E14.102.2"),sQuery(id+"F0.wireOp",EDGE,"E14.102.3"),sQuery(id+"F0.wireOp",EDGE,"E14.102.4"),sQuery(id+"F0.wireOp",EDGE,"E14.102.5"),sQuery(id+"F0.wireOp",EDGE,"E14.102.6"),sQuery(id+"F0.wireOp",EDGE,"E14.102.7"),sQuery(id+"F0.wireOp",EDGE,"E14.102.8"),sQuery(id+"F0.wireOp",EDGE,"E14.102.9"),sQuery(id+"F0.wireOp",EDGE,"E14.103.0"),sQuery(id+"F0.wireOp",EDGE,"E14.103.1"),sQuery(id+"F0.wireOp",EDGE,"E14.103.2"),sQuery(id+"F0.wireOp",EDGE,"E14.103.3"),sQuery(id+"F0.wireOp",EDGE,"E14.103.4"),sQuery(id+"F0.wireOp",EDGE,"E14.103.5"),sQuery(id+"F0.wireOp",EDGE,"E14.103.6"),sQuery(id+"F0.wireOp",EDGE,"E14.103.7"),sQuery(id+"F0.wireOp",EDGE,"E14.103.8"),sQuery(id+"F0.wireOp",EDGE,"E14.103.9"),sQuery(id+"F0.wireOp",EDGE,"E14.104.0"),sQuery(id+"F0.wireOp",EDGE,"E14.104.1"),sQuery(id+"F0.wireOp",EDGE,"E14.104.2"),sQuery(id+"F0.wireOp",EDGE,"E14.104.3"),sQuery(id+"F0.wireOp",EDGE,"E14.104.4"),sQuery(id+"F0.wireOp",EDGE,"E14.104.5"),sQuery(id+"F0.wireOp",EDGE,"E14.104.6"),sQuery(id+"F0.wireOp",EDGE,"E14.104.7"),sQuery(id+"F0.wireOp",EDGE,"E14.104.8"),sQuery(id+"F0.wireOp",EDGE,"E14.104.9"),sQuery(id+"F0.wireOp",EDGE,"E14.105.0"),sQuery(id+"F0.wireOp",EDGE,"E14.105.1"),sQuery(id+"F0.wireOp",EDGE,"E14.105.2"),sQuery(id+"F0.wireOp",EDGE,"E14.105.3"),sQuery(id+"F0.wireOp",EDGE,"E14.105.4"),sQuery(id+"F0.wireOp",EDGE,"E14.105.5"),sQuery(id+"F0.wireOp",EDGE,"E14.105.6"),sQuery(id+"F0.wireOp",EDGE,"E14.105.7"),sQuery(id+"F0.wireOp",EDGE,"E14.105.8"),sQuery(id+"F0.wireOp",EDGE,"E14.105.9"),sQuery(id+"F0.wireOp",EDGE,"E14.106.0"),sQuery(id+"F0.wireOp",EDGE,"E14.106.1"),sQuery(id+"F0.wireOp",EDGE,"E14.106.2"),sQuery(id+"F0.wireOp",EDGE,"E14.106.3"),sQuery(id+"F0.wireOp",EDGE,"E14.106.4"),sQuery(id+"F0.wireOp",EDGE,"E14.106.5"),sQuery(id+"F0.wireOp",EDGE,"E14.106.6"),sQuery(id+"F0.wireOp",EDGE,"E14.106.7"),sQuery(id+"F0.wireOp",EDGE,"E14.106.8"),sQuery(id+"F0.wireOp",EDGE,"E14.106.9"),sQuery(id+"F0.wireOp",EDGE,"E14.107.0"),sQuery(id+"F0.wireOp",EDGE,"E14.107.1"),sQuery(id+"F0.wireOp",EDGE,"E14.107.2"),sQuery(id+"F0.wireOp",EDGE,"E14.107.3"),sQuery(id+"F0.wireOp",EDGE,"E14.107.4"),sQuery(id+"F0.wireOp",EDGE,"E14.107.5"),sQuery(id+"F0.wireOp",EDGE,"E14.107.6"),sQuery(id+"F0.wireOp",EDGE,"E14.107.7"),sQuery(id+"F0.wireOp",EDGE,"E14.107.8"),sQuery(id+"F0.wireOp",EDGE,"E14.107.9"),sQuery(id+"F0.wireOp",EDGE,"E14.108.0"),sQuery(id+"F0.wireOp",EDGE,"E14.108.1"),sQuery(id+"F0.wireOp",EDGE,"E14.108.2"),sQuery(id+"F0.wireOp",EDGE,"E14.108.3"),sQuery(id+"F0.wireOp",EDGE,"E14.108.4"),sQuery(id+"F0.wireOp",EDGE,"E14.108.5"),sQuery(id+"F0.wireOp",EDGE,"E14.108.6"),sQuery(id+"F0.wireOp",EDGE,"E14.108.7"),sQuery(id+"F0.wireOp",EDGE,"E14.108.8"),sQuery(id+"F0.wireOp",EDGE,"E14.108.9"),sQuery(id+"F0.wireOp",EDGE,"E14.109.0"),sQuery(id+"F0.wireOp",EDGE,"E14.109.1"),sQuery(id+"F0.wireOp",EDGE,"E14.109.2"),sQuery(id+"F0.wireOp",EDGE,"E14.109.3"),sQuery(id+"F0.wireOp",EDGE,"E14.109.4"),sQuery(id+"F0.wireOp",EDGE,"E14.109.5"),sQuery(id+"F0.wireOp",EDGE,"E14.109.6"),sQuery(id+"F0.wireOp",EDGE,"E14.109.7"),sQuery(id+"F0.wireOp",EDGE,"E14.109.8"),sQuery(id+"F0.wireOp",EDGE,"E14.109.9"),sQuery(id+"F0.wireOp",EDGE,"E14.110.0"),sQuery(id+"F0.wireOp",EDGE,"E14.110.1"),sQuery(id+"F0.wireOp",EDGE,"E14.110.2"),sQuery(id+"F0.wireOp",EDGE,"E14.110.3"),sQuery(id+"F0.wireOp",EDGE,"E14.110.4"),sQuery(id+"F0.wireOp",EDGE,"E14.110.5"),sQuery(id+"F0.wireOp",EDGE,"E14.110.6"),sQuery(id+"F0.wireOp",EDGE,"E14.110.7"),sQuery(id+"F0.wireOp",EDGE,"E14.110.8"),sQuery(id+"F0.wireOp",EDGE,"E14.110.9"),sQuery(id+"F0.wireOp",EDGE,"E14.111.0"),sQuery(id+"F0.wireOp",EDGE,"E14.111.1"),sQuery(id+"F0.wireOp",EDGE,"E14.111.2"),sQuery(id+"F0.wireOp",EDGE,"E14.111.3"),sQuery(id+"F0.wireOp",EDGE,"E14.111.4"),sQuery(id+"F0.wireOp",EDGE,"E14.111.5"),sQuery(id+"F0.wireOp",EDGE,"E14.111.6"),sQuery(id+"F0.wireOp",EDGE,"E14.111.7"),sQuery(id+"F0.wireOp",EDGE,"E14.111.8"),sQuery(id+"F0.wireOp",EDGE,"E14.111.9"),sQuery(id+"F0.wireOp",EDGE,"E14.112.0"),sQuery(id+"F0.wireOp",EDGE,"E14.112.1"),sQuery(id+"F0.wireOp",EDGE,"E14.112.2"),sQuery(id+"F0.wireOp",EDGE,"E14.112.3"),sQuery(id+"F0.wireOp",EDGE,"E14.112.4"),sQuery(id+"F0.wireOp",EDGE,"E14.112.5"),sQuery(id+"F0.wireOp",EDGE,"E14.112.6"),sQuery(id+"F0.wireOp",EDGE,"E14.112.7"),sQuery(id+"F0.wireOp",EDGE,"E14.112.8"),sQuery(id+"F0.wireOp",EDGE,"E14.112.9"),sQuery(id+"F0.wireOp",EDGE,"E14.113.0"),sQuery(id+"F0.wireOp",EDGE,"E14.113.1"),sQuery(id+"F0.wireOp",EDGE,"E14.113.2"),sQuery(id+"F0.wireOp",EDGE,"E14.113.3"),sQuery(id+"F0.wireOp",EDGE,"E14.113.4"),sQuery(id+"F0.wireOp",EDGE,"E14.113.5"),sQuery(id+"F0.wireOp",EDGE,"E14.113.6"),sQuery(id+"F0.wireOp",EDGE,"E14.113.7"),sQuery(id+"F0.wireOp",EDGE,"E14.113.8"),sQuery(id+"F0.wireOp",EDGE,"E14.113.9"),sQuery(id+"F0.wireOp",EDGE,"E14.114.0"),sQuery(id+"F0.wireOp",EDGE,"E14.114.1"),sQuery(id+"F0.wireOp",EDGE,"E14.114.2"),sQuery(id+"F0.wireOp",EDGE,"E14.114.3"),sQuery(id+"F0.wireOp",EDGE,"E14.114.4"),sQuery(id+"F0.wireOp",EDGE,"E14.114.5"),sQuery(id+"F0.wireOp",EDGE,"E14.114.6"),sQuery(id+"F0.wireOp",EDGE,"E14.114.7"),sQuery(id+"F0.wireOp",EDGE,"E14.114.8"),sQuery(id+"F0.wireOp",EDGE,"E14.114.9"),sQuery(id+"F0.wireOp",EDGE,"E14.115.0"),sQuery(id+"F0.wireOp",EDGE,"E14.115.1"),sQuery(id+"F0.wireOp",EDGE,"E14.115.2"),sQuery(id+"F0.wireOp",EDGE,"E14.115.3"),sQuery(id+"F0.wireOp",EDGE,"E14.115.4"),sQuery(id+"F0.wireOp",EDGE,"E14.115.5"),sQuery(id+"F0.wireOp",EDGE,"E14.115.6"),sQuery(id+"F0.wireOp",EDGE,"E14.115.7"),sQuery(id+"F0.wireOp",EDGE,"E14.115.8"),sQuery(id+"F0.wireOp",EDGE,"E14.115.9"),sQuery(id+"F0.wireOp",EDGE,"E14.116.0"),sQuery(id+"F0.wireOp",EDGE,"E14.116.1"),sQuery(id+"F0.wireOp",EDGE,"E14.116.2"),sQuery(id+"F0.wireOp",EDGE,"E14.116.3"),sQuery(id+"F0.wireOp",EDGE,"E14.116.4"),sQuery(id+"F0.wireOp",EDGE,"E14.116.5"),sQuery(id+"F0.wireOp",EDGE,"E14.116.6"),sQuery(id+"F0.wireOp",EDGE,"E14.116.7"),sQuery(id+"F0.wireOp",EDGE,"E14.116.8"),sQuery(id+"F0.wireOp",EDGE,"E14.116.9"),sQuery(id+"F0.wireOp",EDGE,"E14.117.0"),sQuery(id+"F0.wireOp",EDGE,"E14.117.1"),sQuery(id+"F0.wireOp",EDGE,"E14.117.2"),sQuery(id+"F0.wireOp",EDGE,"E14.117.3"),sQuery(id+"F0.wireOp",EDGE,"E14.117.4"),sQuery(id+"F0.wireOp",EDGE,"E14.117.5"),sQuery(id+"F0.wireOp",EDGE,"E14.117.6"),sQuery(id+"F0.wireOp",EDGE,"E14.117.7"),sQuery(id+"F0.wireOp",EDGE,"E14.117.8"),sQuery(id+"F0.wireOp",EDGE,"E14.117.9"),sQuery(id+"F0.wireOp",EDGE,"E14.118.0"),sQuery(id+"F0.wireOp",EDGE,"E14.118.1"),sQuery(id+"F0.wireOp",EDGE,"E14.118.2"),sQuery(id+"F0.wireOp",EDGE,"E14.118.3"),sQuery(id+"F0.wireOp",EDGE,"E14.118.4"),sQuery(id+"F0.wireOp",EDGE,"E14.118.5"),sQuery(id+"F0.wireOp",EDGE,"E14.118.6"),sQuery(id+"F0.wireOp",EDGE,"E14.118.7"),sQuery(id+"F0.wireOp",EDGE,"E14.118.8"),sQuery(id+"F0.wireOp",EDGE,"E14.118.9"),sQuery(id+"F0.wireOp",EDGE,"E14.119.0"),sQuery(id+"F0.wireOp",EDGE,"E14.119.1"),sQuery(id+"F0.wireOp",EDGE,"E14.119.2"),sQuery(id+"F0.wireOp",EDGE,"E14.119.3"),sQuery(id+"F0.wireOp",EDGE,"E14.119.4"),sQuery(id+"F0.wireOp",EDGE,"E14.119.5"),sQuery(id+"F0.wireOp",EDGE,"E14.119.6"),sQuery(id+"F0.wireOp",EDGE,"E14.119.7"),sQuery(id+"F0.wireOp",EDGE,"E14.119.8"),sQuery(id+"F0.wireOp",EDGE,"E14.119.9"),sQuery(id+"F0.wireOp",EDGE,"E15.trimOffspring"),sQuery(id+"F0.wireOp",EDGE,"E16.trimOffspring"),sQuery(id+"F0.wireOp",EDGE,"E17.trimOffspring"),sQuery(id+"F0.wireOp",EDGE,"E18.trimOffspring"),sQuery(id+"F0.wireOp",EDGE,"E19.trimOffspring"),sQuery(id+"F0.wireOp",EDGE,"E20.trimOffspring"),sQuery(id+"F0.wireOp",EDGE,"E21.trimOffspring"),sQuery(id+"F0.wireOp",EDGE,"E22.trimOffspring"),sQuery(id+"F0.wireOp",EDGE,"E23.trimOffspring"),sQuery(id+"F0.wireOp",EDGE,"E24.trimOffspring"),sQuery(id+"F0.wireOp",EDGE,"E25.trimOffspring"),sQuery(id+"F0.wireOp",EDGE,"E26.trimOffspring"),sQuery(id+"F0.wireOp",EDGE,"E27.trimOffspring"),sQuery(id+"F0.wireOp",EDGE,"E28.trimOffspring"),sQuery(id+"F0.wireOp",EDGE,"E29.trimOffspring"),sQuery(id+"F0.wireOp",EDGE,"E30.trimOffspring"),sQuery(id+"F0.wireOp",EDGE,"E31.trimOffspring"),sQuery(id+"F0.wireOp",EDGE,"E32.trimOffspring"),sQuery(id+"F0.wireOp",EDGE,"E33.trimOffspring"),sQuery(id+"F0.wireOp",EDGE,"E34.trimOffspring"),sQuery(id+"F0.wireOp",EDGE,"E35.trimOffspring"),sQuery(id+"F0.wireOp",EDGE,"E36.trimOffspring"),sQuery(id+"F0.wireOp",EDGE,"E37.trimOffspring"),sQuery(id+"F0.wireOp",EDGE,"E38.trimOffspring"),sQuery(id+"F0.wireOp",EDGE,"E39.trimOffspring"),sQuery(id+"F0.wireOp",EDGE,"E40.trimOffspring"),sQuery(id+"F0.wireOp",EDGE,"E41.trimOffspring"),sQuery(id+"F0.wireOp",EDGE,"E42.trimOffspring"),sQuery(id+"F0.wireOp",EDGE,"E43.trimOffspring"),sQuery(id+"F0.wireOp",EDGE,"E44.trimOffspring"),sQuery(id+"F0.wireOp",EDGE,"E45.trimOffspring"),sQuery(id+"F0.wireOp",EDGE,"E46.trimOffspring"),sQuery(id+"F0.wireOp",EDGE,"E47.trimOffspring"),sQuery(id+"F0.wireOp",EDGE,"E48.trimOffspring"),sQuery(id+"F0.wireOp",EDGE,"E49.trimOffspring"),sQuery(id+"F0.wireOp",EDGE,"E73.1.0"),sQuery(id+"F0.wireOp",EDGE,"E73.1.1"),sQuery(id+"F0.wireOp",EDGE,"E73.2.0"),sQuery(id+"F0.wireOp",EDGE,"E73.2.1"),sQuery(id+"F0.wireOp",EDGE,"E74.3.3.0"),sQuery(id+"F0.wireOp",EDGE,"E74.4.3.0"),sQuery(id+"F0.wireOp",EDGE,"E74.3.4.0"),sQuery(id+"F0.wireOp",EDGE,"E74.4.4.0"),sQuery(id+"F0.wireOp",EDGE,"E74.3.5.0"),sQuery(id+"F0.wireOp",EDGE,"E74.4.5.0"),sQuery(id+"F0.wireOp",EDGE,"E74.3.6.0"),sQuery(id+"F0.wireOp",EDGE,"E74.4.6.0"),sQuery(id+"F0.wireOp",EDGE,"E74.3.7.0"),sQuery(id+"F0.wireOp",EDGE,"E74.4.7.0"),sQuery(id+"F0.wireOp",EDGE,"E74.3.8.0"),sQuery(id+"F0.wireOp",EDGE,"E74.4.8.0"),sQuery(id+"F0.wireOp",EDGE,"E74.3.9.0"),sQuery(id+"F0.wireOp",EDGE,"E74.4.9.0"),sQuery(id+"F0.wireOp",EDGE,"E74.3.10.0"),sQuery(id+"F0.wireOp",EDGE,"E74.4.10.0"),sQuery(id+"F0.wireOp",EDGE,"E74.3.11.0"),sQuery(id+"F0.wireOp",EDGE,"E74.4.11.0"),sQuery(id+"F0.wireOp",EDGE,"E74.3.12.0"),sQuery(id+"F0.wireOp",EDGE,"E74.4.12.0"),sQuery(id+"F0.wireOp",EDGE,"E74.3.13.0"),sQuery(id+"F0.wireOp",EDGE,"E74.4.13.0"),sQuery(id+"F0.wireOp",EDGE,"E74.3.14.0"),sQuery(id+"F0.wireOp",EDGE,"E74.4.14.0"),sQuery(id+"F0.wireOp",EDGE,"E74.3.15.0"),sQuery(id+"F0.wireOp",EDGE,"E74.4.15.0"),sQuery(id+"F0.wireOp",EDGE,"E74.3.16.0"),sQuery(id+"F0.wireOp",EDGE,"E74.4.16.0"),sQuery(id+"F0.wireOp",EDGE,"E74.3.17.0"),sQuery(id+"F0.wireOp",EDGE,"E74.4.17.0"),sQuery(id+"F0.wireOp",EDGE,"E74.3.18.0"),sQuery(id+"F0.wireOp",EDGE,"E74.4.18.0"),sQuery(id+"F0.wireOp",EDGE,"E74.3.19.0"),sQuery(id+"F0.wireOp",EDGE,"E74.4.19.0"),sQuery(id+"F0.wireOp",EDGE,"E74.3.20.0"),sQuery(id+"F0.wireOp",EDGE,"E74.4.20.0"),sQuery(id+"F0.wireOp",EDGE,"E74.3.21.0"),sQuery(id+"F0.wireOp",EDGE,"E74.4.21.0"),sQuery(id+"F0.wireOp",EDGE,"E74.3.22.0"),sQuery(id+"F0.wireOp",EDGE,"E74.4.22.0"),sQuery(id+"F0.wireOp",EDGE,"E74.3.23.0"),sQuery(id+"F0.wireOp",EDGE,"E74.4.23.0"),sQuery(id+"F0.wireOp",EDGE,"E74.3.24.0"),sQuery(id+"F0.wireOp",EDGE,"E74.4.24.0"),sQuery(id+"F0.wireOp",EDGE,"E74.3.25.0"),sQuery(id+"F0.wireOp",EDGE,"E74.4.25.0"),sQuery(id+"F0.wireOp",EDGE,"E74.3.26.0"),sQuery(id+"F0.wireOp",EDGE,"E74.4.26.0"),sQuery(id+"F0.wireOp",EDGE,"E74.3.27.0"),sQuery(id+"F0.wireOp",EDGE,"E74.4.27.0"),sQuery(id+"F0.wireOp",EDGE,"E74.3.28.0"),sQuery(id+"F0.wireOp",EDGE,"E74.4.28.0"),sQuery(id+"F0.wireOp",EDGE,"E74.3.29.0"),sQuery(id+"F0.wireOp",EDGE,"E74.4.29.0"),sQuery(id+"F0.wireOp",EDGE,"E74.3.30.0"),sQuery(id+"F0.wireOp",EDGE,"E74.4.30.0"),sQuery(id+"F0.wireOp",EDGE,"E74.3.31.0"),sQuery(id+"F0.wireOp",EDGE,"E74.4.31.0"),sQuery(id+"F0.wireOp",EDGE,"E74.3.32.0"),sQuery(id+"F0.wireOp",EDGE,"E74.4.32.0"),sQuery(id+"F0.wireOp",EDGE,"E74.3.33.0"),sQuery(id+"F0.wireOp",EDGE,"E74.4.33.0"),sQuery(id+"F0.wireOp",EDGE,"E74.3.34.0"),sQuery(id+"F0.wireOp",EDGE,"E74.4.34.0"),sQuery(id+"F0.wireOp",EDGE,"E74.3.35.0"),sQuery(id+"F0.wireOp",EDGE,"E74.4.35.0"),sQuery(id+"F0.wireOp",EDGE,"E74.3.36.0"),sQuery(id+"F0.wireOp",EDGE,"E74.4.36.0"),sQuery(id+"F0.wireOp",EDGE,"E74.3.37.0"),sQuery(id+"F0.wireOp",EDGE,"E74.4.37.0"),sQuery(id+"F0.wireOp",EDGE,"E74.3.38.0"),sQuery(id+"F0.wireOp",EDGE,"E74.4.38.0"),sQuery(id+"F0.wireOp",EDGE,"E74.3.39.0"),sQuery(id+"F0.wireOp",EDGE,"E74.4.39.0"),sQuery(id+"F0.wireOp",EDGE,"E74.3.40.0"),sQuery(id+"F0.wireOp",EDGE,"E74.4.40.0"),sQuery(id+"F0.wireOp",EDGE,"E74.3.41.0"),sQuery(id+"F0.wireOp",EDGE,"E74.4.41.0"),sQuery(id+"F0.wireOp",EDGE,"E74.3.42.0"),sQuery(id+"F0.wireOp",EDGE,"E74.4.42.0"),sQuery(id+"F0.wireOp",EDGE,"E74.3.43.0"),sQuery(id+"F0.wireOp",EDGE,"E74.4.43.0"),sQuery(id+"F0.wireOp",EDGE,"E74.3.44.0"),sQuery(id+"F0.wireOp",EDGE,"E74.4.44.0"),sQuery(id+"F0.wireOp",EDGE,"E74.3.45.0"),sQuery(id+"F0.wireOp",EDGE,"E74.4.45.0"),sQuery(id+"F0.wireOp",EDGE,"E74.3.46.0"),sQuery(id+"F0.wireOp",EDGE,"E74.4.46.0"),sQuery(id+"F0.wireOp",EDGE,"E74.3.47.0"),sQuery(id+"F0.wireOp",EDGE,"E74.4.47.0"),sQuery(id+"F0.wireOp",EDGE,"E74.3.48.0"),sQuery(id+"F0.wireOp",EDGE,"E74.4.48.0"),sQuery(id+"F0.wireOp",EDGE,"E74.3.49.0"),sQuery(id+"F0.wireOp",EDGE,"E74.4.49.0"),sQuery(id+"F0.wireOp",EDGE,"E74.3.50.0"),sQuery(id+"F0.wireOp",EDGE,"E74.4.50.0"),sQuery(id+"F0.wireOp",EDGE,"E74.3.51.0"),sQuery(id+"F0.wireOp",EDGE,"E74.4.51.0"),sQuery(id+"F0.wireOp",EDGE,"E74.3.52.0"),sQuery(id+"F0.wireOp",EDGE,"E74.4.52.0"),sQuery(id+"F0.wireOp",EDGE,"E74.3.53.0"),sQuery(id+"F0.wireOp",EDGE,"E74.4.53.0"),sQuery(id+"F0.wireOp",EDGE,"E74.3.54.0"),sQuery(id+"F0.wireOp",EDGE,"E74.4.54.0"),sQuery(id+"F0.wireOp",EDGE,"E74.3.55.0"),sQuery(id+"F0.wireOp",EDGE,"E74.4.55.0"),sQuery(id+"F0.wireOp",EDGE,"E74.3.56.0"),sQuery(id+"F0.wireOp",EDGE,"E74.4.56.0"),sQuery(id+"F0.wireOp",EDGE,"E74.3.57.0"),sQuery(id+"F0.wireOp",EDGE,"E74.4.57.0"),sQuery(id+"F0.wireOp",EDGE,"E74.3.58.0"),sQuery(id+"F0.wireOp",EDGE,"E74.4.58.0"),sQuery(id+"F0.wireOp",EDGE,"E74.3.59.0"),sQuery(id+"F0.wireOp",EDGE,"E74.4.59.0"),sQuery(id+"F0.wireOp",EDGE,"E74.3.60.0"),sQuery(id+"F0.wireOp",EDGE,"E74.4.60.0"),sQuery(id+"F0.wireOp",EDGE,"E74.3.61.0"),sQuery(id+"F0.wireOp",EDGE,"E74.4.61.0"),sQuery(id+"F0.wireOp",EDGE,"E74.3.62.0"),sQuery(id+"F0.wireOp",EDGE,"E74.4.62.0"),sQuery(id+"F0.wireOp",EDGE,"E74.3.63.0"),sQuery(id+"F0.wireOp",EDGE,"E74.4.63.0"),sQuery(id+"F0.wireOp",EDGE,"E74.3.64.0"),sQuery(id+"F0.wireOp",EDGE,"E74.4.64.0"),sQuery(id+"F0.wireOp",EDGE,"E74.3.65.0"),sQuery(id+"F0.wireOp",EDGE,"E74.4.65.0"),sQuery(id+"F0.wireOp",EDGE,"E74.3.66.0"),sQuery(id+"F0.wireOp",EDGE,"E74.4.66.0"),sQuery(id+"F0.wireOp",EDGE,"E74.3.67.0"),sQuery(id+"F0.wireOp",EDGE,"E74.4.67.0"),sQuery(id+"F0.wireOp",EDGE,"E74.3.68.0"),sQuery(id+"F0.wireOp",EDGE,"E74.4.68.0"),sQuery(id+"F0.wireOp",EDGE,"E74.3.69.0"),sQuery(id+"F0.wireOp",EDGE,"E74.4.69.0"),sQuery(id+"F0.wireOp",EDGE,"E74.3.70.0"),sQuery(id+"F0.wireOp",EDGE,"E74.4.70.0"),sQuery(id+"F0.wireOp",EDGE,"E74.3.71.0"),sQuery(id+"F0.wireOp",EDGE,"E74.4.71.0"),sQuery(id+"F0.wireOp",EDGE,"E74.3.72.0"),sQuery(id+"F0.wireOp",EDGE,"E74.4.72.0"),sQuery(id+"F0.wireOp",EDGE,"E74.3.73.0"),sQuery(id+"F0.wireOp",EDGE,"E74.4.73.0"),sQuery(id+"F0.wireOp",EDGE,"E74.3.74.0"),sQuery(id+"F0.wireOp",EDGE,"E74.4.74.0"),sQuery(id+"F0.wireOp",EDGE,"E74.3.75.0"),sQuery(id+"F0.wireOp",EDGE,"E74.4.75.0"),sQuery(id+"F0.wireOp",EDGE,"E74.3.76.0"),sQuery(id+"F0.wireOp",EDGE,"E74.4.76.0"),sQuery(id+"F0.wireOp",EDGE,"E74.3.77.0"),sQuery(id+"F0.wireOp",EDGE,"E74.4.77.0"),sQuery(id+"F0.wireOp",EDGE,"E74.3.78.0"),sQuery(id+"F0.wireOp",EDGE,"E74.4.78.0"),sQuery(id+"F0.wireOp",EDGE,"E74.3.79.0"),sQuery(id+"F0.wireOp",EDGE,"E74.4.79.0"),sQuery(id+"F0.wireOp",EDGE,"E74.3.80.0"),sQuery(id+"F0.wireOp",EDGE,"E74.4.80.0"),sQuery(id+"F0.wireOp",EDGE,"E74.3.81.0"),sQuery(id+"F0.wireOp",EDGE,"E74.4.81.0"),sQuery(id+"F0.wireOp",EDGE,"E74.3.82.0"),sQuery(id+"F0.wireOp",EDGE,"E74.4.82.0"),sQuery(id+"F0.wireOp",EDGE,"E74.3.83.0"),sQuery(id+"F0.wireOp",EDGE,"E74.4.83.0"),sQuery(id+"F0.wireOp",EDGE,"E74.3.84.0"),sQuery(id+"F0.wireOp",EDGE,"E74.4.84.0"),sQuery(id+"F0.wireOp",EDGE,"E74.3.85.0"),sQuery(id+"F0.wireOp",EDGE,"E74.4.85.0"),sQuery(id+"F0.wireOp",EDGE,"E74.3.86.0"),sQuery(id+"F0.wireOp",EDGE,"E74.4.86.0"),sQuery(id+"F0.wireOp",EDGE,"E74.3.87.0"),sQuery(id+"F0.wireOp",EDGE,"E74.4.87.0"),sQuery(id+"F0.wireOp",EDGE,"E74.3.88.0"),sQuery(id+"F0.wireOp",EDGE,"E74.4.88.0"),sQuery(id+"F0.wireOp",EDGE,"E74.3.89.0"),sQuery(id+"F0.wireOp",EDGE,"E74.4.89.0"),sQuery(id+"F0.wireOp",EDGE,"E74.3.90.0"),sQuery(id+"F0.wireOp",EDGE,"E74.4.90.0"),sQuery(id+"F0.wireOp",EDGE,"E74.3.91.0"),sQuery(id+"F0.wireOp",EDGE,"E74.4.91.0"),sQuery(id+"F0.wireOp",EDGE,"E74.3.92.0"),sQuery(id+"F0.wireOp",EDGE,"E74.4.92.0"),sQuery(id+"F0.wireOp",EDGE,"E74.3.93.0"),sQuery(id+"F0.wireOp",EDGE,"E74.4.93.0"),sQuery(id+"F0.wireOp",EDGE,"E74.3.94.0"),sQuery(id+"F0.wireOp",EDGE,"E74.4.94.0"),sQuery(id+"F0.wireOp",EDGE,"E74.3.95.0"),sQuery(id+"F0.wireOp",EDGE,"E74.4.95.0"),sQuery(id+"F0.wireOp",EDGE,"E74.3.96.0"),sQuery(id+"F0.wireOp",EDGE,"E74.4.96.0"),sQuery(id+"F0.wireOp",EDGE,"E74.3.97.0"),sQuery(id+"F0.wireOp",EDGE,"E74.4.97.0"),sQuery(id+"F0.wireOp",EDGE,"E74.3.98.0"),sQuery(id+"F0.wireOp",EDGE,"E74.4.98.0"),sQuery(id+"F0.wireOp",EDGE,"E74.3.99.0"),sQuery(id+"F0.wireOp",EDGE,"E74.4.99.0"),sQuery(id+"F0.wireOp",EDGE,"E74.3.100.0"),sQuery(id+"F0.wireOp",EDGE,"E74.4.100.0"),sQuery(id+"F0.wireOp",EDGE,"E74.3.101.0"),sQuery(id+"F0.wireOp",EDGE,"E74.4.101.0"),sQuery(id+"F0.wireOp",EDGE,"E74.3.102.0"),sQuery(id+"F0.wireOp",EDGE,"E74.4.102.0"),sQuery(id+"F0.wireOp",EDGE,"E74.3.103.0"),sQuery(id+"F0.wireOp",EDGE,"E74.4.103.0"),sQuery(id+"F0.wireOp",EDGE,"E74.3.104.0"),sQuery(id+"F0.wireOp",EDGE,"E74.4.104.0"),sQuery(id+"F0.wireOp",EDGE,"E74.3.105.0"),sQuery(id+"F0.wireOp",EDGE,"E74.4.105.0"),sQuery(id+"F0.wireOp",EDGE,"E74.3.106.0"),sQuery(id+"F0.wireOp",EDGE,"E74.4.106.0"),sQuery(id+"F0.wireOp",EDGE,"E74.3.107.0"),sQuery(id+"F0.wireOp",EDGE,"E74.4.107.0"),sQuery(id+"F0.wireOp",EDGE,"E74.3.108.0"),sQuery(id+"F0.wireOp",EDGE,"E74.4.108.0"),sQuery(id+"F0.wireOp",EDGE,"E74.3.109.0"),sQuery(id+"F0.wireOp",EDGE,"E74.4.109.0"),sQuery(id+"F0.wireOp",EDGE,"E74.3.110.0"),sQuery(id+"F0.wireOp",EDGE,"E74.4.110.0"),sQuery(id+"F0.wireOp",EDGE,"E74.3.111.0"),sQuery(id+"F0.wireOp",EDGE,"E74.4.111.0"),sQuery(id+"F0.wireOp",EDGE,"E74.3.112.0"),sQuery(id+"F0.wireOp",EDGE,"E74.4.112.0"),sQuery(id+"F0.wireOp",EDGE,"E74.3.113.0"),sQuery(id+"F0.wireOp",EDGE,"E74.4.113.0"),sQuery(id+"F0.wireOp",EDGE,"E74.3.114.0"),sQuery(id+"F0.wireOp",EDGE,"E74.4.114.0"),sQuery(id+"F0.wireOp",EDGE,"E74.3.115.0"),sQuery(id+"F0.wireOp",EDGE,"E74.4.115.0"),sQuery(id+"F0.wireOp",EDGE,"E74.3.116.0"),sQuery(id+"F0.wireOp",EDGE,"E74.4.116.0"),sQuery(id+"F0.wireOp",EDGE,"E74.3.117.0"),sQuery(id+"F0.wireOp",EDGE,"E74.4.117.0"),sQuery(id+"F0.wireOp",EDGE,"E74.3.118.0"),sQuery(id+"F0.wireOp",EDGE,"E74.4.118.0"),sQuery(id+"F0.wireOp",EDGE,"E74.3.119.0"),sQuery(id+"F0.wireOp",EDGE,"E74.4.119.0"),sQuery(id+"F0.wireOp",EDGE,"E75.trimOffspring"),sQuery(id+"F0.wireOp",EDGE,"E76.trimOffspring"),sQuery(id+"F0.wireOp",EDGE,"E77.trimOffspring"),sQuery(id+"F0.wireOp",EDGE,"E78.trimOffspring"),sQuery(id+"F0.wireOp",EDGE,"E79.trimOffspring"),sQuery(id+"F0.wireOp",EDGE,"E80.trimOffspring"),sQuery(id+"F0.wireOp",EDGE,"E81.trimOffspring"),sQuery(id+"F0.wireOp",EDGE,"E82.trimOffspring"),sQuery(id+"F0.wireOp",EDGE,"E83.trimOffspring"),sQuery(id+"F0.wireOp",EDGE,"E84.trimOffspring"),sQuery(id+"F0.wireOp",EDGE,"E85.trimOffspring"),sQuery(id+"F0.wireOp",EDGE,"E86.trimOffspring"),sQuery(id+"F0.wireOp",EDGE,"E87.trimOffspring"),sQuery(id+"F0.wireOp",EDGE,"E88.trimOffspring"),sQuery(id+"F0.wireOp",EDGE,"E89.trimOffspring"),sQuery(id+"F0.wireOp",EDGE,"E90.trimOffspring"),sQuery(id+"F0.wireOp",EDGE,"E91.trimOffspring"),sQuery(id+"F0.wireOp",EDGE,"E92.trimOffspring"),sQuery(id+"F0.wireOp",EDGE,"E93.trimOffspring"),sQuery(id+"F0.wireOp",EDGE,"E94.trimOffspring"),sQuery(id+"F0.wireOp",EDGE,"E95.trimOffspring"),sQuery(id+"F0.wireOp",EDGE,"E96.trimOffspring"),sQuery(id+"F0.wireOp",EDGE,"E97.trimOffspring"),sQuery(id+"F0.wireOp",EDGE,"E98.trimOffspring"),sQuery(id+"F0.wireOp",EDGE,"E99.trimOffspring"),sQuery(id+"F0.wireOp",EDGE,"E100.trimOffspring"),sQuery(id+"F0.wireOp",EDGE,"E101.trimOffspring"),sQuery(id+"F0.wireOp",EDGE,"E102.trimOffspring"),sQuery(id+"F0.wireOp",EDGE,"E103.trimOffspring"),sQuery(id+"F0.wireOp",EDGE,"E104.trimOffspring"),sQuery(id+"F0.wireOp",EDGE,"E105.trimOffspring"),sQuery(id+"F0.wireOp",EDGE,"E106.trimOffspring"),sQuery(id+"F0.wireOp",EDGE,"E107.trimOffspring"),sQuery(id+"F0.wireOp",EDGE,"E108.trimOffspring"),sQuery(id+"F0.wireOp",EDGE,"E109.trimOffspring"),sQuery(id+"F0.wireOp",EDGE,"E110.trimOffspring"),sQuery(id+"F0.wireOp",EDGE,"E111.trimOffspring"),sQuery(id+"F0.wireOp",EDGE,"E112.trimOffspring"),sQuery(id+"F0.wireOp",EDGE,"E113.trimOffspring"),sQuery(id+"F0.wireOp",EDGE,"E114.trimOffspring"),sQuery(id+"F0.wireOp",EDGE,"E115.trimOffspring"),sQuery(id+"F0.wireOp",EDGE,"E116.trimOffspring"),sQuery(id+"F0.wireOp",EDGE,"E117.trimOffspring"),sQuery(id+"F0.wireOp",EDGE,"E118.trimOffspring"),sQuery(id+"F0.wireOp",EDGE,"E119.trimOffspring"),sQuery(id+"F0.wireOp",EDGE,"E120.trimOffspring"),sQuery(id+"F0.wireOp",EDGE,"E121.trimOffspring"),sQuery(id+"F0.wireOp",EDGE,"E122.trimOffspring"),sQuery(id+"F0.wireOp",EDGE,"E123.trimOffspring"),sQuery(id+"F0.wireOp",EDGE,"E124.trimOffspring"),sQuery(id+"F0.wireOp",EDGE,"E125.trimOffspring"),sQuery(id+"F0.wireOp",EDGE,"E126.trimOffspring"),sQuery(id+"F0.wireOp",EDGE,"E127.trimOffspring"),sQuery(id+"F0.wireOp",EDGE,"E128.trimOffspring"),sQuery(id+"F0.wireOp",EDGE,"E129.trimOffspring"),sQuery(id+"F0.wireOp",EDGE,"E130.trimOffspring"),sQuery(id+"F0.wireOp",EDGE,"E131.trimOffspring"),sQuery(id+"F0.wireOp",EDGE,"E132.trimOffspring"),sQuery(id+"F0.wireOp",EDGE,"E133.trimOffspring"),sQuery(id+"F0.wireOp",EDGE,"E134.trimOffspring"),sQuery(id+"F0.wireOp",EDGE,"E135.trimOffspring"),sQuery(id+"F0.wireOp",EDGE,"E136.trimOffspring"),sQuery(id+"F0.wireOp",EDGE,"E137.trimOffspring"),sQuery(id+"F0.wireOp",EDGE,"E138.trimOffspring"),sQuery(id+"F0.wireOp",EDGE,"E139.trimOffspring"),sQuery(id+"F0.wireOp",EDGE,"E140.trimOffspring"),sQuery(id+"F0.wireOp",EDGE,"E141.trimOffspring"),sQuery(id+"F0.wireOp",EDGE,"E142.trimOffspring"),sQuery(id+"F0.wireOp",EDGE,"E143.trimOffspring"),sQuery(id+"F0.wireOp",EDGE,"E144.trimOffspring"),sQuery(id+"F0.wireOp",EDGE,"E145.trimOffspring"),sQuery(id+"F0.wireOp",EDGE,"E146.trimOffspring"),sQuery(id+"F0.wireOp",EDGE,"E147.trimOffspring"),sQuery(id+"F0.wireOp",EDGE,"E148.trimOffspring"),sQuery(id+"F0.wireOp",EDGE,"E149.trimOffspring"),sQuery(id+"F0.wireOp",EDGE,"E150.trimOffspring"),sQuery(id+"F0.wireOp",EDGE,"E151.trimOffspring"),sQuery(id+"F0.wireOp",EDGE,"E152.trimOffspring"),sQuery(id+"F0.wireOp",EDGE,"E153.trimOffspring"),sQuery(id+"F0.wireOp",EDGE,"E154.trimOffspring"),sQuery(id+"F0.wireOp",EDGE,"E155.trimOffspring"),sQuery(id+"F0.wireOp",EDGE,"E156.trimOffspring"),sQuery(id+"F0.wireOp",EDGE,"E157.trimOffspring")])],"isStart":false});
            var sketch = newSketch(context, id + "F2", { "sketchPlane" : qUnion([Q0])});
            skCircle(sketch, "E158", {"center": v(0, 0) * mm, "radius": 3.94 * mm});
            skSolve(sketch);
        }
        {
            var Q0;
            Q0=makeQuery(id+"F2.imprint","IMPRINT",FACE,{"disambiguationData":[TD([[makeQuery(id+"F2.imprint","IMPRINT",EDGE,{"derivedFrom":sQuery(id+"F2.wireOp",EDGE,"E158")}),1.0]])]});
            extrude(context, id + "F3", {"entities" : qUnion([Q0]), "operationType" : NewBodyOperationType.REMOVE, "oppositeDirection" : true, "depth" : 25.4 * mm});
        }
        {
            var Q0;
            Q0=makeQuery(id+"F1.opExtrude","CAP_FACE",FACE,{"disambiguationData":[OSD([sQuery(id+"F0.wireOp",EDGE,"E0"),sQuery(id+"F0.wireOp",EDGE,"E1.trimOffspring"),sQuery(id+"F0.wireOp",EDGE,"E2"),sQuery(id+"F0.wireOp",EDGE,"E3"),sQuery(id+"F0.wireOp",EDGE,"E4.MirrorCS"),sQuery(id+"F0.wireOp",EDGE,"E5.MirrorCS"),sQuery(id+"F0.wireOp",EDGE,"E6.MirrorCS"),sQuery(id+"F0.wireOp",EDGE,"E8.filletArc"),sQuery(id+"F0.wireOp",EDGE,"E9.filletArc"),sQuery(id+"F0.wireOp",EDGE,"E10.filletArc"),sQuery(id+"F0.wireOp",EDGE,"E11.filletArc"),sQuery(id+"F0.wireOp",EDGE,"E12.filletArc"),sQuery(id+"F0.wireOp",EDGE,"E13.filletArc"),sQuery(id+"F0.wireOp",EDGE,"E14.1.0"),sQuery(id+"F0.wireOp",EDGE,"E14.1.1"),sQuery(id+"F0.wireOp",EDGE,"E14.1.2"),sQuery(id+"F0.wireOp",EDGE,"E14.1.3"),sQuery(id+"F0.wireOp",EDGE,"E14.1.4"),sQuery(id+"F0.wireOp",EDGE,"E14.1.5"),sQuery(id+"F0.wireOp",EDGE,"E14.1.6"),sQuery(id+"F0.wireOp",EDGE,"E14.1.7"),sQuery(id+"F0.wireOp",EDGE,"E14.1.8"),sQuery(id+"F0.wireOp",EDGE,"E14.1.9"),sQuery(id+"F0.wireOp",EDGE,"E14.2.0"),sQuery(id+"F0.wireOp",EDGE,"E14.2.1"),sQuery(id+"F0.wireOp",EDGE,"E14.2.2"),sQuery(id+"F0.wireOp",EDGE,"E14.2.3"),sQuery(id+"F0.wireOp",EDGE,"E14.2.4"),sQuery(id+"F0.wireOp",EDGE,"E14.2.5"),sQuery(id+"F0.wireOp",EDGE,"E14.2.6"),sQuery(id+"F0.wireOp",EDGE,"E14.2.7"),sQuery(id+"F0.wireOp",EDGE,"E14.2.8"),sQuery(id+"F0.wireOp",EDGE,"E14.2.9"),sQuery(id+"F0.wireOp",EDGE,"E14.3.0"),sQuery(id+"F0.wireOp",EDGE,"E14.3.1"),sQuery(id+"F0.wireOp",EDGE,"E14.3.2"),sQuery(id+"F0.wireOp",EDGE,"E14.3.3"),sQuery(id+"F0.wireOp",EDGE,"E14.3.4"),sQuery(id+"F0.wireOp",EDGE,"E14.3.5"),sQuery(id+"F0.wireOp",EDGE,"E14.3.6"),sQuery(id+"F0.wireOp",EDGE,"E14.3.7"),sQuery(id+"F0.wireOp",EDGE,"E14.3.8"),sQuery(id+"F0.wireOp",EDGE,"E14.3.9"),sQuery(id+"F0.wireOp",EDGE,"E14.4.0"),sQuery(id+"F0.wireOp",EDGE,"E14.4.1"),sQuery(id+"F0.wireOp",EDGE,"E14.4.2"),sQuery(id+"F0.wireOp",EDGE,"E14.4.3"),sQuery(id+"F0.wireOp",EDGE,"E14.4.4"),sQuery(id+"F0.wireOp",EDGE,"E14.4.5"),sQuery(id+"F0.wireOp",EDGE,"E14.4.6"),sQuery(id+"F0.wireOp",EDGE,"E14.4.7"),sQuery(id+"F0.wireOp",EDGE,"E14.4.8"),sQuery(id+"F0.wireOp",EDGE,"E14.4.9"),sQuery(id+"F0.wireOp",EDGE,"E14.5.0"),sQuery(id+"F0.wireOp",EDGE,"E14.5.1"),sQuery(id+"F0.wireOp",EDGE,"E14.5.2"),sQuery(id+"F0.wireOp",EDGE,"E14.5.3"),sQuery(id+"F0.wireOp",EDGE,"E14.5.4"),sQuery(id+"F0.wireOp",EDGE,"E14.5.5"),sQuery(id+"F0.wireOp",EDGE,"E14.5.6"),sQuery(id+"F0.wireOp",EDGE,"E14.5.7"),sQuery(id+"F0.wireOp",EDGE,"E14.5.8"),sQuery(id+"F0.wireOp",EDGE,"E14.5.9"),sQuery(id+"F0.wireOp",EDGE,"E14.6.0"),sQuery(id+"F0.wireOp",EDGE,"E14.6.1"),sQuery(id+"F0.wireOp",EDGE,"E14.6.2"),sQuery(id+"F0.wireOp",EDGE,"E14.6.3"),sQuery(id+"F0.wireOp",EDGE,"E14.6.4"),sQuery(id+"F0.wireOp",EDGE,"E14.6.5"),sQuery(id+"F0.wireOp",EDGE,"E14.6.6"),sQuery(id+"F0.wireOp",EDGE,"E14.6.7"),sQuery(id+"F0.wireOp",EDGE,"E14.6.8"),sQuery(id+"F0.wireOp",EDGE,"E14.6.9"),sQuery(id+"F0.wireOp",EDGE,"E14.7.0"),sQuery(id+"F0.wireOp",EDGE,"E14.7.1"),sQuery(id+"F0.wireOp",EDGE,"E14.7.2"),sQuery(id+"F0.wireOp",EDGE,"E14.7.3"),sQuery(id+"F0.wireOp",EDGE,"E14.7.4"),sQuery(id+"F0.wireOp",EDGE,"E14.7.5"),sQuery(id+"F0.wireOp",EDGE,"E14.7.6"),sQuery(id+"F0.wireOp",EDGE,"E14.7.7"),sQuery(id+"F0.wireOp",EDGE,"E14.7.8"),sQuery(id+"F0.wireOp",EDGE,"E14.7.9"),sQuery(id+"F0.wireOp",EDGE,"E14.8.0"),sQuery(id+"F0.wireOp",EDGE,"E14.8.1"),sQuery(id+"F0.wireOp",EDGE,"E14.8.2"),sQuery(id+"F0.wireOp",EDGE,"E14.8.3"),sQuery(id+"F0.wireOp",EDGE,"E14.8.4"),sQuery(id+"F0.wireOp",EDGE,"E14.8.5"),sQuery(id+"F0.wireOp",EDGE,"E14.8.6"),sQuery(id+"F0.wireOp",EDGE,"E14.8.7"),sQuery(id+"F0.wireOp",EDGE,"E14.8.8"),sQuery(id+"F0.wireOp",EDGE,"E14.8.9"),sQuery(id+"F0.wireOp",EDGE,"E14.9.0"),sQuery(id+"F0.wireOp",EDGE,"E14.9.1"),sQuery(id+"F0.wireOp",EDGE,"E14.9.2"),sQuery(id+"F0.wireOp",EDGE,"E14.9.3"),sQuery(id+"F0.wireOp",EDGE,"E14.9.4"),sQuery(id+"F0.wireOp",EDGE,"E14.9.5"),sQuery(id+"F0.wireOp",EDGE,"E14.9.6"),sQuery(id+"F0.wireOp",EDGE,"E14.9.7"),sQuery(id+"F0.wireOp",EDGE,"E14.9.8"),sQuery(id+"F0.wireOp",EDGE,"E14.9.9"),sQuery(id+"F0.wireOp",EDGE,"E14.10.0"),sQuery(id+"F0.wireOp",EDGE,"E14.10.1"),sQuery(id+"F0.wireOp",EDGE,"E14.10.2"),sQuery(id+"F0.wireOp",EDGE,"E14.10.3"),sQuery(id+"F0.wireOp",EDGE,"E14.10.4"),sQuery(id+"F0.wireOp",EDGE,"E14.10.5"),sQuery(id+"F0.wireOp",EDGE,"E14.10.6"),sQuery(id+"F0.wireOp",EDGE,"E14.10.7"),sQuery(id+"F0.wireOp",EDGE,"E14.10.8"),sQuery(id+"F0.wireOp",EDGE,"E14.10.9"),sQuery(id+"F0.wireOp",EDGE,"E14.11.0"),sQuery(id+"F0.wireOp",EDGE,"E14.11.1"),sQuery(id+"F0.wireOp",EDGE,"E14.11.2"),sQuery(id+"F0.wireOp",EDGE,"E14.11.3"),sQuery(id+"F0.wireOp",EDGE,"E14.11.4"),sQuery(id+"F0.wireOp",EDGE,"E14.11.5"),sQuery(id+"F0.wireOp",EDGE,"E14.11.6"),sQuery(id+"F0.wireOp",EDGE,"E14.11.7"),sQuery(id+"F0.wireOp",EDGE,"E14.11.8"),sQuery(id+"F0.wireOp",EDGE,"E14.11.9"),sQuery(id+"F0.wireOp",EDGE,"E14.12.0"),sQuery(id+"F0.wireOp",EDGE,"E14.12.1"),sQuery(id+"F0.wireOp",EDGE,"E14.12.2"),sQuery(id+"F0.wireOp",EDGE,"E14.12.3"),sQuery(id+"F0.wireOp",EDGE,"E14.12.4"),sQuery(id+"F0.wireOp",EDGE,"E14.12.5"),sQuery(id+"F0.wireOp",EDGE,"E14.12.6"),sQuery(id+"F0.wireOp",EDGE,"E14.12.7"),sQuery(id+"F0.wireOp",EDGE,"E14.12.8"),sQuery(id+"F0.wireOp",EDGE,"E14.12.9"),sQuery(id+"F0.wireOp",EDGE,"E14.13.0"),sQuery(id+"F0.wireOp",EDGE,"E14.13.1"),sQuery(id+"F0.wireOp",EDGE,"E14.13.2"),sQuery(id+"F0.wireOp",EDGE,"E14.13.3"),sQuery(id+"F0.wireOp",EDGE,"E14.13.4"),sQuery(id+"F0.wireOp",EDGE,"E14.13.5"),sQuery(id+"F0.wireOp",EDGE,"E14.13.6"),sQuery(id+"F0.wireOp",EDGE,"E14.13.7"),sQuery(id+"F0.wireOp",EDGE,"E14.13.8"),sQuery(id+"F0.wireOp",EDGE,"E14.13.9"),sQuery(id+"F0.wireOp",EDGE,"E14.14.0"),sQuery(id+"F0.wireOp",EDGE,"E14.14.1"),sQuery(id+"F0.wireOp",EDGE,"E14.14.2"),sQuery(id+"F0.wireOp",EDGE,"E14.14.3"),sQuery(id+"F0.wireOp",EDGE,"E14.14.4"),sQuery(id+"F0.wireOp",EDGE,"E14.14.5"),sQuery(id+"F0.wireOp",EDGE,"E14.14.6"),sQuery(id+"F0.wireOp",EDGE,"E14.14.7"),sQuery(id+"F0.wireOp",EDGE,"E14.14.8"),sQuery(id+"F0.wireOp",EDGE,"E14.14.9"),sQuery(id+"F0.wireOp",EDGE,"E14.15.0"),sQuery(id+"F0.wireOp",EDGE,"E14.15.1"),sQuery(id+"F0.wireOp",EDGE,"E14.15.2"),sQuery(id+"F0.wireOp",EDGE,"E14.15.3"),sQuery(id+"F0.wireOp",EDGE,"E14.15.4"),sQuery(id+"F0.wireOp",EDGE,"E14.15.5"),sQuery(id+"F0.wireOp",EDGE,"E14.15.6"),sQuery(id+"F0.wireOp",EDGE,"E14.15.7"),sQuery(id+"F0.wireOp",EDGE,"E14.15.8"),sQuery(id+"F0.wireOp",EDGE,"E14.15.9"),sQuery(id+"F0.wireOp",EDGE,"E14.16.0"),sQuery(id+"F0.wireOp",EDGE,"E14.16.1"),sQuery(id+"F0.wireOp",EDGE,"E14.16.2"),sQuery(id+"F0.wireOp",EDGE,"E14.16.3"),sQuery(id+"F0.wireOp",EDGE,"E14.16.4"),sQuery(id+"F0.wireOp",EDGE,"E14.16.5"),sQuery(id+"F0.wireOp",EDGE,"E14.16.6"),sQuery(id+"F0.wireOp",EDGE,"E14.16.7"),sQuery(id+"F0.wireOp",EDGE,"E14.16.8"),sQuery(id+"F0.wireOp",EDGE,"E14.16.9"),sQuery(id+"F0.wireOp",EDGE,"E14.17.0"),sQuery(id+"F0.wireOp",EDGE,"E14.17.1"),sQuery(id+"F0.wireOp",EDGE,"E14.17.2"),sQuery(id+"F0.wireOp",EDGE,"E14.17.3"),sQuery(id+"F0.wireOp",EDGE,"E14.17.4"),sQuery(id+"F0.wireOp",EDGE,"E14.17.5"),sQuery(id+"F0.wireOp",EDGE,"E14.17.6"),sQuery(id+"F0.wireOp",EDGE,"E14.17.7"),sQuery(id+"F0.wireOp",EDGE,"E14.17.8"),sQuery(id+"F0.wireOp",EDGE,"E14.17.9"),sQuery(id+"F0.wireOp",EDGE,"E14.18.0"),sQuery(id+"F0.wireOp",EDGE,"E14.18.1"),sQuery(id+"F0.wireOp",EDGE,"E14.18.2"),sQuery(id+"F0.wireOp",EDGE,"E14.18.3"),sQuery(id+"F0.wireOp",EDGE,"E14.18.4"),sQuery(id+"F0.wireOp",EDGE,"E14.18.5"),sQuery(id+"F0.wireOp",EDGE,"E14.18.6"),sQuery(id+"F0.wireOp",EDGE,"E14.18.7"),sQuery(id+"F0.wireOp",EDGE,"E14.18.8"),sQuery(id+"F0.wireOp",EDGE,"E14.18.9"),sQuery(id+"F0.wireOp",EDGE,"E14.19.0"),sQuery(id+"F0.wireOp",EDGE,"E14.19.1"),sQuery(id+"F0.wireOp",EDGE,"E14.19.2"),sQuery(id+"F0.wireOp",EDGE,"E14.19.3"),sQuery(id+"F0.wireOp",EDGE,"E14.19.4"),sQuery(id+"F0.wireOp",EDGE,"E14.19.5"),sQuery(id+"F0.wireOp",EDGE,"E14.19.6"),sQuery(id+"F0.wireOp",EDGE,"E14.19.7"),sQuery(id+"F0.wireOp",EDGE,"E14.19.8"),sQuery(id+"F0.wireOp",EDGE,"E14.19.9"),sQuery(id+"F0.wireOp",EDGE,"E14.20.0"),sQuery(id+"F0.wireOp",EDGE,"E14.20.1"),sQuery(id+"F0.wireOp",EDGE,"E14.20.2"),sQuery(id+"F0.wireOp",EDGE,"E14.20.3"),sQuery(id+"F0.wireOp",EDGE,"E14.20.4"),sQuery(id+"F0.wireOp",EDGE,"E14.20.5"),sQuery(id+"F0.wireOp",EDGE,"E14.20.6"),sQuery(id+"F0.wireOp",EDGE,"E14.20.7"),sQuery(id+"F0.wireOp",EDGE,"E14.20.8"),sQuery(id+"F0.wireOp",EDGE,"E14.20.9"),sQuery(id+"F0.wireOp",EDGE,"E14.21.0"),sQuery(id+"F0.wireOp",EDGE,"E14.21.1"),sQuery(id+"F0.wireOp",EDGE,"E14.21.2"),sQuery(id+"F0.wireOp",EDGE,"E14.21.3"),sQuery(id+"F0.wireOp",EDGE,"E14.21.4"),sQuery(id+"F0.wireOp",EDGE,"E14.21.5"),sQuery(id+"F0.wireOp",EDGE,"E14.21.6"),sQuery(id+"F0.wireOp",EDGE,"E14.21.7"),sQuery(id+"F0.wireOp",EDGE,"E14.21.8"),sQuery(id+"F0.wireOp",EDGE,"E14.21.9"),sQuery(id+"F0.wireOp",EDGE,"E14.22.0"),sQuery(id+"F0.wireOp",EDGE,"E14.22.1"),sQuery(id+"F0.wireOp",EDGE,"E14.22.2"),sQuery(id+"F0.wireOp",EDGE,"E14.22.3"),sQuery(id+"F0.wireOp",EDGE,"E14.22.4"),sQuery(id+"F0.wireOp",EDGE,"E14.22.5"),sQuery(id+"F0.wireOp",EDGE,"E14.22.6"),sQuery(id+"F0.wireOp",EDGE,"E14.22.7"),sQuery(id+"F0.wireOp",EDGE,"E14.22.8"),sQuery(id+"F0.wireOp",EDGE,"E14.22.9"),sQuery(id+"F0.wireOp",EDGE,"E14.23.0"),sQuery(id+"F0.wireOp",EDGE,"E14.23.1"),sQuery(id+"F0.wireOp",EDGE,"E14.23.2"),sQuery(id+"F0.wireOp",EDGE,"E14.23.3"),sQuery(id+"F0.wireOp",EDGE,"E14.23.4"),sQuery(id+"F0.wireOp",EDGE,"E14.23.5"),sQuery(id+"F0.wireOp",EDGE,"E14.23.6"),sQuery(id+"F0.wireOp",EDGE,"E14.23.7"),sQuery(id+"F0.wireOp",EDGE,"E14.23.8"),sQuery(id+"F0.wireOp",EDGE,"E14.23.9"),sQuery(id+"F0.wireOp",EDGE,"E14.24.0"),sQuery(id+"F0.wireOp",EDGE,"E14.24.1"),sQuery(id+"F0.wireOp",EDGE,"E14.24.2"),sQuery(id+"F0.wireOp",EDGE,"E14.24.3"),sQuery(id+"F0.wireOp",EDGE,"E14.24.4"),sQuery(id+"F0.wireOp",EDGE,"E14.24.5"),sQuery(id+"F0.wireOp",EDGE,"E14.24.6"),sQuery(id+"F0.wireOp",EDGE,"E14.24.7"),sQuery(id+"F0.wireOp",EDGE,"E14.24.8"),sQuery(id+"F0.wireOp",EDGE,"E14.24.9"),sQuery(id+"F0.wireOp",EDGE,"E14.25.0"),sQuery(id+"F0.wireOp",EDGE,"E14.25.1"),sQuery(id+"F0.wireOp",EDGE,"E14.25.2"),sQuery(id+"F0.wireOp",EDGE,"E14.25.3"),sQuery(id+"F0.wireOp",EDGE,"E14.25.4"),sQuery(id+"F0.wireOp",EDGE,"E14.25.5"),sQuery(id+"F0.wireOp",EDGE,"E14.25.6"),sQuery(id+"F0.wireOp",EDGE,"E14.25.7"),sQuery(id+"F0.wireOp",EDGE,"E14.25.8"),sQuery(id+"F0.wireOp",EDGE,"E14.25.9"),sQuery(id+"F0.wireOp",EDGE,"E14.26.0"),sQuery(id+"F0.wireOp",EDGE,"E14.26.1"),sQuery(id+"F0.wireOp",EDGE,"E14.26.2"),sQuery(id+"F0.wireOp",EDGE,"E14.26.3"),sQuery(id+"F0.wireOp",EDGE,"E14.26.4"),sQuery(id+"F0.wireOp",EDGE,"E14.26.5"),sQuery(id+"F0.wireOp",EDGE,"E14.26.6"),sQuery(id+"F0.wireOp",EDGE,"E14.26.7"),sQuery(id+"F0.wireOp",EDGE,"E14.26.8"),sQuery(id+"F0.wireOp",EDGE,"E14.26.9"),sQuery(id+"F0.wireOp",EDGE,"E14.27.0"),sQuery(id+"F0.wireOp",EDGE,"E14.27.1"),sQuery(id+"F0.wireOp",EDGE,"E14.27.2"),sQuery(id+"F0.wireOp",EDGE,"E14.27.3"),sQuery(id+"F0.wireOp",EDGE,"E14.27.4"),sQuery(id+"F0.wireOp",EDGE,"E14.27.5"),sQuery(id+"F0.wireOp",EDGE,"E14.27.6"),sQuery(id+"F0.wireOp",EDGE,"E14.27.7"),sQuery(id+"F0.wireOp",EDGE,"E14.27.8"),sQuery(id+"F0.wireOp",EDGE,"E14.27.9"),sQuery(id+"F0.wireOp",EDGE,"E14.28.0"),sQuery(id+"F0.wireOp",EDGE,"E14.28.1"),sQuery(id+"F0.wireOp",EDGE,"E14.28.2"),sQuery(id+"F0.wireOp",EDGE,"E14.28.3"),sQuery(id+"F0.wireOp",EDGE,"E14.28.4"),sQuery(id+"F0.wireOp",EDGE,"E14.28.5"),sQuery(id+"F0.wireOp",EDGE,"E14.28.6"),sQuery(id+"F0.wireOp",EDGE,"E14.28.7"),sQuery(id+"F0.wireOp",EDGE,"E14.28.8"),sQuery(id+"F0.wireOp",EDGE,"E14.28.9"),sQuery(id+"F0.wireOp",EDGE,"E14.29.0"),sQuery(id+"F0.wireOp",EDGE,"E14.29.1"),sQuery(id+"F0.wireOp",EDGE,"E14.29.2"),sQuery(id+"F0.wireOp",EDGE,"E14.29.3"),sQuery(id+"F0.wireOp",EDGE,"E14.29.4"),sQuery(id+"F0.wireOp",EDGE,"E14.29.5"),sQuery(id+"F0.wireOp",EDGE,"E14.29.6"),sQuery(id+"F0.wireOp",EDGE,"E14.29.7"),sQuery(id+"F0.wireOp",EDGE,"E14.29.8"),sQuery(id+"F0.wireOp",EDGE,"E14.29.9"),sQuery(id+"F0.wireOp",EDGE,"E14.30.0"),sQuery(id+"F0.wireOp",EDGE,"E14.30.1"),sQuery(id+"F0.wireOp",EDGE,"E14.30.2"),sQuery(id+"F0.wireOp",EDGE,"E14.30.3"),sQuery(id+"F0.wireOp",EDGE,"E14.30.4"),sQuery(id+"F0.wireOp",EDGE,"E14.30.5"),sQuery(id+"F0.wireOp",EDGE,"E14.30.6"),sQuery(id+"F0.wireOp",EDGE,"E14.30.7"),sQuery(id+"F0.wireOp",EDGE,"E14.30.8"),sQuery(id+"F0.wireOp",EDGE,"E14.30.9"),sQuery(id+"F0.wireOp",EDGE,"E14.31.0"),sQuery(id+"F0.wireOp",EDGE,"E14.31.1"),sQuery(id+"F0.wireOp",EDGE,"E14.31.2"),sQuery(id+"F0.wireOp",EDGE,"E14.31.3"),sQuery(id+"F0.wireOp",EDGE,"E14.31.4"),sQuery(id+"F0.wireOp",EDGE,"E14.31.5"),sQuery(id+"F0.wireOp",EDGE,"E14.31.6"),sQuery(id+"F0.wireOp",EDGE,"E14.31.7"),sQuery(id+"F0.wireOp",EDGE,"E14.31.8"),sQuery(id+"F0.wireOp",EDGE,"E14.31.9"),sQuery(id+"F0.wireOp",EDGE,"E14.32.0"),sQuery(id+"F0.wireOp",EDGE,"E14.32.1"),sQuery(id+"F0.wireOp",EDGE,"E14.32.2"),sQuery(id+"F0.wireOp",EDGE,"E14.32.3"),sQuery(id+"F0.wireOp",EDGE,"E14.32.4"),sQuery(id+"F0.wireOp",EDGE,"E14.32.5"),sQuery(id+"F0.wireOp",EDGE,"E14.32.6"),sQuery(id+"F0.wireOp",EDGE,"E14.32.7"),sQuery(id+"F0.wireOp",EDGE,"E14.32.8"),sQuery(id+"F0.wireOp",EDGE,"E14.32.9"),sQuery(id+"F0.wireOp",EDGE,"E14.33.0"),sQuery(id+"F0.wireOp",EDGE,"E14.33.1"),sQuery(id+"F0.wireOp",EDGE,"E14.33.2"),sQuery(id+"F0.wireOp",EDGE,"E14.33.3"),sQuery(id+"F0.wireOp",EDGE,"E14.33.4"),sQuery(id+"F0.wireOp",EDGE,"E14.33.5"),sQuery(id+"F0.wireOp",EDGE,"E14.33.6"),sQuery(id+"F0.wireOp",EDGE,"E14.33.7"),sQuery(id+"F0.wireOp",EDGE,"E14.33.8"),sQuery(id+"F0.wireOp",EDGE,"E14.33.9"),sQuery(id+"F0.wireOp",EDGE,"E14.34.0"),sQuery(id+"F0.wireOp",EDGE,"E14.34.1"),sQuery(id+"F0.wireOp",EDGE,"E14.34.2"),sQuery(id+"F0.wireOp",EDGE,"E14.34.3"),sQuery(id+"F0.wireOp",EDGE,"E14.34.4"),sQuery(id+"F0.wireOp",EDGE,"E14.34.5"),sQuery(id+"F0.wireOp",EDGE,"E14.34.6"),sQuery(id+"F0.wireOp",EDGE,"E14.34.7"),sQuery(id+"F0.wireOp",EDGE,"E14.34.8"),sQuery(id+"F0.wireOp",EDGE,"E14.34.9"),sQuery(id+"F0.wireOp",EDGE,"E14.35.0"),sQuery(id+"F0.wireOp",EDGE,"E14.35.1"),sQuery(id+"F0.wireOp",EDGE,"E14.35.2"),sQuery(id+"F0.wireOp",EDGE,"E14.35.3"),sQuery(id+"F0.wireOp",EDGE,"E14.35.4"),sQuery(id+"F0.wireOp",EDGE,"E14.35.5"),sQuery(id+"F0.wireOp",EDGE,"E14.35.6"),sQuery(id+"F0.wireOp",EDGE,"E14.35.7"),sQuery(id+"F0.wireOp",EDGE,"E14.35.8"),sQuery(id+"F0.wireOp",EDGE,"E14.35.9"),sQuery(id+"F0.wireOp",EDGE,"E14.36.0"),sQuery(id+"F0.wireOp",EDGE,"E14.36.1"),sQuery(id+"F0.wireOp",EDGE,"E14.36.2"),sQuery(id+"F0.wireOp",EDGE,"E14.36.3"),sQuery(id+"F0.wireOp",EDGE,"E14.36.4"),sQuery(id+"F0.wireOp",EDGE,"E14.36.5"),sQuery(id+"F0.wireOp",EDGE,"E14.36.6"),sQuery(id+"F0.wireOp",EDGE,"E14.36.7"),sQuery(id+"F0.wireOp",EDGE,"E14.36.8"),sQuery(id+"F0.wireOp",EDGE,"E14.36.9"),sQuery(id+"F0.wireOp",EDGE,"E14.37.0"),sQuery(id+"F0.wireOp",EDGE,"E14.37.1"),sQuery(id+"F0.wireOp",EDGE,"E14.37.2"),sQuery(id+"F0.wireOp",EDGE,"E14.37.3"),sQuery(id+"F0.wireOp",EDGE,"E14.37.4"),sQuery(id+"F0.wireOp",EDGE,"E14.37.5"),sQuery(id+"F0.wireOp",EDGE,"E14.37.6"),sQuery(id+"F0.wireOp",EDGE,"E14.37.7"),sQuery(id+"F0.wireOp",EDGE,"E14.37.8"),sQuery(id+"F0.wireOp",EDGE,"E14.37.9"),sQuery(id+"F0.wireOp",EDGE,"E14.38.0"),sQuery(id+"F0.wireOp",EDGE,"E14.38.1"),sQuery(id+"F0.wireOp",EDGE,"E14.38.2"),sQuery(id+"F0.wireOp",EDGE,"E14.38.3"),sQuery(id+"F0.wireOp",EDGE,"E14.38.4"),sQuery(id+"F0.wireOp",EDGE,"E14.38.5"),sQuery(id+"F0.wireOp",EDGE,"E14.38.6"),sQuery(id+"F0.wireOp",EDGE,"E14.38.7"),sQuery(id+"F0.wireOp",EDGE,"E14.38.8"),sQuery(id+"F0.wireOp",EDGE,"E14.38.9"),sQuery(id+"F0.wireOp",EDGE,"E14.39.0"),sQuery(id+"F0.wireOp",EDGE,"E14.39.1"),sQuery(id+"F0.wireOp",EDGE,"E14.39.2"),sQuery(id+"F0.wireOp",EDGE,"E14.39.3"),sQuery(id+"F0.wireOp",EDGE,"E14.39.4"),sQuery(id+"F0.wireOp",EDGE,"E14.39.5"),sQuery(id+"F0.wireOp",EDGE,"E14.39.6"),sQuery(id+"F0.wireOp",EDGE,"E14.39.7"),sQuery(id+"F0.wireOp",EDGE,"E14.39.8"),sQuery(id+"F0.wireOp",EDGE,"E14.39.9"),sQuery(id+"F0.wireOp",EDGE,"E14.40.0"),sQuery(id+"F0.wireOp",EDGE,"E14.40.1"),sQuery(id+"F0.wireOp",EDGE,"E14.40.2"),sQuery(id+"F0.wireOp",EDGE,"E14.40.3"),sQuery(id+"F0.wireOp",EDGE,"E14.40.4"),sQuery(id+"F0.wireOp",EDGE,"E14.40.5"),sQuery(id+"F0.wireOp",EDGE,"E14.40.6"),sQuery(id+"F0.wireOp",EDGE,"E14.40.7"),sQuery(id+"F0.wireOp",EDGE,"E14.40.8"),sQuery(id+"F0.wireOp",EDGE,"E14.40.9"),sQuery(id+"F0.wireOp",EDGE,"E14.41.0"),sQuery(id+"F0.wireOp",EDGE,"E14.41.1"),sQuery(id+"F0.wireOp",EDGE,"E14.41.2"),sQuery(id+"F0.wireOp",EDGE,"E14.41.3"),sQuery(id+"F0.wireOp",EDGE,"E14.41.4"),sQuery(id+"F0.wireOp",EDGE,"E14.41.5"),sQuery(id+"F0.wireOp",EDGE,"E14.41.6"),sQuery(id+"F0.wireOp",EDGE,"E14.41.7"),sQuery(id+"F0.wireOp",EDGE,"E14.41.8"),sQuery(id+"F0.wireOp",EDGE,"E14.41.9"),sQuery(id+"F0.wireOp",EDGE,"E14.42.0"),sQuery(id+"F0.wireOp",EDGE,"E14.42.1"),sQuery(id+"F0.wireOp",EDGE,"E14.42.2"),sQuery(id+"F0.wireOp",EDGE,"E14.42.3"),sQuery(id+"F0.wireOp",EDGE,"E14.42.4"),sQuery(id+"F0.wireOp",EDGE,"E14.42.5"),sQuery(id+"F0.wireOp",EDGE,"E14.42.6"),sQuery(id+"F0.wireOp",EDGE,"E14.42.7"),sQuery(id+"F0.wireOp",EDGE,"E14.42.8"),sQuery(id+"F0.wireOp",EDGE,"E14.42.9"),sQuery(id+"F0.wireOp",EDGE,"E14.43.0"),sQuery(id+"F0.wireOp",EDGE,"E14.43.1"),sQuery(id+"F0.wireOp",EDGE,"E14.43.2"),sQuery(id+"F0.wireOp",EDGE,"E14.43.3"),sQuery(id+"F0.wireOp",EDGE,"E14.43.4"),sQuery(id+"F0.wireOp",EDGE,"E14.43.5"),sQuery(id+"F0.wireOp",EDGE,"E14.43.6"),sQuery(id+"F0.wireOp",EDGE,"E14.43.7"),sQuery(id+"F0.wireOp",EDGE,"E14.43.8"),sQuery(id+"F0.wireOp",EDGE,"E14.43.9"),sQuery(id+"F0.wireOp",EDGE,"E14.44.0"),sQuery(id+"F0.wireOp",EDGE,"E14.44.1"),sQuery(id+"F0.wireOp",EDGE,"E14.44.2"),sQuery(id+"F0.wireOp",EDGE,"E14.44.3"),sQuery(id+"F0.wireOp",EDGE,"E14.44.4"),sQuery(id+"F0.wireOp",EDGE,"E14.44.5"),sQuery(id+"F0.wireOp",EDGE,"E14.44.6"),sQuery(id+"F0.wireOp",EDGE,"E14.44.7"),sQuery(id+"F0.wireOp",EDGE,"E14.44.8"),sQuery(id+"F0.wireOp",EDGE,"E14.44.9"),sQuery(id+"F0.wireOp",EDGE,"E14.45.0"),sQuery(id+"F0.wireOp",EDGE,"E14.45.1"),sQuery(id+"F0.wireOp",EDGE,"E14.45.2"),sQuery(id+"F0.wireOp",EDGE,"E14.45.3"),sQuery(id+"F0.wireOp",EDGE,"E14.45.4"),sQuery(id+"F0.wireOp",EDGE,"E14.45.5"),sQuery(id+"F0.wireOp",EDGE,"E14.45.6"),sQuery(id+"F0.wireOp",EDGE,"E14.45.7"),sQuery(id+"F0.wireOp",EDGE,"E14.45.8"),sQuery(id+"F0.wireOp",EDGE,"E14.45.9"),sQuery(id+"F0.wireOp",EDGE,"E14.46.0"),sQuery(id+"F0.wireOp",EDGE,"E14.46.1"),sQuery(id+"F0.wireOp",EDGE,"E14.46.2"),sQuery(id+"F0.wireOp",EDGE,"E14.46.3"),sQuery(id+"F0.wireOp",EDGE,"E14.46.4"),sQuery(id+"F0.wireOp",EDGE,"E14.46.5"),sQuery(id+"F0.wireOp",EDGE,"E14.46.6"),sQuery(id+"F0.wireOp",EDGE,"E14.46.7"),sQuery(id+"F0.wireOp",EDGE,"E14.46.8"),sQuery(id+"F0.wireOp",EDGE,"E14.46.9"),sQuery(id+"F0.wireOp",EDGE,"E14.47.0"),sQuery(id+"F0.wireOp",EDGE,"E14.47.1"),sQuery(id+"F0.wireOp",EDGE,"E14.47.2"),sQuery(id+"F0.wireOp",EDGE,"E14.47.3"),sQuery(id+"F0.wireOp",EDGE,"E14.47.4"),sQuery(id+"F0.wireOp",EDGE,"E14.47.5"),sQuery(id+"F0.wireOp",EDGE,"E14.47.6"),sQuery(id+"F0.wireOp",EDGE,"E14.47.7"),sQuery(id+"F0.wireOp",EDGE,"E14.47.8"),sQuery(id+"F0.wireOp",EDGE,"E14.47.9"),sQuery(id+"F0.wireOp",EDGE,"E14.48.0"),sQuery(id+"F0.wireOp",EDGE,"E14.48.1"),sQuery(id+"F0.wireOp",EDGE,"E14.48.2"),sQuery(id+"F0.wireOp",EDGE,"E14.48.3"),sQuery(id+"F0.wireOp",EDGE,"E14.48.4"),sQuery(id+"F0.wireOp",EDGE,"E14.48.5"),sQuery(id+"F0.wireOp",EDGE,"E14.48.6"),sQuery(id+"F0.wireOp",EDGE,"E14.48.7"),sQuery(id+"F0.wireOp",EDGE,"E14.48.8"),sQuery(id+"F0.wireOp",EDGE,"E14.48.9"),sQuery(id+"F0.wireOp",EDGE,"E14.49.0"),sQuery(id+"F0.wireOp",EDGE,"E14.49.1"),sQuery(id+"F0.wireOp",EDGE,"E14.49.2"),sQuery(id+"F0.wireOp",EDGE,"E14.49.3"),sQuery(id+"F0.wireOp",EDGE,"E14.49.4"),sQuery(id+"F0.wireOp",EDGE,"E14.49.5"),sQuery(id+"F0.wireOp",EDGE,"E14.49.6"),sQuery(id+"F0.wireOp",EDGE,"E14.49.7"),sQuery(id+"F0.wireOp",EDGE,"E14.49.8"),sQuery(id+"F0.wireOp",EDGE,"E14.49.9"),sQuery(id+"F0.wireOp",EDGE,"E14.50.0"),sQuery(id+"F0.wireOp",EDGE,"E14.50.1"),sQuery(id+"F0.wireOp",EDGE,"E14.50.2"),sQuery(id+"F0.wireOp",EDGE,"E14.50.3"),sQuery(id+"F0.wireOp",EDGE,"E14.50.4"),sQuery(id+"F0.wireOp",EDGE,"E14.50.5"),sQuery(id+"F0.wireOp",EDGE,"E14.50.6"),sQuery(id+"F0.wireOp",EDGE,"E14.50.7"),sQuery(id+"F0.wireOp",EDGE,"E14.50.8"),sQuery(id+"F0.wireOp",EDGE,"E14.50.9"),sQuery(id+"F0.wireOp",EDGE,"E14.51.0"),sQuery(id+"F0.wireOp",EDGE,"E14.51.1"),sQuery(id+"F0.wireOp",EDGE,"E14.51.2"),sQuery(id+"F0.wireOp",EDGE,"E14.51.3"),sQuery(id+"F0.wireOp",EDGE,"E14.51.4"),sQuery(id+"F0.wireOp",EDGE,"E14.51.5"),sQuery(id+"F0.wireOp",EDGE,"E14.51.6"),sQuery(id+"F0.wireOp",EDGE,"E14.51.7"),sQuery(id+"F0.wireOp",EDGE,"E14.51.8"),sQuery(id+"F0.wireOp",EDGE,"E14.51.9"),sQuery(id+"F0.wireOp",EDGE,"E14.52.0"),sQuery(id+"F0.wireOp",EDGE,"E14.52.1"),sQuery(id+"F0.wireOp",EDGE,"E14.52.2"),sQuery(id+"F0.wireOp",EDGE,"E14.52.3"),sQuery(id+"F0.wireOp",EDGE,"E14.52.4"),sQuery(id+"F0.wireOp",EDGE,"E14.52.5"),sQuery(id+"F0.wireOp",EDGE,"E14.52.6"),sQuery(id+"F0.wireOp",EDGE,"E14.52.7"),sQuery(id+"F0.wireOp",EDGE,"E14.52.8"),sQuery(id+"F0.wireOp",EDGE,"E14.52.9"),sQuery(id+"F0.wireOp",EDGE,"E14.53.0"),sQuery(id+"F0.wireOp",EDGE,"E14.53.1"),sQuery(id+"F0.wireOp",EDGE,"E14.53.2"),sQuery(id+"F0.wireOp",EDGE,"E14.53.3"),sQuery(id+"F0.wireOp",EDGE,"E14.53.4"),sQuery(id+"F0.wireOp",EDGE,"E14.53.5"),sQuery(id+"F0.wireOp",EDGE,"E14.53.6"),sQuery(id+"F0.wireOp",EDGE,"E14.53.7"),sQuery(id+"F0.wireOp",EDGE,"E14.53.8"),sQuery(id+"F0.wireOp",EDGE,"E14.53.9"),sQuery(id+"F0.wireOp",EDGE,"E14.54.0"),sQuery(id+"F0.wireOp",EDGE,"E14.54.1"),sQuery(id+"F0.wireOp",EDGE,"E14.54.2"),sQuery(id+"F0.wireOp",EDGE,"E14.54.3"),sQuery(id+"F0.wireOp",EDGE,"E14.54.4"),sQuery(id+"F0.wireOp",EDGE,"E14.54.5"),sQuery(id+"F0.wireOp",EDGE,"E14.54.6"),sQuery(id+"F0.wireOp",EDGE,"E14.54.7"),sQuery(id+"F0.wireOp",EDGE,"E14.54.8"),sQuery(id+"F0.wireOp",EDGE,"E14.54.9"),sQuery(id+"F0.wireOp",EDGE,"E14.55.0"),sQuery(id+"F0.wireOp",EDGE,"E14.55.1"),sQuery(id+"F0.wireOp",EDGE,"E14.55.2"),sQuery(id+"F0.wireOp",EDGE,"E14.55.3"),sQuery(id+"F0.wireOp",EDGE,"E14.55.4"),sQuery(id+"F0.wireOp",EDGE,"E14.55.5"),sQuery(id+"F0.wireOp",EDGE,"E14.55.6"),sQuery(id+"F0.wireOp",EDGE,"E14.55.7"),sQuery(id+"F0.wireOp",EDGE,"E14.55.8"),sQuery(id+"F0.wireOp",EDGE,"E14.55.9"),sQuery(id+"F0.wireOp",EDGE,"E14.56.0"),sQuery(id+"F0.wireOp",EDGE,"E14.56.1"),sQuery(id+"F0.wireOp",EDGE,"E14.56.2"),sQuery(id+"F0.wireOp",EDGE,"E14.56.3"),sQuery(id+"F0.wireOp",EDGE,"E14.56.4"),sQuery(id+"F0.wireOp",EDGE,"E14.56.5"),sQuery(id+"F0.wireOp",EDGE,"E14.56.6"),sQuery(id+"F0.wireOp",EDGE,"E14.56.7"),sQuery(id+"F0.wireOp",EDGE,"E14.56.8"),sQuery(id+"F0.wireOp",EDGE,"E14.56.9"),sQuery(id+"F0.wireOp",EDGE,"E14.57.0"),sQuery(id+"F0.wireOp",EDGE,"E14.57.1"),sQuery(id+"F0.wireOp",EDGE,"E14.57.2"),sQuery(id+"F0.wireOp",EDGE,"E14.57.3"),sQuery(id+"F0.wireOp",EDGE,"E14.57.4"),sQuery(id+"F0.wireOp",EDGE,"E14.57.5"),sQuery(id+"F0.wireOp",EDGE,"E14.57.6"),sQuery(id+"F0.wireOp",EDGE,"E14.57.7"),sQuery(id+"F0.wireOp",EDGE,"E14.57.8"),sQuery(id+"F0.wireOp",EDGE,"E14.57.9"),sQuery(id+"F0.wireOp",EDGE,"E14.58.0"),sQuery(id+"F0.wireOp",EDGE,"E14.58.1"),sQuery(id+"F0.wireOp",EDGE,"E14.58.2"),sQuery(id+"F0.wireOp",EDGE,"E14.58.3"),sQuery(id+"F0.wireOp",EDGE,"E14.58.4"),sQuery(id+"F0.wireOp",EDGE,"E14.58.5"),sQuery(id+"F0.wireOp",EDGE,"E14.58.6"),sQuery(id+"F0.wireOp",EDGE,"E14.58.7"),sQuery(id+"F0.wireOp",EDGE,"E14.58.8"),sQuery(id+"F0.wireOp",EDGE,"E14.58.9"),sQuery(id+"F0.wireOp",EDGE,"E14.59.0"),sQuery(id+"F0.wireOp",EDGE,"E14.59.1"),sQuery(id+"F0.wireOp",EDGE,"E14.59.2"),sQuery(id+"F0.wireOp",EDGE,"E14.59.3"),sQuery(id+"F0.wireOp",EDGE,"E14.59.4"),sQuery(id+"F0.wireOp",EDGE,"E14.59.5"),sQuery(id+"F0.wireOp",EDGE,"E14.59.6"),sQuery(id+"F0.wireOp",EDGE,"E14.59.7"),sQuery(id+"F0.wireOp",EDGE,"E14.59.8"),sQuery(id+"F0.wireOp",EDGE,"E14.59.9"),sQuery(id+"F0.wireOp",EDGE,"E14.60.0"),sQuery(id+"F0.wireOp",EDGE,"E14.60.1"),sQuery(id+"F0.wireOp",EDGE,"E14.60.2"),sQuery(id+"F0.wireOp",EDGE,"E14.60.3"),sQuery(id+"F0.wireOp",EDGE,"E14.60.4"),sQuery(id+"F0.wireOp",EDGE,"E14.60.5"),sQuery(id+"F0.wireOp",EDGE,"E14.60.6"),sQuery(id+"F0.wireOp",EDGE,"E14.60.7"),sQuery(id+"F0.wireOp",EDGE,"E14.60.8"),sQuery(id+"F0.wireOp",EDGE,"E14.60.9"),sQuery(id+"F0.wireOp",EDGE,"E14.61.0"),sQuery(id+"F0.wireOp",EDGE,"E14.61.1"),sQuery(id+"F0.wireOp",EDGE,"E14.61.2"),sQuery(id+"F0.wireOp",EDGE,"E14.61.3"),sQuery(id+"F0.wireOp",EDGE,"E14.61.4"),sQuery(id+"F0.wireOp",EDGE,"E14.61.5"),sQuery(id+"F0.wireOp",EDGE,"E14.61.6"),sQuery(id+"F0.wireOp",EDGE,"E14.61.7"),sQuery(id+"F0.wireOp",EDGE,"E14.61.8"),sQuery(id+"F0.wireOp",EDGE,"E14.61.9"),sQuery(id+"F0.wireOp",EDGE,"E14.62.0"),sQuery(id+"F0.wireOp",EDGE,"E14.62.1"),sQuery(id+"F0.wireOp",EDGE,"E14.62.2"),sQuery(id+"F0.wireOp",EDGE,"E14.62.3"),sQuery(id+"F0.wireOp",EDGE,"E14.62.4"),sQuery(id+"F0.wireOp",EDGE,"E14.62.5"),sQuery(id+"F0.wireOp",EDGE,"E14.62.6"),sQuery(id+"F0.wireOp",EDGE,"E14.62.7"),sQuery(id+"F0.wireOp",EDGE,"E14.62.8"),sQuery(id+"F0.wireOp",EDGE,"E14.62.9"),sQuery(id+"F0.wireOp",EDGE,"E14.63.0"),sQuery(id+"F0.wireOp",EDGE,"E14.63.1"),sQuery(id+"F0.wireOp",EDGE,"E14.63.2"),sQuery(id+"F0.wireOp",EDGE,"E14.63.3"),sQuery(id+"F0.wireOp",EDGE,"E14.63.4"),sQuery(id+"F0.wireOp",EDGE,"E14.63.5"),sQuery(id+"F0.wireOp",EDGE,"E14.63.6"),sQuery(id+"F0.wireOp",EDGE,"E14.63.7"),sQuery(id+"F0.wireOp",EDGE,"E14.63.8"),sQuery(id+"F0.wireOp",EDGE,"E14.63.9"),sQuery(id+"F0.wireOp",EDGE,"E14.64.0"),sQuery(id+"F0.wireOp",EDGE,"E14.64.1"),sQuery(id+"F0.wireOp",EDGE,"E14.64.2"),sQuery(id+"F0.wireOp",EDGE,"E14.64.3"),sQuery(id+"F0.wireOp",EDGE,"E14.64.4"),sQuery(id+"F0.wireOp",EDGE,"E14.64.5"),sQuery(id+"F0.wireOp",EDGE,"E14.64.6"),sQuery(id+"F0.wireOp",EDGE,"E14.64.7"),sQuery(id+"F0.wireOp",EDGE,"E14.64.8"),sQuery(id+"F0.wireOp",EDGE,"E14.64.9"),sQuery(id+"F0.wireOp",EDGE,"E14.65.0"),sQuery(id+"F0.wireOp",EDGE,"E14.65.1"),sQuery(id+"F0.wireOp",EDGE,"E14.65.2"),sQuery(id+"F0.wireOp",EDGE,"E14.65.3"),sQuery(id+"F0.wireOp",EDGE,"E14.65.4"),sQuery(id+"F0.wireOp",EDGE,"E14.65.5"),sQuery(id+"F0.wireOp",EDGE,"E14.65.6"),sQuery(id+"F0.wireOp",EDGE,"E14.65.7"),sQuery(id+"F0.wireOp",EDGE,"E14.65.8"),sQuery(id+"F0.wireOp",EDGE,"E14.65.9"),sQuery(id+"F0.wireOp",EDGE,"E14.66.0"),sQuery(id+"F0.wireOp",EDGE,"E14.66.1"),sQuery(id+"F0.wireOp",EDGE,"E14.66.2"),sQuery(id+"F0.wireOp",EDGE,"E14.66.3"),sQuery(id+"F0.wireOp",EDGE,"E14.66.4"),sQuery(id+"F0.wireOp",EDGE,"E14.66.5"),sQuery(id+"F0.wireOp",EDGE,"E14.66.6"),sQuery(id+"F0.wireOp",EDGE,"E14.66.7"),sQuery(id+"F0.wireOp",EDGE,"E14.66.8"),sQuery(id+"F0.wireOp",EDGE,"E14.66.9"),sQuery(id+"F0.wireOp",EDGE,"E14.67.0"),sQuery(id+"F0.wireOp",EDGE,"E14.67.1"),sQuery(id+"F0.wireOp",EDGE,"E14.67.2"),sQuery(id+"F0.wireOp",EDGE,"E14.67.3"),sQuery(id+"F0.wireOp",EDGE,"E14.67.4"),sQuery(id+"F0.wireOp",EDGE,"E14.67.5"),sQuery(id+"F0.wireOp",EDGE,"E14.67.6"),sQuery(id+"F0.wireOp",EDGE,"E14.67.7"),sQuery(id+"F0.wireOp",EDGE,"E14.67.8"),sQuery(id+"F0.wireOp",EDGE,"E14.67.9"),sQuery(id+"F0.wireOp",EDGE,"E14.68.0"),sQuery(id+"F0.wireOp",EDGE,"E14.68.1"),sQuery(id+"F0.wireOp",EDGE,"E14.68.2"),sQuery(id+"F0.wireOp",EDGE,"E14.68.3"),sQuery(id+"F0.wireOp",EDGE,"E14.68.4"),sQuery(id+"F0.wireOp",EDGE,"E14.68.5"),sQuery(id+"F0.wireOp",EDGE,"E14.68.6"),sQuery(id+"F0.wireOp",EDGE,"E14.68.7"),sQuery(id+"F0.wireOp",EDGE,"E14.68.8"),sQuery(id+"F0.wireOp",EDGE,"E14.68.9"),sQuery(id+"F0.wireOp",EDGE,"E14.69.0"),sQuery(id+"F0.wireOp",EDGE,"E14.69.1"),sQuery(id+"F0.wireOp",EDGE,"E14.69.2"),sQuery(id+"F0.wireOp",EDGE,"E14.69.3"),sQuery(id+"F0.wireOp",EDGE,"E14.69.4"),sQuery(id+"F0.wireOp",EDGE,"E14.69.5"),sQuery(id+"F0.wireOp",EDGE,"E14.69.6"),sQuery(id+"F0.wireOp",EDGE,"E14.69.7"),sQuery(id+"F0.wireOp",EDGE,"E14.69.8"),sQuery(id+"F0.wireOp",EDGE,"E14.69.9"),sQuery(id+"F0.wireOp",EDGE,"E14.70.0"),sQuery(id+"F0.wireOp",EDGE,"E14.70.1"),sQuery(id+"F0.wireOp",EDGE,"E14.70.2"),sQuery(id+"F0.wireOp",EDGE,"E14.70.3"),sQuery(id+"F0.wireOp",EDGE,"E14.70.4"),sQuery(id+"F0.wireOp",EDGE,"E14.70.5"),sQuery(id+"F0.wireOp",EDGE,"E14.70.6"),sQuery(id+"F0.wireOp",EDGE,"E14.70.7"),sQuery(id+"F0.wireOp",EDGE,"E14.70.8"),sQuery(id+"F0.wireOp",EDGE,"E14.70.9"),sQuery(id+"F0.wireOp",EDGE,"E14.71.0"),sQuery(id+"F0.wireOp",EDGE,"E14.71.1"),sQuery(id+"F0.wireOp",EDGE,"E14.71.2"),sQuery(id+"F0.wireOp",EDGE,"E14.71.3"),sQuery(id+"F0.wireOp",EDGE,"E14.71.4"),sQuery(id+"F0.wireOp",EDGE,"E14.71.5"),sQuery(id+"F0.wireOp",EDGE,"E14.71.6"),sQuery(id+"F0.wireOp",EDGE,"E14.71.7"),sQuery(id+"F0.wireOp",EDGE,"E14.71.8"),sQuery(id+"F0.wireOp",EDGE,"E14.71.9"),sQuery(id+"F0.wireOp",EDGE,"E14.72.0"),sQuery(id+"F0.wireOp",EDGE,"E14.72.1"),sQuery(id+"F0.wireOp",EDGE,"E14.72.2"),sQuery(id+"F0.wireOp",EDGE,"E14.72.3"),sQuery(id+"F0.wireOp",EDGE,"E14.72.4"),sQuery(id+"F0.wireOp",EDGE,"E14.72.5"),sQuery(id+"F0.wireOp",EDGE,"E14.72.6"),sQuery(id+"F0.wireOp",EDGE,"E14.72.7"),sQuery(id+"F0.wireOp",EDGE,"E14.72.8"),sQuery(id+"F0.wireOp",EDGE,"E14.72.9"),sQuery(id+"F0.wireOp",EDGE,"E14.73.0"),sQuery(id+"F0.wireOp",EDGE,"E14.73.1"),sQuery(id+"F0.wireOp",EDGE,"E14.73.2"),sQuery(id+"F0.wireOp",EDGE,"E14.73.3"),sQuery(id+"F0.wireOp",EDGE,"E14.73.4"),sQuery(id+"F0.wireOp",EDGE,"E14.73.5"),sQuery(id+"F0.wireOp",EDGE,"E14.73.6"),sQuery(id+"F0.wireOp",EDGE,"E14.73.7"),sQuery(id+"F0.wireOp",EDGE,"E14.73.8"),sQuery(id+"F0.wireOp",EDGE,"E14.73.9"),sQuery(id+"F0.wireOp",EDGE,"E14.74.0"),sQuery(id+"F0.wireOp",EDGE,"E14.74.1"),sQuery(id+"F0.wireOp",EDGE,"E14.74.2"),sQuery(id+"F0.wireOp",EDGE,"E14.74.3"),sQuery(id+"F0.wireOp",EDGE,"E14.74.4"),sQuery(id+"F0.wireOp",EDGE,"E14.74.5"),sQuery(id+"F0.wireOp",EDGE,"E14.74.6"),sQuery(id+"F0.wireOp",EDGE,"E14.74.7"),sQuery(id+"F0.wireOp",EDGE,"E14.74.8"),sQuery(id+"F0.wireOp",EDGE,"E14.74.9"),sQuery(id+"F0.wireOp",EDGE,"E14.75.0"),sQuery(id+"F0.wireOp",EDGE,"E14.75.1"),sQuery(id+"F0.wireOp",EDGE,"E14.75.2"),sQuery(id+"F0.wireOp",EDGE,"E14.75.3"),sQuery(id+"F0.wireOp",EDGE,"E14.75.4"),sQuery(id+"F0.wireOp",EDGE,"E14.75.5"),sQuery(id+"F0.wireOp",EDGE,"E14.75.6"),sQuery(id+"F0.wireOp",EDGE,"E14.75.7"),sQuery(id+"F0.wireOp",EDGE,"E14.75.8"),sQuery(id+"F0.wireOp",EDGE,"E14.75.9"),sQuery(id+"F0.wireOp",EDGE,"E14.76.0"),sQuery(id+"F0.wireOp",EDGE,"E14.76.1"),sQuery(id+"F0.wireOp",EDGE,"E14.76.2"),sQuery(id+"F0.wireOp",EDGE,"E14.76.3"),sQuery(id+"F0.wireOp",EDGE,"E14.76.4"),sQuery(id+"F0.wireOp",EDGE,"E14.76.5"),sQuery(id+"F0.wireOp",EDGE,"E14.76.6"),sQuery(id+"F0.wireOp",EDGE,"E14.76.7"),sQuery(id+"F0.wireOp",EDGE,"E14.76.8"),sQuery(id+"F0.wireOp",EDGE,"E14.76.9"),sQuery(id+"F0.wireOp",EDGE,"E14.77.0"),sQuery(id+"F0.wireOp",EDGE,"E14.77.1"),sQuery(id+"F0.wireOp",EDGE,"E14.77.2"),sQuery(id+"F0.wireOp",EDGE,"E14.77.3"),sQuery(id+"F0.wireOp",EDGE,"E14.77.4"),sQuery(id+"F0.wireOp",EDGE,"E14.77.5"),sQuery(id+"F0.wireOp",EDGE,"E14.77.6"),sQuery(id+"F0.wireOp",EDGE,"E14.77.7"),sQuery(id+"F0.wireOp",EDGE,"E14.77.8"),sQuery(id+"F0.wireOp",EDGE,"E14.77.9"),sQuery(id+"F0.wireOp",EDGE,"E14.78.0"),sQuery(id+"F0.wireOp",EDGE,"E14.78.1"),sQuery(id+"F0.wireOp",EDGE,"E14.78.2"),sQuery(id+"F0.wireOp",EDGE,"E14.78.3"),sQuery(id+"F0.wireOp",EDGE,"E14.78.4"),sQuery(id+"F0.wireOp",EDGE,"E14.78.5"),sQuery(id+"F0.wireOp",EDGE,"E14.78.6"),sQuery(id+"F0.wireOp",EDGE,"E14.78.7"),sQuery(id+"F0.wireOp",EDGE,"E14.78.8"),sQuery(id+"F0.wireOp",EDGE,"E14.78.9"),sQuery(id+"F0.wireOp",EDGE,"E14.79.0"),sQuery(id+"F0.wireOp",EDGE,"E14.79.1"),sQuery(id+"F0.wireOp",EDGE,"E14.79.2"),sQuery(id+"F0.wireOp",EDGE,"E14.79.3"),sQuery(id+"F0.wireOp",EDGE,"E14.79.4"),sQuery(id+"F0.wireOp",EDGE,"E14.79.5"),sQuery(id+"F0.wireOp",EDGE,"E14.79.6"),sQuery(id+"F0.wireOp",EDGE,"E14.79.7"),sQuery(id+"F0.wireOp",EDGE,"E14.79.8"),sQuery(id+"F0.wireOp",EDGE,"E14.79.9"),sQuery(id+"F0.wireOp",EDGE,"E14.80.0"),sQuery(id+"F0.wireOp",EDGE,"E14.80.1"),sQuery(id+"F0.wireOp",EDGE,"E14.80.2"),sQuery(id+"F0.wireOp",EDGE,"E14.80.3"),sQuery(id+"F0.wireOp",EDGE,"E14.80.4"),sQuery(id+"F0.wireOp",EDGE,"E14.80.5"),sQuery(id+"F0.wireOp",EDGE,"E14.80.6"),sQuery(id+"F0.wireOp",EDGE,"E14.80.7"),sQuery(id+"F0.wireOp",EDGE,"E14.80.8"),sQuery(id+"F0.wireOp",EDGE,"E14.80.9"),sQuery(id+"F0.wireOp",EDGE,"E14.81.0"),sQuery(id+"F0.wireOp",EDGE,"E14.81.1"),sQuery(id+"F0.wireOp",EDGE,"E14.81.2"),sQuery(id+"F0.wireOp",EDGE,"E14.81.3"),sQuery(id+"F0.wireOp",EDGE,"E14.81.4"),sQuery(id+"F0.wireOp",EDGE,"E14.81.5"),sQuery(id+"F0.wireOp",EDGE,"E14.81.6"),sQuery(id+"F0.wireOp",EDGE,"E14.81.7"),sQuery(id+"F0.wireOp",EDGE,"E14.81.8"),sQuery(id+"F0.wireOp",EDGE,"E14.81.9"),sQuery(id+"F0.wireOp",EDGE,"E14.82.0"),sQuery(id+"F0.wireOp",EDGE,"E14.82.1"),sQuery(id+"F0.wireOp",EDGE,"E14.82.2"),sQuery(id+"F0.wireOp",EDGE,"E14.82.3"),sQuery(id+"F0.wireOp",EDGE,"E14.82.4"),sQuery(id+"F0.wireOp",EDGE,"E14.82.5"),sQuery(id+"F0.wireOp",EDGE,"E14.82.6"),sQuery(id+"F0.wireOp",EDGE,"E14.82.7"),sQuery(id+"F0.wireOp",EDGE,"E14.82.8"),sQuery(id+"F0.wireOp",EDGE,"E14.82.9"),sQuery(id+"F0.wireOp",EDGE,"E14.83.0"),sQuery(id+"F0.wireOp",EDGE,"E14.83.1"),sQuery(id+"F0.wireOp",EDGE,"E14.83.2"),sQuery(id+"F0.wireOp",EDGE,"E14.83.3"),sQuery(id+"F0.wireOp",EDGE,"E14.83.4"),sQuery(id+"F0.wireOp",EDGE,"E14.83.5"),sQuery(id+"F0.wireOp",EDGE,"E14.83.6"),sQuery(id+"F0.wireOp",EDGE,"E14.83.7"),sQuery(id+"F0.wireOp",EDGE,"E14.83.8"),sQuery(id+"F0.wireOp",EDGE,"E14.83.9"),sQuery(id+"F0.wireOp",EDGE,"E14.84.0"),sQuery(id+"F0.wireOp",EDGE,"E14.84.1"),sQuery(id+"F0.wireOp",EDGE,"E14.84.2"),sQuery(id+"F0.wireOp",EDGE,"E14.84.3"),sQuery(id+"F0.wireOp",EDGE,"E14.84.4"),sQuery(id+"F0.wireOp",EDGE,"E14.84.5"),sQuery(id+"F0.wireOp",EDGE,"E14.84.6"),sQuery(id+"F0.wireOp",EDGE,"E14.84.7"),sQuery(id+"F0.wireOp",EDGE,"E14.84.8"),sQuery(id+"F0.wireOp",EDGE,"E14.84.9"),sQuery(id+"F0.wireOp",EDGE,"E14.85.0"),sQuery(id+"F0.wireOp",EDGE,"E14.85.1"),sQuery(id+"F0.wireOp",EDGE,"E14.85.2"),sQuery(id+"F0.wireOp",EDGE,"E14.85.3"),sQuery(id+"F0.wireOp",EDGE,"E14.85.4"),sQuery(id+"F0.wireOp",EDGE,"E14.85.5"),sQuery(id+"F0.wireOp",EDGE,"E14.85.6"),sQuery(id+"F0.wireOp",EDGE,"E14.85.7"),sQuery(id+"F0.wireOp",EDGE,"E14.85.8"),sQuery(id+"F0.wireOp",EDGE,"E14.85.9"),sQuery(id+"F0.wireOp",EDGE,"E14.86.0"),sQuery(id+"F0.wireOp",EDGE,"E14.86.1"),sQuery(id+"F0.wireOp",EDGE,"E14.86.2"),sQuery(id+"F0.wireOp",EDGE,"E14.86.3"),sQuery(id+"F0.wireOp",EDGE,"E14.86.4"),sQuery(id+"F0.wireOp",EDGE,"E14.86.5"),sQuery(id+"F0.wireOp",EDGE,"E14.86.6"),sQuery(id+"F0.wireOp",EDGE,"E14.86.7"),sQuery(id+"F0.wireOp",EDGE,"E14.86.8"),sQuery(id+"F0.wireOp",EDGE,"E14.86.9"),sQuery(id+"F0.wireOp",EDGE,"E14.87.0"),sQuery(id+"F0.wireOp",EDGE,"E14.87.1"),sQuery(id+"F0.wireOp",EDGE,"E14.87.2"),sQuery(id+"F0.wireOp",EDGE,"E14.87.3"),sQuery(id+"F0.wireOp",EDGE,"E14.87.4"),sQuery(id+"F0.wireOp",EDGE,"E14.87.5"),sQuery(id+"F0.wireOp",EDGE,"E14.87.6"),sQuery(id+"F0.wireOp",EDGE,"E14.87.7"),sQuery(id+"F0.wireOp",EDGE,"E14.87.8"),sQuery(id+"F0.wireOp",EDGE,"E14.87.9"),sQuery(id+"F0.wireOp",EDGE,"E14.88.0"),sQuery(id+"F0.wireOp",EDGE,"E14.88.1"),sQuery(id+"F0.wireOp",EDGE,"E14.88.2"),sQuery(id+"F0.wireOp",EDGE,"E14.88.3"),sQuery(id+"F0.wireOp",EDGE,"E14.88.4"),sQuery(id+"F0.wireOp",EDGE,"E14.88.5"),sQuery(id+"F0.wireOp",EDGE,"E14.88.6"),sQuery(id+"F0.wireOp",EDGE,"E14.88.7"),sQuery(id+"F0.wireOp",EDGE,"E14.88.8"),sQuery(id+"F0.wireOp",EDGE,"E14.88.9"),sQuery(id+"F0.wireOp",EDGE,"E14.89.0"),sQuery(id+"F0.wireOp",EDGE,"E14.89.1"),sQuery(id+"F0.wireOp",EDGE,"E14.89.2"),sQuery(id+"F0.wireOp",EDGE,"E14.89.3"),sQuery(id+"F0.wireOp",EDGE,"E14.89.4"),sQuery(id+"F0.wireOp",EDGE,"E14.89.5"),sQuery(id+"F0.wireOp",EDGE,"E14.89.6"),sQuery(id+"F0.wireOp",EDGE,"E14.89.7"),sQuery(id+"F0.wireOp",EDGE,"E14.89.8"),sQuery(id+"F0.wireOp",EDGE,"E14.89.9"),sQuery(id+"F0.wireOp",EDGE,"E14.90.0"),sQuery(id+"F0.wireOp",EDGE,"E14.90.1"),sQuery(id+"F0.wireOp",EDGE,"E14.90.2"),sQuery(id+"F0.wireOp",EDGE,"E14.90.3"),sQuery(id+"F0.wireOp",EDGE,"E14.90.4"),sQuery(id+"F0.wireOp",EDGE,"E14.90.5"),sQuery(id+"F0.wireOp",EDGE,"E14.90.6"),sQuery(id+"F0.wireOp",EDGE,"E14.90.7"),sQuery(id+"F0.wireOp",EDGE,"E14.90.8"),sQuery(id+"F0.wireOp",EDGE,"E14.90.9"),sQuery(id+"F0.wireOp",EDGE,"E14.91.0"),sQuery(id+"F0.wireOp",EDGE,"E14.91.1"),sQuery(id+"F0.wireOp",EDGE,"E14.91.2"),sQuery(id+"F0.wireOp",EDGE,"E14.91.3"),sQuery(id+"F0.wireOp",EDGE,"E14.91.4"),sQuery(id+"F0.wireOp",EDGE,"E14.91.5"),sQuery(id+"F0.wireOp",EDGE,"E14.91.6"),sQuery(id+"F0.wireOp",EDGE,"E14.91.7"),sQuery(id+"F0.wireOp",EDGE,"E14.91.8"),sQuery(id+"F0.wireOp",EDGE,"E14.91.9"),sQuery(id+"F0.wireOp",EDGE,"E14.92.0"),sQuery(id+"F0.wireOp",EDGE,"E14.92.1"),sQuery(id+"F0.wireOp",EDGE,"E14.92.2"),sQuery(id+"F0.wireOp",EDGE,"E14.92.3"),sQuery(id+"F0.wireOp",EDGE,"E14.92.4"),sQuery(id+"F0.wireOp",EDGE,"E14.92.5"),sQuery(id+"F0.wireOp",EDGE,"E14.92.6"),sQuery(id+"F0.wireOp",EDGE,"E14.92.7"),sQuery(id+"F0.wireOp",EDGE,"E14.92.8"),sQuery(id+"F0.wireOp",EDGE,"E14.92.9"),sQuery(id+"F0.wireOp",EDGE,"E14.93.0"),sQuery(id+"F0.wireOp",EDGE,"E14.93.1"),sQuery(id+"F0.wireOp",EDGE,"E14.93.2"),sQuery(id+"F0.wireOp",EDGE,"E14.93.3"),sQuery(id+"F0.wireOp",EDGE,"E14.93.4"),sQuery(id+"F0.wireOp",EDGE,"E14.93.5"),sQuery(id+"F0.wireOp",EDGE,"E14.93.6"),sQuery(id+"F0.wireOp",EDGE,"E14.93.7"),sQuery(id+"F0.wireOp",EDGE,"E14.93.8"),sQuery(id+"F0.wireOp",EDGE,"E14.93.9"),sQuery(id+"F0.wireOp",EDGE,"E14.94.0"),sQuery(id+"F0.wireOp",EDGE,"E14.94.1"),sQuery(id+"F0.wireOp",EDGE,"E14.94.2"),sQuery(id+"F0.wireOp",EDGE,"E14.94.3"),sQuery(id+"F0.wireOp",EDGE,"E14.94.4"),sQuery(id+"F0.wireOp",EDGE,"E14.94.5"),sQuery(id+"F0.wireOp",EDGE,"E14.94.6"),sQuery(id+"F0.wireOp",EDGE,"E14.94.7"),sQuery(id+"F0.wireOp",EDGE,"E14.94.8"),sQuery(id+"F0.wireOp",EDGE,"E14.94.9"),sQuery(id+"F0.wireOp",EDGE,"E14.95.0"),sQuery(id+"F0.wireOp",EDGE,"E14.95.1"),sQuery(id+"F0.wireOp",EDGE,"E14.95.2"),sQuery(id+"F0.wireOp",EDGE,"E14.95.3"),sQuery(id+"F0.wireOp",EDGE,"E14.95.4"),sQuery(id+"F0.wireOp",EDGE,"E14.95.5"),sQuery(id+"F0.wireOp",EDGE,"E14.95.6"),sQuery(id+"F0.wireOp",EDGE,"E14.95.7"),sQuery(id+"F0.wireOp",EDGE,"E14.95.8"),sQuery(id+"F0.wireOp",EDGE,"E14.95.9"),sQuery(id+"F0.wireOp",EDGE,"E14.96.0"),sQuery(id+"F0.wireOp",EDGE,"E14.96.1"),sQuery(id+"F0.wireOp",EDGE,"E14.96.2"),sQuery(id+"F0.wireOp",EDGE,"E14.96.3"),sQuery(id+"F0.wireOp",EDGE,"E14.96.4"),sQuery(id+"F0.wireOp",EDGE,"E14.96.5"),sQuery(id+"F0.wireOp",EDGE,"E14.96.6"),sQuery(id+"F0.wireOp",EDGE,"E14.96.7"),sQuery(id+"F0.wireOp",EDGE,"E14.96.8"),sQuery(id+"F0.wireOp",EDGE,"E14.96.9"),sQuery(id+"F0.wireOp",EDGE,"E14.97.0"),sQuery(id+"F0.wireOp",EDGE,"E14.97.1"),sQuery(id+"F0.wireOp",EDGE,"E14.97.2"),sQuery(id+"F0.wireOp",EDGE,"E14.97.3"),sQuery(id+"F0.wireOp",EDGE,"E14.97.4"),sQuery(id+"F0.wireOp",EDGE,"E14.97.5"),sQuery(id+"F0.wireOp",EDGE,"E14.97.6"),sQuery(id+"F0.wireOp",EDGE,"E14.97.7"),sQuery(id+"F0.wireOp",EDGE,"E14.97.8"),sQuery(id+"F0.wireOp",EDGE,"E14.97.9"),sQuery(id+"F0.wireOp",EDGE,"E14.98.0"),sQuery(id+"F0.wireOp",EDGE,"E14.98.1"),sQuery(id+"F0.wireOp",EDGE,"E14.98.2"),sQuery(id+"F0.wireOp",EDGE,"E14.98.3"),sQuery(id+"F0.wireOp",EDGE,"E14.98.4"),sQuery(id+"F0.wireOp",EDGE,"E14.98.5"),sQuery(id+"F0.wireOp",EDGE,"E14.98.6"),sQuery(id+"F0.wireOp",EDGE,"E14.98.7"),sQuery(id+"F0.wireOp",EDGE,"E14.98.8"),sQuery(id+"F0.wireOp",EDGE,"E14.98.9"),sQuery(id+"F0.wireOp",EDGE,"E14.99.0"),sQuery(id+"F0.wireOp",EDGE,"E14.99.1"),sQuery(id+"F0.wireOp",EDGE,"E14.99.2"),sQuery(id+"F0.wireOp",EDGE,"E14.99.3"),sQuery(id+"F0.wireOp",EDGE,"E14.99.4"),sQuery(id+"F0.wireOp",EDGE,"E14.99.5"),sQuery(id+"F0.wireOp",EDGE,"E14.99.6"),sQuery(id+"F0.wireOp",EDGE,"E14.99.7"),sQuery(id+"F0.wireOp",EDGE,"E14.99.8"),sQuery(id+"F0.wireOp",EDGE,"E14.99.9"),sQuery(id+"F0.wireOp",EDGE,"E14.100.0"),sQuery(id+"F0.wireOp",EDGE,"E14.100.1"),sQuery(id+"F0.wireOp",EDGE,"E14.100.2"),sQuery(id+"F0.wireOp",EDGE,"E14.100.3"),sQuery(id+"F0.wireOp",EDGE,"E14.100.4"),sQuery(id+"F0.wireOp",EDGE,"E14.100.5"),sQuery(id+"F0.wireOp",EDGE,"E14.100.6"),sQuery(id+"F0.wireOp",EDGE,"E14.100.7"),sQuery(id+"F0.wireOp",EDGE,"E14.100.8"),sQuery(id+"F0.wireOp",EDGE,"E14.100.9"),sQuery(id+"F0.wireOp",EDGE,"E14.101.0"),sQuery(id+"F0.wireOp",EDGE,"E14.101.1"),sQuery(id+"F0.wireOp",EDGE,"E14.101.2"),sQuery(id+"F0.wireOp",EDGE,"E14.101.3"),sQuery(id+"F0.wireOp",EDGE,"E14.101.4"),sQuery(id+"F0.wireOp",EDGE,"E14.101.5"),sQuery(id+"F0.wireOp",EDGE,"E14.101.6"),sQuery(id+"F0.wireOp",EDGE,"E14.101.7"),sQuery(id+"F0.wireOp",EDGE,"E14.101.8"),sQuery(id+"F0.wireOp",EDGE,"E14.101.9"),sQuery(id+"F0.wireOp",EDGE,"E14.102.0"),sQuery(id+"F0.wireOp",EDGE,"E14.102.1"),sQuery(id+"F0.wireOp",EDGE,"E14.102.2"),sQuery(id+"F0.wireOp",EDGE,"E14.102.3"),sQuery(id+"F0.wireOp",EDGE,"E14.102.4"),sQuery(id+"F0.wireOp",EDGE,"E14.102.5"),sQuery(id+"F0.wireOp",EDGE,"E14.102.6"),sQuery(id+"F0.wireOp",EDGE,"E14.102.7"),sQuery(id+"F0.wireOp",EDGE,"E14.102.8"),sQuery(id+"F0.wireOp",EDGE,"E14.102.9"),sQuery(id+"F0.wireOp",EDGE,"E14.103.0"),sQuery(id+"F0.wireOp",EDGE,"E14.103.1"),sQuery(id+"F0.wireOp",EDGE,"E14.103.2"),sQuery(id+"F0.wireOp",EDGE,"E14.103.3"),sQuery(id+"F0.wireOp",EDGE,"E14.103.4"),sQuery(id+"F0.wireOp",EDGE,"E14.103.5"),sQuery(id+"F0.wireOp",EDGE,"E14.103.6"),sQuery(id+"F0.wireOp",EDGE,"E14.103.7"),sQuery(id+"F0.wireOp",EDGE,"E14.103.8"),sQuery(id+"F0.wireOp",EDGE,"E14.103.9"),sQuery(id+"F0.wireOp",EDGE,"E14.104.0"),sQuery(id+"F0.wireOp",EDGE,"E14.104.1"),sQuery(id+"F0.wireOp",EDGE,"E14.104.2"),sQuery(id+"F0.wireOp",EDGE,"E14.104.3"),sQuery(id+"F0.wireOp",EDGE,"E14.104.4"),sQuery(id+"F0.wireOp",EDGE,"E14.104.5"),sQuery(id+"F0.wireOp",EDGE,"E14.104.6"),sQuery(id+"F0.wireOp",EDGE,"E14.104.7"),sQuery(id+"F0.wireOp",EDGE,"E14.104.8"),sQuery(id+"F0.wireOp",EDGE,"E14.104.9"),sQuery(id+"F0.wireOp",EDGE,"E14.105.0"),sQuery(id+"F0.wireOp",EDGE,"E14.105.1"),sQuery(id+"F0.wireOp",EDGE,"E14.105.2"),sQuery(id+"F0.wireOp",EDGE,"E14.105.3"),sQuery(id+"F0.wireOp",EDGE,"E14.105.4"),sQuery(id+"F0.wireOp",EDGE,"E14.105.5"),sQuery(id+"F0.wireOp",EDGE,"E14.105.6"),sQuery(id+"F0.wireOp",EDGE,"E14.105.7"),sQuery(id+"F0.wireOp",EDGE,"E14.105.8"),sQuery(id+"F0.wireOp",EDGE,"E14.105.9"),sQuery(id+"F0.wireOp",EDGE,"E14.106.0"),sQuery(id+"F0.wireOp",EDGE,"E14.106.1"),sQuery(id+"F0.wireOp",EDGE,"E14.106.2"),sQuery(id+"F0.wireOp",EDGE,"E14.106.3"),sQuery(id+"F0.wireOp",EDGE,"E14.106.4"),sQuery(id+"F0.wireOp",EDGE,"E14.106.5"),sQuery(id+"F0.wireOp",EDGE,"E14.106.6"),sQuery(id+"F0.wireOp",EDGE,"E14.106.7"),sQuery(id+"F0.wireOp",EDGE,"E14.106.8"),sQuery(id+"F0.wireOp",EDGE,"E14.106.9"),sQuery(id+"F0.wireOp",EDGE,"E14.107.0"),sQuery(id+"F0.wireOp",EDGE,"E14.107.1"),sQuery(id+"F0.wireOp",EDGE,"E14.107.2"),sQuery(id+"F0.wireOp",EDGE,"E14.107.3"),sQuery(id+"F0.wireOp",EDGE,"E14.107.4"),sQuery(id+"F0.wireOp",EDGE,"E14.107.5"),sQuery(id+"F0.wireOp",EDGE,"E14.107.6"),sQuery(id+"F0.wireOp",EDGE,"E14.107.7"),sQuery(id+"F0.wireOp",EDGE,"E14.107.8"),sQuery(id+"F0.wireOp",EDGE,"E14.107.9"),sQuery(id+"F0.wireOp",EDGE,"E14.108.0"),sQuery(id+"F0.wireOp",EDGE,"E14.108.1"),sQuery(id+"F0.wireOp",EDGE,"E14.108.2"),sQuery(id+"F0.wireOp",EDGE,"E14.108.3"),sQuery(id+"F0.wireOp",EDGE,"E14.108.4"),sQuery(id+"F0.wireOp",EDGE,"E14.108.5"),sQuery(id+"F0.wireOp",EDGE,"E14.108.6"),sQuery(id+"F0.wireOp",EDGE,"E14.108.7"),sQuery(id+"F0.wireOp",EDGE,"E14.108.8"),sQuery(id+"F0.wireOp",EDGE,"E14.108.9"),sQuery(id+"F0.wireOp",EDGE,"E14.109.0"),sQuery(id+"F0.wireOp",EDGE,"E14.109.1"),sQuery(id+"F0.wireOp",EDGE,"E14.109.2"),sQuery(id+"F0.wireOp",EDGE,"E14.109.3"),sQuery(id+"F0.wireOp",EDGE,"E14.109.4"),sQuery(id+"F0.wireOp",EDGE,"E14.109.5"),sQuery(id+"F0.wireOp",EDGE,"E14.109.6"),sQuery(id+"F0.wireOp",EDGE,"E14.109.7"),sQuery(id+"F0.wireOp",EDGE,"E14.109.8"),sQuery(id+"F0.wireOp",EDGE,"E14.109.9"),sQuery(id+"F0.wireOp",EDGE,"E14.110.0"),sQuery(id+"F0.wireOp",EDGE,"E14.110.1"),sQuery(id+"F0.wireOp",EDGE,"E14.110.2"),sQuery(id+"F0.wireOp",EDGE,"E14.110.3"),sQuery(id+"F0.wireOp",EDGE,"E14.110.4"),sQuery(id+"F0.wireOp",EDGE,"E14.110.5"),sQuery(id+"F0.wireOp",EDGE,"E14.110.6"),sQuery(id+"F0.wireOp",EDGE,"E14.110.7"),sQuery(id+"F0.wireOp",EDGE,"E14.110.8"),sQuery(id+"F0.wireOp",EDGE,"E14.110.9"),sQuery(id+"F0.wireOp",EDGE,"E14.111.0"),sQuery(id+"F0.wireOp",EDGE,"E14.111.1"),sQuery(id+"F0.wireOp",EDGE,"E14.111.2"),sQuery(id+"F0.wireOp",EDGE,"E14.111.3"),sQuery(id+"F0.wireOp",EDGE,"E14.111.4"),sQuery(id+"F0.wireOp",EDGE,"E14.111.5"),sQuery(id+"F0.wireOp",EDGE,"E14.111.6"),sQuery(id+"F0.wireOp",EDGE,"E14.111.7"),sQuery(id+"F0.wireOp",EDGE,"E14.111.8"),sQuery(id+"F0.wireOp",EDGE,"E14.111.9"),sQuery(id+"F0.wireOp",EDGE,"E14.112.0"),sQuery(id+"F0.wireOp",EDGE,"E14.112.1"),sQuery(id+"F0.wireOp",EDGE,"E14.112.2"),sQuery(id+"F0.wireOp",EDGE,"E14.112.3"),sQuery(id+"F0.wireOp",EDGE,"E14.112.4"),sQuery(id+"F0.wireOp",EDGE,"E14.112.5"),sQuery(id+"F0.wireOp",EDGE,"E14.112.6"),sQuery(id+"F0.wireOp",EDGE,"E14.112.7"),sQuery(id+"F0.wireOp",EDGE,"E14.112.8"),sQuery(id+"F0.wireOp",EDGE,"E14.112.9"),sQuery(id+"F0.wireOp",EDGE,"E14.113.0"),sQuery(id+"F0.wireOp",EDGE,"E14.113.1"),sQuery(id+"F0.wireOp",EDGE,"E14.113.2"),sQuery(id+"F0.wireOp",EDGE,"E14.113.3"),sQuery(id+"F0.wireOp",EDGE,"E14.113.4"),sQuery(id+"F0.wireOp",EDGE,"E14.113.5"),sQuery(id+"F0.wireOp",EDGE,"E14.113.6"),sQuery(id+"F0.wireOp",EDGE,"E14.113.7"),sQuery(id+"F0.wireOp",EDGE,"E14.113.8"),sQuery(id+"F0.wireOp",EDGE,"E14.113.9"),sQuery(id+"F0.wireOp",EDGE,"E14.114.0"),sQuery(id+"F0.wireOp",EDGE,"E14.114.1"),sQuery(id+"F0.wireOp",EDGE,"E14.114.2"),sQuery(id+"F0.wireOp",EDGE,"E14.114.3"),sQuery(id+"F0.wireOp",EDGE,"E14.114.4"),sQuery(id+"F0.wireOp",EDGE,"E14.114.5"),sQuery(id+"F0.wireOp",EDGE,"E14.114.6"),sQuery(id+"F0.wireOp",EDGE,"E14.114.7"),sQuery(id+"F0.wireOp",EDGE,"E14.114.8"),sQuery(id+"F0.wireOp",EDGE,"E14.114.9"),sQuery(id+"F0.wireOp",EDGE,"E14.115.0"),sQuery(id+"F0.wireOp",EDGE,"E14.115.1"),sQuery(id+"F0.wireOp",EDGE,"E14.115.2"),sQuery(id+"F0.wireOp",EDGE,"E14.115.3"),sQuery(id+"F0.wireOp",EDGE,"E14.115.4"),sQuery(id+"F0.wireOp",EDGE,"E14.115.5"),sQuery(id+"F0.wireOp",EDGE,"E14.115.6"),sQuery(id+"F0.wireOp",EDGE,"E14.115.7"),sQuery(id+"F0.wireOp",EDGE,"E14.115.8"),sQuery(id+"F0.wireOp",EDGE,"E14.115.9"),sQuery(id+"F0.wireOp",EDGE,"E14.116.0"),sQuery(id+"F0.wireOp",EDGE,"E14.116.1"),sQuery(id+"F0.wireOp",EDGE,"E14.116.2"),sQuery(id+"F0.wireOp",EDGE,"E14.116.3"),sQuery(id+"F0.wireOp",EDGE,"E14.116.4"),sQuery(id+"F0.wireOp",EDGE,"E14.116.5"),sQuery(id+"F0.wireOp",EDGE,"E14.116.6"),sQuery(id+"F0.wireOp",EDGE,"E14.116.7"),sQuery(id+"F0.wireOp",EDGE,"E14.116.8"),sQuery(id+"F0.wireOp",EDGE,"E14.116.9"),sQuery(id+"F0.wireOp",EDGE,"E14.117.0"),sQuery(id+"F0.wireOp",EDGE,"E14.117.1"),sQuery(id+"F0.wireOp",EDGE,"E14.117.2"),sQuery(id+"F0.wireOp",EDGE,"E14.117.3"),sQuery(id+"F0.wireOp",EDGE,"E14.117.4"),sQuery(id+"F0.wireOp",EDGE,"E14.117.5"),sQuery(id+"F0.wireOp",EDGE,"E14.117.6"),sQuery(id+"F0.wireOp",EDGE,"E14.117.7"),sQuery(id+"F0.wireOp",EDGE,"E14.117.8"),sQuery(id+"F0.wireOp",EDGE,"E14.117.9"),sQuery(id+"F0.wireOp",EDGE,"E14.118.0"),sQuery(id+"F0.wireOp",EDGE,"E14.118.1"),sQuery(id+"F0.wireOp",EDGE,"E14.118.2"),sQuery(id+"F0.wireOp",EDGE,"E14.118.3"),sQuery(id+"F0.wireOp",EDGE,"E14.118.4"),sQuery(id+"F0.wireOp",EDGE,"E14.118.5"),sQuery(id+"F0.wireOp",EDGE,"E14.118.6"),sQuery(id+"F0.wireOp",EDGE,"E14.118.7"),sQuery(id+"F0.wireOp",EDGE,"E14.118.8"),sQuery(id+"F0.wireOp",EDGE,"E14.118.9"),sQuery(id+"F0.wireOp",EDGE,"E14.119.0"),sQuery(id+"F0.wireOp",EDGE,"E14.119.1"),sQuery(id+"F0.wireOp",EDGE,"E14.119.2"),sQuery(id+"F0.wireOp",EDGE,"E14.119.3"),sQuery(id+"F0.wireOp",EDGE,"E14.119.4"),sQuery(id+"F0.wireOp",EDGE,"E14.119.5"),sQuery(id+"F0.wireOp",EDGE,"E14.119.6"),sQuery(id+"F0.wireOp",EDGE,"E14.119.7"),sQuery(id+"F0.wireOp",EDGE,"E14.119.8"),sQuery(id+"F0.wireOp",EDGE,"E14.119.9"),sQuery(id+"F0.wireOp",EDGE,"E15.trimOffspring"),sQuery(id+"F0.wireOp",EDGE,"E16.trimOffspring"),sQuery(id+"F0.wireOp",EDGE,"E17.trimOffspring"),sQuery(id+"F0.wireOp",EDGE,"E18.trimOffspring"),sQuery(id+"F0.wireOp",EDGE,"E19.trimOffspring"),sQuery(id+"F0.wireOp",EDGE,"E20.trimOffspring"),sQuery(id+"F0.wireOp",EDGE,"E21.trimOffspring"),sQuery(id+"F0.wireOp",EDGE,"E22.trimOffspring"),sQuery(id+"F0.wireOp",EDGE,"E23.trimOffspring"),sQuery(id+"F0.wireOp",EDGE,"E24.trimOffspring"),sQuery(id+"F0.wireOp",EDGE,"E25.trimOffspring"),sQuery(id+"F0.wireOp",EDGE,"E26.trimOffspring"),sQuery(id+"F0.wireOp",EDGE,"E27.trimOffspring"),sQuery(id+"F0.wireOp",EDGE,"E28.trimOffspring"),sQuery(id+"F0.wireOp",EDGE,"E29.trimOffspring"),sQuery(id+"F0.wireOp",EDGE,"E30.trimOffspring"),sQuery(id+"F0.wireOp",EDGE,"E31.trimOffspring"),sQuery(id+"F0.wireOp",EDGE,"E32.trimOffspring"),sQuery(id+"F0.wireOp",EDGE,"E33.trimOffspring"),sQuery(id+"F0.wireOp",EDGE,"E34.trimOffspring"),sQuery(id+"F0.wireOp",EDGE,"E35.trimOffspring"),sQuery(id+"F0.wireOp",EDGE,"E36.trimOffspring"),sQuery(id+"F0.wireOp",EDGE,"E37.trimOffspring"),sQuery(id+"F0.wireOp",EDGE,"E38.trimOffspring"),sQuery(id+"F0.wireOp",EDGE,"E39.trimOffspring"),sQuery(id+"F0.wireOp",EDGE,"E40.trimOffspring"),sQuery(id+"F0.wireOp",EDGE,"E41.trimOffspring"),sQuery(id+"F0.wireOp",EDGE,"E42.trimOffspring"),sQuery(id+"F0.wireOp",EDGE,"E43.trimOffspring"),sQuery(id+"F0.wireOp",EDGE,"E44.trimOffspring"),sQuery(id+"F0.wireOp",EDGE,"E45.trimOffspring"),sQuery(id+"F0.wireOp",EDGE,"E46.trimOffspring"),sQuery(id+"F0.wireOp",EDGE,"E47.trimOffspring"),sQuery(id+"F0.wireOp",EDGE,"E48.trimOffspring"),sQuery(id+"F0.wireOp",EDGE,"E49.trimOffspring"),sQuery(id+"F0.wireOp",EDGE,"E73.1.0"),sQuery(id+"F0.wireOp",EDGE,"E73.1.1"),sQuery(id+"F0.wireOp",EDGE,"E73.2.0"),sQuery(id+"F0.wireOp",EDGE,"E73.2.1"),sQuery(id+"F0.wireOp",EDGE,"E74.3.3.0"),sQuery(id+"F0.wireOp",EDGE,"E74.4.3.0"),sQuery(id+"F0.wireOp",EDGE,"E74.3.4.0"),sQuery(id+"F0.wireOp",EDGE,"E74.4.4.0"),sQuery(id+"F0.wireOp",EDGE,"E74.3.5.0"),sQuery(id+"F0.wireOp",EDGE,"E74.4.5.0"),sQuery(id+"F0.wireOp",EDGE,"E74.3.6.0"),sQuery(id+"F0.wireOp",EDGE,"E74.4.6.0"),sQuery(id+"F0.wireOp",EDGE,"E74.3.7.0"),sQuery(id+"F0.wireOp",EDGE,"E74.4.7.0"),sQuery(id+"F0.wireOp",EDGE,"E74.3.8.0"),sQuery(id+"F0.wireOp",EDGE,"E74.4.8.0"),sQuery(id+"F0.wireOp",EDGE,"E74.3.9.0"),sQuery(id+"F0.wireOp",EDGE,"E74.4.9.0"),sQuery(id+"F0.wireOp",EDGE,"E74.3.10.0"),sQuery(id+"F0.wireOp",EDGE,"E74.4.10.0"),sQuery(id+"F0.wireOp",EDGE,"E74.3.11.0"),sQuery(id+"F0.wireOp",EDGE,"E74.4.11.0"),sQuery(id+"F0.wireOp",EDGE,"E74.3.12.0"),sQuery(id+"F0.wireOp",EDGE,"E74.4.12.0"),sQuery(id+"F0.wireOp",EDGE,"E74.3.13.0"),sQuery(id+"F0.wireOp",EDGE,"E74.4.13.0"),sQuery(id+"F0.wireOp",EDGE,"E74.3.14.0"),sQuery(id+"F0.wireOp",EDGE,"E74.4.14.0"),sQuery(id+"F0.wireOp",EDGE,"E74.3.15.0"),sQuery(id+"F0.wireOp",EDGE,"E74.4.15.0"),sQuery(id+"F0.wireOp",EDGE,"E74.3.16.0"),sQuery(id+"F0.wireOp",EDGE,"E74.4.16.0"),sQuery(id+"F0.wireOp",EDGE,"E74.3.17.0"),sQuery(id+"F0.wireOp",EDGE,"E74.4.17.0"),sQuery(id+"F0.wireOp",EDGE,"E74.3.18.0"),sQuery(id+"F0.wireOp",EDGE,"E74.4.18.0"),sQuery(id+"F0.wireOp",EDGE,"E74.3.19.0"),sQuery(id+"F0.wireOp",EDGE,"E74.4.19.0"),sQuery(id+"F0.wireOp",EDGE,"E74.3.20.0"),sQuery(id+"F0.wireOp",EDGE,"E74.4.20.0"),sQuery(id+"F0.wireOp",EDGE,"E74.3.21.0"),sQuery(id+"F0.wireOp",EDGE,"E74.4.21.0"),sQuery(id+"F0.wireOp",EDGE,"E74.3.22.0"),sQuery(id+"F0.wireOp",EDGE,"E74.4.22.0"),sQuery(id+"F0.wireOp",EDGE,"E74.3.23.0"),sQuery(id+"F0.wireOp",EDGE,"E74.4.23.0"),sQuery(id+"F0.wireOp",EDGE,"E74.3.24.0"),sQuery(id+"F0.wireOp",EDGE,"E74.4.24.0"),sQuery(id+"F0.wireOp",EDGE,"E74.3.25.0"),sQuery(id+"F0.wireOp",EDGE,"E74.4.25.0"),sQuery(id+"F0.wireOp",EDGE,"E74.3.26.0"),sQuery(id+"F0.wireOp",EDGE,"E74.4.26.0"),sQuery(id+"F0.wireOp",EDGE,"E74.3.27.0"),sQuery(id+"F0.wireOp",EDGE,"E74.4.27.0"),sQuery(id+"F0.wireOp",EDGE,"E74.3.28.0"),sQuery(id+"F0.wireOp",EDGE,"E74.4.28.0"),sQuery(id+"F0.wireOp",EDGE,"E74.3.29.0"),sQuery(id+"F0.wireOp",EDGE,"E74.4.29.0"),sQuery(id+"F0.wireOp",EDGE,"E74.3.30.0"),sQuery(id+"F0.wireOp",EDGE,"E74.4.30.0"),sQuery(id+"F0.wireOp",EDGE,"E74.3.31.0"),sQuery(id+"F0.wireOp",EDGE,"E74.4.31.0"),sQuery(id+"F0.wireOp",EDGE,"E74.3.32.0"),sQuery(id+"F0.wireOp",EDGE,"E74.4.32.0"),sQuery(id+"F0.wireOp",EDGE,"E74.3.33.0"),sQuery(id+"F0.wireOp",EDGE,"E74.4.33.0"),sQuery(id+"F0.wireOp",EDGE,"E74.3.34.0"),sQuery(id+"F0.wireOp",EDGE,"E74.4.34.0"),sQuery(id+"F0.wireOp",EDGE,"E74.3.35.0"),sQuery(id+"F0.wireOp",EDGE,"E74.4.35.0"),sQuery(id+"F0.wireOp",EDGE,"E74.3.36.0"),sQuery(id+"F0.wireOp",EDGE,"E74.4.36.0"),sQuery(id+"F0.wireOp",EDGE,"E74.3.37.0"),sQuery(id+"F0.wireOp",EDGE,"E74.4.37.0"),sQuery(id+"F0.wireOp",EDGE,"E74.3.38.0"),sQuery(id+"F0.wireOp",EDGE,"E74.4.38.0"),sQuery(id+"F0.wireOp",EDGE,"E74.3.39.0"),sQuery(id+"F0.wireOp",EDGE,"E74.4.39.0"),sQuery(id+"F0.wireOp",EDGE,"E74.3.40.0"),sQuery(id+"F0.wireOp",EDGE,"E74.4.40.0"),sQuery(id+"F0.wireOp",EDGE,"E74.3.41.0"),sQuery(id+"F0.wireOp",EDGE,"E74.4.41.0"),sQuery(id+"F0.wireOp",EDGE,"E74.3.42.0"),sQuery(id+"F0.wireOp",EDGE,"E74.4.42.0"),sQuery(id+"F0.wireOp",EDGE,"E74.3.43.0"),sQuery(id+"F0.wireOp",EDGE,"E74.4.43.0"),sQuery(id+"F0.wireOp",EDGE,"E74.3.44.0"),sQuery(id+"F0.wireOp",EDGE,"E74.4.44.0"),sQuery(id+"F0.wireOp",EDGE,"E74.3.45.0"),sQuery(id+"F0.wireOp",EDGE,"E74.4.45.0"),sQuery(id+"F0.wireOp",EDGE,"E74.3.46.0"),sQuery(id+"F0.wireOp",EDGE,"E74.4.46.0"),sQuery(id+"F0.wireOp",EDGE,"E74.3.47.0"),sQuery(id+"F0.wireOp",EDGE,"E74.4.47.0"),sQuery(id+"F0.wireOp",EDGE,"E74.3.48.0"),sQuery(id+"F0.wireOp",EDGE,"E74.4.48.0"),sQuery(id+"F0.wireOp",EDGE,"E74.3.49.0"),sQuery(id+"F0.wireOp",EDGE,"E74.4.49.0"),sQuery(id+"F0.wireOp",EDGE,"E74.3.50.0"),sQuery(id+"F0.wireOp",EDGE,"E74.4.50.0"),sQuery(id+"F0.wireOp",EDGE,"E74.3.51.0"),sQuery(id+"F0.wireOp",EDGE,"E74.4.51.0"),sQuery(id+"F0.wireOp",EDGE,"E74.3.52.0"),sQuery(id+"F0.wireOp",EDGE,"E74.4.52.0"),sQuery(id+"F0.wireOp",EDGE,"E74.3.53.0"),sQuery(id+"F0.wireOp",EDGE,"E74.4.53.0"),sQuery(id+"F0.wireOp",EDGE,"E74.3.54.0"),sQuery(id+"F0.wireOp",EDGE,"E74.4.54.0"),sQuery(id+"F0.wireOp",EDGE,"E74.3.55.0"),sQuery(id+"F0.wireOp",EDGE,"E74.4.55.0"),sQuery(id+"F0.wireOp",EDGE,"E74.3.56.0"),sQuery(id+"F0.wireOp",EDGE,"E74.4.56.0"),sQuery(id+"F0.wireOp",EDGE,"E74.3.57.0"),sQuery(id+"F0.wireOp",EDGE,"E74.4.57.0"),sQuery(id+"F0.wireOp",EDGE,"E74.3.58.0"),sQuery(id+"F0.wireOp",EDGE,"E74.4.58.0"),sQuery(id+"F0.wireOp",EDGE,"E74.3.59.0"),sQuery(id+"F0.wireOp",EDGE,"E74.4.59.0"),sQuery(id+"F0.wireOp",EDGE,"E74.3.60.0"),sQuery(id+"F0.wireOp",EDGE,"E74.4.60.0"),sQuery(id+"F0.wireOp",EDGE,"E74.3.61.0"),sQuery(id+"F0.wireOp",EDGE,"E74.4.61.0"),sQuery(id+"F0.wireOp",EDGE,"E74.3.62.0"),sQuery(id+"F0.wireOp",EDGE,"E74.4.62.0"),sQuery(id+"F0.wireOp",EDGE,"E74.3.63.0"),sQuery(id+"F0.wireOp",EDGE,"E74.4.63.0"),sQuery(id+"F0.wireOp",EDGE,"E74.3.64.0"),sQuery(id+"F0.wireOp",EDGE,"E74.4.64.0"),sQuery(id+"F0.wireOp",EDGE,"E74.3.65.0"),sQuery(id+"F0.wireOp",EDGE,"E74.4.65.0"),sQuery(id+"F0.wireOp",EDGE,"E74.3.66.0"),sQuery(id+"F0.wireOp",EDGE,"E74.4.66.0"),sQuery(id+"F0.wireOp",EDGE,"E74.3.67.0"),sQuery(id+"F0.wireOp",EDGE,"E74.4.67.0"),sQuery(id+"F0.wireOp",EDGE,"E74.3.68.0"),sQuery(id+"F0.wireOp",EDGE,"E74.4.68.0"),sQuery(id+"F0.wireOp",EDGE,"E74.3.69.0"),sQuery(id+"F0.wireOp",EDGE,"E74.4.69.0"),sQuery(id+"F0.wireOp",EDGE,"E74.3.70.0"),sQuery(id+"F0.wireOp",EDGE,"E74.4.70.0"),sQuery(id+"F0.wireOp",EDGE,"E74.3.71.0"),sQuery(id+"F0.wireOp",EDGE,"E74.4.71.0"),sQuery(id+"F0.wireOp",EDGE,"E74.3.72.0"),sQuery(id+"F0.wireOp",EDGE,"E74.4.72.0"),sQuery(id+"F0.wireOp",EDGE,"E74.3.73.0"),sQuery(id+"F0.wireOp",EDGE,"E74.4.73.0"),sQuery(id+"F0.wireOp",EDGE,"E74.3.74.0"),sQuery(id+"F0.wireOp",EDGE,"E74.4.74.0"),sQuery(id+"F0.wireOp",EDGE,"E74.3.75.0"),sQuery(id+"F0.wireOp",EDGE,"E74.4.75.0"),sQuery(id+"F0.wireOp",EDGE,"E74.3.76.0"),sQuery(id+"F0.wireOp",EDGE,"E74.4.76.0"),sQuery(id+"F0.wireOp",EDGE,"E74.3.77.0"),sQuery(id+"F0.wireOp",EDGE,"E74.4.77.0"),sQuery(id+"F0.wireOp",EDGE,"E74.3.78.0"),sQuery(id+"F0.wireOp",EDGE,"E74.4.78.0"),sQuery(id+"F0.wireOp",EDGE,"E74.3.79.0"),sQuery(id+"F0.wireOp",EDGE,"E74.4.79.0"),sQuery(id+"F0.wireOp",EDGE,"E74.3.80.0"),sQuery(id+"F0.wireOp",EDGE,"E74.4.80.0"),sQuery(id+"F0.wireOp",EDGE,"E74.3.81.0"),sQuery(id+"F0.wireOp",EDGE,"E74.4.81.0"),sQuery(id+"F0.wireOp",EDGE,"E74.3.82.0"),sQuery(id+"F0.wireOp",EDGE,"E74.4.82.0"),sQuery(id+"F0.wireOp",EDGE,"E74.3.83.0"),sQuery(id+"F0.wireOp",EDGE,"E74.4.83.0"),sQuery(id+"F0.wireOp",EDGE,"E74.3.84.0"),sQuery(id+"F0.wireOp",EDGE,"E74.4.84.0"),sQuery(id+"F0.wireOp",EDGE,"E74.3.85.0"),sQuery(id+"F0.wireOp",EDGE,"E74.4.85.0"),sQuery(id+"F0.wireOp",EDGE,"E74.3.86.0"),sQuery(id+"F0.wireOp",EDGE,"E74.4.86.0"),sQuery(id+"F0.wireOp",EDGE,"E74.3.87.0"),sQuery(id+"F0.wireOp",EDGE,"E74.4.87.0"),sQuery(id+"F0.wireOp",EDGE,"E74.3.88.0"),sQuery(id+"F0.wireOp",EDGE,"E74.4.88.0"),sQuery(id+"F0.wireOp",EDGE,"E74.3.89.0"),sQuery(id+"F0.wireOp",EDGE,"E74.4.89.0"),sQuery(id+"F0.wireOp",EDGE,"E74.3.90.0"),sQuery(id+"F0.wireOp",EDGE,"E74.4.90.0"),sQuery(id+"F0.wireOp",EDGE,"E74.3.91.0"),sQuery(id+"F0.wireOp",EDGE,"E74.4.91.0"),sQuery(id+"F0.wireOp",EDGE,"E74.3.92.0"),sQuery(id+"F0.wireOp",EDGE,"E74.4.92.0"),sQuery(id+"F0.wireOp",EDGE,"E74.3.93.0"),sQuery(id+"F0.wireOp",EDGE,"E74.4.93.0"),sQuery(id+"F0.wireOp",EDGE,"E74.3.94.0"),sQuery(id+"F0.wireOp",EDGE,"E74.4.94.0"),sQuery(id+"F0.wireOp",EDGE,"E74.3.95.0"),sQuery(id+"F0.wireOp",EDGE,"E74.4.95.0"),sQuery(id+"F0.wireOp",EDGE,"E74.3.96.0"),sQuery(id+"F0.wireOp",EDGE,"E74.4.96.0"),sQuery(id+"F0.wireOp",EDGE,"E74.3.97.0"),sQuery(id+"F0.wireOp",EDGE,"E74.4.97.0"),sQuery(id+"F0.wireOp",EDGE,"E74.3.98.0"),sQuery(id+"F0.wireOp",EDGE,"E74.4.98.0"),sQuery(id+"F0.wireOp",EDGE,"E74.3.99.0"),sQuery(id+"F0.wireOp",EDGE,"E74.4.99.0"),sQuery(id+"F0.wireOp",EDGE,"E74.3.100.0"),sQuery(id+"F0.wireOp",EDGE,"E74.4.100.0"),sQuery(id+"F0.wireOp",EDGE,"E74.3.101.0"),sQuery(id+"F0.wireOp",EDGE,"E74.4.101.0"),sQuery(id+"F0.wireOp",EDGE,"E74.3.102.0"),sQuery(id+"F0.wireOp",EDGE,"E74.4.102.0"),sQuery(id+"F0.wireOp",EDGE,"E74.3.103.0"),sQuery(id+"F0.wireOp",EDGE,"E74.4.103.0"),sQuery(id+"F0.wireOp",EDGE,"E74.3.104.0"),sQuery(id+"F0.wireOp",EDGE,"E74.4.104.0"),sQuery(id+"F0.wireOp",EDGE,"E74.3.105.0"),sQuery(id+"F0.wireOp",EDGE,"E74.4.105.0"),sQuery(id+"F0.wireOp",EDGE,"E74.3.106.0"),sQuery(id+"F0.wireOp",EDGE,"E74.4.106.0"),sQuery(id+"F0.wireOp",EDGE,"E74.3.107.0"),sQuery(id+"F0.wireOp",EDGE,"E74.4.107.0"),sQuery(id+"F0.wireOp",EDGE,"E74.3.108.0"),sQuery(id+"F0.wireOp",EDGE,"E74.4.108.0"),sQuery(id+"F0.wireOp",EDGE,"E74.3.109.0"),sQuery(id+"F0.wireOp",EDGE,"E74.4.109.0"),sQuery(id+"F0.wireOp",EDGE,"E74.3.110.0"),sQuery(id+"F0.wireOp",EDGE,"E74.4.110.0"),sQuery(id+"F0.wireOp",EDGE,"E74.3.111.0"),sQuery(id+"F0.wireOp",EDGE,"E74.4.111.0"),sQuery(id+"F0.wireOp",EDGE,"E74.3.112.0"),sQuery(id+"F0.wireOp",EDGE,"E74.4.112.0"),sQuery(id+"F0.wireOp",EDGE,"E74.3.113.0"),sQuery(id+"F0.wireOp",EDGE,"E74.4.113.0"),sQuery(id+"F0.wireOp",EDGE,"E74.3.114.0"),sQuery(id+"F0.wireOp",EDGE,"E74.4.114.0"),sQuery(id+"F0.wireOp",EDGE,"E74.3.115.0"),sQuery(id+"F0.wireOp",EDGE,"E74.4.115.0"),sQuery(id+"F0.wireOp",EDGE,"E74.3.116.0"),sQuery(id+"F0.wireOp",EDGE,"E74.4.116.0"),sQuery(id+"F0.wireOp",EDGE,"E74.3.117.0"),sQuery(id+"F0.wireOp",EDGE,"E74.4.117.0"),sQuery(id+"F0.wireOp",EDGE,"E74.3.118.0"),sQuery(id+"F0.wireOp",EDGE,"E74.4.118.0"),sQuery(id+"F0.wireOp",EDGE,"E74.3.119.0"),sQuery(id+"F0.wireOp",EDGE,"E74.4.119.0"),sQuery(id+"F0.wireOp",EDGE,"E75.trimOffspring"),sQuery(id+"F0.wireOp",EDGE,"E76.trimOffspring"),sQuery(id+"F0.wireOp",EDGE,"E77.trimOffspring"),sQuery(id+"F0.wireOp",EDGE,"E78.trimOffspring"),sQuery(id+"F0.wireOp",EDGE,"E79.trimOffspring"),sQuery(id+"F0.wireOp",EDGE,"E80.trimOffspring"),sQuery(id+"F0.wireOp",EDGE,"E81.trimOffspring"),sQuery(id+"F0.wireOp",EDGE,"E82.trimOffspring"),sQuery(id+"F0.wireOp",EDGE,"E83.trimOffspring"),sQuery(id+"F0.wireOp",EDGE,"E84.trimOffspring"),sQuery(id+"F0.wireOp",EDGE,"E85.trimOffspring"),sQuery(id+"F0.wireOp",EDGE,"E86.trimOffspring"),sQuery(id+"F0.wireOp",EDGE,"E87.trimOffspring"),sQuery(id+"F0.wireOp",EDGE,"E88.trimOffspring"),sQuery(id+"F0.wireOp",EDGE,"E89.trimOffspring"),sQuery(id+"F0.wireOp",EDGE,"E90.trimOffspring"),sQuery(id+"F0.wireOp",EDGE,"E91.trimOffspring"),sQuery(id+"F0.wireOp",EDGE,"E92.trimOffspring"),sQuery(id+"F0.wireOp",EDGE,"E93.trimOffspring"),sQuery(id+"F0.wireOp",EDGE,"E94.trimOffspring"),sQuery(id+"F0.wireOp",EDGE,"E95.trimOffspring"),sQuery(id+"F0.wireOp",EDGE,"E96.trimOffspring"),sQuery(id+"F0.wireOp",EDGE,"E97.trimOffspring"),sQuery(id+"F0.wireOp",EDGE,"E98.trimOffspring"),sQuery(id+"F0.wireOp",EDGE,"E99.trimOffspring"),sQuery(id+"F0.wireOp",EDGE,"E100.trimOffspring"),sQuery(id+"F0.wireOp",EDGE,"E101.trimOffspring"),sQuery(id+"F0.wireOp",EDGE,"E102.trimOffspring"),sQuery(id+"F0.wireOp",EDGE,"E103.trimOffspring"),sQuery(id+"F0.wireOp",EDGE,"E104.trimOffspring"),sQuery(id+"F0.wireOp",EDGE,"E105.trimOffspring"),sQuery(id+"F0.wireOp",EDGE,"E106.trimOffspring"),sQuery(id+"F0.wireOp",EDGE,"E107.trimOffspring"),sQuery(id+"F0.wireOp",EDGE,"E108.trimOffspring"),sQuery(id+"F0.wireOp",EDGE,"E109.trimOffspring"),sQuery(id+"F0.wireOp",EDGE,"E110.trimOffspring"),sQuery(id+"F0.wireOp",EDGE,"E111.trimOffspring"),sQuery(id+"F0.wireOp",EDGE,"E112.trimOffspring"),sQuery(id+"F0.wireOp",EDGE,"E113.trimOffspring"),sQuery(id+"F0.wireOp",EDGE,"E114.trimOffspring"),sQuery(id+"F0.wireOp",EDGE,"E115.trimOffspring"),sQuery(id+"F0.wireOp",EDGE,"E116.trimOffspring"),sQuery(id+"F0.wireOp",EDGE,"E117.trimOffspring"),sQuery(id+"F0.wireOp",EDGE,"E118.trimOffspring"),sQuery(id+"F0.wireOp",EDGE,"E119.trimOffspring"),sQuery(id+"F0.wireOp",EDGE,"E120.trimOffspring"),sQuery(id+"F0.wireOp",EDGE,"E121.trimOffspring"),sQuery(id+"F0.wireOp",EDGE,"E122.trimOffspring"),sQuery(id+"F0.wireOp",EDGE,"E123.trimOffspring"),sQuery(id+"F0.wireOp",EDGE,"E124.trimOffspring"),sQuery(id+"F0.wireOp",EDGE,"E125.trimOffspring"),sQuery(id+"F0.wireOp",EDGE,"E126.trimOffspring"),sQuery(id+"F0.wireOp",EDGE,"E127.trimOffspring"),sQuery(id+"F0.wireOp",EDGE,"E128.trimOffspring"),sQuery(id+"F0.wireOp",EDGE,"E129.trimOffspring"),sQuery(id+"F0.wireOp",EDGE,"E130.trimOffspring"),sQuery(id+"F0.wireOp",EDGE,"E131.trimOffspring"),sQuery(id+"F0.wireOp",EDGE,"E132.trimOffspring"),sQuery(id+"F0.wireOp",EDGE,"E133.trimOffspring"),sQuery(id+"F0.wireOp",EDGE,"E134.trimOffspring"),sQuery(id+"F0.wireOp",EDGE,"E135.trimOffspring"),sQuery(id+"F0.wireOp",EDGE,"E136.trimOffspring"),sQuery(id+"F0.wireOp",EDGE,"E137.trimOffspring"),sQuery(id+"F0.wireOp",EDGE,"E138.trimOffspring"),sQuery(id+"F0.wireOp",EDGE,"E139.trimOffspring"),sQuery(id+"F0.wireOp",EDGE,"E140.trimOffspring"),sQuery(id+"F0.wireOp",EDGE,"E141.trimOffspring"),sQuery(id+"F0.wireOp",EDGE,"E142.trimOffspring"),sQuery(id+"F0.wireOp",EDGE,"E143.trimOffspring"),sQuery(id+"F0.wireOp",EDGE,"E144.trimOffspring"),sQuery(id+"F0.wireOp",EDGE,"E145.trimOffspring"),sQuery(id+"F0.wireOp",EDGE,"E146.trimOffspring"),sQuery(id+"F0.wireOp",EDGE,"E147.trimOffspring"),sQuery(id+"F0.wireOp",EDGE,"E148.trimOffspring"),sQuery(id+"F0.wireOp",EDGE,"E149.trimOffspring"),sQuery(id+"F0.wireOp",EDGE,"E150.trimOffspring"),sQuery(id+"F0.wireOp",EDGE,"E151.trimOffspring"),sQuery(id+"F0.wireOp",EDGE,"E152.trimOffspring"),sQuery(id+"F0.wireOp",EDGE,"E153.trimOffspring"),sQuery(id+"F0.wireOp",EDGE,"E154.trimOffspring"),sQuery(id+"F0.wireOp",EDGE,"E155.trimOffspring"),sQuery(id+"F0.wireOp",EDGE,"E156.trimOffspring"),sQuery(id+"F0.wireOp",EDGE,"E157.trimOffspring")])],"isStart":false});
            var sketch = newSketch(context, id + "F4", { "sketchPlane" : qUnion([Q0])});
            skLineSegment(sketch, "E159", {"start": v(0, 0) * mm, "end": v(50.8, 0) * mm, "construction": true});
            skCircle(sketch, "E160", {"center": v(50.8, 0) * mm, "radius": 3.18 * mm});
            skSolve(sketch);
        }
        {
            var Q0;
            Q0 = qSketchRegion(id + "F4", true);
            extrude(context, id + "F5", {"entities" : qUnion([Q0]), "operationType" : NewBodyOperationType.REMOVE, "oppositeDirection" : true, "depth" : 25.4 * mm});
        }
        {
            var Q0;
            Q0=makeQuery(id+"F1.opExtrude","CAP_FACE",FACE,{"disambiguationData":[OSD([sQuery(id+"F0.wireOp",EDGE,"E0"),sQuery(id+"F0.wireOp",EDGE,"E1.trimOffspring"),sQuery(id+"F0.wireOp",EDGE,"E2"),sQuery(id+"F0.wireOp",EDGE,"E3"),sQuery(id+"F0.wireOp",EDGE,"E4.MirrorCS"),sQuery(id+"F0.wireOp",EDGE,"E5.MirrorCS"),sQuery(id+"F0.wireOp",EDGE,"E6.MirrorCS"),sQuery(id+"F0.wireOp",EDGE,"E8.filletArc"),sQuery(id+"F0.wireOp",EDGE,"E9.filletArc"),sQuery(id+"F0.wireOp",EDGE,"E10.filletArc"),sQuery(id+"F0.wireOp",EDGE,"E11.filletArc"),sQuery(id+"F0.wireOp",EDGE,"E12.filletArc"),sQuery(id+"F0.wireOp",EDGE,"E13.filletArc"),sQuery(id+"F0.wireOp",EDGE,"E14.1.0"),sQuery(id+"F0.wireOp",EDGE,"E14.1.1"),sQuery(id+"F0.wireOp",EDGE,"E14.1.2"),sQuery(id+"F0.wireOp",EDGE,"E14.1.3"),sQuery(id+"F0.wireOp",EDGE,"E14.1.4"),sQuery(id+"F0.wireOp",EDGE,"E14.1.5"),sQuery(id+"F0.wireOp",EDGE,"E14.1.6"),sQuery(id+"F0.wireOp",EDGE,"E14.1.7"),sQuery(id+"F0.wireOp",EDGE,"E14.1.8"),sQuery(id+"F0.wireOp",EDGE,"E14.1.9"),sQuery(id+"F0.wireOp",EDGE,"E14.2.0"),sQuery(id+"F0.wireOp",EDGE,"E14.2.1"),sQuery(id+"F0.wireOp",EDGE,"E14.2.2"),sQuery(id+"F0.wireOp",EDGE,"E14.2.3"),sQuery(id+"F0.wireOp",EDGE,"E14.2.4"),sQuery(id+"F0.wireOp",EDGE,"E14.2.5"),sQuery(id+"F0.wireOp",EDGE,"E14.2.6"),sQuery(id+"F0.wireOp",EDGE,"E14.2.7"),sQuery(id+"F0.wireOp",EDGE,"E14.2.8"),sQuery(id+"F0.wireOp",EDGE,"E14.2.9"),sQuery(id+"F0.wireOp",EDGE,"E14.3.0"),sQuery(id+"F0.wireOp",EDGE,"E14.3.1"),sQuery(id+"F0.wireOp",EDGE,"E14.3.2"),sQuery(id+"F0.wireOp",EDGE,"E14.3.3"),sQuery(id+"F0.wireOp",EDGE,"E14.3.4"),sQuery(id+"F0.wireOp",EDGE,"E14.3.5"),sQuery(id+"F0.wireOp",EDGE,"E14.3.6"),sQuery(id+"F0.wireOp",EDGE,"E14.3.7"),sQuery(id+"F0.wireOp",EDGE,"E14.3.8"),sQuery(id+"F0.wireOp",EDGE,"E14.3.9"),sQuery(id+"F0.wireOp",EDGE,"E14.4.0"),sQuery(id+"F0.wireOp",EDGE,"E14.4.1"),sQuery(id+"F0.wireOp",EDGE,"E14.4.2"),sQuery(id+"F0.wireOp",EDGE,"E14.4.3"),sQuery(id+"F0.wireOp",EDGE,"E14.4.4"),sQuery(id+"F0.wireOp",EDGE,"E14.4.5"),sQuery(id+"F0.wireOp",EDGE,"E14.4.6"),sQuery(id+"F0.wireOp",EDGE,"E14.4.7"),sQuery(id+"F0.wireOp",EDGE,"E14.4.8"),sQuery(id+"F0.wireOp",EDGE,"E14.4.9"),sQuery(id+"F0.wireOp",EDGE,"E14.5.0"),sQuery(id+"F0.wireOp",EDGE,"E14.5.1"),sQuery(id+"F0.wireOp",EDGE,"E14.5.2"),sQuery(id+"F0.wireOp",EDGE,"E14.5.3"),sQuery(id+"F0.wireOp",EDGE,"E14.5.4"),sQuery(id+"F0.wireOp",EDGE,"E14.5.5"),sQuery(id+"F0.wireOp",EDGE,"E14.5.6"),sQuery(id+"F0.wireOp",EDGE,"E14.5.7"),sQuery(id+"F0.wireOp",EDGE,"E14.5.8"),sQuery(id+"F0.wireOp",EDGE,"E14.5.9"),sQuery(id+"F0.wireOp",EDGE,"E14.6.0"),sQuery(id+"F0.wireOp",EDGE,"E14.6.1"),sQuery(id+"F0.wireOp",EDGE,"E14.6.2"),sQuery(id+"F0.wireOp",EDGE,"E14.6.3"),sQuery(id+"F0.wireOp",EDGE,"E14.6.4"),sQuery(id+"F0.wireOp",EDGE,"E14.6.5"),sQuery(id+"F0.wireOp",EDGE,"E14.6.6"),sQuery(id+"F0.wireOp",EDGE,"E14.6.7"),sQuery(id+"F0.wireOp",EDGE,"E14.6.8"),sQuery(id+"F0.wireOp",EDGE,"E14.6.9"),sQuery(id+"F0.wireOp",EDGE,"E14.7.0"),sQuery(id+"F0.wireOp",EDGE,"E14.7.1"),sQuery(id+"F0.wireOp",EDGE,"E14.7.2"),sQuery(id+"F0.wireOp",EDGE,"E14.7.3"),sQuery(id+"F0.wireOp",EDGE,"E14.7.4"),sQuery(id+"F0.wireOp",EDGE,"E14.7.5"),sQuery(id+"F0.wireOp",EDGE,"E14.7.6"),sQuery(id+"F0.wireOp",EDGE,"E14.7.7"),sQuery(id+"F0.wireOp",EDGE,"E14.7.8"),sQuery(id+"F0.wireOp",EDGE,"E14.7.9"),sQuery(id+"F0.wireOp",EDGE,"E14.8.0"),sQuery(id+"F0.wireOp",EDGE,"E14.8.1"),sQuery(id+"F0.wireOp",EDGE,"E14.8.2"),sQuery(id+"F0.wireOp",EDGE,"E14.8.3"),sQuery(id+"F0.wireOp",EDGE,"E14.8.4"),sQuery(id+"F0.wireOp",EDGE,"E14.8.5"),sQuery(id+"F0.wireOp",EDGE,"E14.8.6"),sQuery(id+"F0.wireOp",EDGE,"E14.8.7"),sQuery(id+"F0.wireOp",EDGE,"E14.8.8"),sQuery(id+"F0.wireOp",EDGE,"E14.8.9"),sQuery(id+"F0.wireOp",EDGE,"E14.9.0"),sQuery(id+"F0.wireOp",EDGE,"E14.9.1"),sQuery(id+"F0.wireOp",EDGE,"E14.9.2"),sQuery(id+"F0.wireOp",EDGE,"E14.9.3"),sQuery(id+"F0.wireOp",EDGE,"E14.9.4"),sQuery(id+"F0.wireOp",EDGE,"E14.9.5"),sQuery(id+"F0.wireOp",EDGE,"E14.9.6"),sQuery(id+"F0.wireOp",EDGE,"E14.9.7"),sQuery(id+"F0.wireOp",EDGE,"E14.9.8"),sQuery(id+"F0.wireOp",EDGE,"E14.9.9"),sQuery(id+"F0.wireOp",EDGE,"E14.10.0"),sQuery(id+"F0.wireOp",EDGE,"E14.10.1"),sQuery(id+"F0.wireOp",EDGE,"E14.10.2"),sQuery(id+"F0.wireOp",EDGE,"E14.10.3"),sQuery(id+"F0.wireOp",EDGE,"E14.10.4"),sQuery(id+"F0.wireOp",EDGE,"E14.10.5"),sQuery(id+"F0.wireOp",EDGE,"E14.10.6"),sQuery(id+"F0.wireOp",EDGE,"E14.10.7"),sQuery(id+"F0.wireOp",EDGE,"E14.10.8"),sQuery(id+"F0.wireOp",EDGE,"E14.10.9"),sQuery(id+"F0.wireOp",EDGE,"E14.11.0"),sQuery(id+"F0.wireOp",EDGE,"E14.11.1"),sQuery(id+"F0.wireOp",EDGE,"E14.11.2"),sQuery(id+"F0.wireOp",EDGE,"E14.11.3"),sQuery(id+"F0.wireOp",EDGE,"E14.11.4"),sQuery(id+"F0.wireOp",EDGE,"E14.11.5"),sQuery(id+"F0.wireOp",EDGE,"E14.11.6"),sQuery(id+"F0.wireOp",EDGE,"E14.11.7"),sQuery(id+"F0.wireOp",EDGE,"E14.11.8"),sQuery(id+"F0.wireOp",EDGE,"E14.11.9"),sQuery(id+"F0.wireOp",EDGE,"E14.12.0"),sQuery(id+"F0.wireOp",EDGE,"E14.12.1"),sQuery(id+"F0.wireOp",EDGE,"E14.12.2"),sQuery(id+"F0.wireOp",EDGE,"E14.12.3"),sQuery(id+"F0.wireOp",EDGE,"E14.12.4"),sQuery(id+"F0.wireOp",EDGE,"E14.12.5"),sQuery(id+"F0.wireOp",EDGE,"E14.12.6"),sQuery(id+"F0.wireOp",EDGE,"E14.12.7"),sQuery(id+"F0.wireOp",EDGE,"E14.12.8"),sQuery(id+"F0.wireOp",EDGE,"E14.12.9"),sQuery(id+"F0.wireOp",EDGE,"E14.13.0"),sQuery(id+"F0.wireOp",EDGE,"E14.13.1"),sQuery(id+"F0.wireOp",EDGE,"E14.13.2"),sQuery(id+"F0.wireOp",EDGE,"E14.13.3"),sQuery(id+"F0.wireOp",EDGE,"E14.13.4"),sQuery(id+"F0.wireOp",EDGE,"E14.13.5"),sQuery(id+"F0.wireOp",EDGE,"E14.13.6"),sQuery(id+"F0.wireOp",EDGE,"E14.13.7"),sQuery(id+"F0.wireOp",EDGE,"E14.13.8"),sQuery(id+"F0.wireOp",EDGE,"E14.13.9"),sQuery(id+"F0.wireOp",EDGE,"E14.14.0"),sQuery(id+"F0.wireOp",EDGE,"E14.14.1"),sQuery(id+"F0.wireOp",EDGE,"E14.14.2"),sQuery(id+"F0.wireOp",EDGE,"E14.14.3"),sQuery(id+"F0.wireOp",EDGE,"E14.14.4"),sQuery(id+"F0.wireOp",EDGE,"E14.14.5"),sQuery(id+"F0.wireOp",EDGE,"E14.14.6"),sQuery(id+"F0.wireOp",EDGE,"E14.14.7"),sQuery(id+"F0.wireOp",EDGE,"E14.14.8"),sQuery(id+"F0.wireOp",EDGE,"E14.14.9"),sQuery(id+"F0.wireOp",EDGE,"E14.15.0"),sQuery(id+"F0.wireOp",EDGE,"E14.15.1"),sQuery(id+"F0.wireOp",EDGE,"E14.15.2"),sQuery(id+"F0.wireOp",EDGE,"E14.15.3"),sQuery(id+"F0.wireOp",EDGE,"E14.15.4"),sQuery(id+"F0.wireOp",EDGE,"E14.15.5"),sQuery(id+"F0.wireOp",EDGE,"E14.15.6"),sQuery(id+"F0.wireOp",EDGE,"E14.15.7"),sQuery(id+"F0.wireOp",EDGE,"E14.15.8"),sQuery(id+"F0.wireOp",EDGE,"E14.15.9"),sQuery(id+"F0.wireOp",EDGE,"E14.16.0"),sQuery(id+"F0.wireOp",EDGE,"E14.16.1"),sQuery(id+"F0.wireOp",EDGE,"E14.16.2"),sQuery(id+"F0.wireOp",EDGE,"E14.16.3"),sQuery(id+"F0.wireOp",EDGE,"E14.16.4"),sQuery(id+"F0.wireOp",EDGE,"E14.16.5"),sQuery(id+"F0.wireOp",EDGE,"E14.16.6"),sQuery(id+"F0.wireOp",EDGE,"E14.16.7"),sQuery(id+"F0.wireOp",EDGE,"E14.16.8"),sQuery(id+"F0.wireOp",EDGE,"E14.16.9"),sQuery(id+"F0.wireOp",EDGE,"E14.17.0"),sQuery(id+"F0.wireOp",EDGE,"E14.17.1"),sQuery(id+"F0.wireOp",EDGE,"E14.17.2"),sQuery(id+"F0.wireOp",EDGE,"E14.17.3"),sQuery(id+"F0.wireOp",EDGE,"E14.17.4"),sQuery(id+"F0.wireOp",EDGE,"E14.17.5"),sQuery(id+"F0.wireOp",EDGE,"E14.17.6"),sQuery(id+"F0.wireOp",EDGE,"E14.17.7"),sQuery(id+"F0.wireOp",EDGE,"E14.17.8"),sQuery(id+"F0.wireOp",EDGE,"E14.17.9"),sQuery(id+"F0.wireOp",EDGE,"E14.18.0"),sQuery(id+"F0.wireOp",EDGE,"E14.18.1"),sQuery(id+"F0.wireOp",EDGE,"E14.18.2"),sQuery(id+"F0.wireOp",EDGE,"E14.18.3"),sQuery(id+"F0.wireOp",EDGE,"E14.18.4"),sQuery(id+"F0.wireOp",EDGE,"E14.18.5"),sQuery(id+"F0.wireOp",EDGE,"E14.18.6"),sQuery(id+"F0.wireOp",EDGE,"E14.18.7"),sQuery(id+"F0.wireOp",EDGE,"E14.18.8"),sQuery(id+"F0.wireOp",EDGE,"E14.18.9"),sQuery(id+"F0.wireOp",EDGE,"E14.19.0"),sQuery(id+"F0.wireOp",EDGE,"E14.19.1"),sQuery(id+"F0.wireOp",EDGE,"E14.19.2"),sQuery(id+"F0.wireOp",EDGE,"E14.19.3"),sQuery(id+"F0.wireOp",EDGE,"E14.19.4"),sQuery(id+"F0.wireOp",EDGE,"E14.19.5"),sQuery(id+"F0.wireOp",EDGE,"E14.19.6"),sQuery(id+"F0.wireOp",EDGE,"E14.19.7"),sQuery(id+"F0.wireOp",EDGE,"E14.19.8"),sQuery(id+"F0.wireOp",EDGE,"E14.19.9"),sQuery(id+"F0.wireOp",EDGE,"E14.20.0"),sQuery(id+"F0.wireOp",EDGE,"E14.20.1"),sQuery(id+"F0.wireOp",EDGE,"E14.20.2"),sQuery(id+"F0.wireOp",EDGE,"E14.20.3"),sQuery(id+"F0.wireOp",EDGE,"E14.20.4"),sQuery(id+"F0.wireOp",EDGE,"E14.20.5"),sQuery(id+"F0.wireOp",EDGE,"E14.20.6"),sQuery(id+"F0.wireOp",EDGE,"E14.20.7"),sQuery(id+"F0.wireOp",EDGE,"E14.20.8"),sQuery(id+"F0.wireOp",EDGE,"E14.20.9"),sQuery(id+"F0.wireOp",EDGE,"E14.21.0"),sQuery(id+"F0.wireOp",EDGE,"E14.21.1"),sQuery(id+"F0.wireOp",EDGE,"E14.21.2"),sQuery(id+"F0.wireOp",EDGE,"E14.21.3"),sQuery(id+"F0.wireOp",EDGE,"E14.21.4"),sQuery(id+"F0.wireOp",EDGE,"E14.21.5"),sQuery(id+"F0.wireOp",EDGE,"E14.21.6"),sQuery(id+"F0.wireOp",EDGE,"E14.21.7"),sQuery(id+"F0.wireOp",EDGE,"E14.21.8"),sQuery(id+"F0.wireOp",EDGE,"E14.21.9"),sQuery(id+"F0.wireOp",EDGE,"E14.22.0"),sQuery(id+"F0.wireOp",EDGE,"E14.22.1"),sQuery(id+"F0.wireOp",EDGE,"E14.22.2"),sQuery(id+"F0.wireOp",EDGE,"E14.22.3"),sQuery(id+"F0.wireOp",EDGE,"E14.22.4"),sQuery(id+"F0.wireOp",EDGE,"E14.22.5"),sQuery(id+"F0.wireOp",EDGE,"E14.22.6"),sQuery(id+"F0.wireOp",EDGE,"E14.22.7"),sQuery(id+"F0.wireOp",EDGE,"E14.22.8"),sQuery(id+"F0.wireOp",EDGE,"E14.22.9"),sQuery(id+"F0.wireOp",EDGE,"E14.23.0"),sQuery(id+"F0.wireOp",EDGE,"E14.23.1"),sQuery(id+"F0.wireOp",EDGE,"E14.23.2"),sQuery(id+"F0.wireOp",EDGE,"E14.23.3"),sQuery(id+"F0.wireOp",EDGE,"E14.23.4"),sQuery(id+"F0.wireOp",EDGE,"E14.23.5"),sQuery(id+"F0.wireOp",EDGE,"E14.23.6"),sQuery(id+"F0.wireOp",EDGE,"E14.23.7"),sQuery(id+"F0.wireOp",EDGE,"E14.23.8"),sQuery(id+"F0.wireOp",EDGE,"E14.23.9"),sQuery(id+"F0.wireOp",EDGE,"E14.24.0"),sQuery(id+"F0.wireOp",EDGE,"E14.24.1"),sQuery(id+"F0.wireOp",EDGE,"E14.24.2"),sQuery(id+"F0.wireOp",EDGE,"E14.24.3"),sQuery(id+"F0.wireOp",EDGE,"E14.24.4"),sQuery(id+"F0.wireOp",EDGE,"E14.24.5"),sQuery(id+"F0.wireOp",EDGE,"E14.24.6"),sQuery(id+"F0.wireOp",EDGE,"E14.24.7"),sQuery(id+"F0.wireOp",EDGE,"E14.24.8"),sQuery(id+"F0.wireOp",EDGE,"E14.24.9"),sQuery(id+"F0.wireOp",EDGE,"E14.25.0"),sQuery(id+"F0.wireOp",EDGE,"E14.25.1"),sQuery(id+"F0.wireOp",EDGE,"E14.25.2"),sQuery(id+"F0.wireOp",EDGE,"E14.25.3"),sQuery(id+"F0.wireOp",EDGE,"E14.25.4"),sQuery(id+"F0.wireOp",EDGE,"E14.25.5"),sQuery(id+"F0.wireOp",EDGE,"E14.25.6"),sQuery(id+"F0.wireOp",EDGE,"E14.25.7"),sQuery(id+"F0.wireOp",EDGE,"E14.25.8"),sQuery(id+"F0.wireOp",EDGE,"E14.25.9"),sQuery(id+"F0.wireOp",EDGE,"E14.26.0"),sQuery(id+"F0.wireOp",EDGE,"E14.26.1"),sQuery(id+"F0.wireOp",EDGE,"E14.26.2"),sQuery(id+"F0.wireOp",EDGE,"E14.26.3"),sQuery(id+"F0.wireOp",EDGE,"E14.26.4"),sQuery(id+"F0.wireOp",EDGE,"E14.26.5"),sQuery(id+"F0.wireOp",EDGE,"E14.26.6"),sQuery(id+"F0.wireOp",EDGE,"E14.26.7"),sQuery(id+"F0.wireOp",EDGE,"E14.26.8"),sQuery(id+"F0.wireOp",EDGE,"E14.26.9"),sQuery(id+"F0.wireOp",EDGE,"E14.27.0"),sQuery(id+"F0.wireOp",EDGE,"E14.27.1"),sQuery(id+"F0.wireOp",EDGE,"E14.27.2"),sQuery(id+"F0.wireOp",EDGE,"E14.27.3"),sQuery(id+"F0.wireOp",EDGE,"E14.27.4"),sQuery(id+"F0.wireOp",EDGE,"E14.27.5"),sQuery(id+"F0.wireOp",EDGE,"E14.27.6"),sQuery(id+"F0.wireOp",EDGE,"E14.27.7"),sQuery(id+"F0.wireOp",EDGE,"E14.27.8"),sQuery(id+"F0.wireOp",EDGE,"E14.27.9"),sQuery(id+"F0.wireOp",EDGE,"E14.28.0"),sQuery(id+"F0.wireOp",EDGE,"E14.28.1"),sQuery(id+"F0.wireOp",EDGE,"E14.28.2"),sQuery(id+"F0.wireOp",EDGE,"E14.28.3"),sQuery(id+"F0.wireOp",EDGE,"E14.28.4"),sQuery(id+"F0.wireOp",EDGE,"E14.28.5"),sQuery(id+"F0.wireOp",EDGE,"E14.28.6"),sQuery(id+"F0.wireOp",EDGE,"E14.28.7"),sQuery(id+"F0.wireOp",EDGE,"E14.28.8"),sQuery(id+"F0.wireOp",EDGE,"E14.28.9"),sQuery(id+"F0.wireOp",EDGE,"E14.29.0"),sQuery(id+"F0.wireOp",EDGE,"E14.29.1"),sQuery(id+"F0.wireOp",EDGE,"E14.29.2"),sQuery(id+"F0.wireOp",EDGE,"E14.29.3"),sQuery(id+"F0.wireOp",EDGE,"E14.29.4"),sQuery(id+"F0.wireOp",EDGE,"E14.29.5"),sQuery(id+"F0.wireOp",EDGE,"E14.29.6"),sQuery(id+"F0.wireOp",EDGE,"E14.29.7"),sQuery(id+"F0.wireOp",EDGE,"E14.29.8"),sQuery(id+"F0.wireOp",EDGE,"E14.29.9"),sQuery(id+"F0.wireOp",EDGE,"E14.30.0"),sQuery(id+"F0.wireOp",EDGE,"E14.30.1"),sQuery(id+"F0.wireOp",EDGE,"E14.30.2"),sQuery(id+"F0.wireOp",EDGE,"E14.30.3"),sQuery(id+"F0.wireOp",EDGE,"E14.30.4"),sQuery(id+"F0.wireOp",EDGE,"E14.30.5"),sQuery(id+"F0.wireOp",EDGE,"E14.30.6"),sQuery(id+"F0.wireOp",EDGE,"E14.30.7"),sQuery(id+"F0.wireOp",EDGE,"E14.30.8"),sQuery(id+"F0.wireOp",EDGE,"E14.30.9"),sQuery(id+"F0.wireOp",EDGE,"E14.31.0"),sQuery(id+"F0.wireOp",EDGE,"E14.31.1"),sQuery(id+"F0.wireOp",EDGE,"E14.31.2"),sQuery(id+"F0.wireOp",EDGE,"E14.31.3"),sQuery(id+"F0.wireOp",EDGE,"E14.31.4"),sQuery(id+"F0.wireOp",EDGE,"E14.31.5"),sQuery(id+"F0.wireOp",EDGE,"E14.31.6"),sQuery(id+"F0.wireOp",EDGE,"E14.31.7"),sQuery(id+"F0.wireOp",EDGE,"E14.31.8"),sQuery(id+"F0.wireOp",EDGE,"E14.31.9"),sQuery(id+"F0.wireOp",EDGE,"E14.32.0"),sQuery(id+"F0.wireOp",EDGE,"E14.32.1"),sQuery(id+"F0.wireOp",EDGE,"E14.32.2"),sQuery(id+"F0.wireOp",EDGE,"E14.32.3"),sQuery(id+"F0.wireOp",EDGE,"E14.32.4"),sQuery(id+"F0.wireOp",EDGE,"E14.32.5"),sQuery(id+"F0.wireOp",EDGE,"E14.32.6"),sQuery(id+"F0.wireOp",EDGE,"E14.32.7"),sQuery(id+"F0.wireOp",EDGE,"E14.32.8"),sQuery(id+"F0.wireOp",EDGE,"E14.32.9"),sQuery(id+"F0.wireOp",EDGE,"E14.33.0"),sQuery(id+"F0.wireOp",EDGE,"E14.33.1"),sQuery(id+"F0.wireOp",EDGE,"E14.33.2"),sQuery(id+"F0.wireOp",EDGE,"E14.33.3"),sQuery(id+"F0.wireOp",EDGE,"E14.33.4"),sQuery(id+"F0.wireOp",EDGE,"E14.33.5"),sQuery(id+"F0.wireOp",EDGE,"E14.33.6"),sQuery(id+"F0.wireOp",EDGE,"E14.33.7"),sQuery(id+"F0.wireOp",EDGE,"E14.33.8"),sQuery(id+"F0.wireOp",EDGE,"E14.33.9"),sQuery(id+"F0.wireOp",EDGE,"E14.34.0"),sQuery(id+"F0.wireOp",EDGE,"E14.34.1"),sQuery(id+"F0.wireOp",EDGE,"E14.34.2"),sQuery(id+"F0.wireOp",EDGE,"E14.34.3"),sQuery(id+"F0.wireOp",EDGE,"E14.34.4"),sQuery(id+"F0.wireOp",EDGE,"E14.34.5"),sQuery(id+"F0.wireOp",EDGE,"E14.34.6"),sQuery(id+"F0.wireOp",EDGE,"E14.34.7"),sQuery(id+"F0.wireOp",EDGE,"E14.34.8"),sQuery(id+"F0.wireOp",EDGE,"E14.34.9"),sQuery(id+"F0.wireOp",EDGE,"E14.35.0"),sQuery(id+"F0.wireOp",EDGE,"E14.35.1"),sQuery(id+"F0.wireOp",EDGE,"E14.35.2"),sQuery(id+"F0.wireOp",EDGE,"E14.35.3"),sQuery(id+"F0.wireOp",EDGE,"E14.35.4"),sQuery(id+"F0.wireOp",EDGE,"E14.35.5"),sQuery(id+"F0.wireOp",EDGE,"E14.35.6"),sQuery(id+"F0.wireOp",EDGE,"E14.35.7"),sQuery(id+"F0.wireOp",EDGE,"E14.35.8"),sQuery(id+"F0.wireOp",EDGE,"E14.35.9"),sQuery(id+"F0.wireOp",EDGE,"E14.36.0"),sQuery(id+"F0.wireOp",EDGE,"E14.36.1"),sQuery(id+"F0.wireOp",EDGE,"E14.36.2"),sQuery(id+"F0.wireOp",EDGE,"E14.36.3"),sQuery(id+"F0.wireOp",EDGE,"E14.36.4"),sQuery(id+"F0.wireOp",EDGE,"E14.36.5"),sQuery(id+"F0.wireOp",EDGE,"E14.36.6"),sQuery(id+"F0.wireOp",EDGE,"E14.36.7"),sQuery(id+"F0.wireOp",EDGE,"E14.36.8"),sQuery(id+"F0.wireOp",EDGE,"E14.36.9"),sQuery(id+"F0.wireOp",EDGE,"E14.37.0"),sQuery(id+"F0.wireOp",EDGE,"E14.37.1"),sQuery(id+"F0.wireOp",EDGE,"E14.37.2"),sQuery(id+"F0.wireOp",EDGE,"E14.37.3"),sQuery(id+"F0.wireOp",EDGE,"E14.37.4"),sQuery(id+"F0.wireOp",EDGE,"E14.37.5"),sQuery(id+"F0.wireOp",EDGE,"E14.37.6"),sQuery(id+"F0.wireOp",EDGE,"E14.37.7"),sQuery(id+"F0.wireOp",EDGE,"E14.37.8"),sQuery(id+"F0.wireOp",EDGE,"E14.37.9"),sQuery(id+"F0.wireOp",EDGE,"E14.38.0"),sQuery(id+"F0.wireOp",EDGE,"E14.38.1"),sQuery(id+"F0.wireOp",EDGE,"E14.38.2"),sQuery(id+"F0.wireOp",EDGE,"E14.38.3"),sQuery(id+"F0.wireOp",EDGE,"E14.38.4"),sQuery(id+"F0.wireOp",EDGE,"E14.38.5"),sQuery(id+"F0.wireOp",EDGE,"E14.38.6"),sQuery(id+"F0.wireOp",EDGE,"E14.38.7"),sQuery(id+"F0.wireOp",EDGE,"E14.38.8"),sQuery(id+"F0.wireOp",EDGE,"E14.38.9"),sQuery(id+"F0.wireOp",EDGE,"E14.39.0"),sQuery(id+"F0.wireOp",EDGE,"E14.39.1"),sQuery(id+"F0.wireOp",EDGE,"E14.39.2"),sQuery(id+"F0.wireOp",EDGE,"E14.39.3"),sQuery(id+"F0.wireOp",EDGE,"E14.39.4"),sQuery(id+"F0.wireOp",EDGE,"E14.39.5"),sQuery(id+"F0.wireOp",EDGE,"E14.39.6"),sQuery(id+"F0.wireOp",EDGE,"E14.39.7"),sQuery(id+"F0.wireOp",EDGE,"E14.39.8"),sQuery(id+"F0.wireOp",EDGE,"E14.39.9"),sQuery(id+"F0.wireOp",EDGE,"E14.40.0"),sQuery(id+"F0.wireOp",EDGE,"E14.40.1"),sQuery(id+"F0.wireOp",EDGE,"E14.40.2"),sQuery(id+"F0.wireOp",EDGE,"E14.40.3"),sQuery(id+"F0.wireOp",EDGE,"E14.40.4"),sQuery(id+"F0.wireOp",EDGE,"E14.40.5"),sQuery(id+"F0.wireOp",EDGE,"E14.40.6"),sQuery(id+"F0.wireOp",EDGE,"E14.40.7"),sQuery(id+"F0.wireOp",EDGE,"E14.40.8"),sQuery(id+"F0.wireOp",EDGE,"E14.40.9"),sQuery(id+"F0.wireOp",EDGE,"E14.41.0"),sQuery(id+"F0.wireOp",EDGE,"E14.41.1"),sQuery(id+"F0.wireOp",EDGE,"E14.41.2"),sQuery(id+"F0.wireOp",EDGE,"E14.41.3"),sQuery(id+"F0.wireOp",EDGE,"E14.41.4"),sQuery(id+"F0.wireOp",EDGE,"E14.41.5"),sQuery(id+"F0.wireOp",EDGE,"E14.41.6"),sQuery(id+"F0.wireOp",EDGE,"E14.41.7"),sQuery(id+"F0.wireOp",EDGE,"E14.41.8"),sQuery(id+"F0.wireOp",EDGE,"E14.41.9"),sQuery(id+"F0.wireOp",EDGE,"E14.42.0"),sQuery(id+"F0.wireOp",EDGE,"E14.42.1"),sQuery(id+"F0.wireOp",EDGE,"E14.42.2"),sQuery(id+"F0.wireOp",EDGE,"E14.42.3"),sQuery(id+"F0.wireOp",EDGE,"E14.42.4"),sQuery(id+"F0.wireOp",EDGE,"E14.42.5"),sQuery(id+"F0.wireOp",EDGE,"E14.42.6"),sQuery(id+"F0.wireOp",EDGE,"E14.42.7"),sQuery(id+"F0.wireOp",EDGE,"E14.42.8"),sQuery(id+"F0.wireOp",EDGE,"E14.42.9"),sQuery(id+"F0.wireOp",EDGE,"E14.43.0"),sQuery(id+"F0.wireOp",EDGE,"E14.43.1"),sQuery(id+"F0.wireOp",EDGE,"E14.43.2"),sQuery(id+"F0.wireOp",EDGE,"E14.43.3"),sQuery(id+"F0.wireOp",EDGE,"E14.43.4"),sQuery(id+"F0.wireOp",EDGE,"E14.43.5"),sQuery(id+"F0.wireOp",EDGE,"E14.43.6"),sQuery(id+"F0.wireOp",EDGE,"E14.43.7"),sQuery(id+"F0.wireOp",EDGE,"E14.43.8"),sQuery(id+"F0.wireOp",EDGE,"E14.43.9"),sQuery(id+"F0.wireOp",EDGE,"E14.44.0"),sQuery(id+"F0.wireOp",EDGE,"E14.44.1"),sQuery(id+"F0.wireOp",EDGE,"E14.44.2"),sQuery(id+"F0.wireOp",EDGE,"E14.44.3"),sQuery(id+"F0.wireOp",EDGE,"E14.44.4"),sQuery(id+"F0.wireOp",EDGE,"E14.44.5"),sQuery(id+"F0.wireOp",EDGE,"E14.44.6"),sQuery(id+"F0.wireOp",EDGE,"E14.44.7"),sQuery(id+"F0.wireOp",EDGE,"E14.44.8"),sQuery(id+"F0.wireOp",EDGE,"E14.44.9"),sQuery(id+"F0.wireOp",EDGE,"E14.45.0"),sQuery(id+"F0.wireOp",EDGE,"E14.45.1"),sQuery(id+"F0.wireOp",EDGE,"E14.45.2"),sQuery(id+"F0.wireOp",EDGE,"E14.45.3"),sQuery(id+"F0.wireOp",EDGE,"E14.45.4"),sQuery(id+"F0.wireOp",EDGE,"E14.45.5"),sQuery(id+"F0.wireOp",EDGE,"E14.45.6"),sQuery(id+"F0.wireOp",EDGE,"E14.45.7"),sQuery(id+"F0.wireOp",EDGE,"E14.45.8"),sQuery(id+"F0.wireOp",EDGE,"E14.45.9"),sQuery(id+"F0.wireOp",EDGE,"E14.46.0"),sQuery(id+"F0.wireOp",EDGE,"E14.46.1"),sQuery(id+"F0.wireOp",EDGE,"E14.46.2"),sQuery(id+"F0.wireOp",EDGE,"E14.46.3"),sQuery(id+"F0.wireOp",EDGE,"E14.46.4"),sQuery(id+"F0.wireOp",EDGE,"E14.46.5"),sQuery(id+"F0.wireOp",EDGE,"E14.46.6"),sQuery(id+"F0.wireOp",EDGE,"E14.46.7"),sQuery(id+"F0.wireOp",EDGE,"E14.46.8"),sQuery(id+"F0.wireOp",EDGE,"E14.46.9"),sQuery(id+"F0.wireOp",EDGE,"E14.47.0"),sQuery(id+"F0.wireOp",EDGE,"E14.47.1"),sQuery(id+"F0.wireOp",EDGE,"E14.47.2"),sQuery(id+"F0.wireOp",EDGE,"E14.47.3"),sQuery(id+"F0.wireOp",EDGE,"E14.47.4"),sQuery(id+"F0.wireOp",EDGE,"E14.47.5"),sQuery(id+"F0.wireOp",EDGE,"E14.47.6"),sQuery(id+"F0.wireOp",EDGE,"E14.47.7"),sQuery(id+"F0.wireOp",EDGE,"E14.47.8"),sQuery(id+"F0.wireOp",EDGE,"E14.47.9"),sQuery(id+"F0.wireOp",EDGE,"E14.48.0"),sQuery(id+"F0.wireOp",EDGE,"E14.48.1"),sQuery(id+"F0.wireOp",EDGE,"E14.48.2"),sQuery(id+"F0.wireOp",EDGE,"E14.48.3"),sQuery(id+"F0.wireOp",EDGE,"E14.48.4"),sQuery(id+"F0.wireOp",EDGE,"E14.48.5"),sQuery(id+"F0.wireOp",EDGE,"E14.48.6"),sQuery(id+"F0.wireOp",EDGE,"E14.48.7"),sQuery(id+"F0.wireOp",EDGE,"E14.48.8"),sQuery(id+"F0.wireOp",EDGE,"E14.48.9"),sQuery(id+"F0.wireOp",EDGE,"E14.49.0"),sQuery(id+"F0.wireOp",EDGE,"E14.49.1"),sQuery(id+"F0.wireOp",EDGE,"E14.49.2"),sQuery(id+"F0.wireOp",EDGE,"E14.49.3"),sQuery(id+"F0.wireOp",EDGE,"E14.49.4"),sQuery(id+"F0.wireOp",EDGE,"E14.49.5"),sQuery(id+"F0.wireOp",EDGE,"E14.49.6"),sQuery(id+"F0.wireOp",EDGE,"E14.49.7"),sQuery(id+"F0.wireOp",EDGE,"E14.49.8"),sQuery(id+"F0.wireOp",EDGE,"E14.49.9"),sQuery(id+"F0.wireOp",EDGE,"E14.50.0"),sQuery(id+"F0.wireOp",EDGE,"E14.50.1"),sQuery(id+"F0.wireOp",EDGE,"E14.50.2"),sQuery(id+"F0.wireOp",EDGE,"E14.50.3"),sQuery(id+"F0.wireOp",EDGE,"E14.50.4"),sQuery(id+"F0.wireOp",EDGE,"E14.50.5"),sQuery(id+"F0.wireOp",EDGE,"E14.50.6"),sQuery(id+"F0.wireOp",EDGE,"E14.50.7"),sQuery(id+"F0.wireOp",EDGE,"E14.50.8"),sQuery(id+"F0.wireOp",EDGE,"E14.50.9"),sQuery(id+"F0.wireOp",EDGE,"E14.51.0"),sQuery(id+"F0.wireOp",EDGE,"E14.51.1"),sQuery(id+"F0.wireOp",EDGE,"E14.51.2"),sQuery(id+"F0.wireOp",EDGE,"E14.51.3"),sQuery(id+"F0.wireOp",EDGE,"E14.51.4"),sQuery(id+"F0.wireOp",EDGE,"E14.51.5"),sQuery(id+"F0.wireOp",EDGE,"E14.51.6"),sQuery(id+"F0.wireOp",EDGE,"E14.51.7"),sQuery(id+"F0.wireOp",EDGE,"E14.51.8"),sQuery(id+"F0.wireOp",EDGE,"E14.51.9"),sQuery(id+"F0.wireOp",EDGE,"E14.52.0"),sQuery(id+"F0.wireOp",EDGE,"E14.52.1"),sQuery(id+"F0.wireOp",EDGE,"E14.52.2"),sQuery(id+"F0.wireOp",EDGE,"E14.52.3"),sQuery(id+"F0.wireOp",EDGE,"E14.52.4"),sQuery(id+"F0.wireOp",EDGE,"E14.52.5"),sQuery(id+"F0.wireOp",EDGE,"E14.52.6"),sQuery(id+"F0.wireOp",EDGE,"E14.52.7"),sQuery(id+"F0.wireOp",EDGE,"E14.52.8"),sQuery(id+"F0.wireOp",EDGE,"E14.52.9"),sQuery(id+"F0.wireOp",EDGE,"E14.53.0"),sQuery(id+"F0.wireOp",EDGE,"E14.53.1"),sQuery(id+"F0.wireOp",EDGE,"E14.53.2"),sQuery(id+"F0.wireOp",EDGE,"E14.53.3"),sQuery(id+"F0.wireOp",EDGE,"E14.53.4"),sQuery(id+"F0.wireOp",EDGE,"E14.53.5"),sQuery(id+"F0.wireOp",EDGE,"E14.53.6"),sQuery(id+"F0.wireOp",EDGE,"E14.53.7"),sQuery(id+"F0.wireOp",EDGE,"E14.53.8"),sQuery(id+"F0.wireOp",EDGE,"E14.53.9"),sQuery(id+"F0.wireOp",EDGE,"E14.54.0"),sQuery(id+"F0.wireOp",EDGE,"E14.54.1"),sQuery(id+"F0.wireOp",EDGE,"E14.54.2"),sQuery(id+"F0.wireOp",EDGE,"E14.54.3"),sQuery(id+"F0.wireOp",EDGE,"E14.54.4"),sQuery(id+"F0.wireOp",EDGE,"E14.54.5"),sQuery(id+"F0.wireOp",EDGE,"E14.54.6"),sQuery(id+"F0.wireOp",EDGE,"E14.54.7"),sQuery(id+"F0.wireOp",EDGE,"E14.54.8"),sQuery(id+"F0.wireOp",EDGE,"E14.54.9"),sQuery(id+"F0.wireOp",EDGE,"E14.55.0"),sQuery(id+"F0.wireOp",EDGE,"E14.55.1"),sQuery(id+"F0.wireOp",EDGE,"E14.55.2"),sQuery(id+"F0.wireOp",EDGE,"E14.55.3"),sQuery(id+"F0.wireOp",EDGE,"E14.55.4"),sQuery(id+"F0.wireOp",EDGE,"E14.55.5"),sQuery(id+"F0.wireOp",EDGE,"E14.55.6"),sQuery(id+"F0.wireOp",EDGE,"E14.55.7"),sQuery(id+"F0.wireOp",EDGE,"E14.55.8"),sQuery(id+"F0.wireOp",EDGE,"E14.55.9"),sQuery(id+"F0.wireOp",EDGE,"E14.56.0"),sQuery(id+"F0.wireOp",EDGE,"E14.56.1"),sQuery(id+"F0.wireOp",EDGE,"E14.56.2"),sQuery(id+"F0.wireOp",EDGE,"E14.56.3"),sQuery(id+"F0.wireOp",EDGE,"E14.56.4"),sQuery(id+"F0.wireOp",EDGE,"E14.56.5"),sQuery(id+"F0.wireOp",EDGE,"E14.56.6"),sQuery(id+"F0.wireOp",EDGE,"E14.56.7"),sQuery(id+"F0.wireOp",EDGE,"E14.56.8"),sQuery(id+"F0.wireOp",EDGE,"E14.56.9"),sQuery(id+"F0.wireOp",EDGE,"E14.57.0"),sQuery(id+"F0.wireOp",EDGE,"E14.57.1"),sQuery(id+"F0.wireOp",EDGE,"E14.57.2"),sQuery(id+"F0.wireOp",EDGE,"E14.57.3"),sQuery(id+"F0.wireOp",EDGE,"E14.57.4"),sQuery(id+"F0.wireOp",EDGE,"E14.57.5"),sQuery(id+"F0.wireOp",EDGE,"E14.57.6"),sQuery(id+"F0.wireOp",EDGE,"E14.57.7"),sQuery(id+"F0.wireOp",EDGE,"E14.57.8"),sQuery(id+"F0.wireOp",EDGE,"E14.57.9"),sQuery(id+"F0.wireOp",EDGE,"E14.58.0"),sQuery(id+"F0.wireOp",EDGE,"E14.58.1"),sQuery(id+"F0.wireOp",EDGE,"E14.58.2"),sQuery(id+"F0.wireOp",EDGE,"E14.58.3"),sQuery(id+"F0.wireOp",EDGE,"E14.58.4"),sQuery(id+"F0.wireOp",EDGE,"E14.58.5"),sQuery(id+"F0.wireOp",EDGE,"E14.58.6"),sQuery(id+"F0.wireOp",EDGE,"E14.58.7"),sQuery(id+"F0.wireOp",EDGE,"E14.58.8"),sQuery(id+"F0.wireOp",EDGE,"E14.58.9"),sQuery(id+"F0.wireOp",EDGE,"E14.59.0"),sQuery(id+"F0.wireOp",EDGE,"E14.59.1"),sQuery(id+"F0.wireOp",EDGE,"E14.59.2"),sQuery(id+"F0.wireOp",EDGE,"E14.59.3"),sQuery(id+"F0.wireOp",EDGE,"E14.59.4"),sQuery(id+"F0.wireOp",EDGE,"E14.59.5"),sQuery(id+"F0.wireOp",EDGE,"E14.59.6"),sQuery(id+"F0.wireOp",EDGE,"E14.59.7"),sQuery(id+"F0.wireOp",EDGE,"E14.59.8"),sQuery(id+"F0.wireOp",EDGE,"E14.59.9"),sQuery(id+"F0.wireOp",EDGE,"E14.60.0"),sQuery(id+"F0.wireOp",EDGE,"E14.60.1"),sQuery(id+"F0.wireOp",EDGE,"E14.60.2"),sQuery(id+"F0.wireOp",EDGE,"E14.60.3"),sQuery(id+"F0.wireOp",EDGE,"E14.60.4"),sQuery(id+"F0.wireOp",EDGE,"E14.60.5"),sQuery(id+"F0.wireOp",EDGE,"E14.60.6"),sQuery(id+"F0.wireOp",EDGE,"E14.60.7"),sQuery(id+"F0.wireOp",EDGE,"E14.60.8"),sQuery(id+"F0.wireOp",EDGE,"E14.60.9"),sQuery(id+"F0.wireOp",EDGE,"E14.61.0"),sQuery(id+"F0.wireOp",EDGE,"E14.61.1"),sQuery(id+"F0.wireOp",EDGE,"E14.61.2"),sQuery(id+"F0.wireOp",EDGE,"E14.61.3"),sQuery(id+"F0.wireOp",EDGE,"E14.61.4"),sQuery(id+"F0.wireOp",EDGE,"E14.61.5"),sQuery(id+"F0.wireOp",EDGE,"E14.61.6"),sQuery(id+"F0.wireOp",EDGE,"E14.61.7"),sQuery(id+"F0.wireOp",EDGE,"E14.61.8"),sQuery(id+"F0.wireOp",EDGE,"E14.61.9"),sQuery(id+"F0.wireOp",EDGE,"E14.62.0"),sQuery(id+"F0.wireOp",EDGE,"E14.62.1"),sQuery(id+"F0.wireOp",EDGE,"E14.62.2"),sQuery(id+"F0.wireOp",EDGE,"E14.62.3"),sQuery(id+"F0.wireOp",EDGE,"E14.62.4"),sQuery(id+"F0.wireOp",EDGE,"E14.62.5"),sQuery(id+"F0.wireOp",EDGE,"E14.62.6"),sQuery(id+"F0.wireOp",EDGE,"E14.62.7"),sQuery(id+"F0.wireOp",EDGE,"E14.62.8"),sQuery(id+"F0.wireOp",EDGE,"E14.62.9"),sQuery(id+"F0.wireOp",EDGE,"E14.63.0"),sQuery(id+"F0.wireOp",EDGE,"E14.63.1"),sQuery(id+"F0.wireOp",EDGE,"E14.63.2"),sQuery(id+"F0.wireOp",EDGE,"E14.63.3"),sQuery(id+"F0.wireOp",EDGE,"E14.63.4"),sQuery(id+"F0.wireOp",EDGE,"E14.63.5"),sQuery(id+"F0.wireOp",EDGE,"E14.63.6"),sQuery(id+"F0.wireOp",EDGE,"E14.63.7"),sQuery(id+"F0.wireOp",EDGE,"E14.63.8"),sQuery(id+"F0.wireOp",EDGE,"E14.63.9"),sQuery(id+"F0.wireOp",EDGE,"E14.64.0"),sQuery(id+"F0.wireOp",EDGE,"E14.64.1"),sQuery(id+"F0.wireOp",EDGE,"E14.64.2"),sQuery(id+"F0.wireOp",EDGE,"E14.64.3"),sQuery(id+"F0.wireOp",EDGE,"E14.64.4"),sQuery(id+"F0.wireOp",EDGE,"E14.64.5"),sQuery(id+"F0.wireOp",EDGE,"E14.64.6"),sQuery(id+"F0.wireOp",EDGE,"E14.64.7"),sQuery(id+"F0.wireOp",EDGE,"E14.64.8"),sQuery(id+"F0.wireOp",EDGE,"E14.64.9"),sQuery(id+"F0.wireOp",EDGE,"E14.65.0"),sQuery(id+"F0.wireOp",EDGE,"E14.65.1"),sQuery(id+"F0.wireOp",EDGE,"E14.65.2"),sQuery(id+"F0.wireOp",EDGE,"E14.65.3"),sQuery(id+"F0.wireOp",EDGE,"E14.65.4"),sQuery(id+"F0.wireOp",EDGE,"E14.65.5"),sQuery(id+"F0.wireOp",EDGE,"E14.65.6"),sQuery(id+"F0.wireOp",EDGE,"E14.65.7"),sQuery(id+"F0.wireOp",EDGE,"E14.65.8"),sQuery(id+"F0.wireOp",EDGE,"E14.65.9"),sQuery(id+"F0.wireOp",EDGE,"E14.66.0"),sQuery(id+"F0.wireOp",EDGE,"E14.66.1"),sQuery(id+"F0.wireOp",EDGE,"E14.66.2"),sQuery(id+"F0.wireOp",EDGE,"E14.66.3"),sQuery(id+"F0.wireOp",EDGE,"E14.66.4"),sQuery(id+"F0.wireOp",EDGE,"E14.66.5"),sQuery(id+"F0.wireOp",EDGE,"E14.66.6"),sQuery(id+"F0.wireOp",EDGE,"E14.66.7"),sQuery(id+"F0.wireOp",EDGE,"E14.66.8"),sQuery(id+"F0.wireOp",EDGE,"E14.66.9"),sQuery(id+"F0.wireOp",EDGE,"E14.67.0"),sQuery(id+"F0.wireOp",EDGE,"E14.67.1"),sQuery(id+"F0.wireOp",EDGE,"E14.67.2"),sQuery(id+"F0.wireOp",EDGE,"E14.67.3"),sQuery(id+"F0.wireOp",EDGE,"E14.67.4"),sQuery(id+"F0.wireOp",EDGE,"E14.67.5"),sQuery(id+"F0.wireOp",EDGE,"E14.67.6"),sQuery(id+"F0.wireOp",EDGE,"E14.67.7"),sQuery(id+"F0.wireOp",EDGE,"E14.67.8"),sQuery(id+"F0.wireOp",EDGE,"E14.67.9"),sQuery(id+"F0.wireOp",EDGE,"E14.68.0"),sQuery(id+"F0.wireOp",EDGE,"E14.68.1"),sQuery(id+"F0.wireOp",EDGE,"E14.68.2"),sQuery(id+"F0.wireOp",EDGE,"E14.68.3"),sQuery(id+"F0.wireOp",EDGE,"E14.68.4"),sQuery(id+"F0.wireOp",EDGE,"E14.68.5"),sQuery(id+"F0.wireOp",EDGE,"E14.68.6"),sQuery(id+"F0.wireOp",EDGE,"E14.68.7"),sQuery(id+"F0.wireOp",EDGE,"E14.68.8"),sQuery(id+"F0.wireOp",EDGE,"E14.68.9"),sQuery(id+"F0.wireOp",EDGE,"E14.69.0"),sQuery(id+"F0.wireOp",EDGE,"E14.69.1"),sQuery(id+"F0.wireOp",EDGE,"E14.69.2"),sQuery(id+"F0.wireOp",EDGE,"E14.69.3"),sQuery(id+"F0.wireOp",EDGE,"E14.69.4"),sQuery(id+"F0.wireOp",EDGE,"E14.69.5"),sQuery(id+"F0.wireOp",EDGE,"E14.69.6"),sQuery(id+"F0.wireOp",EDGE,"E14.69.7"),sQuery(id+"F0.wireOp",EDGE,"E14.69.8"),sQuery(id+"F0.wireOp",EDGE,"E14.69.9"),sQuery(id+"F0.wireOp",EDGE,"E14.70.0"),sQuery(id+"F0.wireOp",EDGE,"E14.70.1"),sQuery(id+"F0.wireOp",EDGE,"E14.70.2"),sQuery(id+"F0.wireOp",EDGE,"E14.70.3"),sQuery(id+"F0.wireOp",EDGE,"E14.70.4"),sQuery(id+"F0.wireOp",EDGE,"E14.70.5"),sQuery(id+"F0.wireOp",EDGE,"E14.70.6"),sQuery(id+"F0.wireOp",EDGE,"E14.70.7"),sQuery(id+"F0.wireOp",EDGE,"E14.70.8"),sQuery(id+"F0.wireOp",EDGE,"E14.70.9"),sQuery(id+"F0.wireOp",EDGE,"E14.71.0"),sQuery(id+"F0.wireOp",EDGE,"E14.71.1"),sQuery(id+"F0.wireOp",EDGE,"E14.71.2"),sQuery(id+"F0.wireOp",EDGE,"E14.71.3"),sQuery(id+"F0.wireOp",EDGE,"E14.71.4"),sQuery(id+"F0.wireOp",EDGE,"E14.71.5"),sQuery(id+"F0.wireOp",EDGE,"E14.71.6"),sQuery(id+"F0.wireOp",EDGE,"E14.71.7"),sQuery(id+"F0.wireOp",EDGE,"E14.71.8"),sQuery(id+"F0.wireOp",EDGE,"E14.71.9"),sQuery(id+"F0.wireOp",EDGE,"E14.72.0"),sQuery(id+"F0.wireOp",EDGE,"E14.72.1"),sQuery(id+"F0.wireOp",EDGE,"E14.72.2"),sQuery(id+"F0.wireOp",EDGE,"E14.72.3"),sQuery(id+"F0.wireOp",EDGE,"E14.72.4"),sQuery(id+"F0.wireOp",EDGE,"E14.72.5"),sQuery(id+"F0.wireOp",EDGE,"E14.72.6"),sQuery(id+"F0.wireOp",EDGE,"E14.72.7"),sQuery(id+"F0.wireOp",EDGE,"E14.72.8"),sQuery(id+"F0.wireOp",EDGE,"E14.72.9"),sQuery(id+"F0.wireOp",EDGE,"E14.73.0"),sQuery(id+"F0.wireOp",EDGE,"E14.73.1"),sQuery(id+"F0.wireOp",EDGE,"E14.73.2"),sQuery(id+"F0.wireOp",EDGE,"E14.73.3"),sQuery(id+"F0.wireOp",EDGE,"E14.73.4"),sQuery(id+"F0.wireOp",EDGE,"E14.73.5"),sQuery(id+"F0.wireOp",EDGE,"E14.73.6"),sQuery(id+"F0.wireOp",EDGE,"E14.73.7"),sQuery(id+"F0.wireOp",EDGE,"E14.73.8"),sQuery(id+"F0.wireOp",EDGE,"E14.73.9"),sQuery(id+"F0.wireOp",EDGE,"E14.74.0"),sQuery(id+"F0.wireOp",EDGE,"E14.74.1"),sQuery(id+"F0.wireOp",EDGE,"E14.74.2"),sQuery(id+"F0.wireOp",EDGE,"E14.74.3"),sQuery(id+"F0.wireOp",EDGE,"E14.74.4"),sQuery(id+"F0.wireOp",EDGE,"E14.74.5"),sQuery(id+"F0.wireOp",EDGE,"E14.74.6"),sQuery(id+"F0.wireOp",EDGE,"E14.74.7"),sQuery(id+"F0.wireOp",EDGE,"E14.74.8"),sQuery(id+"F0.wireOp",EDGE,"E14.74.9"),sQuery(id+"F0.wireOp",EDGE,"E14.75.0"),sQuery(id+"F0.wireOp",EDGE,"E14.75.1"),sQuery(id+"F0.wireOp",EDGE,"E14.75.2"),sQuery(id+"F0.wireOp",EDGE,"E14.75.3"),sQuery(id+"F0.wireOp",EDGE,"E14.75.4"),sQuery(id+"F0.wireOp",EDGE,"E14.75.5"),sQuery(id+"F0.wireOp",EDGE,"E14.75.6"),sQuery(id+"F0.wireOp",EDGE,"E14.75.7"),sQuery(id+"F0.wireOp",EDGE,"E14.75.8"),sQuery(id+"F0.wireOp",EDGE,"E14.75.9"),sQuery(id+"F0.wireOp",EDGE,"E14.76.0"),sQuery(id+"F0.wireOp",EDGE,"E14.76.1"),sQuery(id+"F0.wireOp",EDGE,"E14.76.2"),sQuery(id+"F0.wireOp",EDGE,"E14.76.3"),sQuery(id+"F0.wireOp",EDGE,"E14.76.4"),sQuery(id+"F0.wireOp",EDGE,"E14.76.5"),sQuery(id+"F0.wireOp",EDGE,"E14.76.6"),sQuery(id+"F0.wireOp",EDGE,"E14.76.7"),sQuery(id+"F0.wireOp",EDGE,"E14.76.8"),sQuery(id+"F0.wireOp",EDGE,"E14.76.9"),sQuery(id+"F0.wireOp",EDGE,"E14.77.0"),sQuery(id+"F0.wireOp",EDGE,"E14.77.1"),sQuery(id+"F0.wireOp",EDGE,"E14.77.2"),sQuery(id+"F0.wireOp",EDGE,"E14.77.3"),sQuery(id+"F0.wireOp",EDGE,"E14.77.4"),sQuery(id+"F0.wireOp",EDGE,"E14.77.5"),sQuery(id+"F0.wireOp",EDGE,"E14.77.6"),sQuery(id+"F0.wireOp",EDGE,"E14.77.7"),sQuery(id+"F0.wireOp",EDGE,"E14.77.8"),sQuery(id+"F0.wireOp",EDGE,"E14.77.9"),sQuery(id+"F0.wireOp",EDGE,"E14.78.0"),sQuery(id+"F0.wireOp",EDGE,"E14.78.1"),sQuery(id+"F0.wireOp",EDGE,"E14.78.2"),sQuery(id+"F0.wireOp",EDGE,"E14.78.3"),sQuery(id+"F0.wireOp",EDGE,"E14.78.4"),sQuery(id+"F0.wireOp",EDGE,"E14.78.5"),sQuery(id+"F0.wireOp",EDGE,"E14.78.6"),sQuery(id+"F0.wireOp",EDGE,"E14.78.7"),sQuery(id+"F0.wireOp",EDGE,"E14.78.8"),sQuery(id+"F0.wireOp",EDGE,"E14.78.9"),sQuery(id+"F0.wireOp",EDGE,"E14.79.0"),sQuery(id+"F0.wireOp",EDGE,"E14.79.1"),sQuery(id+"F0.wireOp",EDGE,"E14.79.2"),sQuery(id+"F0.wireOp",EDGE,"E14.79.3"),sQuery(id+"F0.wireOp",EDGE,"E14.79.4"),sQuery(id+"F0.wireOp",EDGE,"E14.79.5"),sQuery(id+"F0.wireOp",EDGE,"E14.79.6"),sQuery(id+"F0.wireOp",EDGE,"E14.79.7"),sQuery(id+"F0.wireOp",EDGE,"E14.79.8"),sQuery(id+"F0.wireOp",EDGE,"E14.79.9"),sQuery(id+"F0.wireOp",EDGE,"E14.80.0"),sQuery(id+"F0.wireOp",EDGE,"E14.80.1"),sQuery(id+"F0.wireOp",EDGE,"E14.80.2"),sQuery(id+"F0.wireOp",EDGE,"E14.80.3"),sQuery(id+"F0.wireOp",EDGE,"E14.80.4"),sQuery(id+"F0.wireOp",EDGE,"E14.80.5"),sQuery(id+"F0.wireOp",EDGE,"E14.80.6"),sQuery(id+"F0.wireOp",EDGE,"E14.80.7"),sQuery(id+"F0.wireOp",EDGE,"E14.80.8"),sQuery(id+"F0.wireOp",EDGE,"E14.80.9"),sQuery(id+"F0.wireOp",EDGE,"E14.81.0"),sQuery(id+"F0.wireOp",EDGE,"E14.81.1"),sQuery(id+"F0.wireOp",EDGE,"E14.81.2"),sQuery(id+"F0.wireOp",EDGE,"E14.81.3"),sQuery(id+"F0.wireOp",EDGE,"E14.81.4"),sQuery(id+"F0.wireOp",EDGE,"E14.81.5"),sQuery(id+"F0.wireOp",EDGE,"E14.81.6"),sQuery(id+"F0.wireOp",EDGE,"E14.81.7"),sQuery(id+"F0.wireOp",EDGE,"E14.81.8"),sQuery(id+"F0.wireOp",EDGE,"E14.81.9"),sQuery(id+"F0.wireOp",EDGE,"E14.82.0"),sQuery(id+"F0.wireOp",EDGE,"E14.82.1"),sQuery(id+"F0.wireOp",EDGE,"E14.82.2"),sQuery(id+"F0.wireOp",EDGE,"E14.82.3"),sQuery(id+"F0.wireOp",EDGE,"E14.82.4"),sQuery(id+"F0.wireOp",EDGE,"E14.82.5"),sQuery(id+"F0.wireOp",EDGE,"E14.82.6"),sQuery(id+"F0.wireOp",EDGE,"E14.82.7"),sQuery(id+"F0.wireOp",EDGE,"E14.82.8"),sQuery(id+"F0.wireOp",EDGE,"E14.82.9"),sQuery(id+"F0.wireOp",EDGE,"E14.83.0"),sQuery(id+"F0.wireOp",EDGE,"E14.83.1"),sQuery(id+"F0.wireOp",EDGE,"E14.83.2"),sQuery(id+"F0.wireOp",EDGE,"E14.83.3"),sQuery(id+"F0.wireOp",EDGE,"E14.83.4"),sQuery(id+"F0.wireOp",EDGE,"E14.83.5"),sQuery(id+"F0.wireOp",EDGE,"E14.83.6"),sQuery(id+"F0.wireOp",EDGE,"E14.83.7"),sQuery(id+"F0.wireOp",EDGE,"E14.83.8"),sQuery(id+"F0.wireOp",EDGE,"E14.83.9"),sQuery(id+"F0.wireOp",EDGE,"E14.84.0"),sQuery(id+"F0.wireOp",EDGE,"E14.84.1"),sQuery(id+"F0.wireOp",EDGE,"E14.84.2"),sQuery(id+"F0.wireOp",EDGE,"E14.84.3"),sQuery(id+"F0.wireOp",EDGE,"E14.84.4"),sQuery(id+"F0.wireOp",EDGE,"E14.84.5"),sQuery(id+"F0.wireOp",EDGE,"E14.84.6"),sQuery(id+"F0.wireOp",EDGE,"E14.84.7"),sQuery(id+"F0.wireOp",EDGE,"E14.84.8"),sQuery(id+"F0.wireOp",EDGE,"E14.84.9"),sQuery(id+"F0.wireOp",EDGE,"E14.85.0"),sQuery(id+"F0.wireOp",EDGE,"E14.85.1"),sQuery(id+"F0.wireOp",EDGE,"E14.85.2"),sQuery(id+"F0.wireOp",EDGE,"E14.85.3"),sQuery(id+"F0.wireOp",EDGE,"E14.85.4"),sQuery(id+"F0.wireOp",EDGE,"E14.85.5"),sQuery(id+"F0.wireOp",EDGE,"E14.85.6"),sQuery(id+"F0.wireOp",EDGE,"E14.85.7"),sQuery(id+"F0.wireOp",EDGE,"E14.85.8"),sQuery(id+"F0.wireOp",EDGE,"E14.85.9"),sQuery(id+"F0.wireOp",EDGE,"E14.86.0"),sQuery(id+"F0.wireOp",EDGE,"E14.86.1"),sQuery(id+"F0.wireOp",EDGE,"E14.86.2"),sQuery(id+"F0.wireOp",EDGE,"E14.86.3"),sQuery(id+"F0.wireOp",EDGE,"E14.86.4"),sQuery(id+"F0.wireOp",EDGE,"E14.86.5"),sQuery(id+"F0.wireOp",EDGE,"E14.86.6"),sQuery(id+"F0.wireOp",EDGE,"E14.86.7"),sQuery(id+"F0.wireOp",EDGE,"E14.86.8"),sQuery(id+"F0.wireOp",EDGE,"E14.86.9"),sQuery(id+"F0.wireOp",EDGE,"E14.87.0"),sQuery(id+"F0.wireOp",EDGE,"E14.87.1"),sQuery(id+"F0.wireOp",EDGE,"E14.87.2"),sQuery(id+"F0.wireOp",EDGE,"E14.87.3"),sQuery(id+"F0.wireOp",EDGE,"E14.87.4"),sQuery(id+"F0.wireOp",EDGE,"E14.87.5"),sQuery(id+"F0.wireOp",EDGE,"E14.87.6"),sQuery(id+"F0.wireOp",EDGE,"E14.87.7"),sQuery(id+"F0.wireOp",EDGE,"E14.87.8"),sQuery(id+"F0.wireOp",EDGE,"E14.87.9"),sQuery(id+"F0.wireOp",EDGE,"E14.88.0"),sQuery(id+"F0.wireOp",EDGE,"E14.88.1"),sQuery(id+"F0.wireOp",EDGE,"E14.88.2"),sQuery(id+"F0.wireOp",EDGE,"E14.88.3"),sQuery(id+"F0.wireOp",EDGE,"E14.88.4"),sQuery(id+"F0.wireOp",EDGE,"E14.88.5"),sQuery(id+"F0.wireOp",EDGE,"E14.88.6"),sQuery(id+"F0.wireOp",EDGE,"E14.88.7"),sQuery(id+"F0.wireOp",EDGE,"E14.88.8"),sQuery(id+"F0.wireOp",EDGE,"E14.88.9"),sQuery(id+"F0.wireOp",EDGE,"E14.89.0"),sQuery(id+"F0.wireOp",EDGE,"E14.89.1"),sQuery(id+"F0.wireOp",EDGE,"E14.89.2"),sQuery(id+"F0.wireOp",EDGE,"E14.89.3"),sQuery(id+"F0.wireOp",EDGE,"E14.89.4"),sQuery(id+"F0.wireOp",EDGE,"E14.89.5"),sQuery(id+"F0.wireOp",EDGE,"E14.89.6"),sQuery(id+"F0.wireOp",EDGE,"E14.89.7"),sQuery(id+"F0.wireOp",EDGE,"E14.89.8"),sQuery(id+"F0.wireOp",EDGE,"E14.89.9"),sQuery(id+"F0.wireOp",EDGE,"E14.90.0"),sQuery(id+"F0.wireOp",EDGE,"E14.90.1"),sQuery(id+"F0.wireOp",EDGE,"E14.90.2"),sQuery(id+"F0.wireOp",EDGE,"E14.90.3"),sQuery(id+"F0.wireOp",EDGE,"E14.90.4"),sQuery(id+"F0.wireOp",EDGE,"E14.90.5"),sQuery(id+"F0.wireOp",EDGE,"E14.90.6"),sQuery(id+"F0.wireOp",EDGE,"E14.90.7"),sQuery(id+"F0.wireOp",EDGE,"E14.90.8"),sQuery(id+"F0.wireOp",EDGE,"E14.90.9"),sQuery(id+"F0.wireOp",EDGE,"E14.91.0"),sQuery(id+"F0.wireOp",EDGE,"E14.91.1"),sQuery(id+"F0.wireOp",EDGE,"E14.91.2"),sQuery(id+"F0.wireOp",EDGE,"E14.91.3"),sQuery(id+"F0.wireOp",EDGE,"E14.91.4"),sQuery(id+"F0.wireOp",EDGE,"E14.91.5"),sQuery(id+"F0.wireOp",EDGE,"E14.91.6"),sQuery(id+"F0.wireOp",EDGE,"E14.91.7"),sQuery(id+"F0.wireOp",EDGE,"E14.91.8"),sQuery(id+"F0.wireOp",EDGE,"E14.91.9"),sQuery(id+"F0.wireOp",EDGE,"E14.92.0"),sQuery(id+"F0.wireOp",EDGE,"E14.92.1"),sQuery(id+"F0.wireOp",EDGE,"E14.92.2"),sQuery(id+"F0.wireOp",EDGE,"E14.92.3"),sQuery(id+"F0.wireOp",EDGE,"E14.92.4"),sQuery(id+"F0.wireOp",EDGE,"E14.92.5"),sQuery(id+"F0.wireOp",EDGE,"E14.92.6"),sQuery(id+"F0.wireOp",EDGE,"E14.92.7"),sQuery(id+"F0.wireOp",EDGE,"E14.92.8"),sQuery(id+"F0.wireOp",EDGE,"E14.92.9"),sQuery(id+"F0.wireOp",EDGE,"E14.93.0"),sQuery(id+"F0.wireOp",EDGE,"E14.93.1"),sQuery(id+"F0.wireOp",EDGE,"E14.93.2"),sQuery(id+"F0.wireOp",EDGE,"E14.93.3"),sQuery(id+"F0.wireOp",EDGE,"E14.93.4"),sQuery(id+"F0.wireOp",EDGE,"E14.93.5"),sQuery(id+"F0.wireOp",EDGE,"E14.93.6"),sQuery(id+"F0.wireOp",EDGE,"E14.93.7"),sQuery(id+"F0.wireOp",EDGE,"E14.93.8"),sQuery(id+"F0.wireOp",EDGE,"E14.93.9"),sQuery(id+"F0.wireOp",EDGE,"E14.94.0"),sQuery(id+"F0.wireOp",EDGE,"E14.94.1"),sQuery(id+"F0.wireOp",EDGE,"E14.94.2"),sQuery(id+"F0.wireOp",EDGE,"E14.94.3"),sQuery(id+"F0.wireOp",EDGE,"E14.94.4"),sQuery(id+"F0.wireOp",EDGE,"E14.94.5"),sQuery(id+"F0.wireOp",EDGE,"E14.94.6"),sQuery(id+"F0.wireOp",EDGE,"E14.94.7"),sQuery(id+"F0.wireOp",EDGE,"E14.94.8"),sQuery(id+"F0.wireOp",EDGE,"E14.94.9"),sQuery(id+"F0.wireOp",EDGE,"E14.95.0"),sQuery(id+"F0.wireOp",EDGE,"E14.95.1"),sQuery(id+"F0.wireOp",EDGE,"E14.95.2"),sQuery(id+"F0.wireOp",EDGE,"E14.95.3"),sQuery(id+"F0.wireOp",EDGE,"E14.95.4"),sQuery(id+"F0.wireOp",EDGE,"E14.95.5"),sQuery(id+"F0.wireOp",EDGE,"E14.95.6"),sQuery(id+"F0.wireOp",EDGE,"E14.95.7"),sQuery(id+"F0.wireOp",EDGE,"E14.95.8"),sQuery(id+"F0.wireOp",EDGE,"E14.95.9"),sQuery(id+"F0.wireOp",EDGE,"E14.96.0"),sQuery(id+"F0.wireOp",EDGE,"E14.96.1"),sQuery(id+"F0.wireOp",EDGE,"E14.96.2"),sQuery(id+"F0.wireOp",EDGE,"E14.96.3"),sQuery(id+"F0.wireOp",EDGE,"E14.96.4"),sQuery(id+"F0.wireOp",EDGE,"E14.96.5"),sQuery(id+"F0.wireOp",EDGE,"E14.96.6"),sQuery(id+"F0.wireOp",EDGE,"E14.96.7"),sQuery(id+"F0.wireOp",EDGE,"E14.96.8"),sQuery(id+"F0.wireOp",EDGE,"E14.96.9"),sQuery(id+"F0.wireOp",EDGE,"E14.97.0"),sQuery(id+"F0.wireOp",EDGE,"E14.97.1"),sQuery(id+"F0.wireOp",EDGE,"E14.97.2"),sQuery(id+"F0.wireOp",EDGE,"E14.97.3"),sQuery(id+"F0.wireOp",EDGE,"E14.97.4"),sQuery(id+"F0.wireOp",EDGE,"E14.97.5"),sQuery(id+"F0.wireOp",EDGE,"E14.97.6"),sQuery(id+"F0.wireOp",EDGE,"E14.97.7"),sQuery(id+"F0.wireOp",EDGE,"E14.97.8"),sQuery(id+"F0.wireOp",EDGE,"E14.97.9"),sQuery(id+"F0.wireOp",EDGE,"E14.98.0"),sQuery(id+"F0.wireOp",EDGE,"E14.98.1"),sQuery(id+"F0.wireOp",EDGE,"E14.98.2"),sQuery(id+"F0.wireOp",EDGE,"E14.98.3"),sQuery(id+"F0.wireOp",EDGE,"E14.98.4"),sQuery(id+"F0.wireOp",EDGE,"E14.98.5"),sQuery(id+"F0.wireOp",EDGE,"E14.98.6"),sQuery(id+"F0.wireOp",EDGE,"E14.98.7"),sQuery(id+"F0.wireOp",EDGE,"E14.98.8"),sQuery(id+"F0.wireOp",EDGE,"E14.98.9"),sQuery(id+"F0.wireOp",EDGE,"E14.99.0"),sQuery(id+"F0.wireOp",EDGE,"E14.99.1"),sQuery(id+"F0.wireOp",EDGE,"E14.99.2"),sQuery(id+"F0.wireOp",EDGE,"E14.99.3"),sQuery(id+"F0.wireOp",EDGE,"E14.99.4"),sQuery(id+"F0.wireOp",EDGE,"E14.99.5"),sQuery(id+"F0.wireOp",EDGE,"E14.99.6"),sQuery(id+"F0.wireOp",EDGE,"E14.99.7"),sQuery(id+"F0.wireOp",EDGE,"E14.99.8"),sQuery(id+"F0.wireOp",EDGE,"E14.99.9"),sQuery(id+"F0.wireOp",EDGE,"E14.100.0"),sQuery(id+"F0.wireOp",EDGE,"E14.100.1"),sQuery(id+"F0.wireOp",EDGE,"E14.100.2"),sQuery(id+"F0.wireOp",EDGE,"E14.100.3"),sQuery(id+"F0.wireOp",EDGE,"E14.100.4"),sQuery(id+"F0.wireOp",EDGE,"E14.100.5"),sQuery(id+"F0.wireOp",EDGE,"E14.100.6"),sQuery(id+"F0.wireOp",EDGE,"E14.100.7"),sQuery(id+"F0.wireOp",EDGE,"E14.100.8"),sQuery(id+"F0.wireOp",EDGE,"E14.100.9"),sQuery(id+"F0.wireOp",EDGE,"E14.101.0"),sQuery(id+"F0.wireOp",EDGE,"E14.101.1"),sQuery(id+"F0.wireOp",EDGE,"E14.101.2"),sQuery(id+"F0.wireOp",EDGE,"E14.101.3"),sQuery(id+"F0.wireOp",EDGE,"E14.101.4"),sQuery(id+"F0.wireOp",EDGE,"E14.101.5"),sQuery(id+"F0.wireOp",EDGE,"E14.101.6"),sQuery(id+"F0.wireOp",EDGE,"E14.101.7"),sQuery(id+"F0.wireOp",EDGE,"E14.101.8"),sQuery(id+"F0.wireOp",EDGE,"E14.101.9"),sQuery(id+"F0.wireOp",EDGE,"E14.102.0"),sQuery(id+"F0.wireOp",EDGE,"E14.102.1"),sQuery(id+"F0.wireOp",EDGE,"E14.102.2"),sQuery(id+"F0.wireOp",EDGE,"E14.102.3"),sQuery(id+"F0.wireOp",EDGE,"E14.102.4"),sQuery(id+"F0.wireOp",EDGE,"E14.102.5"),sQuery(id+"F0.wireOp",EDGE,"E14.102.6"),sQuery(id+"F0.wireOp",EDGE,"E14.102.7"),sQuery(id+"F0.wireOp",EDGE,"E14.102.8"),sQuery(id+"F0.wireOp",EDGE,"E14.102.9"),sQuery(id+"F0.wireOp",EDGE,"E14.103.0"),sQuery(id+"F0.wireOp",EDGE,"E14.103.1"),sQuery(id+"F0.wireOp",EDGE,"E14.103.2"),sQuery(id+"F0.wireOp",EDGE,"E14.103.3"),sQuery(id+"F0.wireOp",EDGE,"E14.103.4"),sQuery(id+"F0.wireOp",EDGE,"E14.103.5"),sQuery(id+"F0.wireOp",EDGE,"E14.103.6"),sQuery(id+"F0.wireOp",EDGE,"E14.103.7"),sQuery(id+"F0.wireOp",EDGE,"E14.103.8"),sQuery(id+"F0.wireOp",EDGE,"E14.103.9"),sQuery(id+"F0.wireOp",EDGE,"E14.104.0"),sQuery(id+"F0.wireOp",EDGE,"E14.104.1"),sQuery(id+"F0.wireOp",EDGE,"E14.104.2"),sQuery(id+"F0.wireOp",EDGE,"E14.104.3"),sQuery(id+"F0.wireOp",EDGE,"E14.104.4"),sQuery(id+"F0.wireOp",EDGE,"E14.104.5"),sQuery(id+"F0.wireOp",EDGE,"E14.104.6"),sQuery(id+"F0.wireOp",EDGE,"E14.104.7"),sQuery(id+"F0.wireOp",EDGE,"E14.104.8"),sQuery(id+"F0.wireOp",EDGE,"E14.104.9"),sQuery(id+"F0.wireOp",EDGE,"E14.105.0"),sQuery(id+"F0.wireOp",EDGE,"E14.105.1"),sQuery(id+"F0.wireOp",EDGE,"E14.105.2"),sQuery(id+"F0.wireOp",EDGE,"E14.105.3"),sQuery(id+"F0.wireOp",EDGE,"E14.105.4"),sQuery(id+"F0.wireOp",EDGE,"E14.105.5"),sQuery(id+"F0.wireOp",EDGE,"E14.105.6"),sQuery(id+"F0.wireOp",EDGE,"E14.105.7"),sQuery(id+"F0.wireOp",EDGE,"E14.105.8"),sQuery(id+"F0.wireOp",EDGE,"E14.105.9"),sQuery(id+"F0.wireOp",EDGE,"E14.106.0"),sQuery(id+"F0.wireOp",EDGE,"E14.106.1"),sQuery(id+"F0.wireOp",EDGE,"E14.106.2"),sQuery(id+"F0.wireOp",EDGE,"E14.106.3"),sQuery(id+"F0.wireOp",EDGE,"E14.106.4"),sQuery(id+"F0.wireOp",EDGE,"E14.106.5"),sQuery(id+"F0.wireOp",EDGE,"E14.106.6"),sQuery(id+"F0.wireOp",EDGE,"E14.106.7"),sQuery(id+"F0.wireOp",EDGE,"E14.106.8"),sQuery(id+"F0.wireOp",EDGE,"E14.106.9"),sQuery(id+"F0.wireOp",EDGE,"E14.107.0"),sQuery(id+"F0.wireOp",EDGE,"E14.107.1"),sQuery(id+"F0.wireOp",EDGE,"E14.107.2"),sQuery(id+"F0.wireOp",EDGE,"E14.107.3"),sQuery(id+"F0.wireOp",EDGE,"E14.107.4"),sQuery(id+"F0.wireOp",EDGE,"E14.107.5"),sQuery(id+"F0.wireOp",EDGE,"E14.107.6"),sQuery(id+"F0.wireOp",EDGE,"E14.107.7"),sQuery(id+"F0.wireOp",EDGE,"E14.107.8"),sQuery(id+"F0.wireOp",EDGE,"E14.107.9"),sQuery(id+"F0.wireOp",EDGE,"E14.108.0"),sQuery(id+"F0.wireOp",EDGE,"E14.108.1"),sQuery(id+"F0.wireOp",EDGE,"E14.108.2"),sQuery(id+"F0.wireOp",EDGE,"E14.108.3"),sQuery(id+"F0.wireOp",EDGE,"E14.108.4"),sQuery(id+"F0.wireOp",EDGE,"E14.108.5"),sQuery(id+"F0.wireOp",EDGE,"E14.108.6"),sQuery(id+"F0.wireOp",EDGE,"E14.108.7"),sQuery(id+"F0.wireOp",EDGE,"E14.108.8"),sQuery(id+"F0.wireOp",EDGE,"E14.108.9"),sQuery(id+"F0.wireOp",EDGE,"E14.109.0"),sQuery(id+"F0.wireOp",EDGE,"E14.109.1"),sQuery(id+"F0.wireOp",EDGE,"E14.109.2"),sQuery(id+"F0.wireOp",EDGE,"E14.109.3"),sQuery(id+"F0.wireOp",EDGE,"E14.109.4"),sQuery(id+"F0.wireOp",EDGE,"E14.109.5"),sQuery(id+"F0.wireOp",EDGE,"E14.109.6"),sQuery(id+"F0.wireOp",EDGE,"E14.109.7"),sQuery(id+"F0.wireOp",EDGE,"E14.109.8"),sQuery(id+"F0.wireOp",EDGE,"E14.109.9"),sQuery(id+"F0.wireOp",EDGE,"E14.110.0"),sQuery(id+"F0.wireOp",EDGE,"E14.110.1"),sQuery(id+"F0.wireOp",EDGE,"E14.110.2"),sQuery(id+"F0.wireOp",EDGE,"E14.110.3"),sQuery(id+"F0.wireOp",EDGE,"E14.110.4"),sQuery(id+"F0.wireOp",EDGE,"E14.110.5"),sQuery(id+"F0.wireOp",EDGE,"E14.110.6"),sQuery(id+"F0.wireOp",EDGE,"E14.110.7"),sQuery(id+"F0.wireOp",EDGE,"E14.110.8"),sQuery(id+"F0.wireOp",EDGE,"E14.110.9"),sQuery(id+"F0.wireOp",EDGE,"E14.111.0"),sQuery(id+"F0.wireOp",EDGE,"E14.111.1"),sQuery(id+"F0.wireOp",EDGE,"E14.111.2"),sQuery(id+"F0.wireOp",EDGE,"E14.111.3"),sQuery(id+"F0.wireOp",EDGE,"E14.111.4"),sQuery(id+"F0.wireOp",EDGE,"E14.111.5"),sQuery(id+"F0.wireOp",EDGE,"E14.111.6"),sQuery(id+"F0.wireOp",EDGE,"E14.111.7"),sQuery(id+"F0.wireOp",EDGE,"E14.111.8"),sQuery(id+"F0.wireOp",EDGE,"E14.111.9"),sQuery(id+"F0.wireOp",EDGE,"E14.112.0"),sQuery(id+"F0.wireOp",EDGE,"E14.112.1"),sQuery(id+"F0.wireOp",EDGE,"E14.112.2"),sQuery(id+"F0.wireOp",EDGE,"E14.112.3"),sQuery(id+"F0.wireOp",EDGE,"E14.112.4"),sQuery(id+"F0.wireOp",EDGE,"E14.112.5"),sQuery(id+"F0.wireOp",EDGE,"E14.112.6"),sQuery(id+"F0.wireOp",EDGE,"E14.112.7"),sQuery(id+"F0.wireOp",EDGE,"E14.112.8"),sQuery(id+"F0.wireOp",EDGE,"E14.112.9"),sQuery(id+"F0.wireOp",EDGE,"E14.113.0"),sQuery(id+"F0.wireOp",EDGE,"E14.113.1"),sQuery(id+"F0.wireOp",EDGE,"E14.113.2"),sQuery(id+"F0.wireOp",EDGE,"E14.113.3"),sQuery(id+"F0.wireOp",EDGE,"E14.113.4"),sQuery(id+"F0.wireOp",EDGE,"E14.113.5"),sQuery(id+"F0.wireOp",EDGE,"E14.113.6"),sQuery(id+"F0.wireOp",EDGE,"E14.113.7"),sQuery(id+"F0.wireOp",EDGE,"E14.113.8"),sQuery(id+"F0.wireOp",EDGE,"E14.113.9"),sQuery(id+"F0.wireOp",EDGE,"E14.114.0"),sQuery(id+"F0.wireOp",EDGE,"E14.114.1"),sQuery(id+"F0.wireOp",EDGE,"E14.114.2"),sQuery(id+"F0.wireOp",EDGE,"E14.114.3"),sQuery(id+"F0.wireOp",EDGE,"E14.114.4"),sQuery(id+"F0.wireOp",EDGE,"E14.114.5"),sQuery(id+"F0.wireOp",EDGE,"E14.114.6"),sQuery(id+"F0.wireOp",EDGE,"E14.114.7"),sQuery(id+"F0.wireOp",EDGE,"E14.114.8"),sQuery(id+"F0.wireOp",EDGE,"E14.114.9"),sQuery(id+"F0.wireOp",EDGE,"E14.115.0"),sQuery(id+"F0.wireOp",EDGE,"E14.115.1"),sQuery(id+"F0.wireOp",EDGE,"E14.115.2"),sQuery(id+"F0.wireOp",EDGE,"E14.115.3"),sQuery(id+"F0.wireOp",EDGE,"E14.115.4"),sQuery(id+"F0.wireOp",EDGE,"E14.115.5"),sQuery(id+"F0.wireOp",EDGE,"E14.115.6"),sQuery(id+"F0.wireOp",EDGE,"E14.115.7"),sQuery(id+"F0.wireOp",EDGE,"E14.115.8"),sQuery(id+"F0.wireOp",EDGE,"E14.115.9"),sQuery(id+"F0.wireOp",EDGE,"E14.116.0"),sQuery(id+"F0.wireOp",EDGE,"E14.116.1"),sQuery(id+"F0.wireOp",EDGE,"E14.116.2"),sQuery(id+"F0.wireOp",EDGE,"E14.116.3"),sQuery(id+"F0.wireOp",EDGE,"E14.116.4"),sQuery(id+"F0.wireOp",EDGE,"E14.116.5"),sQuery(id+"F0.wireOp",EDGE,"E14.116.6"),sQuery(id+"F0.wireOp",EDGE,"E14.116.7"),sQuery(id+"F0.wireOp",EDGE,"E14.116.8"),sQuery(id+"F0.wireOp",EDGE,"E14.116.9"),sQuery(id+"F0.wireOp",EDGE,"E14.117.0"),sQuery(id+"F0.wireOp",EDGE,"E14.117.1"),sQuery(id+"F0.wireOp",EDGE,"E14.117.2"),sQuery(id+"F0.wireOp",EDGE,"E14.117.3"),sQuery(id+"F0.wireOp",EDGE,"E14.117.4"),sQuery(id+"F0.wireOp",EDGE,"E14.117.5"),sQuery(id+"F0.wireOp",EDGE,"E14.117.6"),sQuery(id+"F0.wireOp",EDGE,"E14.117.7"),sQuery(id+"F0.wireOp",EDGE,"E14.117.8"),sQuery(id+"F0.wireOp",EDGE,"E14.117.9"),sQuery(id+"F0.wireOp",EDGE,"E14.118.0"),sQuery(id+"F0.wireOp",EDGE,"E14.118.1"),sQuery(id+"F0.wireOp",EDGE,"E14.118.2"),sQuery(id+"F0.wireOp",EDGE,"E14.118.3"),sQuery(id+"F0.wireOp",EDGE,"E14.118.4"),sQuery(id+"F0.wireOp",EDGE,"E14.118.5"),sQuery(id+"F0.wireOp",EDGE,"E14.118.6"),sQuery(id+"F0.wireOp",EDGE,"E14.118.7"),sQuery(id+"F0.wireOp",EDGE,"E14.118.8"),sQuery(id+"F0.wireOp",EDGE,"E14.118.9"),sQuery(id+"F0.wireOp",EDGE,"E14.119.0"),sQuery(id+"F0.wireOp",EDGE,"E14.119.1"),sQuery(id+"F0.wireOp",EDGE,"E14.119.2"),sQuery(id+"F0.wireOp",EDGE,"E14.119.3"),sQuery(id+"F0.wireOp",EDGE,"E14.119.4"),sQuery(id+"F0.wireOp",EDGE,"E14.119.5"),sQuery(id+"F0.wireOp",EDGE,"E14.119.6"),sQuery(id+"F0.wireOp",EDGE,"E14.119.7"),sQuery(id+"F0.wireOp",EDGE,"E14.119.8"),sQuery(id+"F0.wireOp",EDGE,"E14.119.9"),sQuery(id+"F0.wireOp",EDGE,"E15.trimOffspring"),sQuery(id+"F0.wireOp",EDGE,"E16.trimOffspring"),sQuery(id+"F0.wireOp",EDGE,"E17.trimOffspring"),sQuery(id+"F0.wireOp",EDGE,"E18.trimOffspring"),sQuery(id+"F0.wireOp",EDGE,"E19.trimOffspring"),sQuery(id+"F0.wireOp",EDGE,"E20.trimOffspring"),sQuery(id+"F0.wireOp",EDGE,"E21.trimOffspring"),sQuery(id+"F0.wireOp",EDGE,"E22.trimOffspring"),sQuery(id+"F0.wireOp",EDGE,"E23.trimOffspring"),sQuery(id+"F0.wireOp",EDGE,"E24.trimOffspring"),sQuery(id+"F0.wireOp",EDGE,"E25.trimOffspring"),sQuery(id+"F0.wireOp",EDGE,"E26.trimOffspring"),sQuery(id+"F0.wireOp",EDGE,"E27.trimOffspring"),sQuery(id+"F0.wireOp",EDGE,"E28.trimOffspring"),sQuery(id+"F0.wireOp",EDGE,"E29.trimOffspring"),sQuery(id+"F0.wireOp",EDGE,"E30.trimOffspring"),sQuery(id+"F0.wireOp",EDGE,"E31.trimOffspring"),sQuery(id+"F0.wireOp",EDGE,"E32.trimOffspring"),sQuery(id+"F0.wireOp",EDGE,"E33.trimOffspring"),sQuery(id+"F0.wireOp",EDGE,"E34.trimOffspring"),sQuery(id+"F0.wireOp",EDGE,"E35.trimOffspring"),sQuery(id+"F0.wireOp",EDGE,"E36.trimOffspring"),sQuery(id+"F0.wireOp",EDGE,"E37.trimOffspring"),sQuery(id+"F0.wireOp",EDGE,"E38.trimOffspring"),sQuery(id+"F0.wireOp",EDGE,"E39.trimOffspring"),sQuery(id+"F0.wireOp",EDGE,"E40.trimOffspring"),sQuery(id+"F0.wireOp",EDGE,"E41.trimOffspring"),sQuery(id+"F0.wireOp",EDGE,"E42.trimOffspring"),sQuery(id+"F0.wireOp",EDGE,"E43.trimOffspring"),sQuery(id+"F0.wireOp",EDGE,"E44.trimOffspring"),sQuery(id+"F0.wireOp",EDGE,"E45.trimOffspring"),sQuery(id+"F0.wireOp",EDGE,"E46.trimOffspring"),sQuery(id+"F0.wireOp",EDGE,"E47.trimOffspring"),sQuery(id+"F0.wireOp",EDGE,"E48.trimOffspring"),sQuery(id+"F0.wireOp",EDGE,"E49.trimOffspring"),sQuery(id+"F0.wireOp",EDGE,"E73.1.0"),sQuery(id+"F0.wireOp",EDGE,"E73.1.1"),sQuery(id+"F0.wireOp",EDGE,"E73.2.0"),sQuery(id+"F0.wireOp",EDGE,"E73.2.1"),sQuery(id+"F0.wireOp",EDGE,"E74.3.3.0"),sQuery(id+"F0.wireOp",EDGE,"E74.4.3.0"),sQuery(id+"F0.wireOp",EDGE,"E74.3.4.0"),sQuery(id+"F0.wireOp",EDGE,"E74.4.4.0"),sQuery(id+"F0.wireOp",EDGE,"E74.3.5.0"),sQuery(id+"F0.wireOp",EDGE,"E74.4.5.0"),sQuery(id+"F0.wireOp",EDGE,"E74.3.6.0"),sQuery(id+"F0.wireOp",EDGE,"E74.4.6.0"),sQuery(id+"F0.wireOp",EDGE,"E74.3.7.0"),sQuery(id+"F0.wireOp",EDGE,"E74.4.7.0"),sQuery(id+"F0.wireOp",EDGE,"E74.3.8.0"),sQuery(id+"F0.wireOp",EDGE,"E74.4.8.0"),sQuery(id+"F0.wireOp",EDGE,"E74.3.9.0"),sQuery(id+"F0.wireOp",EDGE,"E74.4.9.0"),sQuery(id+"F0.wireOp",EDGE,"E74.3.10.0"),sQuery(id+"F0.wireOp",EDGE,"E74.4.10.0"),sQuery(id+"F0.wireOp",EDGE,"E74.3.11.0"),sQuery(id+"F0.wireOp",EDGE,"E74.4.11.0"),sQuery(id+"F0.wireOp",EDGE,"E74.3.12.0"),sQuery(id+"F0.wireOp",EDGE,"E74.4.12.0"),sQuery(id+"F0.wireOp",EDGE,"E74.3.13.0"),sQuery(id+"F0.wireOp",EDGE,"E74.4.13.0"),sQuery(id+"F0.wireOp",EDGE,"E74.3.14.0"),sQuery(id+"F0.wireOp",EDGE,"E74.4.14.0"),sQuery(id+"F0.wireOp",EDGE,"E74.3.15.0"),sQuery(id+"F0.wireOp",EDGE,"E74.4.15.0"),sQuery(id+"F0.wireOp",EDGE,"E74.3.16.0"),sQuery(id+"F0.wireOp",EDGE,"E74.4.16.0"),sQuery(id+"F0.wireOp",EDGE,"E74.3.17.0"),sQuery(id+"F0.wireOp",EDGE,"E74.4.17.0"),sQuery(id+"F0.wireOp",EDGE,"E74.3.18.0"),sQuery(id+"F0.wireOp",EDGE,"E74.4.18.0"),sQuery(id+"F0.wireOp",EDGE,"E74.3.19.0"),sQuery(id+"F0.wireOp",EDGE,"E74.4.19.0"),sQuery(id+"F0.wireOp",EDGE,"E74.3.20.0"),sQuery(id+"F0.wireOp",EDGE,"E74.4.20.0"),sQuery(id+"F0.wireOp",EDGE,"E74.3.21.0"),sQuery(id+"F0.wireOp",EDGE,"E74.4.21.0"),sQuery(id+"F0.wireOp",EDGE,"E74.3.22.0"),sQuery(id+"F0.wireOp",EDGE,"E74.4.22.0"),sQuery(id+"F0.wireOp",EDGE,"E74.3.23.0"),sQuery(id+"F0.wireOp",EDGE,"E74.4.23.0"),sQuery(id+"F0.wireOp",EDGE,"E74.3.24.0"),sQuery(id+"F0.wireOp",EDGE,"E74.4.24.0"),sQuery(id+"F0.wireOp",EDGE,"E74.3.25.0"),sQuery(id+"F0.wireOp",EDGE,"E74.4.25.0"),sQuery(id+"F0.wireOp",EDGE,"E74.3.26.0"),sQuery(id+"F0.wireOp",EDGE,"E74.4.26.0"),sQuery(id+"F0.wireOp",EDGE,"E74.3.27.0"),sQuery(id+"F0.wireOp",EDGE,"E74.4.27.0"),sQuery(id+"F0.wireOp",EDGE,"E74.3.28.0"),sQuery(id+"F0.wireOp",EDGE,"E74.4.28.0"),sQuery(id+"F0.wireOp",EDGE,"E74.3.29.0"),sQuery(id+"F0.wireOp",EDGE,"E74.4.29.0"),sQuery(id+"F0.wireOp",EDGE,"E74.3.30.0"),sQuery(id+"F0.wireOp",EDGE,"E74.4.30.0"),sQuery(id+"F0.wireOp",EDGE,"E74.3.31.0"),sQuery(id+"F0.wireOp",EDGE,"E74.4.31.0"),sQuery(id+"F0.wireOp",EDGE,"E74.3.32.0"),sQuery(id+"F0.wireOp",EDGE,"E74.4.32.0"),sQuery(id+"F0.wireOp",EDGE,"E74.3.33.0"),sQuery(id+"F0.wireOp",EDGE,"E74.4.33.0"),sQuery(id+"F0.wireOp",EDGE,"E74.3.34.0"),sQuery(id+"F0.wireOp",EDGE,"E74.4.34.0"),sQuery(id+"F0.wireOp",EDGE,"E74.3.35.0"),sQuery(id+"F0.wireOp",EDGE,"E74.4.35.0"),sQuery(id+"F0.wireOp",EDGE,"E74.3.36.0"),sQuery(id+"F0.wireOp",EDGE,"E74.4.36.0"),sQuery(id+"F0.wireOp",EDGE,"E74.3.37.0"),sQuery(id+"F0.wireOp",EDGE,"E74.4.37.0"),sQuery(id+"F0.wireOp",EDGE,"E74.3.38.0"),sQuery(id+"F0.wireOp",EDGE,"E74.4.38.0"),sQuery(id+"F0.wireOp",EDGE,"E74.3.39.0"),sQuery(id+"F0.wireOp",EDGE,"E74.4.39.0"),sQuery(id+"F0.wireOp",EDGE,"E74.3.40.0"),sQuery(id+"F0.wireOp",EDGE,"E74.4.40.0"),sQuery(id+"F0.wireOp",EDGE,"E74.3.41.0"),sQuery(id+"F0.wireOp",EDGE,"E74.4.41.0"),sQuery(id+"F0.wireOp",EDGE,"E74.3.42.0"),sQuery(id+"F0.wireOp",EDGE,"E74.4.42.0"),sQuery(id+"F0.wireOp",EDGE,"E74.3.43.0"),sQuery(id+"F0.wireOp",EDGE,"E74.4.43.0"),sQuery(id+"F0.wireOp",EDGE,"E74.3.44.0"),sQuery(id+"F0.wireOp",EDGE,"E74.4.44.0"),sQuery(id+"F0.wireOp",EDGE,"E74.3.45.0"),sQuery(id+"F0.wireOp",EDGE,"E74.4.45.0"),sQuery(id+"F0.wireOp",EDGE,"E74.3.46.0"),sQuery(id+"F0.wireOp",EDGE,"E74.4.46.0"),sQuery(id+"F0.wireOp",EDGE,"E74.3.47.0"),sQuery(id+"F0.wireOp",EDGE,"E74.4.47.0"),sQuery(id+"F0.wireOp",EDGE,"E74.3.48.0"),sQuery(id+"F0.wireOp",EDGE,"E74.4.48.0"),sQuery(id+"F0.wireOp",EDGE,"E74.3.49.0"),sQuery(id+"F0.wireOp",EDGE,"E74.4.49.0"),sQuery(id+"F0.wireOp",EDGE,"E74.3.50.0"),sQuery(id+"F0.wireOp",EDGE,"E74.4.50.0"),sQuery(id+"F0.wireOp",EDGE,"E74.3.51.0"),sQuery(id+"F0.wireOp",EDGE,"E74.4.51.0"),sQuery(id+"F0.wireOp",EDGE,"E74.3.52.0"),sQuery(id+"F0.wireOp",EDGE,"E74.4.52.0"),sQuery(id+"F0.wireOp",EDGE,"E74.3.53.0"),sQuery(id+"F0.wireOp",EDGE,"E74.4.53.0"),sQuery(id+"F0.wireOp",EDGE,"E74.3.54.0"),sQuery(id+"F0.wireOp",EDGE,"E74.4.54.0"),sQuery(id+"F0.wireOp",EDGE,"E74.3.55.0"),sQuery(id+"F0.wireOp",EDGE,"E74.4.55.0"),sQuery(id+"F0.wireOp",EDGE,"E74.3.56.0"),sQuery(id+"F0.wireOp",EDGE,"E74.4.56.0"),sQuery(id+"F0.wireOp",EDGE,"E74.3.57.0"),sQuery(id+"F0.wireOp",EDGE,"E74.4.57.0"),sQuery(id+"F0.wireOp",EDGE,"E74.3.58.0"),sQuery(id+"F0.wireOp",EDGE,"E74.4.58.0"),sQuery(id+"F0.wireOp",EDGE,"E74.3.59.0"),sQuery(id+"F0.wireOp",EDGE,"E74.4.59.0"),sQuery(id+"F0.wireOp",EDGE,"E74.3.60.0"),sQuery(id+"F0.wireOp",EDGE,"E74.4.60.0"),sQuery(id+"F0.wireOp",EDGE,"E74.3.61.0"),sQuery(id+"F0.wireOp",EDGE,"E74.4.61.0"),sQuery(id+"F0.wireOp",EDGE,"E74.3.62.0"),sQuery(id+"F0.wireOp",EDGE,"E74.4.62.0"),sQuery(id+"F0.wireOp",EDGE,"E74.3.63.0"),sQuery(id+"F0.wireOp",EDGE,"E74.4.63.0"),sQuery(id+"F0.wireOp",EDGE,"E74.3.64.0"),sQuery(id+"F0.wireOp",EDGE,"E74.4.64.0"),sQuery(id+"F0.wireOp",EDGE,"E74.3.65.0"),sQuery(id+"F0.wireOp",EDGE,"E74.4.65.0"),sQuery(id+"F0.wireOp",EDGE,"E74.3.66.0"),sQuery(id+"F0.wireOp",EDGE,"E74.4.66.0"),sQuery(id+"F0.wireOp",EDGE,"E74.3.67.0"),sQuery(id+"F0.wireOp",EDGE,"E74.4.67.0"),sQuery(id+"F0.wireOp",EDGE,"E74.3.68.0"),sQuery(id+"F0.wireOp",EDGE,"E74.4.68.0"),sQuery(id+"F0.wireOp",EDGE,"E74.3.69.0"),sQuery(id+"F0.wireOp",EDGE,"E74.4.69.0"),sQuery(id+"F0.wireOp",EDGE,"E74.3.70.0"),sQuery(id+"F0.wireOp",EDGE,"E74.4.70.0"),sQuery(id+"F0.wireOp",EDGE,"E74.3.71.0"),sQuery(id+"F0.wireOp",EDGE,"E74.4.71.0"),sQuery(id+"F0.wireOp",EDGE,"E74.3.72.0"),sQuery(id+"F0.wireOp",EDGE,"E74.4.72.0"),sQuery(id+"F0.wireOp",EDGE,"E74.3.73.0"),sQuery(id+"F0.wireOp",EDGE,"E74.4.73.0"),sQuery(id+"F0.wireOp",EDGE,"E74.3.74.0"),sQuery(id+"F0.wireOp",EDGE,"E74.4.74.0"),sQuery(id+"F0.wireOp",EDGE,"E74.3.75.0"),sQuery(id+"F0.wireOp",EDGE,"E74.4.75.0"),sQuery(id+"F0.wireOp",EDGE,"E74.3.76.0"),sQuery(id+"F0.wireOp",EDGE,"E74.4.76.0"),sQuery(id+"F0.wireOp",EDGE,"E74.3.77.0"),sQuery(id+"F0.wireOp",EDGE,"E74.4.77.0"),sQuery(id+"F0.wireOp",EDGE,"E74.3.78.0"),sQuery(id+"F0.wireOp",EDGE,"E74.4.78.0"),sQuery(id+"F0.wireOp",EDGE,"E74.3.79.0"),sQuery(id+"F0.wireOp",EDGE,"E74.4.79.0"),sQuery(id+"F0.wireOp",EDGE,"E74.3.80.0"),sQuery(id+"F0.wireOp",EDGE,"E74.4.80.0"),sQuery(id+"F0.wireOp",EDGE,"E74.3.81.0"),sQuery(id+"F0.wireOp",EDGE,"E74.4.81.0"),sQuery(id+"F0.wireOp",EDGE,"E74.3.82.0"),sQuery(id+"F0.wireOp",EDGE,"E74.4.82.0"),sQuery(id+"F0.wireOp",EDGE,"E74.3.83.0"),sQuery(id+"F0.wireOp",EDGE,"E74.4.83.0"),sQuery(id+"F0.wireOp",EDGE,"E74.3.84.0"),sQuery(id+"F0.wireOp",EDGE,"E74.4.84.0"),sQuery(id+"F0.wireOp",EDGE,"E74.3.85.0"),sQuery(id+"F0.wireOp",EDGE,"E74.4.85.0"),sQuery(id+"F0.wireOp",EDGE,"E74.3.86.0"),sQuery(id+"F0.wireOp",EDGE,"E74.4.86.0"),sQuery(id+"F0.wireOp",EDGE,"E74.3.87.0"),sQuery(id+"F0.wireOp",EDGE,"E74.4.87.0"),sQuery(id+"F0.wireOp",EDGE,"E74.3.88.0"),sQuery(id+"F0.wireOp",EDGE,"E74.4.88.0"),sQuery(id+"F0.wireOp",EDGE,"E74.3.89.0"),sQuery(id+"F0.wireOp",EDGE,"E74.4.89.0"),sQuery(id+"F0.wireOp",EDGE,"E74.3.90.0"),sQuery(id+"F0.wireOp",EDGE,"E74.4.90.0"),sQuery(id+"F0.wireOp",EDGE,"E74.3.91.0"),sQuery(id+"F0.wireOp",EDGE,"E74.4.91.0"),sQuery(id+"F0.wireOp",EDGE,"E74.3.92.0"),sQuery(id+"F0.wireOp",EDGE,"E74.4.92.0"),sQuery(id+"F0.wireOp",EDGE,"E74.3.93.0"),sQuery(id+"F0.wireOp",EDGE,"E74.4.93.0"),sQuery(id+"F0.wireOp",EDGE,"E74.3.94.0"),sQuery(id+"F0.wireOp",EDGE,"E74.4.94.0"),sQuery(id+"F0.wireOp",EDGE,"E74.3.95.0"),sQuery(id+"F0.wireOp",EDGE,"E74.4.95.0"),sQuery(id+"F0.wireOp",EDGE,"E74.3.96.0"),sQuery(id+"F0.wireOp",EDGE,"E74.4.96.0"),sQuery(id+"F0.wireOp",EDGE,"E74.3.97.0"),sQuery(id+"F0.wireOp",EDGE,"E74.4.97.0"),sQuery(id+"F0.wireOp",EDGE,"E74.3.98.0"),sQuery(id+"F0.wireOp",EDGE,"E74.4.98.0"),sQuery(id+"F0.wireOp",EDGE,"E74.3.99.0"),sQuery(id+"F0.wireOp",EDGE,"E74.4.99.0"),sQuery(id+"F0.wireOp",EDGE,"E74.3.100.0"),sQuery(id+"F0.wireOp",EDGE,"E74.4.100.0"),sQuery(id+"F0.wireOp",EDGE,"E74.3.101.0"),sQuery(id+"F0.wireOp",EDGE,"E74.4.101.0"),sQuery(id+"F0.wireOp",EDGE,"E74.3.102.0"),sQuery(id+"F0.wireOp",EDGE,"E74.4.102.0"),sQuery(id+"F0.wireOp",EDGE,"E74.3.103.0"),sQuery(id+"F0.wireOp",EDGE,"E74.4.103.0"),sQuery(id+"F0.wireOp",EDGE,"E74.3.104.0"),sQuery(id+"F0.wireOp",EDGE,"E74.4.104.0"),sQuery(id+"F0.wireOp",EDGE,"E74.3.105.0"),sQuery(id+"F0.wireOp",EDGE,"E74.4.105.0"),sQuery(id+"F0.wireOp",EDGE,"E74.3.106.0"),sQuery(id+"F0.wireOp",EDGE,"E74.4.106.0"),sQuery(id+"F0.wireOp",EDGE,"E74.3.107.0"),sQuery(id+"F0.wireOp",EDGE,"E74.4.107.0"),sQuery(id+"F0.wireOp",EDGE,"E74.3.108.0"),sQuery(id+"F0.wireOp",EDGE,"E74.4.108.0"),sQuery(id+"F0.wireOp",EDGE,"E74.3.109.0"),sQuery(id+"F0.wireOp",EDGE,"E74.4.109.0"),sQuery(id+"F0.wireOp",EDGE,"E74.3.110.0"),sQuery(id+"F0.wireOp",EDGE,"E74.4.110.0"),sQuery(id+"F0.wireOp",EDGE,"E74.3.111.0"),sQuery(id+"F0.wireOp",EDGE,"E74.4.111.0"),sQuery(id+"F0.wireOp",EDGE,"E74.3.112.0"),sQuery(id+"F0.wireOp",EDGE,"E74.4.112.0"),sQuery(id+"F0.wireOp",EDGE,"E74.3.113.0"),sQuery(id+"F0.wireOp",EDGE,"E74.4.113.0"),sQuery(id+"F0.wireOp",EDGE,"E74.3.114.0"),sQuery(id+"F0.wireOp",EDGE,"E74.4.114.0"),sQuery(id+"F0.wireOp",EDGE,"E74.3.115.0"),sQuery(id+"F0.wireOp",EDGE,"E74.4.115.0"),sQuery(id+"F0.wireOp",EDGE,"E74.3.116.0"),sQuery(id+"F0.wireOp",EDGE,"E74.4.116.0"),sQuery(id+"F0.wireOp",EDGE,"E74.3.117.0"),sQuery(id+"F0.wireOp",EDGE,"E74.4.117.0"),sQuery(id+"F0.wireOp",EDGE,"E74.3.118.0"),sQuery(id+"F0.wireOp",EDGE,"E74.4.118.0"),sQuery(id+"F0.wireOp",EDGE,"E74.3.119.0"),sQuery(id+"F0.wireOp",EDGE,"E74.4.119.0"),sQuery(id+"F0.wireOp",EDGE,"E75.trimOffspring"),sQuery(id+"F0.wireOp",EDGE,"E76.trimOffspring"),sQuery(id+"F0.wireOp",EDGE,"E77.trimOffspring"),sQuery(id+"F0.wireOp",EDGE,"E78.trimOffspring"),sQuery(id+"F0.wireOp",EDGE,"E79.trimOffspring"),sQuery(id+"F0.wireOp",EDGE,"E80.trimOffspring"),sQuery(id+"F0.wireOp",EDGE,"E81.trimOffspring"),sQuery(id+"F0.wireOp",EDGE,"E82.trimOffspring"),sQuery(id+"F0.wireOp",EDGE,"E83.trimOffspring"),sQuery(id+"F0.wireOp",EDGE,"E84.trimOffspring"),sQuery(id+"F0.wireOp",EDGE,"E85.trimOffspring"),sQuery(id+"F0.wireOp",EDGE,"E86.trimOffspring"),sQuery(id+"F0.wireOp",EDGE,"E87.trimOffspring"),sQuery(id+"F0.wireOp",EDGE,"E88.trimOffspring"),sQuery(id+"F0.wireOp",EDGE,"E89.trimOffspring"),sQuery(id+"F0.wireOp",EDGE,"E90.trimOffspring"),sQuery(id+"F0.wireOp",EDGE,"E91.trimOffspring"),sQuery(id+"F0.wireOp",EDGE,"E92.trimOffspring"),sQuery(id+"F0.wireOp",EDGE,"E93.trimOffspring"),sQuery(id+"F0.wireOp",EDGE,"E94.trimOffspring"),sQuery(id+"F0.wireOp",EDGE,"E95.trimOffspring"),sQuery(id+"F0.wireOp",EDGE,"E96.trimOffspring"),sQuery(id+"F0.wireOp",EDGE,"E97.trimOffspring"),sQuery(id+"F0.wireOp",EDGE,"E98.trimOffspring"),sQuery(id+"F0.wireOp",EDGE,"E99.trimOffspring"),sQuery(id+"F0.wireOp",EDGE,"E100.trimOffspring"),sQuery(id+"F0.wireOp",EDGE,"E101.trimOffspring"),sQuery(id+"F0.wireOp",EDGE,"E102.trimOffspring"),sQuery(id+"F0.wireOp",EDGE,"E103.trimOffspring"),sQuery(id+"F0.wireOp",EDGE,"E104.trimOffspring"),sQuery(id+"F0.wireOp",EDGE,"E105.trimOffspring"),sQuery(id+"F0.wireOp",EDGE,"E106.trimOffspring"),sQuery(id+"F0.wireOp",EDGE,"E107.trimOffspring"),sQuery(id+"F0.wireOp",EDGE,"E108.trimOffspring"),sQuery(id+"F0.wireOp",EDGE,"E109.trimOffspring"),sQuery(id+"F0.wireOp",EDGE,"E110.trimOffspring"),sQuery(id+"F0.wireOp",EDGE,"E111.trimOffspring"),sQuery(id+"F0.wireOp",EDGE,"E112.trimOffspring"),sQuery(id+"F0.wireOp",EDGE,"E113.trimOffspring"),sQuery(id+"F0.wireOp",EDGE,"E114.trimOffspring"),sQuery(id+"F0.wireOp",EDGE,"E115.trimOffspring"),sQuery(id+"F0.wireOp",EDGE,"E116.trimOffspring"),sQuery(id+"F0.wireOp",EDGE,"E117.trimOffspring"),sQuery(id+"F0.wireOp",EDGE,"E118.trimOffspring"),sQuery(id+"F0.wireOp",EDGE,"E119.trimOffspring"),sQuery(id+"F0.wireOp",EDGE,"E120.trimOffspring"),sQuery(id+"F0.wireOp",EDGE,"E121.trimOffspring"),sQuery(id+"F0.wireOp",EDGE,"E122.trimOffspring"),sQuery(id+"F0.wireOp",EDGE,"E123.trimOffspring"),sQuery(id+"F0.wireOp",EDGE,"E124.trimOffspring"),sQuery(id+"F0.wireOp",EDGE,"E125.trimOffspring"),sQuery(id+"F0.wireOp",EDGE,"E126.trimOffspring"),sQuery(id+"F0.wireOp",EDGE,"E127.trimOffspring"),sQuery(id+"F0.wireOp",EDGE,"E128.trimOffspring"),sQuery(id+"F0.wireOp",EDGE,"E129.trimOffspring"),sQuery(id+"F0.wireOp",EDGE,"E130.trimOffspring"),sQuery(id+"F0.wireOp",EDGE,"E131.trimOffspring"),sQuery(id+"F0.wireOp",EDGE,"E132.trimOffspring"),sQuery(id+"F0.wireOp",EDGE,"E133.trimOffspring"),sQuery(id+"F0.wireOp",EDGE,"E134.trimOffspring"),sQuery(id+"F0.wireOp",EDGE,"E135.trimOffspring"),sQuery(id+"F0.wireOp",EDGE,"E136.trimOffspring"),sQuery(id+"F0.wireOp",EDGE,"E137.trimOffspring"),sQuery(id+"F0.wireOp",EDGE,"E138.trimOffspring"),sQuery(id+"F0.wireOp",EDGE,"E139.trimOffspring"),sQuery(id+"F0.wireOp",EDGE,"E140.trimOffspring"),sQuery(id+"F0.wireOp",EDGE,"E141.trimOffspring"),sQuery(id+"F0.wireOp",EDGE,"E142.trimOffspring"),sQuery(id+"F0.wireOp",EDGE,"E143.trimOffspring"),sQuery(id+"F0.wireOp",EDGE,"E144.trimOffspring"),sQuery(id+"F0.wireOp",EDGE,"E145.trimOffspring"),sQuery(id+"F0.wireOp",EDGE,"E146.trimOffspring"),sQuery(id+"F0.wireOp",EDGE,"E147.trimOffspring"),sQuery(id+"F0.wireOp",EDGE,"E148.trimOffspring"),sQuery(id+"F0.wireOp",EDGE,"E149.trimOffspring"),sQuery(id+"F0.wireOp",EDGE,"E150.trimOffspring"),sQuery(id+"F0.wireOp",EDGE,"E151.trimOffspring"),sQuery(id+"F0.wireOp",EDGE,"E152.trimOffspring"),sQuery(id+"F0.wireOp",EDGE,"E153.trimOffspring"),sQuery(id+"F0.wireOp",EDGE,"E154.trimOffspring"),sQuery(id+"F0.wireOp",EDGE,"E155.trimOffspring"),sQuery(id+"F0.wireOp",EDGE,"E156.trimOffspring"),sQuery(id+"F0.wireOp",EDGE,"E157.trimOffspring")])],"isStart":false});
            var sketch = newSketch(context, id + "F6", { "sketchPlane" : qUnion([Q0])});
            skLineSegment(sketch, "E161.bottom", {"start": v(31.45, -1.97) * mm, "end": v(27.7, -1.97) * mm});
            skLineSegment(sketch, "E161.top", {"start": v(31.45, 1.97) * mm, "end": v(27.7, 1.97) * mm});
            skLineSegment(sketch, "E161.left", {"start": v(31.45, -1.97) * mm, "end": v(31.45, 1.97) * mm});
            skLineSegment(sketch, "E161.right", {"start": v(27.7, -1.97) * mm, "end": v(27.7, 1.97) * mm});
            skPoint(sketch, "E161.middle", {"position": v(29.58, 0) * mm});
            skLineSegment(sketch, "E162.1.0", {"start": v(1.97, 27.7) * mm, "end": v(-1.97, 27.7) * mm});
            skLineSegment(sketch, "E162.1.1", {"start": v(-1.97, 31.45) * mm, "end": v(-1.97, 27.7) * mm});
            skLineSegment(sketch, "E162.1.2", {"start": v(1.97, 31.45) * mm, "end": v(-1.97, 31.45) * mm});
            skLineSegment(sketch, "E162.1.3", {"start": v(1.97, 31.45) * mm, "end": v(1.97, 27.7) * mm});
            skLineSegment(sketch, "E162.2.0", {"start": v(-27.7, 1.97) * mm, "end": v(-27.7, -1.97) * mm});
            skLineSegment(sketch, "E162.2.1", {"start": v(-31.45, -1.97) * mm, "end": v(-27.7, -1.97) * mm});
            skLineSegment(sketch, "E162.2.2", {"start": v(-31.45, 1.97) * mm, "end": v(-31.45, -1.97) * mm});
            skLineSegment(sketch, "E162.2.3", {"start": v(-31.45, 1.97) * mm, "end": v(-27.7, 1.97) * mm});
            skLineSegment(sketch, "E162.3.0", {"start": v(-1.97, -27.7) * mm, "end": v(1.97, -27.7) * mm});
            skLineSegment(sketch, "E162.3.1", {"start": v(1.97, -31.45) * mm, "end": v(1.97, -27.7) * mm});
            skLineSegment(sketch, "E162.3.2", {"start": v(-1.97, -31.45) * mm, "end": v(1.97, -31.45) * mm});
            skLineSegment(sketch, "E162.3.3", {"start": v(-1.97, -31.45) * mm, "end": v(-1.97, -27.7) * mm});
            skPoint(sketch, "E162.center", {"position": v(0, 0) * mm});
            skSolve(sketch);
        }
        {
            var Q0;
            Q0 = qSketchRegion(id + "F6", true);
            extrude(context, id + "F7", {"entities" : qUnion([Q0]), "operationType" : NewBodyOperationType.REMOVE, "oppositeDirection" : true, "depth" : 25.4 * mm});
        }
        {
            var Q0;
            Q0=makeQuery(id+"F1.opExtrude","CAP_FACE",FACE,{"disambiguationData":[OSD([sQuery(id+"F0.wireOp",EDGE,"E0"),sQuery(id+"F0.wireOp",EDGE,"E1.trimOffspring"),sQuery(id+"F0.wireOp",EDGE,"E2"),sQuery(id+"F0.wireOp",EDGE,"E3"),sQuery(id+"F0.wireOp",EDGE,"E4.MirrorCS"),sQuery(id+"F0.wireOp",EDGE,"E5.MirrorCS"),sQuery(id+"F0.wireOp",EDGE,"E6.MirrorCS"),sQuery(id+"F0.wireOp",EDGE,"E8.filletArc"),sQuery(id+"F0.wireOp",EDGE,"E9.filletArc"),sQuery(id+"F0.wireOp",EDGE,"E10.filletArc"),sQuery(id+"F0.wireOp",EDGE,"E11.filletArc"),sQuery(id+"F0.wireOp",EDGE,"E12.filletArc"),sQuery(id+"F0.wireOp",EDGE,"E13.filletArc"),sQuery(id+"F0.wireOp",EDGE,"E14.1.0"),sQuery(id+"F0.wireOp",EDGE,"E14.1.1"),sQuery(id+"F0.wireOp",EDGE,"E14.1.2"),sQuery(id+"F0.wireOp",EDGE,"E14.1.3"),sQuery(id+"F0.wireOp",EDGE,"E14.1.4"),sQuery(id+"F0.wireOp",EDGE,"E14.1.5"),sQuery(id+"F0.wireOp",EDGE,"E14.1.6"),sQuery(id+"F0.wireOp",EDGE,"E14.1.7"),sQuery(id+"F0.wireOp",EDGE,"E14.1.8"),sQuery(id+"F0.wireOp",EDGE,"E14.1.9"),sQuery(id+"F0.wireOp",EDGE,"E14.2.0"),sQuery(id+"F0.wireOp",EDGE,"E14.2.1"),sQuery(id+"F0.wireOp",EDGE,"E14.2.2"),sQuery(id+"F0.wireOp",EDGE,"E14.2.3"),sQuery(id+"F0.wireOp",EDGE,"E14.2.4"),sQuery(id+"F0.wireOp",EDGE,"E14.2.5"),sQuery(id+"F0.wireOp",EDGE,"E14.2.6"),sQuery(id+"F0.wireOp",EDGE,"E14.2.7"),sQuery(id+"F0.wireOp",EDGE,"E14.2.8"),sQuery(id+"F0.wireOp",EDGE,"E14.2.9"),sQuery(id+"F0.wireOp",EDGE,"E14.3.0"),sQuery(id+"F0.wireOp",EDGE,"E14.3.1"),sQuery(id+"F0.wireOp",EDGE,"E14.3.2"),sQuery(id+"F0.wireOp",EDGE,"E14.3.3"),sQuery(id+"F0.wireOp",EDGE,"E14.3.4"),sQuery(id+"F0.wireOp",EDGE,"E14.3.5"),sQuery(id+"F0.wireOp",EDGE,"E14.3.6"),sQuery(id+"F0.wireOp",EDGE,"E14.3.7"),sQuery(id+"F0.wireOp",EDGE,"E14.3.8"),sQuery(id+"F0.wireOp",EDGE,"E14.3.9"),sQuery(id+"F0.wireOp",EDGE,"E14.4.0"),sQuery(id+"F0.wireOp",EDGE,"E14.4.1"),sQuery(id+"F0.wireOp",EDGE,"E14.4.2"),sQuery(id+"F0.wireOp",EDGE,"E14.4.3"),sQuery(id+"F0.wireOp",EDGE,"E14.4.4"),sQuery(id+"F0.wireOp",EDGE,"E14.4.5"),sQuery(id+"F0.wireOp",EDGE,"E14.4.6"),sQuery(id+"F0.wireOp",EDGE,"E14.4.7"),sQuery(id+"F0.wireOp",EDGE,"E14.4.8"),sQuery(id+"F0.wireOp",EDGE,"E14.4.9"),sQuery(id+"F0.wireOp",EDGE,"E14.5.0"),sQuery(id+"F0.wireOp",EDGE,"E14.5.1"),sQuery(id+"F0.wireOp",EDGE,"E14.5.2"),sQuery(id+"F0.wireOp",EDGE,"E14.5.3"),sQuery(id+"F0.wireOp",EDGE,"E14.5.4"),sQuery(id+"F0.wireOp",EDGE,"E14.5.5"),sQuery(id+"F0.wireOp",EDGE,"E14.5.6"),sQuery(id+"F0.wireOp",EDGE,"E14.5.7"),sQuery(id+"F0.wireOp",EDGE,"E14.5.8"),sQuery(id+"F0.wireOp",EDGE,"E14.5.9"),sQuery(id+"F0.wireOp",EDGE,"E14.6.0"),sQuery(id+"F0.wireOp",EDGE,"E14.6.1"),sQuery(id+"F0.wireOp",EDGE,"E14.6.2"),sQuery(id+"F0.wireOp",EDGE,"E14.6.3"),sQuery(id+"F0.wireOp",EDGE,"E14.6.4"),sQuery(id+"F0.wireOp",EDGE,"E14.6.5"),sQuery(id+"F0.wireOp",EDGE,"E14.6.6"),sQuery(id+"F0.wireOp",EDGE,"E14.6.7"),sQuery(id+"F0.wireOp",EDGE,"E14.6.8"),sQuery(id+"F0.wireOp",EDGE,"E14.6.9"),sQuery(id+"F0.wireOp",EDGE,"E14.7.0"),sQuery(id+"F0.wireOp",EDGE,"E14.7.1"),sQuery(id+"F0.wireOp",EDGE,"E14.7.2"),sQuery(id+"F0.wireOp",EDGE,"E14.7.3"),sQuery(id+"F0.wireOp",EDGE,"E14.7.4"),sQuery(id+"F0.wireOp",EDGE,"E14.7.5"),sQuery(id+"F0.wireOp",EDGE,"E14.7.6"),sQuery(id+"F0.wireOp",EDGE,"E14.7.7"),sQuery(id+"F0.wireOp",EDGE,"E14.7.8"),sQuery(id+"F0.wireOp",EDGE,"E14.7.9"),sQuery(id+"F0.wireOp",EDGE,"E14.8.0"),sQuery(id+"F0.wireOp",EDGE,"E14.8.1"),sQuery(id+"F0.wireOp",EDGE,"E14.8.2"),sQuery(id+"F0.wireOp",EDGE,"E14.8.3"),sQuery(id+"F0.wireOp",EDGE,"E14.8.4"),sQuery(id+"F0.wireOp",EDGE,"E14.8.5"),sQuery(id+"F0.wireOp",EDGE,"E14.8.6"),sQuery(id+"F0.wireOp",EDGE,"E14.8.7"),sQuery(id+"F0.wireOp",EDGE,"E14.8.8"),sQuery(id+"F0.wireOp",EDGE,"E14.8.9"),sQuery(id+"F0.wireOp",EDGE,"E14.9.0"),sQuery(id+"F0.wireOp",EDGE,"E14.9.1"),sQuery(id+"F0.wireOp",EDGE,"E14.9.2"),sQuery(id+"F0.wireOp",EDGE,"E14.9.3"),sQuery(id+"F0.wireOp",EDGE,"E14.9.4"),sQuery(id+"F0.wireOp",EDGE,"E14.9.5"),sQuery(id+"F0.wireOp",EDGE,"E14.9.6"),sQuery(id+"F0.wireOp",EDGE,"E14.9.7"),sQuery(id+"F0.wireOp",EDGE,"E14.9.8"),sQuery(id+"F0.wireOp",EDGE,"E14.9.9"),sQuery(id+"F0.wireOp",EDGE,"E14.10.0"),sQuery(id+"F0.wireOp",EDGE,"E14.10.1"),sQuery(id+"F0.wireOp",EDGE,"E14.10.2"),sQuery(id+"F0.wireOp",EDGE,"E14.10.3"),sQuery(id+"F0.wireOp",EDGE,"E14.10.4"),sQuery(id+"F0.wireOp",EDGE,"E14.10.5"),sQuery(id+"F0.wireOp",EDGE,"E14.10.6"),sQuery(id+"F0.wireOp",EDGE,"E14.10.7"),sQuery(id+"F0.wireOp",EDGE,"E14.10.8"),sQuery(id+"F0.wireOp",EDGE,"E14.10.9"),sQuery(id+"F0.wireOp",EDGE,"E14.11.0"),sQuery(id+"F0.wireOp",EDGE,"E14.11.1"),sQuery(id+"F0.wireOp",EDGE,"E14.11.2"),sQuery(id+"F0.wireOp",EDGE,"E14.11.3"),sQuery(id+"F0.wireOp",EDGE,"E14.11.4"),sQuery(id+"F0.wireOp",EDGE,"E14.11.5"),sQuery(id+"F0.wireOp",EDGE,"E14.11.6"),sQuery(id+"F0.wireOp",EDGE,"E14.11.7"),sQuery(id+"F0.wireOp",EDGE,"E14.11.8"),sQuery(id+"F0.wireOp",EDGE,"E14.11.9"),sQuery(id+"F0.wireOp",EDGE,"E14.12.0"),sQuery(id+"F0.wireOp",EDGE,"E14.12.1"),sQuery(id+"F0.wireOp",EDGE,"E14.12.2"),sQuery(id+"F0.wireOp",EDGE,"E14.12.3"),sQuery(id+"F0.wireOp",EDGE,"E14.12.4"),sQuery(id+"F0.wireOp",EDGE,"E14.12.5"),sQuery(id+"F0.wireOp",EDGE,"E14.12.6"),sQuery(id+"F0.wireOp",EDGE,"E14.12.7"),sQuery(id+"F0.wireOp",EDGE,"E14.12.8"),sQuery(id+"F0.wireOp",EDGE,"E14.12.9"),sQuery(id+"F0.wireOp",EDGE,"E14.13.0"),sQuery(id+"F0.wireOp",EDGE,"E14.13.1"),sQuery(id+"F0.wireOp",EDGE,"E14.13.2"),sQuery(id+"F0.wireOp",EDGE,"E14.13.3"),sQuery(id+"F0.wireOp",EDGE,"E14.13.4"),sQuery(id+"F0.wireOp",EDGE,"E14.13.5"),sQuery(id+"F0.wireOp",EDGE,"E14.13.6"),sQuery(id+"F0.wireOp",EDGE,"E14.13.7"),sQuery(id+"F0.wireOp",EDGE,"E14.13.8"),sQuery(id+"F0.wireOp",EDGE,"E14.13.9"),sQuery(id+"F0.wireOp",EDGE,"E14.14.0"),sQuery(id+"F0.wireOp",EDGE,"E14.14.1"),sQuery(id+"F0.wireOp",EDGE,"E14.14.2"),sQuery(id+"F0.wireOp",EDGE,"E14.14.3"),sQuery(id+"F0.wireOp",EDGE,"E14.14.4"),sQuery(id+"F0.wireOp",EDGE,"E14.14.5"),sQuery(id+"F0.wireOp",EDGE,"E14.14.6"),sQuery(id+"F0.wireOp",EDGE,"E14.14.7"),sQuery(id+"F0.wireOp",EDGE,"E14.14.8"),sQuery(id+"F0.wireOp",EDGE,"E14.14.9"),sQuery(id+"F0.wireOp",EDGE,"E14.15.0"),sQuery(id+"F0.wireOp",EDGE,"E14.15.1"),sQuery(id+"F0.wireOp",EDGE,"E14.15.2"),sQuery(id+"F0.wireOp",EDGE,"E14.15.3"),sQuery(id+"F0.wireOp",EDGE,"E14.15.4"),sQuery(id+"F0.wireOp",EDGE,"E14.15.5"),sQuery(id+"F0.wireOp",EDGE,"E14.15.6"),sQuery(id+"F0.wireOp",EDGE,"E14.15.7"),sQuery(id+"F0.wireOp",EDGE,"E14.15.8"),sQuery(id+"F0.wireOp",EDGE,"E14.15.9"),sQuery(id+"F0.wireOp",EDGE,"E14.16.0"),sQuery(id+"F0.wireOp",EDGE,"E14.16.1"),sQuery(id+"F0.wireOp",EDGE,"E14.16.2"),sQuery(id+"F0.wireOp",EDGE,"E14.16.3"),sQuery(id+"F0.wireOp",EDGE,"E14.16.4"),sQuery(id+"F0.wireOp",EDGE,"E14.16.5"),sQuery(id+"F0.wireOp",EDGE,"E14.16.6"),sQuery(id+"F0.wireOp",EDGE,"E14.16.7"),sQuery(id+"F0.wireOp",EDGE,"E14.16.8"),sQuery(id+"F0.wireOp",EDGE,"E14.16.9"),sQuery(id+"F0.wireOp",EDGE,"E14.17.0"),sQuery(id+"F0.wireOp",EDGE,"E14.17.1"),sQuery(id+"F0.wireOp",EDGE,"E14.17.2"),sQuery(id+"F0.wireOp",EDGE,"E14.17.3"),sQuery(id+"F0.wireOp",EDGE,"E14.17.4"),sQuery(id+"F0.wireOp",EDGE,"E14.17.5"),sQuery(id+"F0.wireOp",EDGE,"E14.17.6"),sQuery(id+"F0.wireOp",EDGE,"E14.17.7"),sQuery(id+"F0.wireOp",EDGE,"E14.17.8"),sQuery(id+"F0.wireOp",EDGE,"E14.17.9"),sQuery(id+"F0.wireOp",EDGE,"E14.18.0"),sQuery(id+"F0.wireOp",EDGE,"E14.18.1"),sQuery(id+"F0.wireOp",EDGE,"E14.18.2"),sQuery(id+"F0.wireOp",EDGE,"E14.18.3"),sQuery(id+"F0.wireOp",EDGE,"E14.18.4"),sQuery(id+"F0.wireOp",EDGE,"E14.18.5"),sQuery(id+"F0.wireOp",EDGE,"E14.18.6"),sQuery(id+"F0.wireOp",EDGE,"E14.18.7"),sQuery(id+"F0.wireOp",EDGE,"E14.18.8"),sQuery(id+"F0.wireOp",EDGE,"E14.18.9"),sQuery(id+"F0.wireOp",EDGE,"E14.19.0"),sQuery(id+"F0.wireOp",EDGE,"E14.19.1"),sQuery(id+"F0.wireOp",EDGE,"E14.19.2"),sQuery(id+"F0.wireOp",EDGE,"E14.19.3"),sQuery(id+"F0.wireOp",EDGE,"E14.19.4"),sQuery(id+"F0.wireOp",EDGE,"E14.19.5"),sQuery(id+"F0.wireOp",EDGE,"E14.19.6"),sQuery(id+"F0.wireOp",EDGE,"E14.19.7"),sQuery(id+"F0.wireOp",EDGE,"E14.19.8"),sQuery(id+"F0.wireOp",EDGE,"E14.19.9"),sQuery(id+"F0.wireOp",EDGE,"E14.20.0"),sQuery(id+"F0.wireOp",EDGE,"E14.20.1"),sQuery(id+"F0.wireOp",EDGE,"E14.20.2"),sQuery(id+"F0.wireOp",EDGE,"E14.20.3"),sQuery(id+"F0.wireOp",EDGE,"E14.20.4"),sQuery(id+"F0.wireOp",EDGE,"E14.20.5"),sQuery(id+"F0.wireOp",EDGE,"E14.20.6"),sQuery(id+"F0.wireOp",EDGE,"E14.20.7"),sQuery(id+"F0.wireOp",EDGE,"E14.20.8"),sQuery(id+"F0.wireOp",EDGE,"E14.20.9"),sQuery(id+"F0.wireOp",EDGE,"E14.21.0"),sQuery(id+"F0.wireOp",EDGE,"E14.21.1"),sQuery(id+"F0.wireOp",EDGE,"E14.21.2"),sQuery(id+"F0.wireOp",EDGE,"E14.21.3"),sQuery(id+"F0.wireOp",EDGE,"E14.21.4"),sQuery(id+"F0.wireOp",EDGE,"E14.21.5"),sQuery(id+"F0.wireOp",EDGE,"E14.21.6"),sQuery(id+"F0.wireOp",EDGE,"E14.21.7"),sQuery(id+"F0.wireOp",EDGE,"E14.21.8"),sQuery(id+"F0.wireOp",EDGE,"E14.21.9"),sQuery(id+"F0.wireOp",EDGE,"E14.22.0"),sQuery(id+"F0.wireOp",EDGE,"E14.22.1"),sQuery(id+"F0.wireOp",EDGE,"E14.22.2"),sQuery(id+"F0.wireOp",EDGE,"E14.22.3"),sQuery(id+"F0.wireOp",EDGE,"E14.22.4"),sQuery(id+"F0.wireOp",EDGE,"E14.22.5"),sQuery(id+"F0.wireOp",EDGE,"E14.22.6"),sQuery(id+"F0.wireOp",EDGE,"E14.22.7"),sQuery(id+"F0.wireOp",EDGE,"E14.22.8"),sQuery(id+"F0.wireOp",EDGE,"E14.22.9"),sQuery(id+"F0.wireOp",EDGE,"E14.23.0"),sQuery(id+"F0.wireOp",EDGE,"E14.23.1"),sQuery(id+"F0.wireOp",EDGE,"E14.23.2"),sQuery(id+"F0.wireOp",EDGE,"E14.23.3"),sQuery(id+"F0.wireOp",EDGE,"E14.23.4"),sQuery(id+"F0.wireOp",EDGE,"E14.23.5"),sQuery(id+"F0.wireOp",EDGE,"E14.23.6"),sQuery(id+"F0.wireOp",EDGE,"E14.23.7"),sQuery(id+"F0.wireOp",EDGE,"E14.23.8"),sQuery(id+"F0.wireOp",EDGE,"E14.23.9"),sQuery(id+"F0.wireOp",EDGE,"E14.24.0"),sQuery(id+"F0.wireOp",EDGE,"E14.24.1"),sQuery(id+"F0.wireOp",EDGE,"E14.24.2"),sQuery(id+"F0.wireOp",EDGE,"E14.24.3"),sQuery(id+"F0.wireOp",EDGE,"E14.24.4"),sQuery(id+"F0.wireOp",EDGE,"E14.24.5"),sQuery(id+"F0.wireOp",EDGE,"E14.24.6"),sQuery(id+"F0.wireOp",EDGE,"E14.24.7"),sQuery(id+"F0.wireOp",EDGE,"E14.24.8"),sQuery(id+"F0.wireOp",EDGE,"E14.24.9"),sQuery(id+"F0.wireOp",EDGE,"E14.25.0"),sQuery(id+"F0.wireOp",EDGE,"E14.25.1"),sQuery(id+"F0.wireOp",EDGE,"E14.25.2"),sQuery(id+"F0.wireOp",EDGE,"E14.25.3"),sQuery(id+"F0.wireOp",EDGE,"E14.25.4"),sQuery(id+"F0.wireOp",EDGE,"E14.25.5"),sQuery(id+"F0.wireOp",EDGE,"E14.25.6"),sQuery(id+"F0.wireOp",EDGE,"E14.25.7"),sQuery(id+"F0.wireOp",EDGE,"E14.25.8"),sQuery(id+"F0.wireOp",EDGE,"E14.25.9"),sQuery(id+"F0.wireOp",EDGE,"E14.26.0"),sQuery(id+"F0.wireOp",EDGE,"E14.26.1"),sQuery(id+"F0.wireOp",EDGE,"E14.26.2"),sQuery(id+"F0.wireOp",EDGE,"E14.26.3"),sQuery(id+"F0.wireOp",EDGE,"E14.26.4"),sQuery(id+"F0.wireOp",EDGE,"E14.26.5"),sQuery(id+"F0.wireOp",EDGE,"E14.26.6"),sQuery(id+"F0.wireOp",EDGE,"E14.26.7"),sQuery(id+"F0.wireOp",EDGE,"E14.26.8"),sQuery(id+"F0.wireOp",EDGE,"E14.26.9"),sQuery(id+"F0.wireOp",EDGE,"E14.27.0"),sQuery(id+"F0.wireOp",EDGE,"E14.27.1"),sQuery(id+"F0.wireOp",EDGE,"E14.27.2"),sQuery(id+"F0.wireOp",EDGE,"E14.27.3"),sQuery(id+"F0.wireOp",EDGE,"E14.27.4"),sQuery(id+"F0.wireOp",EDGE,"E14.27.5"),sQuery(id+"F0.wireOp",EDGE,"E14.27.6"),sQuery(id+"F0.wireOp",EDGE,"E14.27.7"),sQuery(id+"F0.wireOp",EDGE,"E14.27.8"),sQuery(id+"F0.wireOp",EDGE,"E14.27.9"),sQuery(id+"F0.wireOp",EDGE,"E14.28.0"),sQuery(id+"F0.wireOp",EDGE,"E14.28.1"),sQuery(id+"F0.wireOp",EDGE,"E14.28.2"),sQuery(id+"F0.wireOp",EDGE,"E14.28.3"),sQuery(id+"F0.wireOp",EDGE,"E14.28.4"),sQuery(id+"F0.wireOp",EDGE,"E14.28.5"),sQuery(id+"F0.wireOp",EDGE,"E14.28.6"),sQuery(id+"F0.wireOp",EDGE,"E14.28.7"),sQuery(id+"F0.wireOp",EDGE,"E14.28.8"),sQuery(id+"F0.wireOp",EDGE,"E14.28.9"),sQuery(id+"F0.wireOp",EDGE,"E14.29.0"),sQuery(id+"F0.wireOp",EDGE,"E14.29.1"),sQuery(id+"F0.wireOp",EDGE,"E14.29.2"),sQuery(id+"F0.wireOp",EDGE,"E14.29.3"),sQuery(id+"F0.wireOp",EDGE,"E14.29.4"),sQuery(id+"F0.wireOp",EDGE,"E14.29.5"),sQuery(id+"F0.wireOp",EDGE,"E14.29.6"),sQuery(id+"F0.wireOp",EDGE,"E14.29.7"),sQuery(id+"F0.wireOp",EDGE,"E14.29.8"),sQuery(id+"F0.wireOp",EDGE,"E14.29.9"),sQuery(id+"F0.wireOp",EDGE,"E14.30.0"),sQuery(id+"F0.wireOp",EDGE,"E14.30.1"),sQuery(id+"F0.wireOp",EDGE,"E14.30.2"),sQuery(id+"F0.wireOp",EDGE,"E14.30.3"),sQuery(id+"F0.wireOp",EDGE,"E14.30.4"),sQuery(id+"F0.wireOp",EDGE,"E14.30.5"),sQuery(id+"F0.wireOp",EDGE,"E14.30.6"),sQuery(id+"F0.wireOp",EDGE,"E14.30.7"),sQuery(id+"F0.wireOp",EDGE,"E14.30.8"),sQuery(id+"F0.wireOp",EDGE,"E14.30.9"),sQuery(id+"F0.wireOp",EDGE,"E14.31.0"),sQuery(id+"F0.wireOp",EDGE,"E14.31.1"),sQuery(id+"F0.wireOp",EDGE,"E14.31.2"),sQuery(id+"F0.wireOp",EDGE,"E14.31.3"),sQuery(id+"F0.wireOp",EDGE,"E14.31.4"),sQuery(id+"F0.wireOp",EDGE,"E14.31.5"),sQuery(id+"F0.wireOp",EDGE,"E14.31.6"),sQuery(id+"F0.wireOp",EDGE,"E14.31.7"),sQuery(id+"F0.wireOp",EDGE,"E14.31.8"),sQuery(id+"F0.wireOp",EDGE,"E14.31.9"),sQuery(id+"F0.wireOp",EDGE,"E14.32.0"),sQuery(id+"F0.wireOp",EDGE,"E14.32.1"),sQuery(id+"F0.wireOp",EDGE,"E14.32.2"),sQuery(id+"F0.wireOp",EDGE,"E14.32.3"),sQuery(id+"F0.wireOp",EDGE,"E14.32.4"),sQuery(id+"F0.wireOp",EDGE,"E14.32.5"),sQuery(id+"F0.wireOp",EDGE,"E14.32.6"),sQuery(id+"F0.wireOp",EDGE,"E14.32.7"),sQuery(id+"F0.wireOp",EDGE,"E14.32.8"),sQuery(id+"F0.wireOp",EDGE,"E14.32.9"),sQuery(id+"F0.wireOp",EDGE,"E14.33.0"),sQuery(id+"F0.wireOp",EDGE,"E14.33.1"),sQuery(id+"F0.wireOp",EDGE,"E14.33.2"),sQuery(id+"F0.wireOp",EDGE,"E14.33.3"),sQuery(id+"F0.wireOp",EDGE,"E14.33.4"),sQuery(id+"F0.wireOp",EDGE,"E14.33.5"),sQuery(id+"F0.wireOp",EDGE,"E14.33.6"),sQuery(id+"F0.wireOp",EDGE,"E14.33.7"),sQuery(id+"F0.wireOp",EDGE,"E14.33.8"),sQuery(id+"F0.wireOp",EDGE,"E14.33.9"),sQuery(id+"F0.wireOp",EDGE,"E14.34.0"),sQuery(id+"F0.wireOp",EDGE,"E14.34.1"),sQuery(id+"F0.wireOp",EDGE,"E14.34.2"),sQuery(id+"F0.wireOp",EDGE,"E14.34.3"),sQuery(id+"F0.wireOp",EDGE,"E14.34.4"),sQuery(id+"F0.wireOp",EDGE,"E14.34.5"),sQuery(id+"F0.wireOp",EDGE,"E14.34.6"),sQuery(id+"F0.wireOp",EDGE,"E14.34.7"),sQuery(id+"F0.wireOp",EDGE,"E14.34.8"),sQuery(id+"F0.wireOp",EDGE,"E14.34.9"),sQuery(id+"F0.wireOp",EDGE,"E14.35.0"),sQuery(id+"F0.wireOp",EDGE,"E14.35.1"),sQuery(id+"F0.wireOp",EDGE,"E14.35.2"),sQuery(id+"F0.wireOp",EDGE,"E14.35.3"),sQuery(id+"F0.wireOp",EDGE,"E14.35.4"),sQuery(id+"F0.wireOp",EDGE,"E14.35.5"),sQuery(id+"F0.wireOp",EDGE,"E14.35.6"),sQuery(id+"F0.wireOp",EDGE,"E14.35.7"),sQuery(id+"F0.wireOp",EDGE,"E14.35.8"),sQuery(id+"F0.wireOp",EDGE,"E14.35.9"),sQuery(id+"F0.wireOp",EDGE,"E14.36.0"),sQuery(id+"F0.wireOp",EDGE,"E14.36.1"),sQuery(id+"F0.wireOp",EDGE,"E14.36.2"),sQuery(id+"F0.wireOp",EDGE,"E14.36.3"),sQuery(id+"F0.wireOp",EDGE,"E14.36.4"),sQuery(id+"F0.wireOp",EDGE,"E14.36.5"),sQuery(id+"F0.wireOp",EDGE,"E14.36.6"),sQuery(id+"F0.wireOp",EDGE,"E14.36.7"),sQuery(id+"F0.wireOp",EDGE,"E14.36.8"),sQuery(id+"F0.wireOp",EDGE,"E14.36.9"),sQuery(id+"F0.wireOp",EDGE,"E14.37.0"),sQuery(id+"F0.wireOp",EDGE,"E14.37.1"),sQuery(id+"F0.wireOp",EDGE,"E14.37.2"),sQuery(id+"F0.wireOp",EDGE,"E14.37.3"),sQuery(id+"F0.wireOp",EDGE,"E14.37.4"),sQuery(id+"F0.wireOp",EDGE,"E14.37.5"),sQuery(id+"F0.wireOp",EDGE,"E14.37.6"),sQuery(id+"F0.wireOp",EDGE,"E14.37.7"),sQuery(id+"F0.wireOp",EDGE,"E14.37.8"),sQuery(id+"F0.wireOp",EDGE,"E14.37.9"),sQuery(id+"F0.wireOp",EDGE,"E14.38.0"),sQuery(id+"F0.wireOp",EDGE,"E14.38.1"),sQuery(id+"F0.wireOp",EDGE,"E14.38.2"),sQuery(id+"F0.wireOp",EDGE,"E14.38.3"),sQuery(id+"F0.wireOp",EDGE,"E14.38.4"),sQuery(id+"F0.wireOp",EDGE,"E14.38.5"),sQuery(id+"F0.wireOp",EDGE,"E14.38.6"),sQuery(id+"F0.wireOp",EDGE,"E14.38.7"),sQuery(id+"F0.wireOp",EDGE,"E14.38.8"),sQuery(id+"F0.wireOp",EDGE,"E14.38.9"),sQuery(id+"F0.wireOp",EDGE,"E14.39.0"),sQuery(id+"F0.wireOp",EDGE,"E14.39.1"),sQuery(id+"F0.wireOp",EDGE,"E14.39.2"),sQuery(id+"F0.wireOp",EDGE,"E14.39.3"),sQuery(id+"F0.wireOp",EDGE,"E14.39.4"),sQuery(id+"F0.wireOp",EDGE,"E14.39.5"),sQuery(id+"F0.wireOp",EDGE,"E14.39.6"),sQuery(id+"F0.wireOp",EDGE,"E14.39.7"),sQuery(id+"F0.wireOp",EDGE,"E14.39.8"),sQuery(id+"F0.wireOp",EDGE,"E14.39.9"),sQuery(id+"F0.wireOp",EDGE,"E14.40.0"),sQuery(id+"F0.wireOp",EDGE,"E14.40.1"),sQuery(id+"F0.wireOp",EDGE,"E14.40.2"),sQuery(id+"F0.wireOp",EDGE,"E14.40.3"),sQuery(id+"F0.wireOp",EDGE,"E14.40.4"),sQuery(id+"F0.wireOp",EDGE,"E14.40.5"),sQuery(id+"F0.wireOp",EDGE,"E14.40.6"),sQuery(id+"F0.wireOp",EDGE,"E14.40.7"),sQuery(id+"F0.wireOp",EDGE,"E14.40.8"),sQuery(id+"F0.wireOp",EDGE,"E14.40.9"),sQuery(id+"F0.wireOp",EDGE,"E14.41.0"),sQuery(id+"F0.wireOp",EDGE,"E14.41.1"),sQuery(id+"F0.wireOp",EDGE,"E14.41.2"),sQuery(id+"F0.wireOp",EDGE,"E14.41.3"),sQuery(id+"F0.wireOp",EDGE,"E14.41.4"),sQuery(id+"F0.wireOp",EDGE,"E14.41.5"),sQuery(id+"F0.wireOp",EDGE,"E14.41.6"),sQuery(id+"F0.wireOp",EDGE,"E14.41.7"),sQuery(id+"F0.wireOp",EDGE,"E14.41.8"),sQuery(id+"F0.wireOp",EDGE,"E14.41.9"),sQuery(id+"F0.wireOp",EDGE,"E14.42.0"),sQuery(id+"F0.wireOp",EDGE,"E14.42.1"),sQuery(id+"F0.wireOp",EDGE,"E14.42.2"),sQuery(id+"F0.wireOp",EDGE,"E14.42.3"),sQuery(id+"F0.wireOp",EDGE,"E14.42.4"),sQuery(id+"F0.wireOp",EDGE,"E14.42.5"),sQuery(id+"F0.wireOp",EDGE,"E14.42.6"),sQuery(id+"F0.wireOp",EDGE,"E14.42.7"),sQuery(id+"F0.wireOp",EDGE,"E14.42.8"),sQuery(id+"F0.wireOp",EDGE,"E14.42.9"),sQuery(id+"F0.wireOp",EDGE,"E14.43.0"),sQuery(id+"F0.wireOp",EDGE,"E14.43.1"),sQuery(id+"F0.wireOp",EDGE,"E14.43.2"),sQuery(id+"F0.wireOp",EDGE,"E14.43.3"),sQuery(id+"F0.wireOp",EDGE,"E14.43.4"),sQuery(id+"F0.wireOp",EDGE,"E14.43.5"),sQuery(id+"F0.wireOp",EDGE,"E14.43.6"),sQuery(id+"F0.wireOp",EDGE,"E14.43.7"),sQuery(id+"F0.wireOp",EDGE,"E14.43.8"),sQuery(id+"F0.wireOp",EDGE,"E14.43.9"),sQuery(id+"F0.wireOp",EDGE,"E14.44.0"),sQuery(id+"F0.wireOp",EDGE,"E14.44.1"),sQuery(id+"F0.wireOp",EDGE,"E14.44.2"),sQuery(id+"F0.wireOp",EDGE,"E14.44.3"),sQuery(id+"F0.wireOp",EDGE,"E14.44.4"),sQuery(id+"F0.wireOp",EDGE,"E14.44.5"),sQuery(id+"F0.wireOp",EDGE,"E14.44.6"),sQuery(id+"F0.wireOp",EDGE,"E14.44.7"),sQuery(id+"F0.wireOp",EDGE,"E14.44.8"),sQuery(id+"F0.wireOp",EDGE,"E14.44.9"),sQuery(id+"F0.wireOp",EDGE,"E14.45.0"),sQuery(id+"F0.wireOp",EDGE,"E14.45.1"),sQuery(id+"F0.wireOp",EDGE,"E14.45.2"),sQuery(id+"F0.wireOp",EDGE,"E14.45.3"),sQuery(id+"F0.wireOp",EDGE,"E14.45.4"),sQuery(id+"F0.wireOp",EDGE,"E14.45.5"),sQuery(id+"F0.wireOp",EDGE,"E14.45.6"),sQuery(id+"F0.wireOp",EDGE,"E14.45.7"),sQuery(id+"F0.wireOp",EDGE,"E14.45.8"),sQuery(id+"F0.wireOp",EDGE,"E14.45.9"),sQuery(id+"F0.wireOp",EDGE,"E14.46.0"),sQuery(id+"F0.wireOp",EDGE,"E14.46.1"),sQuery(id+"F0.wireOp",EDGE,"E14.46.2"),sQuery(id+"F0.wireOp",EDGE,"E14.46.3"),sQuery(id+"F0.wireOp",EDGE,"E14.46.4"),sQuery(id+"F0.wireOp",EDGE,"E14.46.5"),sQuery(id+"F0.wireOp",EDGE,"E14.46.6"),sQuery(id+"F0.wireOp",EDGE,"E14.46.7"),sQuery(id+"F0.wireOp",EDGE,"E14.46.8"),sQuery(id+"F0.wireOp",EDGE,"E14.46.9"),sQuery(id+"F0.wireOp",EDGE,"E14.47.0"),sQuery(id+"F0.wireOp",EDGE,"E14.47.1"),sQuery(id+"F0.wireOp",EDGE,"E14.47.2"),sQuery(id+"F0.wireOp",EDGE,"E14.47.3"),sQuery(id+"F0.wireOp",EDGE,"E14.47.4"),sQuery(id+"F0.wireOp",EDGE,"E14.47.5"),sQuery(id+"F0.wireOp",EDGE,"E14.47.6"),sQuery(id+"F0.wireOp",EDGE,"E14.47.7"),sQuery(id+"F0.wireOp",EDGE,"E14.47.8"),sQuery(id+"F0.wireOp",EDGE,"E14.47.9"),sQuery(id+"F0.wireOp",EDGE,"E14.48.0"),sQuery(id+"F0.wireOp",EDGE,"E14.48.1"),sQuery(id+"F0.wireOp",EDGE,"E14.48.2"),sQuery(id+"F0.wireOp",EDGE,"E14.48.3"),sQuery(id+"F0.wireOp",EDGE,"E14.48.4"),sQuery(id+"F0.wireOp",EDGE,"E14.48.5"),sQuery(id+"F0.wireOp",EDGE,"E14.48.6"),sQuery(id+"F0.wireOp",EDGE,"E14.48.7"),sQuery(id+"F0.wireOp",EDGE,"E14.48.8"),sQuery(id+"F0.wireOp",EDGE,"E14.48.9"),sQuery(id+"F0.wireOp",EDGE,"E14.49.0"),sQuery(id+"F0.wireOp",EDGE,"E14.49.1"),sQuery(id+"F0.wireOp",EDGE,"E14.49.2"),sQuery(id+"F0.wireOp",EDGE,"E14.49.3"),sQuery(id+"F0.wireOp",EDGE,"E14.49.4"),sQuery(id+"F0.wireOp",EDGE,"E14.49.5"),sQuery(id+"F0.wireOp",EDGE,"E14.49.6"),sQuery(id+"F0.wireOp",EDGE,"E14.49.7"),sQuery(id+"F0.wireOp",EDGE,"E14.49.8"),sQuery(id+"F0.wireOp",EDGE,"E14.49.9"),sQuery(id+"F0.wireOp",EDGE,"E14.50.0"),sQuery(id+"F0.wireOp",EDGE,"E14.50.1"),sQuery(id+"F0.wireOp",EDGE,"E14.50.2"),sQuery(id+"F0.wireOp",EDGE,"E14.50.3"),sQuery(id+"F0.wireOp",EDGE,"E14.50.4"),sQuery(id+"F0.wireOp",EDGE,"E14.50.5"),sQuery(id+"F0.wireOp",EDGE,"E14.50.6"),sQuery(id+"F0.wireOp",EDGE,"E14.50.7"),sQuery(id+"F0.wireOp",EDGE,"E14.50.8"),sQuery(id+"F0.wireOp",EDGE,"E14.50.9"),sQuery(id+"F0.wireOp",EDGE,"E14.51.0"),sQuery(id+"F0.wireOp",EDGE,"E14.51.1"),sQuery(id+"F0.wireOp",EDGE,"E14.51.2"),sQuery(id+"F0.wireOp",EDGE,"E14.51.3"),sQuery(id+"F0.wireOp",EDGE,"E14.51.4"),sQuery(id+"F0.wireOp",EDGE,"E14.51.5"),sQuery(id+"F0.wireOp",EDGE,"E14.51.6"),sQuery(id+"F0.wireOp",EDGE,"E14.51.7"),sQuery(id+"F0.wireOp",EDGE,"E14.51.8"),sQuery(id+"F0.wireOp",EDGE,"E14.51.9"),sQuery(id+"F0.wireOp",EDGE,"E14.52.0"),sQuery(id+"F0.wireOp",EDGE,"E14.52.1"),sQuery(id+"F0.wireOp",EDGE,"E14.52.2"),sQuery(id+"F0.wireOp",EDGE,"E14.52.3"),sQuery(id+"F0.wireOp",EDGE,"E14.52.4"),sQuery(id+"F0.wireOp",EDGE,"E14.52.5"),sQuery(id+"F0.wireOp",EDGE,"E14.52.6"),sQuery(id+"F0.wireOp",EDGE,"E14.52.7"),sQuery(id+"F0.wireOp",EDGE,"E14.52.8"),sQuery(id+"F0.wireOp",EDGE,"E14.52.9"),sQuery(id+"F0.wireOp",EDGE,"E14.53.0"),sQuery(id+"F0.wireOp",EDGE,"E14.53.1"),sQuery(id+"F0.wireOp",EDGE,"E14.53.2"),sQuery(id+"F0.wireOp",EDGE,"E14.53.3"),sQuery(id+"F0.wireOp",EDGE,"E14.53.4"),sQuery(id+"F0.wireOp",EDGE,"E14.53.5"),sQuery(id+"F0.wireOp",EDGE,"E14.53.6"),sQuery(id+"F0.wireOp",EDGE,"E14.53.7"),sQuery(id+"F0.wireOp",EDGE,"E14.53.8"),sQuery(id+"F0.wireOp",EDGE,"E14.53.9"),sQuery(id+"F0.wireOp",EDGE,"E14.54.0"),sQuery(id+"F0.wireOp",EDGE,"E14.54.1"),sQuery(id+"F0.wireOp",EDGE,"E14.54.2"),sQuery(id+"F0.wireOp",EDGE,"E14.54.3"),sQuery(id+"F0.wireOp",EDGE,"E14.54.4"),sQuery(id+"F0.wireOp",EDGE,"E14.54.5"),sQuery(id+"F0.wireOp",EDGE,"E14.54.6"),sQuery(id+"F0.wireOp",EDGE,"E14.54.7"),sQuery(id+"F0.wireOp",EDGE,"E14.54.8"),sQuery(id+"F0.wireOp",EDGE,"E14.54.9"),sQuery(id+"F0.wireOp",EDGE,"E14.55.0"),sQuery(id+"F0.wireOp",EDGE,"E14.55.1"),sQuery(id+"F0.wireOp",EDGE,"E14.55.2"),sQuery(id+"F0.wireOp",EDGE,"E14.55.3"),sQuery(id+"F0.wireOp",EDGE,"E14.55.4"),sQuery(id+"F0.wireOp",EDGE,"E14.55.5"),sQuery(id+"F0.wireOp",EDGE,"E14.55.6"),sQuery(id+"F0.wireOp",EDGE,"E14.55.7"),sQuery(id+"F0.wireOp",EDGE,"E14.55.8"),sQuery(id+"F0.wireOp",EDGE,"E14.55.9"),sQuery(id+"F0.wireOp",EDGE,"E14.56.0"),sQuery(id+"F0.wireOp",EDGE,"E14.56.1"),sQuery(id+"F0.wireOp",EDGE,"E14.56.2"),sQuery(id+"F0.wireOp",EDGE,"E14.56.3"),sQuery(id+"F0.wireOp",EDGE,"E14.56.4"),sQuery(id+"F0.wireOp",EDGE,"E14.56.5"),sQuery(id+"F0.wireOp",EDGE,"E14.56.6"),sQuery(id+"F0.wireOp",EDGE,"E14.56.7"),sQuery(id+"F0.wireOp",EDGE,"E14.56.8"),sQuery(id+"F0.wireOp",EDGE,"E14.56.9"),sQuery(id+"F0.wireOp",EDGE,"E14.57.0"),sQuery(id+"F0.wireOp",EDGE,"E14.57.1"),sQuery(id+"F0.wireOp",EDGE,"E14.57.2"),sQuery(id+"F0.wireOp",EDGE,"E14.57.3"),sQuery(id+"F0.wireOp",EDGE,"E14.57.4"),sQuery(id+"F0.wireOp",EDGE,"E14.57.5"),sQuery(id+"F0.wireOp",EDGE,"E14.57.6"),sQuery(id+"F0.wireOp",EDGE,"E14.57.7"),sQuery(id+"F0.wireOp",EDGE,"E14.57.8"),sQuery(id+"F0.wireOp",EDGE,"E14.57.9"),sQuery(id+"F0.wireOp",EDGE,"E14.58.0"),sQuery(id+"F0.wireOp",EDGE,"E14.58.1"),sQuery(id+"F0.wireOp",EDGE,"E14.58.2"),sQuery(id+"F0.wireOp",EDGE,"E14.58.3"),sQuery(id+"F0.wireOp",EDGE,"E14.58.4"),sQuery(id+"F0.wireOp",EDGE,"E14.58.5"),sQuery(id+"F0.wireOp",EDGE,"E14.58.6"),sQuery(id+"F0.wireOp",EDGE,"E14.58.7"),sQuery(id+"F0.wireOp",EDGE,"E14.58.8"),sQuery(id+"F0.wireOp",EDGE,"E14.58.9"),sQuery(id+"F0.wireOp",EDGE,"E14.59.0"),sQuery(id+"F0.wireOp",EDGE,"E14.59.1"),sQuery(id+"F0.wireOp",EDGE,"E14.59.2"),sQuery(id+"F0.wireOp",EDGE,"E14.59.3"),sQuery(id+"F0.wireOp",EDGE,"E14.59.4"),sQuery(id+"F0.wireOp",EDGE,"E14.59.5"),sQuery(id+"F0.wireOp",EDGE,"E14.59.6"),sQuery(id+"F0.wireOp",EDGE,"E14.59.7"),sQuery(id+"F0.wireOp",EDGE,"E14.59.8"),sQuery(id+"F0.wireOp",EDGE,"E14.59.9"),sQuery(id+"F0.wireOp",EDGE,"E14.60.0"),sQuery(id+"F0.wireOp",EDGE,"E14.60.1"),sQuery(id+"F0.wireOp",EDGE,"E14.60.2"),sQuery(id+"F0.wireOp",EDGE,"E14.60.3"),sQuery(id+"F0.wireOp",EDGE,"E14.60.4"),sQuery(id+"F0.wireOp",EDGE,"E14.60.5"),sQuery(id+"F0.wireOp",EDGE,"E14.60.6"),sQuery(id+"F0.wireOp",EDGE,"E14.60.7"),sQuery(id+"F0.wireOp",EDGE,"E14.60.8"),sQuery(id+"F0.wireOp",EDGE,"E14.60.9"),sQuery(id+"F0.wireOp",EDGE,"E14.61.0"),sQuery(id+"F0.wireOp",EDGE,"E14.61.1"),sQuery(id+"F0.wireOp",EDGE,"E14.61.2"),sQuery(id+"F0.wireOp",EDGE,"E14.61.3"),sQuery(id+"F0.wireOp",EDGE,"E14.61.4"),sQuery(id+"F0.wireOp",EDGE,"E14.61.5"),sQuery(id+"F0.wireOp",EDGE,"E14.61.6"),sQuery(id+"F0.wireOp",EDGE,"E14.61.7"),sQuery(id+"F0.wireOp",EDGE,"E14.61.8"),sQuery(id+"F0.wireOp",EDGE,"E14.61.9"),sQuery(id+"F0.wireOp",EDGE,"E14.62.0"),sQuery(id+"F0.wireOp",EDGE,"E14.62.1"),sQuery(id+"F0.wireOp",EDGE,"E14.62.2"),sQuery(id+"F0.wireOp",EDGE,"E14.62.3"),sQuery(id+"F0.wireOp",EDGE,"E14.62.4"),sQuery(id+"F0.wireOp",EDGE,"E14.62.5"),sQuery(id+"F0.wireOp",EDGE,"E14.62.6"),sQuery(id+"F0.wireOp",EDGE,"E14.62.7"),sQuery(id+"F0.wireOp",EDGE,"E14.62.8"),sQuery(id+"F0.wireOp",EDGE,"E14.62.9"),sQuery(id+"F0.wireOp",EDGE,"E14.63.0"),sQuery(id+"F0.wireOp",EDGE,"E14.63.1"),sQuery(id+"F0.wireOp",EDGE,"E14.63.2"),sQuery(id+"F0.wireOp",EDGE,"E14.63.3"),sQuery(id+"F0.wireOp",EDGE,"E14.63.4"),sQuery(id+"F0.wireOp",EDGE,"E14.63.5"),sQuery(id+"F0.wireOp",EDGE,"E14.63.6"),sQuery(id+"F0.wireOp",EDGE,"E14.63.7"),sQuery(id+"F0.wireOp",EDGE,"E14.63.8"),sQuery(id+"F0.wireOp",EDGE,"E14.63.9"),sQuery(id+"F0.wireOp",EDGE,"E14.64.0"),sQuery(id+"F0.wireOp",EDGE,"E14.64.1"),sQuery(id+"F0.wireOp",EDGE,"E14.64.2"),sQuery(id+"F0.wireOp",EDGE,"E14.64.3"),sQuery(id+"F0.wireOp",EDGE,"E14.64.4"),sQuery(id+"F0.wireOp",EDGE,"E14.64.5"),sQuery(id+"F0.wireOp",EDGE,"E14.64.6"),sQuery(id+"F0.wireOp",EDGE,"E14.64.7"),sQuery(id+"F0.wireOp",EDGE,"E14.64.8"),sQuery(id+"F0.wireOp",EDGE,"E14.64.9"),sQuery(id+"F0.wireOp",EDGE,"E14.65.0"),sQuery(id+"F0.wireOp",EDGE,"E14.65.1"),sQuery(id+"F0.wireOp",EDGE,"E14.65.2"),sQuery(id+"F0.wireOp",EDGE,"E14.65.3"),sQuery(id+"F0.wireOp",EDGE,"E14.65.4"),sQuery(id+"F0.wireOp",EDGE,"E14.65.5"),sQuery(id+"F0.wireOp",EDGE,"E14.65.6"),sQuery(id+"F0.wireOp",EDGE,"E14.65.7"),sQuery(id+"F0.wireOp",EDGE,"E14.65.8"),sQuery(id+"F0.wireOp",EDGE,"E14.65.9"),sQuery(id+"F0.wireOp",EDGE,"E14.66.0"),sQuery(id+"F0.wireOp",EDGE,"E14.66.1"),sQuery(id+"F0.wireOp",EDGE,"E14.66.2"),sQuery(id+"F0.wireOp",EDGE,"E14.66.3"),sQuery(id+"F0.wireOp",EDGE,"E14.66.4"),sQuery(id+"F0.wireOp",EDGE,"E14.66.5"),sQuery(id+"F0.wireOp",EDGE,"E14.66.6"),sQuery(id+"F0.wireOp",EDGE,"E14.66.7"),sQuery(id+"F0.wireOp",EDGE,"E14.66.8"),sQuery(id+"F0.wireOp",EDGE,"E14.66.9"),sQuery(id+"F0.wireOp",EDGE,"E14.67.0"),sQuery(id+"F0.wireOp",EDGE,"E14.67.1"),sQuery(id+"F0.wireOp",EDGE,"E14.67.2"),sQuery(id+"F0.wireOp",EDGE,"E14.67.3"),sQuery(id+"F0.wireOp",EDGE,"E14.67.4"),sQuery(id+"F0.wireOp",EDGE,"E14.67.5"),sQuery(id+"F0.wireOp",EDGE,"E14.67.6"),sQuery(id+"F0.wireOp",EDGE,"E14.67.7"),sQuery(id+"F0.wireOp",EDGE,"E14.67.8"),sQuery(id+"F0.wireOp",EDGE,"E14.67.9"),sQuery(id+"F0.wireOp",EDGE,"E14.68.0"),sQuery(id+"F0.wireOp",EDGE,"E14.68.1"),sQuery(id+"F0.wireOp",EDGE,"E14.68.2"),sQuery(id+"F0.wireOp",EDGE,"E14.68.3"),sQuery(id+"F0.wireOp",EDGE,"E14.68.4"),sQuery(id+"F0.wireOp",EDGE,"E14.68.5"),sQuery(id+"F0.wireOp",EDGE,"E14.68.6"),sQuery(id+"F0.wireOp",EDGE,"E14.68.7"),sQuery(id+"F0.wireOp",EDGE,"E14.68.8"),sQuery(id+"F0.wireOp",EDGE,"E14.68.9"),sQuery(id+"F0.wireOp",EDGE,"E14.69.0"),sQuery(id+"F0.wireOp",EDGE,"E14.69.1"),sQuery(id+"F0.wireOp",EDGE,"E14.69.2"),sQuery(id+"F0.wireOp",EDGE,"E14.69.3"),sQuery(id+"F0.wireOp",EDGE,"E14.69.4"),sQuery(id+"F0.wireOp",EDGE,"E14.69.5"),sQuery(id+"F0.wireOp",EDGE,"E14.69.6"),sQuery(id+"F0.wireOp",EDGE,"E14.69.7"),sQuery(id+"F0.wireOp",EDGE,"E14.69.8"),sQuery(id+"F0.wireOp",EDGE,"E14.69.9"),sQuery(id+"F0.wireOp",EDGE,"E14.70.0"),sQuery(id+"F0.wireOp",EDGE,"E14.70.1"),sQuery(id+"F0.wireOp",EDGE,"E14.70.2"),sQuery(id+"F0.wireOp",EDGE,"E14.70.3"),sQuery(id+"F0.wireOp",EDGE,"E14.70.4"),sQuery(id+"F0.wireOp",EDGE,"E14.70.5"),sQuery(id+"F0.wireOp",EDGE,"E14.70.6"),sQuery(id+"F0.wireOp",EDGE,"E14.70.7"),sQuery(id+"F0.wireOp",EDGE,"E14.70.8"),sQuery(id+"F0.wireOp",EDGE,"E14.70.9"),sQuery(id+"F0.wireOp",EDGE,"E14.71.0"),sQuery(id+"F0.wireOp",EDGE,"E14.71.1"),sQuery(id+"F0.wireOp",EDGE,"E14.71.2"),sQuery(id+"F0.wireOp",EDGE,"E14.71.3"),sQuery(id+"F0.wireOp",EDGE,"E14.71.4"),sQuery(id+"F0.wireOp",EDGE,"E14.71.5"),sQuery(id+"F0.wireOp",EDGE,"E14.71.6"),sQuery(id+"F0.wireOp",EDGE,"E14.71.7"),sQuery(id+"F0.wireOp",EDGE,"E14.71.8"),sQuery(id+"F0.wireOp",EDGE,"E14.71.9"),sQuery(id+"F0.wireOp",EDGE,"E14.72.0"),sQuery(id+"F0.wireOp",EDGE,"E14.72.1"),sQuery(id+"F0.wireOp",EDGE,"E14.72.2"),sQuery(id+"F0.wireOp",EDGE,"E14.72.3"),sQuery(id+"F0.wireOp",EDGE,"E14.72.4"),sQuery(id+"F0.wireOp",EDGE,"E14.72.5"),sQuery(id+"F0.wireOp",EDGE,"E14.72.6"),sQuery(id+"F0.wireOp",EDGE,"E14.72.7"),sQuery(id+"F0.wireOp",EDGE,"E14.72.8"),sQuery(id+"F0.wireOp",EDGE,"E14.72.9"),sQuery(id+"F0.wireOp",EDGE,"E14.73.0"),sQuery(id+"F0.wireOp",EDGE,"E14.73.1"),sQuery(id+"F0.wireOp",EDGE,"E14.73.2"),sQuery(id+"F0.wireOp",EDGE,"E14.73.3"),sQuery(id+"F0.wireOp",EDGE,"E14.73.4"),sQuery(id+"F0.wireOp",EDGE,"E14.73.5"),sQuery(id+"F0.wireOp",EDGE,"E14.73.6"),sQuery(id+"F0.wireOp",EDGE,"E14.73.7"),sQuery(id+"F0.wireOp",EDGE,"E14.73.8"),sQuery(id+"F0.wireOp",EDGE,"E14.73.9"),sQuery(id+"F0.wireOp",EDGE,"E14.74.0"),sQuery(id+"F0.wireOp",EDGE,"E14.74.1"),sQuery(id+"F0.wireOp",EDGE,"E14.74.2"),sQuery(id+"F0.wireOp",EDGE,"E14.74.3"),sQuery(id+"F0.wireOp",EDGE,"E14.74.4"),sQuery(id+"F0.wireOp",EDGE,"E14.74.5"),sQuery(id+"F0.wireOp",EDGE,"E14.74.6"),sQuery(id+"F0.wireOp",EDGE,"E14.74.7"),sQuery(id+"F0.wireOp",EDGE,"E14.74.8"),sQuery(id+"F0.wireOp",EDGE,"E14.74.9"),sQuery(id+"F0.wireOp",EDGE,"E14.75.0"),sQuery(id+"F0.wireOp",EDGE,"E14.75.1"),sQuery(id+"F0.wireOp",EDGE,"E14.75.2"),sQuery(id+"F0.wireOp",EDGE,"E14.75.3"),sQuery(id+"F0.wireOp",EDGE,"E14.75.4"),sQuery(id+"F0.wireOp",EDGE,"E14.75.5"),sQuery(id+"F0.wireOp",EDGE,"E14.75.6"),sQuery(id+"F0.wireOp",EDGE,"E14.75.7"),sQuery(id+"F0.wireOp",EDGE,"E14.75.8"),sQuery(id+"F0.wireOp",EDGE,"E14.75.9"),sQuery(id+"F0.wireOp",EDGE,"E14.76.0"),sQuery(id+"F0.wireOp",EDGE,"E14.76.1"),sQuery(id+"F0.wireOp",EDGE,"E14.76.2"),sQuery(id+"F0.wireOp",EDGE,"E14.76.3"),sQuery(id+"F0.wireOp",EDGE,"E14.76.4"),sQuery(id+"F0.wireOp",EDGE,"E14.76.5"),sQuery(id+"F0.wireOp",EDGE,"E14.76.6"),sQuery(id+"F0.wireOp",EDGE,"E14.76.7"),sQuery(id+"F0.wireOp",EDGE,"E14.76.8"),sQuery(id+"F0.wireOp",EDGE,"E14.76.9"),sQuery(id+"F0.wireOp",EDGE,"E14.77.0"),sQuery(id+"F0.wireOp",EDGE,"E14.77.1"),sQuery(id+"F0.wireOp",EDGE,"E14.77.2"),sQuery(id+"F0.wireOp",EDGE,"E14.77.3"),sQuery(id+"F0.wireOp",EDGE,"E14.77.4"),sQuery(id+"F0.wireOp",EDGE,"E14.77.5"),sQuery(id+"F0.wireOp",EDGE,"E14.77.6"),sQuery(id+"F0.wireOp",EDGE,"E14.77.7"),sQuery(id+"F0.wireOp",EDGE,"E14.77.8"),sQuery(id+"F0.wireOp",EDGE,"E14.77.9"),sQuery(id+"F0.wireOp",EDGE,"E14.78.0"),sQuery(id+"F0.wireOp",EDGE,"E14.78.1"),sQuery(id+"F0.wireOp",EDGE,"E14.78.2"),sQuery(id+"F0.wireOp",EDGE,"E14.78.3"),sQuery(id+"F0.wireOp",EDGE,"E14.78.4"),sQuery(id+"F0.wireOp",EDGE,"E14.78.5"),sQuery(id+"F0.wireOp",EDGE,"E14.78.6"),sQuery(id+"F0.wireOp",EDGE,"E14.78.7"),sQuery(id+"F0.wireOp",EDGE,"E14.78.8"),sQuery(id+"F0.wireOp",EDGE,"E14.78.9"),sQuery(id+"F0.wireOp",EDGE,"E14.79.0"),sQuery(id+"F0.wireOp",EDGE,"E14.79.1"),sQuery(id+"F0.wireOp",EDGE,"E14.79.2"),sQuery(id+"F0.wireOp",EDGE,"E14.79.3"),sQuery(id+"F0.wireOp",EDGE,"E14.79.4"),sQuery(id+"F0.wireOp",EDGE,"E14.79.5"),sQuery(id+"F0.wireOp",EDGE,"E14.79.6"),sQuery(id+"F0.wireOp",EDGE,"E14.79.7"),sQuery(id+"F0.wireOp",EDGE,"E14.79.8"),sQuery(id+"F0.wireOp",EDGE,"E14.79.9"),sQuery(id+"F0.wireOp",EDGE,"E14.80.0"),sQuery(id+"F0.wireOp",EDGE,"E14.80.1"),sQuery(id+"F0.wireOp",EDGE,"E14.80.2"),sQuery(id+"F0.wireOp",EDGE,"E14.80.3"),sQuery(id+"F0.wireOp",EDGE,"E14.80.4"),sQuery(id+"F0.wireOp",EDGE,"E14.80.5"),sQuery(id+"F0.wireOp",EDGE,"E14.80.6"),sQuery(id+"F0.wireOp",EDGE,"E14.80.7"),sQuery(id+"F0.wireOp",EDGE,"E14.80.8"),sQuery(id+"F0.wireOp",EDGE,"E14.80.9"),sQuery(id+"F0.wireOp",EDGE,"E14.81.0"),sQuery(id+"F0.wireOp",EDGE,"E14.81.1"),sQuery(id+"F0.wireOp",EDGE,"E14.81.2"),sQuery(id+"F0.wireOp",EDGE,"E14.81.3"),sQuery(id+"F0.wireOp",EDGE,"E14.81.4"),sQuery(id+"F0.wireOp",EDGE,"E14.81.5"),sQuery(id+"F0.wireOp",EDGE,"E14.81.6"),sQuery(id+"F0.wireOp",EDGE,"E14.81.7"),sQuery(id+"F0.wireOp",EDGE,"E14.81.8"),sQuery(id+"F0.wireOp",EDGE,"E14.81.9"),sQuery(id+"F0.wireOp",EDGE,"E14.82.0"),sQuery(id+"F0.wireOp",EDGE,"E14.82.1"),sQuery(id+"F0.wireOp",EDGE,"E14.82.2"),sQuery(id+"F0.wireOp",EDGE,"E14.82.3"),sQuery(id+"F0.wireOp",EDGE,"E14.82.4"),sQuery(id+"F0.wireOp",EDGE,"E14.82.5"),sQuery(id+"F0.wireOp",EDGE,"E14.82.6"),sQuery(id+"F0.wireOp",EDGE,"E14.82.7"),sQuery(id+"F0.wireOp",EDGE,"E14.82.8"),sQuery(id+"F0.wireOp",EDGE,"E14.82.9"),sQuery(id+"F0.wireOp",EDGE,"E14.83.0"),sQuery(id+"F0.wireOp",EDGE,"E14.83.1"),sQuery(id+"F0.wireOp",EDGE,"E14.83.2"),sQuery(id+"F0.wireOp",EDGE,"E14.83.3"),sQuery(id+"F0.wireOp",EDGE,"E14.83.4"),sQuery(id+"F0.wireOp",EDGE,"E14.83.5"),sQuery(id+"F0.wireOp",EDGE,"E14.83.6"),sQuery(id+"F0.wireOp",EDGE,"E14.83.7"),sQuery(id+"F0.wireOp",EDGE,"E14.83.8"),sQuery(id+"F0.wireOp",EDGE,"E14.83.9"),sQuery(id+"F0.wireOp",EDGE,"E14.84.0"),sQuery(id+"F0.wireOp",EDGE,"E14.84.1"),sQuery(id+"F0.wireOp",EDGE,"E14.84.2"),sQuery(id+"F0.wireOp",EDGE,"E14.84.3"),sQuery(id+"F0.wireOp",EDGE,"E14.84.4"),sQuery(id+"F0.wireOp",EDGE,"E14.84.5"),sQuery(id+"F0.wireOp",EDGE,"E14.84.6"),sQuery(id+"F0.wireOp",EDGE,"E14.84.7"),sQuery(id+"F0.wireOp",EDGE,"E14.84.8"),sQuery(id+"F0.wireOp",EDGE,"E14.84.9"),sQuery(id+"F0.wireOp",EDGE,"E14.85.0"),sQuery(id+"F0.wireOp",EDGE,"E14.85.1"),sQuery(id+"F0.wireOp",EDGE,"E14.85.2"),sQuery(id+"F0.wireOp",EDGE,"E14.85.3"),sQuery(id+"F0.wireOp",EDGE,"E14.85.4"),sQuery(id+"F0.wireOp",EDGE,"E14.85.5"),sQuery(id+"F0.wireOp",EDGE,"E14.85.6"),sQuery(id+"F0.wireOp",EDGE,"E14.85.7"),sQuery(id+"F0.wireOp",EDGE,"E14.85.8"),sQuery(id+"F0.wireOp",EDGE,"E14.85.9"),sQuery(id+"F0.wireOp",EDGE,"E14.86.0"),sQuery(id+"F0.wireOp",EDGE,"E14.86.1"),sQuery(id+"F0.wireOp",EDGE,"E14.86.2"),sQuery(id+"F0.wireOp",EDGE,"E14.86.3"),sQuery(id+"F0.wireOp",EDGE,"E14.86.4"),sQuery(id+"F0.wireOp",EDGE,"E14.86.5"),sQuery(id+"F0.wireOp",EDGE,"E14.86.6"),sQuery(id+"F0.wireOp",EDGE,"E14.86.7"),sQuery(id+"F0.wireOp",EDGE,"E14.86.8"),sQuery(id+"F0.wireOp",EDGE,"E14.86.9"),sQuery(id+"F0.wireOp",EDGE,"E14.87.0"),sQuery(id+"F0.wireOp",EDGE,"E14.87.1"),sQuery(id+"F0.wireOp",EDGE,"E14.87.2"),sQuery(id+"F0.wireOp",EDGE,"E14.87.3"),sQuery(id+"F0.wireOp",EDGE,"E14.87.4"),sQuery(id+"F0.wireOp",EDGE,"E14.87.5"),sQuery(id+"F0.wireOp",EDGE,"E14.87.6"),sQuery(id+"F0.wireOp",EDGE,"E14.87.7"),sQuery(id+"F0.wireOp",EDGE,"E14.87.8"),sQuery(id+"F0.wireOp",EDGE,"E14.87.9"),sQuery(id+"F0.wireOp",EDGE,"E14.88.0"),sQuery(id+"F0.wireOp",EDGE,"E14.88.1"),sQuery(id+"F0.wireOp",EDGE,"E14.88.2"),sQuery(id+"F0.wireOp",EDGE,"E14.88.3"),sQuery(id+"F0.wireOp",EDGE,"E14.88.4"),sQuery(id+"F0.wireOp",EDGE,"E14.88.5"),sQuery(id+"F0.wireOp",EDGE,"E14.88.6"),sQuery(id+"F0.wireOp",EDGE,"E14.88.7"),sQuery(id+"F0.wireOp",EDGE,"E14.88.8"),sQuery(id+"F0.wireOp",EDGE,"E14.88.9"),sQuery(id+"F0.wireOp",EDGE,"E14.89.0"),sQuery(id+"F0.wireOp",EDGE,"E14.89.1"),sQuery(id+"F0.wireOp",EDGE,"E14.89.2"),sQuery(id+"F0.wireOp",EDGE,"E14.89.3"),sQuery(id+"F0.wireOp",EDGE,"E14.89.4"),sQuery(id+"F0.wireOp",EDGE,"E14.89.5"),sQuery(id+"F0.wireOp",EDGE,"E14.89.6"),sQuery(id+"F0.wireOp",EDGE,"E14.89.7"),sQuery(id+"F0.wireOp",EDGE,"E14.89.8"),sQuery(id+"F0.wireOp",EDGE,"E14.89.9"),sQuery(id+"F0.wireOp",EDGE,"E14.90.0"),sQuery(id+"F0.wireOp",EDGE,"E14.90.1"),sQuery(id+"F0.wireOp",EDGE,"E14.90.2"),sQuery(id+"F0.wireOp",EDGE,"E14.90.3"),sQuery(id+"F0.wireOp",EDGE,"E14.90.4"),sQuery(id+"F0.wireOp",EDGE,"E14.90.5"),sQuery(id+"F0.wireOp",EDGE,"E14.90.6"),sQuery(id+"F0.wireOp",EDGE,"E14.90.7"),sQuery(id+"F0.wireOp",EDGE,"E14.90.8"),sQuery(id+"F0.wireOp",EDGE,"E14.90.9"),sQuery(id+"F0.wireOp",EDGE,"E14.91.0"),sQuery(id+"F0.wireOp",EDGE,"E14.91.1"),sQuery(id+"F0.wireOp",EDGE,"E14.91.2"),sQuery(id+"F0.wireOp",EDGE,"E14.91.3"),sQuery(id+"F0.wireOp",EDGE,"E14.91.4"),sQuery(id+"F0.wireOp",EDGE,"E14.91.5"),sQuery(id+"F0.wireOp",EDGE,"E14.91.6"),sQuery(id+"F0.wireOp",EDGE,"E14.91.7"),sQuery(id+"F0.wireOp",EDGE,"E14.91.8"),sQuery(id+"F0.wireOp",EDGE,"E14.91.9"),sQuery(id+"F0.wireOp",EDGE,"E14.92.0"),sQuery(id+"F0.wireOp",EDGE,"E14.92.1"),sQuery(id+"F0.wireOp",EDGE,"E14.92.2"),sQuery(id+"F0.wireOp",EDGE,"E14.92.3"),sQuery(id+"F0.wireOp",EDGE,"E14.92.4"),sQuery(id+"F0.wireOp",EDGE,"E14.92.5"),sQuery(id+"F0.wireOp",EDGE,"E14.92.6"),sQuery(id+"F0.wireOp",EDGE,"E14.92.7"),sQuery(id+"F0.wireOp",EDGE,"E14.92.8"),sQuery(id+"F0.wireOp",EDGE,"E14.92.9"),sQuery(id+"F0.wireOp",EDGE,"E14.93.0"),sQuery(id+"F0.wireOp",EDGE,"E14.93.1"),sQuery(id+"F0.wireOp",EDGE,"E14.93.2"),sQuery(id+"F0.wireOp",EDGE,"E14.93.3"),sQuery(id+"F0.wireOp",EDGE,"E14.93.4"),sQuery(id+"F0.wireOp",EDGE,"E14.93.5"),sQuery(id+"F0.wireOp",EDGE,"E14.93.6"),sQuery(id+"F0.wireOp",EDGE,"E14.93.7"),sQuery(id+"F0.wireOp",EDGE,"E14.93.8"),sQuery(id+"F0.wireOp",EDGE,"E14.93.9"),sQuery(id+"F0.wireOp",EDGE,"E14.94.0"),sQuery(id+"F0.wireOp",EDGE,"E14.94.1"),sQuery(id+"F0.wireOp",EDGE,"E14.94.2"),sQuery(id+"F0.wireOp",EDGE,"E14.94.3"),sQuery(id+"F0.wireOp",EDGE,"E14.94.4"),sQuery(id+"F0.wireOp",EDGE,"E14.94.5"),sQuery(id+"F0.wireOp",EDGE,"E14.94.6"),sQuery(id+"F0.wireOp",EDGE,"E14.94.7"),sQuery(id+"F0.wireOp",EDGE,"E14.94.8"),sQuery(id+"F0.wireOp",EDGE,"E14.94.9"),sQuery(id+"F0.wireOp",EDGE,"E14.95.0"),sQuery(id+"F0.wireOp",EDGE,"E14.95.1"),sQuery(id+"F0.wireOp",EDGE,"E14.95.2"),sQuery(id+"F0.wireOp",EDGE,"E14.95.3"),sQuery(id+"F0.wireOp",EDGE,"E14.95.4"),sQuery(id+"F0.wireOp",EDGE,"E14.95.5"),sQuery(id+"F0.wireOp",EDGE,"E14.95.6"),sQuery(id+"F0.wireOp",EDGE,"E14.95.7"),sQuery(id+"F0.wireOp",EDGE,"E14.95.8"),sQuery(id+"F0.wireOp",EDGE,"E14.95.9"),sQuery(id+"F0.wireOp",EDGE,"E14.96.0"),sQuery(id+"F0.wireOp",EDGE,"E14.96.1"),sQuery(id+"F0.wireOp",EDGE,"E14.96.2"),sQuery(id+"F0.wireOp",EDGE,"E14.96.3"),sQuery(id+"F0.wireOp",EDGE,"E14.96.4"),sQuery(id+"F0.wireOp",EDGE,"E14.96.5"),sQuery(id+"F0.wireOp",EDGE,"E14.96.6"),sQuery(id+"F0.wireOp",EDGE,"E14.96.7"),sQuery(id+"F0.wireOp",EDGE,"E14.96.8"),sQuery(id+"F0.wireOp",EDGE,"E14.96.9"),sQuery(id+"F0.wireOp",EDGE,"E14.97.0"),sQuery(id+"F0.wireOp",EDGE,"E14.97.1"),sQuery(id+"F0.wireOp",EDGE,"E14.97.2"),sQuery(id+"F0.wireOp",EDGE,"E14.97.3"),sQuery(id+"F0.wireOp",EDGE,"E14.97.4"),sQuery(id+"F0.wireOp",EDGE,"E14.97.5"),sQuery(id+"F0.wireOp",EDGE,"E14.97.6"),sQuery(id+"F0.wireOp",EDGE,"E14.97.7"),sQuery(id+"F0.wireOp",EDGE,"E14.97.8"),sQuery(id+"F0.wireOp",EDGE,"E14.97.9"),sQuery(id+"F0.wireOp",EDGE,"E14.98.0"),sQuery(id+"F0.wireOp",EDGE,"E14.98.1"),sQuery(id+"F0.wireOp",EDGE,"E14.98.2"),sQuery(id+"F0.wireOp",EDGE,"E14.98.3"),sQuery(id+"F0.wireOp",EDGE,"E14.98.4"),sQuery(id+"F0.wireOp",EDGE,"E14.98.5"),sQuery(id+"F0.wireOp",EDGE,"E14.98.6"),sQuery(id+"F0.wireOp",EDGE,"E14.98.7"),sQuery(id+"F0.wireOp",EDGE,"E14.98.8"),sQuery(id+"F0.wireOp",EDGE,"E14.98.9"),sQuery(id+"F0.wireOp",EDGE,"E14.99.0"),sQuery(id+"F0.wireOp",EDGE,"E14.99.1"),sQuery(id+"F0.wireOp",EDGE,"E14.99.2"),sQuery(id+"F0.wireOp",EDGE,"E14.99.3"),sQuery(id+"F0.wireOp",EDGE,"E14.99.4"),sQuery(id+"F0.wireOp",EDGE,"E14.99.5"),sQuery(id+"F0.wireOp",EDGE,"E14.99.6"),sQuery(id+"F0.wireOp",EDGE,"E14.99.7"),sQuery(id+"F0.wireOp",EDGE,"E14.99.8"),sQuery(id+"F0.wireOp",EDGE,"E14.99.9"),sQuery(id+"F0.wireOp",EDGE,"E14.100.0"),sQuery(id+"F0.wireOp",EDGE,"E14.100.1"),sQuery(id+"F0.wireOp",EDGE,"E14.100.2"),sQuery(id+"F0.wireOp",EDGE,"E14.100.3"),sQuery(id+"F0.wireOp",EDGE,"E14.100.4"),sQuery(id+"F0.wireOp",EDGE,"E14.100.5"),sQuery(id+"F0.wireOp",EDGE,"E14.100.6"),sQuery(id+"F0.wireOp",EDGE,"E14.100.7"),sQuery(id+"F0.wireOp",EDGE,"E14.100.8"),sQuery(id+"F0.wireOp",EDGE,"E14.100.9"),sQuery(id+"F0.wireOp",EDGE,"E14.101.0"),sQuery(id+"F0.wireOp",EDGE,"E14.101.1"),sQuery(id+"F0.wireOp",EDGE,"E14.101.2"),sQuery(id+"F0.wireOp",EDGE,"E14.101.3"),sQuery(id+"F0.wireOp",EDGE,"E14.101.4"),sQuery(id+"F0.wireOp",EDGE,"E14.101.5"),sQuery(id+"F0.wireOp",EDGE,"E14.101.6"),sQuery(id+"F0.wireOp",EDGE,"E14.101.7"),sQuery(id+"F0.wireOp",EDGE,"E14.101.8"),sQuery(id+"F0.wireOp",EDGE,"E14.101.9"),sQuery(id+"F0.wireOp",EDGE,"E14.102.0"),sQuery(id+"F0.wireOp",EDGE,"E14.102.1"),sQuery(id+"F0.wireOp",EDGE,"E14.102.2"),sQuery(id+"F0.wireOp",EDGE,"E14.102.3"),sQuery(id+"F0.wireOp",EDGE,"E14.102.4"),sQuery(id+"F0.wireOp",EDGE,"E14.102.5"),sQuery(id+"F0.wireOp",EDGE,"E14.102.6"),sQuery(id+"F0.wireOp",EDGE,"E14.102.7"),sQuery(id+"F0.wireOp",EDGE,"E14.102.8"),sQuery(id+"F0.wireOp",EDGE,"E14.102.9"),sQuery(id+"F0.wireOp",EDGE,"E14.103.0"),sQuery(id+"F0.wireOp",EDGE,"E14.103.1"),sQuery(id+"F0.wireOp",EDGE,"E14.103.2"),sQuery(id+"F0.wireOp",EDGE,"E14.103.3"),sQuery(id+"F0.wireOp",EDGE,"E14.103.4"),sQuery(id+"F0.wireOp",EDGE,"E14.103.5"),sQuery(id+"F0.wireOp",EDGE,"E14.103.6"),sQuery(id+"F0.wireOp",EDGE,"E14.103.7"),sQuery(id+"F0.wireOp",EDGE,"E14.103.8"),sQuery(id+"F0.wireOp",EDGE,"E14.103.9"),sQuery(id+"F0.wireOp",EDGE,"E14.104.0"),sQuery(id+"F0.wireOp",EDGE,"E14.104.1"),sQuery(id+"F0.wireOp",EDGE,"E14.104.2"),sQuery(id+"F0.wireOp",EDGE,"E14.104.3"),sQuery(id+"F0.wireOp",EDGE,"E14.104.4"),sQuery(id+"F0.wireOp",EDGE,"E14.104.5"),sQuery(id+"F0.wireOp",EDGE,"E14.104.6"),sQuery(id+"F0.wireOp",EDGE,"E14.104.7"),sQuery(id+"F0.wireOp",EDGE,"E14.104.8"),sQuery(id+"F0.wireOp",EDGE,"E14.104.9"),sQuery(id+"F0.wireOp",EDGE,"E14.105.0"),sQuery(id+"F0.wireOp",EDGE,"E14.105.1"),sQuery(id+"F0.wireOp",EDGE,"E14.105.2"),sQuery(id+"F0.wireOp",EDGE,"E14.105.3"),sQuery(id+"F0.wireOp",EDGE,"E14.105.4"),sQuery(id+"F0.wireOp",EDGE,"E14.105.5"),sQuery(id+"F0.wireOp",EDGE,"E14.105.6"),sQuery(id+"F0.wireOp",EDGE,"E14.105.7"),sQuery(id+"F0.wireOp",EDGE,"E14.105.8"),sQuery(id+"F0.wireOp",EDGE,"E14.105.9"),sQuery(id+"F0.wireOp",EDGE,"E14.106.0"),sQuery(id+"F0.wireOp",EDGE,"E14.106.1"),sQuery(id+"F0.wireOp",EDGE,"E14.106.2"),sQuery(id+"F0.wireOp",EDGE,"E14.106.3"),sQuery(id+"F0.wireOp",EDGE,"E14.106.4"),sQuery(id+"F0.wireOp",EDGE,"E14.106.5"),sQuery(id+"F0.wireOp",EDGE,"E14.106.6"),sQuery(id+"F0.wireOp",EDGE,"E14.106.7"),sQuery(id+"F0.wireOp",EDGE,"E14.106.8"),sQuery(id+"F0.wireOp",EDGE,"E14.106.9"),sQuery(id+"F0.wireOp",EDGE,"E14.107.0"),sQuery(id+"F0.wireOp",EDGE,"E14.107.1"),sQuery(id+"F0.wireOp",EDGE,"E14.107.2"),sQuery(id+"F0.wireOp",EDGE,"E14.107.3"),sQuery(id+"F0.wireOp",EDGE,"E14.107.4"),sQuery(id+"F0.wireOp",EDGE,"E14.107.5"),sQuery(id+"F0.wireOp",EDGE,"E14.107.6"),sQuery(id+"F0.wireOp",EDGE,"E14.107.7"),sQuery(id+"F0.wireOp",EDGE,"E14.107.8"),sQuery(id+"F0.wireOp",EDGE,"E14.107.9"),sQuery(id+"F0.wireOp",EDGE,"E14.108.0"),sQuery(id+"F0.wireOp",EDGE,"E14.108.1"),sQuery(id+"F0.wireOp",EDGE,"E14.108.2"),sQuery(id+"F0.wireOp",EDGE,"E14.108.3"),sQuery(id+"F0.wireOp",EDGE,"E14.108.4"),sQuery(id+"F0.wireOp",EDGE,"E14.108.5"),sQuery(id+"F0.wireOp",EDGE,"E14.108.6"),sQuery(id+"F0.wireOp",EDGE,"E14.108.7"),sQuery(id+"F0.wireOp",EDGE,"E14.108.8"),sQuery(id+"F0.wireOp",EDGE,"E14.108.9"),sQuery(id+"F0.wireOp",EDGE,"E14.109.0"),sQuery(id+"F0.wireOp",EDGE,"E14.109.1"),sQuery(id+"F0.wireOp",EDGE,"E14.109.2"),sQuery(id+"F0.wireOp",EDGE,"E14.109.3"),sQuery(id+"F0.wireOp",EDGE,"E14.109.4"),sQuery(id+"F0.wireOp",EDGE,"E14.109.5"),sQuery(id+"F0.wireOp",EDGE,"E14.109.6"),sQuery(id+"F0.wireOp",EDGE,"E14.109.7"),sQuery(id+"F0.wireOp",EDGE,"E14.109.8"),sQuery(id+"F0.wireOp",EDGE,"E14.109.9"),sQuery(id+"F0.wireOp",EDGE,"E14.110.0"),sQuery(id+"F0.wireOp",EDGE,"E14.110.1"),sQuery(id+"F0.wireOp",EDGE,"E14.110.2"),sQuery(id+"F0.wireOp",EDGE,"E14.110.3"),sQuery(id+"F0.wireOp",EDGE,"E14.110.4"),sQuery(id+"F0.wireOp",EDGE,"E14.110.5"),sQuery(id+"F0.wireOp",EDGE,"E14.110.6"),sQuery(id+"F0.wireOp",EDGE,"E14.110.7"),sQuery(id+"F0.wireOp",EDGE,"E14.110.8"),sQuery(id+"F0.wireOp",EDGE,"E14.110.9"),sQuery(id+"F0.wireOp",EDGE,"E14.111.0"),sQuery(id+"F0.wireOp",EDGE,"E14.111.1"),sQuery(id+"F0.wireOp",EDGE,"E14.111.2"),sQuery(id+"F0.wireOp",EDGE,"E14.111.3"),sQuery(id+"F0.wireOp",EDGE,"E14.111.4"),sQuery(id+"F0.wireOp",EDGE,"E14.111.5"),sQuery(id+"F0.wireOp",EDGE,"E14.111.6"),sQuery(id+"F0.wireOp",EDGE,"E14.111.7"),sQuery(id+"F0.wireOp",EDGE,"E14.111.8"),sQuery(id+"F0.wireOp",EDGE,"E14.111.9"),sQuery(id+"F0.wireOp",EDGE,"E14.112.0"),sQuery(id+"F0.wireOp",EDGE,"E14.112.1"),sQuery(id+"F0.wireOp",EDGE,"E14.112.2"),sQuery(id+"F0.wireOp",EDGE,"E14.112.3"),sQuery(id+"F0.wireOp",EDGE,"E14.112.4"),sQuery(id+"F0.wireOp",EDGE,"E14.112.5"),sQuery(id+"F0.wireOp",EDGE,"E14.112.6"),sQuery(id+"F0.wireOp",EDGE,"E14.112.7"),sQuery(id+"F0.wireOp",EDGE,"E14.112.8"),sQuery(id+"F0.wireOp",EDGE,"E14.112.9"),sQuery(id+"F0.wireOp",EDGE,"E14.113.0"),sQuery(id+"F0.wireOp",EDGE,"E14.113.1"),sQuery(id+"F0.wireOp",EDGE,"E14.113.2"),sQuery(id+"F0.wireOp",EDGE,"E14.113.3"),sQuery(id+"F0.wireOp",EDGE,"E14.113.4"),sQuery(id+"F0.wireOp",EDGE,"E14.113.5"),sQuery(id+"F0.wireOp",EDGE,"E14.113.6"),sQuery(id+"F0.wireOp",EDGE,"E14.113.7"),sQuery(id+"F0.wireOp",EDGE,"E14.113.8"),sQuery(id+"F0.wireOp",EDGE,"E14.113.9"),sQuery(id+"F0.wireOp",EDGE,"E14.114.0"),sQuery(id+"F0.wireOp",EDGE,"E14.114.1"),sQuery(id+"F0.wireOp",EDGE,"E14.114.2"),sQuery(id+"F0.wireOp",EDGE,"E14.114.3"),sQuery(id+"F0.wireOp",EDGE,"E14.114.4"),sQuery(id+"F0.wireOp",EDGE,"E14.114.5"),sQuery(id+"F0.wireOp",EDGE,"E14.114.6"),sQuery(id+"F0.wireOp",EDGE,"E14.114.7"),sQuery(id+"F0.wireOp",EDGE,"E14.114.8"),sQuery(id+"F0.wireOp",EDGE,"E14.114.9"),sQuery(id+"F0.wireOp",EDGE,"E14.115.0"),sQuery(id+"F0.wireOp",EDGE,"E14.115.1"),sQuery(id+"F0.wireOp",EDGE,"E14.115.2"),sQuery(id+"F0.wireOp",EDGE,"E14.115.3"),sQuery(id+"F0.wireOp",EDGE,"E14.115.4"),sQuery(id+"F0.wireOp",EDGE,"E14.115.5"),sQuery(id+"F0.wireOp",EDGE,"E14.115.6"),sQuery(id+"F0.wireOp",EDGE,"E14.115.7"),sQuery(id+"F0.wireOp",EDGE,"E14.115.8"),sQuery(id+"F0.wireOp",EDGE,"E14.115.9"),sQuery(id+"F0.wireOp",EDGE,"E14.116.0"),sQuery(id+"F0.wireOp",EDGE,"E14.116.1"),sQuery(id+"F0.wireOp",EDGE,"E14.116.2"),sQuery(id+"F0.wireOp",EDGE,"E14.116.3"),sQuery(id+"F0.wireOp",EDGE,"E14.116.4"),sQuery(id+"F0.wireOp",EDGE,"E14.116.5"),sQuery(id+"F0.wireOp",EDGE,"E14.116.6"),sQuery(id+"F0.wireOp",EDGE,"E14.116.7"),sQuery(id+"F0.wireOp",EDGE,"E14.116.8"),sQuery(id+"F0.wireOp",EDGE,"E14.116.9"),sQuery(id+"F0.wireOp",EDGE,"E14.117.0"),sQuery(id+"F0.wireOp",EDGE,"E14.117.1"),sQuery(id+"F0.wireOp",EDGE,"E14.117.2"),sQuery(id+"F0.wireOp",EDGE,"E14.117.3"),sQuery(id+"F0.wireOp",EDGE,"E14.117.4"),sQuery(id+"F0.wireOp",EDGE,"E14.117.5"),sQuery(id+"F0.wireOp",EDGE,"E14.117.6"),sQuery(id+"F0.wireOp",EDGE,"E14.117.7"),sQuery(id+"F0.wireOp",EDGE,"E14.117.8"),sQuery(id+"F0.wireOp",EDGE,"E14.117.9"),sQuery(id+"F0.wireOp",EDGE,"E14.118.0"),sQuery(id+"F0.wireOp",EDGE,"E14.118.1"),sQuery(id+"F0.wireOp",EDGE,"E14.118.2"),sQuery(id+"F0.wireOp",EDGE,"E14.118.3"),sQuery(id+"F0.wireOp",EDGE,"E14.118.4"),sQuery(id+"F0.wireOp",EDGE,"E14.118.5"),sQuery(id+"F0.wireOp",EDGE,"E14.118.6"),sQuery(id+"F0.wireOp",EDGE,"E14.118.7"),sQuery(id+"F0.wireOp",EDGE,"E14.118.8"),sQuery(id+"F0.wireOp",EDGE,"E14.118.9"),sQuery(id+"F0.wireOp",EDGE,"E14.119.0"),sQuery(id+"F0.wireOp",EDGE,"E14.119.1"),sQuery(id+"F0.wireOp",EDGE,"E14.119.2"),sQuery(id+"F0.wireOp",EDGE,"E14.119.3"),sQuery(id+"F0.wireOp",EDGE,"E14.119.4"),sQuery(id+"F0.wireOp",EDGE,"E14.119.5"),sQuery(id+"F0.wireOp",EDGE,"E14.119.6"),sQuery(id+"F0.wireOp",EDGE,"E14.119.7"),sQuery(id+"F0.wireOp",EDGE,"E14.119.8"),sQuery(id+"F0.wireOp",EDGE,"E14.119.9"),sQuery(id+"F0.wireOp",EDGE,"E15.trimOffspring"),sQuery(id+"F0.wireOp",EDGE,"E16.trimOffspring"),sQuery(id+"F0.wireOp",EDGE,"E17.trimOffspring"),sQuery(id+"F0.wireOp",EDGE,"E18.trimOffspring"),sQuery(id+"F0.wireOp",EDGE,"E19.trimOffspring"),sQuery(id+"F0.wireOp",EDGE,"E20.trimOffspring"),sQuery(id+"F0.wireOp",EDGE,"E21.trimOffspring"),sQuery(id+"F0.wireOp",EDGE,"E22.trimOffspring"),sQuery(id+"F0.wireOp",EDGE,"E23.trimOffspring"),sQuery(id+"F0.wireOp",EDGE,"E24.trimOffspring"),sQuery(id+"F0.wireOp",EDGE,"E25.trimOffspring"),sQuery(id+"F0.wireOp",EDGE,"E26.trimOffspring"),sQuery(id+"F0.wireOp",EDGE,"E27.trimOffspring"),sQuery(id+"F0.wireOp",EDGE,"E28.trimOffspring"),sQuery(id+"F0.wireOp",EDGE,"E29.trimOffspring"),sQuery(id+"F0.wireOp",EDGE,"E30.trimOffspring"),sQuery(id+"F0.wireOp",EDGE,"E31.trimOffspring"),sQuery(id+"F0.wireOp",EDGE,"E32.trimOffspring"),sQuery(id+"F0.wireOp",EDGE,"E33.trimOffspring"),sQuery(id+"F0.wireOp",EDGE,"E34.trimOffspring"),sQuery(id+"F0.wireOp",EDGE,"E35.trimOffspring"),sQuery(id+"F0.wireOp",EDGE,"E36.trimOffspring"),sQuery(id+"F0.wireOp",EDGE,"E37.trimOffspring"),sQuery(id+"F0.wireOp",EDGE,"E38.trimOffspring"),sQuery(id+"F0.wireOp",EDGE,"E39.trimOffspring"),sQuery(id+"F0.wireOp",EDGE,"E40.trimOffspring"),sQuery(id+"F0.wireOp",EDGE,"E41.trimOffspring"),sQuery(id+"F0.wireOp",EDGE,"E42.trimOffspring"),sQuery(id+"F0.wireOp",EDGE,"E43.trimOffspring"),sQuery(id+"F0.wireOp",EDGE,"E44.trimOffspring"),sQuery(id+"F0.wireOp",EDGE,"E45.trimOffspring"),sQuery(id+"F0.wireOp",EDGE,"E46.trimOffspring"),sQuery(id+"F0.wireOp",EDGE,"E47.trimOffspring"),sQuery(id+"F0.wireOp",EDGE,"E48.trimOffspring"),sQuery(id+"F0.wireOp",EDGE,"E49.trimOffspring"),sQuery(id+"F0.wireOp",EDGE,"E73.1.0"),sQuery(id+"F0.wireOp",EDGE,"E73.1.1"),sQuery(id+"F0.wireOp",EDGE,"E73.2.0"),sQuery(id+"F0.wireOp",EDGE,"E73.2.1"),sQuery(id+"F0.wireOp",EDGE,"E74.3.3.0"),sQuery(id+"F0.wireOp",EDGE,"E74.4.3.0"),sQuery(id+"F0.wireOp",EDGE,"E74.3.4.0"),sQuery(id+"F0.wireOp",EDGE,"E74.4.4.0"),sQuery(id+"F0.wireOp",EDGE,"E74.3.5.0"),sQuery(id+"F0.wireOp",EDGE,"E74.4.5.0"),sQuery(id+"F0.wireOp",EDGE,"E74.3.6.0"),sQuery(id+"F0.wireOp",EDGE,"E74.4.6.0"),sQuery(id+"F0.wireOp",EDGE,"E74.3.7.0"),sQuery(id+"F0.wireOp",EDGE,"E74.4.7.0"),sQuery(id+"F0.wireOp",EDGE,"E74.3.8.0"),sQuery(id+"F0.wireOp",EDGE,"E74.4.8.0"),sQuery(id+"F0.wireOp",EDGE,"E74.3.9.0"),sQuery(id+"F0.wireOp",EDGE,"E74.4.9.0"),sQuery(id+"F0.wireOp",EDGE,"E74.3.10.0"),sQuery(id+"F0.wireOp",EDGE,"E74.4.10.0"),sQuery(id+"F0.wireOp",EDGE,"E74.3.11.0"),sQuery(id+"F0.wireOp",EDGE,"E74.4.11.0"),sQuery(id+"F0.wireOp",EDGE,"E74.3.12.0"),sQuery(id+"F0.wireOp",EDGE,"E74.4.12.0"),sQuery(id+"F0.wireOp",EDGE,"E74.3.13.0"),sQuery(id+"F0.wireOp",EDGE,"E74.4.13.0"),sQuery(id+"F0.wireOp",EDGE,"E74.3.14.0"),sQuery(id+"F0.wireOp",EDGE,"E74.4.14.0"),sQuery(id+"F0.wireOp",EDGE,"E74.3.15.0"),sQuery(id+"F0.wireOp",EDGE,"E74.4.15.0"),sQuery(id+"F0.wireOp",EDGE,"E74.3.16.0"),sQuery(id+"F0.wireOp",EDGE,"E74.4.16.0"),sQuery(id+"F0.wireOp",EDGE,"E74.3.17.0"),sQuery(id+"F0.wireOp",EDGE,"E74.4.17.0"),sQuery(id+"F0.wireOp",EDGE,"E74.3.18.0"),sQuery(id+"F0.wireOp",EDGE,"E74.4.18.0"),sQuery(id+"F0.wireOp",EDGE,"E74.3.19.0"),sQuery(id+"F0.wireOp",EDGE,"E74.4.19.0"),sQuery(id+"F0.wireOp",EDGE,"E74.3.20.0"),sQuery(id+"F0.wireOp",EDGE,"E74.4.20.0"),sQuery(id+"F0.wireOp",EDGE,"E74.3.21.0"),sQuery(id+"F0.wireOp",EDGE,"E74.4.21.0"),sQuery(id+"F0.wireOp",EDGE,"E74.3.22.0"),sQuery(id+"F0.wireOp",EDGE,"E74.4.22.0"),sQuery(id+"F0.wireOp",EDGE,"E74.3.23.0"),sQuery(id+"F0.wireOp",EDGE,"E74.4.23.0"),sQuery(id+"F0.wireOp",EDGE,"E74.3.24.0"),sQuery(id+"F0.wireOp",EDGE,"E74.4.24.0"),sQuery(id+"F0.wireOp",EDGE,"E74.3.25.0"),sQuery(id+"F0.wireOp",EDGE,"E74.4.25.0"),sQuery(id+"F0.wireOp",EDGE,"E74.3.26.0"),sQuery(id+"F0.wireOp",EDGE,"E74.4.26.0"),sQuery(id+"F0.wireOp",EDGE,"E74.3.27.0"),sQuery(id+"F0.wireOp",EDGE,"E74.4.27.0"),sQuery(id+"F0.wireOp",EDGE,"E74.3.28.0"),sQuery(id+"F0.wireOp",EDGE,"E74.4.28.0"),sQuery(id+"F0.wireOp",EDGE,"E74.3.29.0"),sQuery(id+"F0.wireOp",EDGE,"E74.4.29.0"),sQuery(id+"F0.wireOp",EDGE,"E74.3.30.0"),sQuery(id+"F0.wireOp",EDGE,"E74.4.30.0"),sQuery(id+"F0.wireOp",EDGE,"E74.3.31.0"),sQuery(id+"F0.wireOp",EDGE,"E74.4.31.0"),sQuery(id+"F0.wireOp",EDGE,"E74.3.32.0"),sQuery(id+"F0.wireOp",EDGE,"E74.4.32.0"),sQuery(id+"F0.wireOp",EDGE,"E74.3.33.0"),sQuery(id+"F0.wireOp",EDGE,"E74.4.33.0"),sQuery(id+"F0.wireOp",EDGE,"E74.3.34.0"),sQuery(id+"F0.wireOp",EDGE,"E74.4.34.0"),sQuery(id+"F0.wireOp",EDGE,"E74.3.35.0"),sQuery(id+"F0.wireOp",EDGE,"E74.4.35.0"),sQuery(id+"F0.wireOp",EDGE,"E74.3.36.0"),sQuery(id+"F0.wireOp",EDGE,"E74.4.36.0"),sQuery(id+"F0.wireOp",EDGE,"E74.3.37.0"),sQuery(id+"F0.wireOp",EDGE,"E74.4.37.0"),sQuery(id+"F0.wireOp",EDGE,"E74.3.38.0"),sQuery(id+"F0.wireOp",EDGE,"E74.4.38.0"),sQuery(id+"F0.wireOp",EDGE,"E74.3.39.0"),sQuery(id+"F0.wireOp",EDGE,"E74.4.39.0"),sQuery(id+"F0.wireOp",EDGE,"E74.3.40.0"),sQuery(id+"F0.wireOp",EDGE,"E74.4.40.0"),sQuery(id+"F0.wireOp",EDGE,"E74.3.41.0"),sQuery(id+"F0.wireOp",EDGE,"E74.4.41.0"),sQuery(id+"F0.wireOp",EDGE,"E74.3.42.0"),sQuery(id+"F0.wireOp",EDGE,"E74.4.42.0"),sQuery(id+"F0.wireOp",EDGE,"E74.3.43.0"),sQuery(id+"F0.wireOp",EDGE,"E74.4.43.0"),sQuery(id+"F0.wireOp",EDGE,"E74.3.44.0"),sQuery(id+"F0.wireOp",EDGE,"E74.4.44.0"),sQuery(id+"F0.wireOp",EDGE,"E74.3.45.0"),sQuery(id+"F0.wireOp",EDGE,"E74.4.45.0"),sQuery(id+"F0.wireOp",EDGE,"E74.3.46.0"),sQuery(id+"F0.wireOp",EDGE,"E74.4.46.0"),sQuery(id+"F0.wireOp",EDGE,"E74.3.47.0"),sQuery(id+"F0.wireOp",EDGE,"E74.4.47.0"),sQuery(id+"F0.wireOp",EDGE,"E74.3.48.0"),sQuery(id+"F0.wireOp",EDGE,"E74.4.48.0"),sQuery(id+"F0.wireOp",EDGE,"E74.3.49.0"),sQuery(id+"F0.wireOp",EDGE,"E74.4.49.0"),sQuery(id+"F0.wireOp",EDGE,"E74.3.50.0"),sQuery(id+"F0.wireOp",EDGE,"E74.4.50.0"),sQuery(id+"F0.wireOp",EDGE,"E74.3.51.0"),sQuery(id+"F0.wireOp",EDGE,"E74.4.51.0"),sQuery(id+"F0.wireOp",EDGE,"E74.3.52.0"),sQuery(id+"F0.wireOp",EDGE,"E74.4.52.0"),sQuery(id+"F0.wireOp",EDGE,"E74.3.53.0"),sQuery(id+"F0.wireOp",EDGE,"E74.4.53.0"),sQuery(id+"F0.wireOp",EDGE,"E74.3.54.0"),sQuery(id+"F0.wireOp",EDGE,"E74.4.54.0"),sQuery(id+"F0.wireOp",EDGE,"E74.3.55.0"),sQuery(id+"F0.wireOp",EDGE,"E74.4.55.0"),sQuery(id+"F0.wireOp",EDGE,"E74.3.56.0"),sQuery(id+"F0.wireOp",EDGE,"E74.4.56.0"),sQuery(id+"F0.wireOp",EDGE,"E74.3.57.0"),sQuery(id+"F0.wireOp",EDGE,"E74.4.57.0"),sQuery(id+"F0.wireOp",EDGE,"E74.3.58.0"),sQuery(id+"F0.wireOp",EDGE,"E74.4.58.0"),sQuery(id+"F0.wireOp",EDGE,"E74.3.59.0"),sQuery(id+"F0.wireOp",EDGE,"E74.4.59.0"),sQuery(id+"F0.wireOp",EDGE,"E74.3.60.0"),sQuery(id+"F0.wireOp",EDGE,"E74.4.60.0"),sQuery(id+"F0.wireOp",EDGE,"E74.3.61.0"),sQuery(id+"F0.wireOp",EDGE,"E74.4.61.0"),sQuery(id+"F0.wireOp",EDGE,"E74.3.62.0"),sQuery(id+"F0.wireOp",EDGE,"E74.4.62.0"),sQuery(id+"F0.wireOp",EDGE,"E74.3.63.0"),sQuery(id+"F0.wireOp",EDGE,"E74.4.63.0"),sQuery(id+"F0.wireOp",EDGE,"E74.3.64.0"),sQuery(id+"F0.wireOp",EDGE,"E74.4.64.0"),sQuery(id+"F0.wireOp",EDGE,"E74.3.65.0"),sQuery(id+"F0.wireOp",EDGE,"E74.4.65.0"),sQuery(id+"F0.wireOp",EDGE,"E74.3.66.0"),sQuery(id+"F0.wireOp",EDGE,"E74.4.66.0"),sQuery(id+"F0.wireOp",EDGE,"E74.3.67.0"),sQuery(id+"F0.wireOp",EDGE,"E74.4.67.0"),sQuery(id+"F0.wireOp",EDGE,"E74.3.68.0"),sQuery(id+"F0.wireOp",EDGE,"E74.4.68.0"),sQuery(id+"F0.wireOp",EDGE,"E74.3.69.0"),sQuery(id+"F0.wireOp",EDGE,"E74.4.69.0"),sQuery(id+"F0.wireOp",EDGE,"E74.3.70.0"),sQuery(id+"F0.wireOp",EDGE,"E74.4.70.0"),sQuery(id+"F0.wireOp",EDGE,"E74.3.71.0"),sQuery(id+"F0.wireOp",EDGE,"E74.4.71.0"),sQuery(id+"F0.wireOp",EDGE,"E74.3.72.0"),sQuery(id+"F0.wireOp",EDGE,"E74.4.72.0"),sQuery(id+"F0.wireOp",EDGE,"E74.3.73.0"),sQuery(id+"F0.wireOp",EDGE,"E74.4.73.0"),sQuery(id+"F0.wireOp",EDGE,"E74.3.74.0"),sQuery(id+"F0.wireOp",EDGE,"E74.4.74.0"),sQuery(id+"F0.wireOp",EDGE,"E74.3.75.0"),sQuery(id+"F0.wireOp",EDGE,"E74.4.75.0"),sQuery(id+"F0.wireOp",EDGE,"E74.3.76.0"),sQuery(id+"F0.wireOp",EDGE,"E74.4.76.0"),sQuery(id+"F0.wireOp",EDGE,"E74.3.77.0"),sQuery(id+"F0.wireOp",EDGE,"E74.4.77.0"),sQuery(id+"F0.wireOp",EDGE,"E74.3.78.0"),sQuery(id+"F0.wireOp",EDGE,"E74.4.78.0"),sQuery(id+"F0.wireOp",EDGE,"E74.3.79.0"),sQuery(id+"F0.wireOp",EDGE,"E74.4.79.0"),sQuery(id+"F0.wireOp",EDGE,"E74.3.80.0"),sQuery(id+"F0.wireOp",EDGE,"E74.4.80.0"),sQuery(id+"F0.wireOp",EDGE,"E74.3.81.0"),sQuery(id+"F0.wireOp",EDGE,"E74.4.81.0"),sQuery(id+"F0.wireOp",EDGE,"E74.3.82.0"),sQuery(id+"F0.wireOp",EDGE,"E74.4.82.0"),sQuery(id+"F0.wireOp",EDGE,"E74.3.83.0"),sQuery(id+"F0.wireOp",EDGE,"E74.4.83.0"),sQuery(id+"F0.wireOp",EDGE,"E74.3.84.0"),sQuery(id+"F0.wireOp",EDGE,"E74.4.84.0"),sQuery(id+"F0.wireOp",EDGE,"E74.3.85.0"),sQuery(id+"F0.wireOp",EDGE,"E74.4.85.0"),sQuery(id+"F0.wireOp",EDGE,"E74.3.86.0"),sQuery(id+"F0.wireOp",EDGE,"E74.4.86.0"),sQuery(id+"F0.wireOp",EDGE,"E74.3.87.0"),sQuery(id+"F0.wireOp",EDGE,"E74.4.87.0"),sQuery(id+"F0.wireOp",EDGE,"E74.3.88.0"),sQuery(id+"F0.wireOp",EDGE,"E74.4.88.0"),sQuery(id+"F0.wireOp",EDGE,"E74.3.89.0"),sQuery(id+"F0.wireOp",EDGE,"E74.4.89.0"),sQuery(id+"F0.wireOp",EDGE,"E74.3.90.0"),sQuery(id+"F0.wireOp",EDGE,"E74.4.90.0"),sQuery(id+"F0.wireOp",EDGE,"E74.3.91.0"),sQuery(id+"F0.wireOp",EDGE,"E74.4.91.0"),sQuery(id+"F0.wireOp",EDGE,"E74.3.92.0"),sQuery(id+"F0.wireOp",EDGE,"E74.4.92.0"),sQuery(id+"F0.wireOp",EDGE,"E74.3.93.0"),sQuery(id+"F0.wireOp",EDGE,"E74.4.93.0"),sQuery(id+"F0.wireOp",EDGE,"E74.3.94.0"),sQuery(id+"F0.wireOp",EDGE,"E74.4.94.0"),sQuery(id+"F0.wireOp",EDGE,"E74.3.95.0"),sQuery(id+"F0.wireOp",EDGE,"E74.4.95.0"),sQuery(id+"F0.wireOp",EDGE,"E74.3.96.0"),sQuery(id+"F0.wireOp",EDGE,"E74.4.96.0"),sQuery(id+"F0.wireOp",EDGE,"E74.3.97.0"),sQuery(id+"F0.wireOp",EDGE,"E74.4.97.0"),sQuery(id+"F0.wireOp",EDGE,"E74.3.98.0"),sQuery(id+"F0.wireOp",EDGE,"E74.4.98.0"),sQuery(id+"F0.wireOp",EDGE,"E74.3.99.0"),sQuery(id+"F0.wireOp",EDGE,"E74.4.99.0"),sQuery(id+"F0.wireOp",EDGE,"E74.3.100.0"),sQuery(id+"F0.wireOp",EDGE,"E74.4.100.0"),sQuery(id+"F0.wireOp",EDGE,"E74.3.101.0"),sQuery(id+"F0.wireOp",EDGE,"E74.4.101.0"),sQuery(id+"F0.wireOp",EDGE,"E74.3.102.0"),sQuery(id+"F0.wireOp",EDGE,"E74.4.102.0"),sQuery(id+"F0.wireOp",EDGE,"E74.3.103.0"),sQuery(id+"F0.wireOp",EDGE,"E74.4.103.0"),sQuery(id+"F0.wireOp",EDGE,"E74.3.104.0"),sQuery(id+"F0.wireOp",EDGE,"E74.4.104.0"),sQuery(id+"F0.wireOp",EDGE,"E74.3.105.0"),sQuery(id+"F0.wireOp",EDGE,"E74.4.105.0"),sQuery(id+"F0.wireOp",EDGE,"E74.3.106.0"),sQuery(id+"F0.wireOp",EDGE,"E74.4.106.0"),sQuery(id+"F0.wireOp",EDGE,"E74.3.107.0"),sQuery(id+"F0.wireOp",EDGE,"E74.4.107.0"),sQuery(id+"F0.wireOp",EDGE,"E74.3.108.0"),sQuery(id+"F0.wireOp",EDGE,"E74.4.108.0"),sQuery(id+"F0.wireOp",EDGE,"E74.3.109.0"),sQuery(id+"F0.wireOp",EDGE,"E74.4.109.0"),sQuery(id+"F0.wireOp",EDGE,"E74.3.110.0"),sQuery(id+"F0.wireOp",EDGE,"E74.4.110.0"),sQuery(id+"F0.wireOp",EDGE,"E74.3.111.0"),sQuery(id+"F0.wireOp",EDGE,"E74.4.111.0"),sQuery(id+"F0.wireOp",EDGE,"E74.3.112.0"),sQuery(id+"F0.wireOp",EDGE,"E74.4.112.0"),sQuery(id+"F0.wireOp",EDGE,"E74.3.113.0"),sQuery(id+"F0.wireOp",EDGE,"E74.4.113.0"),sQuery(id+"F0.wireOp",EDGE,"E74.3.114.0"),sQuery(id+"F0.wireOp",EDGE,"E74.4.114.0"),sQuery(id+"F0.wireOp",EDGE,"E74.3.115.0"),sQuery(id+"F0.wireOp",EDGE,"E74.4.115.0"),sQuery(id+"F0.wireOp",EDGE,"E74.3.116.0"),sQuery(id+"F0.wireOp",EDGE,"E74.4.116.0"),sQuery(id+"F0.wireOp",EDGE,"E74.3.117.0"),sQuery(id+"F0.wireOp",EDGE,"E74.4.117.0"),sQuery(id+"F0.wireOp",EDGE,"E74.3.118.0"),sQuery(id+"F0.wireOp",EDGE,"E74.4.118.0"),sQuery(id+"F0.wireOp",EDGE,"E74.3.119.0"),sQuery(id+"F0.wireOp",EDGE,"E74.4.119.0"),sQuery(id+"F0.wireOp",EDGE,"E75.trimOffspring"),sQuery(id+"F0.wireOp",EDGE,"E76.trimOffspring"),sQuery(id+"F0.wireOp",EDGE,"E77.trimOffspring"),sQuery(id+"F0.wireOp",EDGE,"E78.trimOffspring"),sQuery(id+"F0.wireOp",EDGE,"E79.trimOffspring"),sQuery(id+"F0.wireOp",EDGE,"E80.trimOffspring"),sQuery(id+"F0.wireOp",EDGE,"E81.trimOffspring"),sQuery(id+"F0.wireOp",EDGE,"E82.trimOffspring"),sQuery(id+"F0.wireOp",EDGE,"E83.trimOffspring"),sQuery(id+"F0.wireOp",EDGE,"E84.trimOffspring"),sQuery(id+"F0.wireOp",EDGE,"E85.trimOffspring"),sQuery(id+"F0.wireOp",EDGE,"E86.trimOffspring"),sQuery(id+"F0.wireOp",EDGE,"E87.trimOffspring"),sQuery(id+"F0.wireOp",EDGE,"E88.trimOffspring"),sQuery(id+"F0.wireOp",EDGE,"E89.trimOffspring"),sQuery(id+"F0.wireOp",EDGE,"E90.trimOffspring"),sQuery(id+"F0.wireOp",EDGE,"E91.trimOffspring"),sQuery(id+"F0.wireOp",EDGE,"E92.trimOffspring"),sQuery(id+"F0.wireOp",EDGE,"E93.trimOffspring"),sQuery(id+"F0.wireOp",EDGE,"E94.trimOffspring"),sQuery(id+"F0.wireOp",EDGE,"E95.trimOffspring"),sQuery(id+"F0.wireOp",EDGE,"E96.trimOffspring"),sQuery(id+"F0.wireOp",EDGE,"E97.trimOffspring"),sQuery(id+"F0.wireOp",EDGE,"E98.trimOffspring"),sQuery(id+"F0.wireOp",EDGE,"E99.trimOffspring"),sQuery(id+"F0.wireOp",EDGE,"E100.trimOffspring"),sQuery(id+"F0.wireOp",EDGE,"E101.trimOffspring"),sQuery(id+"F0.wireOp",EDGE,"E102.trimOffspring"),sQuery(id+"F0.wireOp",EDGE,"E103.trimOffspring"),sQuery(id+"F0.wireOp",EDGE,"E104.trimOffspring"),sQuery(id+"F0.wireOp",EDGE,"E105.trimOffspring"),sQuery(id+"F0.wireOp",EDGE,"E106.trimOffspring"),sQuery(id+"F0.wireOp",EDGE,"E107.trimOffspring"),sQuery(id+"F0.wireOp",EDGE,"E108.trimOffspring"),sQuery(id+"F0.wireOp",EDGE,"E109.trimOffspring"),sQuery(id+"F0.wireOp",EDGE,"E110.trimOffspring"),sQuery(id+"F0.wireOp",EDGE,"E111.trimOffspring"),sQuery(id+"F0.wireOp",EDGE,"E112.trimOffspring"),sQuery(id+"F0.wireOp",EDGE,"E113.trimOffspring"),sQuery(id+"F0.wireOp",EDGE,"E114.trimOffspring"),sQuery(id+"F0.wireOp",EDGE,"E115.trimOffspring"),sQuery(id+"F0.wireOp",EDGE,"E116.trimOffspring"),sQuery(id+"F0.wireOp",EDGE,"E117.trimOffspring"),sQuery(id+"F0.wireOp",EDGE,"E118.trimOffspring"),sQuery(id+"F0.wireOp",EDGE,"E119.trimOffspring"),sQuery(id+"F0.wireOp",EDGE,"E120.trimOffspring"),sQuery(id+"F0.wireOp",EDGE,"E121.trimOffspring"),sQuery(id+"F0.wireOp",EDGE,"E122.trimOffspring"),sQuery(id+"F0.wireOp",EDGE,"E123.trimOffspring"),sQuery(id+"F0.wireOp",EDGE,"E124.trimOffspring"),sQuery(id+"F0.wireOp",EDGE,"E125.trimOffspring"),sQuery(id+"F0.wireOp",EDGE,"E126.trimOffspring"),sQuery(id+"F0.wireOp",EDGE,"E127.trimOffspring"),sQuery(id+"F0.wireOp",EDGE,"E128.trimOffspring"),sQuery(id+"F0.wireOp",EDGE,"E129.trimOffspring"),sQuery(id+"F0.wireOp",EDGE,"E130.trimOffspring"),sQuery(id+"F0.wireOp",EDGE,"E131.trimOffspring"),sQuery(id+"F0.wireOp",EDGE,"E132.trimOffspring"),sQuery(id+"F0.wireOp",EDGE,"E133.trimOffspring"),sQuery(id+"F0.wireOp",EDGE,"E134.trimOffspring"),sQuery(id+"F0.wireOp",EDGE,"E135.trimOffspring"),sQuery(id+"F0.wireOp",EDGE,"E136.trimOffspring"),sQuery(id+"F0.wireOp",EDGE,"E137.trimOffspring"),sQuery(id+"F0.wireOp",EDGE,"E138.trimOffspring"),sQuery(id+"F0.wireOp",EDGE,"E139.trimOffspring"),sQuery(id+"F0.wireOp",EDGE,"E140.trimOffspring"),sQuery(id+"F0.wireOp",EDGE,"E141.trimOffspring"),sQuery(id+"F0.wireOp",EDGE,"E142.trimOffspring"),sQuery(id+"F0.wireOp",EDGE,"E143.trimOffspring"),sQuery(id+"F0.wireOp",EDGE,"E144.trimOffspring"),sQuery(id+"F0.wireOp",EDGE,"E145.trimOffspring"),sQuery(id+"F0.wireOp",EDGE,"E146.trimOffspring"),sQuery(id+"F0.wireOp",EDGE,"E147.trimOffspring"),sQuery(id+"F0.wireOp",EDGE,"E148.trimOffspring"),sQuery(id+"F0.wireOp",EDGE,"E149.trimOffspring"),sQuery(id+"F0.wireOp",EDGE,"E150.trimOffspring"),sQuery(id+"F0.wireOp",EDGE,"E151.trimOffspring"),sQuery(id+"F0.wireOp",EDGE,"E152.trimOffspring"),sQuery(id+"F0.wireOp",EDGE,"E153.trimOffspring"),sQuery(id+"F0.wireOp",EDGE,"E154.trimOffspring"),sQuery(id+"F0.wireOp",EDGE,"E155.trimOffspring"),sQuery(id+"F0.wireOp",EDGE,"E156.trimOffspring"),sQuery(id+"F0.wireOp",EDGE,"E157.trimOffspring")])],"isStart":true});
            var sketch = newSketch(context, id + "F8", { "sketchPlane" : qUnion([Q0])});
            skText(sketch, "E163", { "text": "Never forget", "fontName": "OpenSans-Bold.ttf"});
            const initialGuessF8  = {"E163": [-0.03577, -0.01976, 1, 0, 0.00738]};
            skSetInitialGuess(sketch, initialGuessF8);
            skSolve(sketch);
        }
        {
            var Q0;
            Q0 = qSketchRegion(id + "F8", true);
            extrude(context, id + "F9", {"entities" : qUnion([Q0]), "operationType" : NewBodyOperationType.REMOVE, "endBound" : BoundingType.THROUGH_ALL, "oppositeDirection" : true, "depth" : 25.4 * mm});
        }
    });
